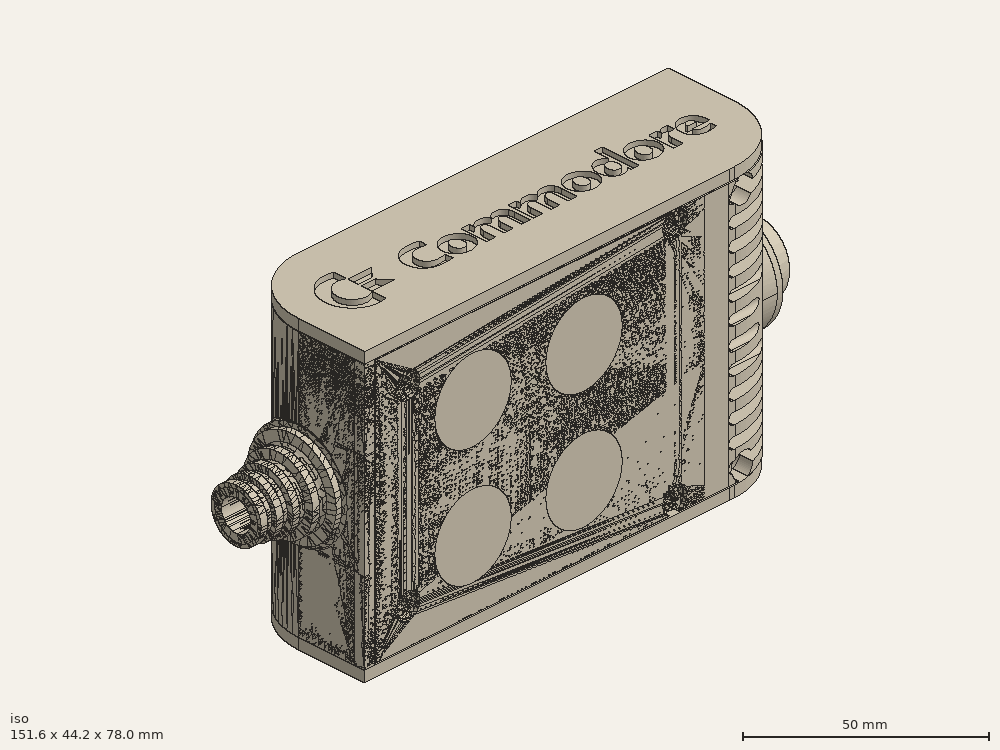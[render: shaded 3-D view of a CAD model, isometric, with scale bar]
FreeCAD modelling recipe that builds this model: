
FCSTD DOCUMENT  (FreeCAD 0.19R0.19.2)
Label: enclosure_217FCStd
License: All rights reserved
LicenseURL: http://en.wikipedia.org/wiki/All_rights_reserved
objects: Part::Revolution×152, Part::MultiFuse×146, Part::Feature×146, Sketcher::SketchObject×89, Part::Extrusion×74, Part::Cut×72, Part::Cylinder×70, Part::Fillet×58, Part::Box×36, App::MeasureDistance×4, Part::Chamfer×4, Part::FeaturePython×2, Image::ImagePlane×1, PartDesign::Body×1, Part::Mirroring×1
note: 851 computed .brp shape members not serialized (recipe doc carries the construction recipe); baked Part::Feature solids carry a one-line shape summary decoded from their .brp

FEATURE [Sketcher::SketchObject] Sketch  label="topSketch"
  FullyConstrained = true
  sketch-geometry (20):
    g0: LineSegment StartX=5.21097e-06 StartY=3 StartZ=0 EndX=5.21097e-06 EndY=19 EndZ=0
    g1: ArcOfCircle CenterX=19 CenterY=19 CenterZ=0 NormalX=0 NormalY=0 NormalZ=1 AngleXU=0 Radius=19 StartAngle=1.5708 EndAngle=3.14159
    g2: ArcOfCircle CenterX=19 CenterY=19 CenterZ=0 NormalX=0 NormalY=0 NormalZ=1 AngleXU=0 Radius=16 StartAngle=1.5708 EndAngle=3.14159
    g3: LineSegment StartX=114 StartY=35 StartZ=0 EndX=19 EndY=35 EndZ=0
    g4: LineSegment StartX=5.21097e-06 StartY=3 StartZ=0 EndX=5.21097e-06 EndY=0 EndZ=0
    g5: LineSegment StartX=3 StartY=0 StartZ=0 EndX=5.21097e-06 EndY=0 EndZ=0
    g6: LineSegment StartX=3 StartY=19 StartZ=0 EndX=3 EndY=0 EndZ=0
    g7: LineSegment StartX=19 StartY=38 StartZ=0 EndX=124 EndY=38 EndZ=0
    g8: Circle CenterX=119 CenterY=35 CenterZ=0 NormalX=0 NormalY=0 NormalZ=1 AngleXU=0 Radius=1
    g9: Circle CenterX=121 CenterY=35 CenterZ=0 NormalX=0 NormalY=0 NormalZ=1 AngleXU=0 Radius=1
    g10: Circle CenterX=121 CenterY=33 CenterZ=0 NormalX=0 NormalY=0 NormalZ=1 AngleXU=0 Radius=1
    g11: BSplineCurve PolesCount=3 KnotsCount=2 Degree=2 IsPeriodic=0
    g12: GeomPoint X=119 Y=35 Z=0
    g13: GeomPoint X=121 Y=33 Z=0
    g14: LineSegment StartX=119 StartY=35 StartZ=0 EndX=114 EndY=35 EndZ=0
    g15: ArcOfCircle CenterX=105 CenterY=19 CenterZ=0 NormalX=0 NormalY=0 NormalZ=1 AngleXU=0 Radius=19 StartAngle=5.7297 EndAngle=6.28319
    g16: ArcOfCircle CenterX=105 CenterY=19 CenterZ=0 NormalX=0 NormalY=0 NormalZ=1 AngleXU=0 Radius=16 StartAngle=5.60905 EndAngle=6.28319
    g17: LineSegment StartX=121 StartY=33 StartZ=0 EndX=121 EndY=19 EndZ=0
    g18: LineSegment StartX=124 StartY=38 StartZ=0 EndX=124 EndY=19 EndZ=0
    g19: LineSegment StartX=117.5 StartY=9.01251 StartZ=0 EndX=121.163 EndY=9.0125 EndZ=0
  constraints (46):
    c: Vertical(g0)
    c: Block(g0)
    c: Coincident(g1,g0)
    c: Block(g1)
    c: Coincident(g2,g1)
    c: Block(g2)
    c: Coincident(g3,g2)
    c: Horizontal(g3)
    c: Tangent(g3,g2)
    c: Coincident(g4,g0)
    c: Distance(g4) = 3
    c: Vertical(g4)
    c: Coincident(g5,g4)
    c: Horizontal(g5)
    c: Coincident(g6,g2)
    c: Coincident(g6,g5)
    c: Vertical(g6)
    c: Horizontal(g7)
    c: Distance(g7) = 105
    c: Coincident(g7,g1)
    c: Block(g3)
    c: Weight(g8) = 1
    c: Equal(g8,g9)
    c: Equal(g8,g10)
    c: InternalAlignment(g8,g11)
    c: InternalAlignment(g9,g11)
    c: InternalAlignment(g10,g11)
    c: InternalAlignment(g12,g11)
    c: InternalAlignment(g13,g11)
    c: Block(g11)
    c: Coincident(g14,g11)
    c: Coincident(g14,g3)
    c: Horizontal(g14)
    c: Block(g15)
    c: Coincident(g16,g15)
    c: Block(g16)
    c: Coincident(g17,g11)
    c: Coincident(g17,g16)
    c: Vertical(g17)
    c: Distance(g17) = 14
    c: Coincident(g18,g7)
    c: Coincident(g18,g15)
    c: Vertical(g18)
    c: Distance(g18) = 19
    c: Coincident(g19,g16)
    c: Coincident(g19,g15)
FEATURE [Sketcher::SketchObject] Sketch001  label="bottomSketch"
  FullyConstrained = true
  sketch-geometry (32):
    g0: LineSegment StartX=3.3 StartY=-6.03275e-07 StartZ=0 EndX=98 EndY=-6.03275e-07 EndZ=0
    g1: ArcOfCircle CenterX=98 CenterY=19 CenterZ=0 NormalX=0 NormalY=0 NormalZ=1 AngleXU=0 Radius=19 StartAngle=4.71239 EndAngle=5.71103
    g2: LineSegment StartX=6.3 StartY=8 StartZ=0 EndX=3.3 EndY=8 EndZ=0
    g3: LineSegment StartX=3.3 StartY=8 StartZ=0 EndX=3.3 EndY=-6.03275e-07 EndZ=0
    g4: ArcOfCircle CenterX=8.3 CenterY=5 CenterZ=0 NormalX=0 NormalY=0 NormalZ=1 AngleXU=0 Radius=2 StartAngle=3.14159 EndAngle=4.71239
    g5: LineSegment StartX=6.3 StartY=8 StartZ=0 EndX=6.3 EndY=5 EndZ=0
    g6: ArcOfCircle CenterX=98 CenterY=19 CenterZ=0 NormalX=0 NormalY=0 NormalZ=1 AngleXU=0 Radius=12.7 StartAngle=4.71239 EndAngle=6.28319
    g7: LineSegment StartX=94.7 StartY=3 StartZ=0 EndX=8.3 EndY=3 EndZ=0
    g8-g12: Circle x5 (B-spline internal-alignment scaffolding for g13; pole/knot coordinates omitted)
    g13: BSplineCurve PolesCount=5 KnotsCount=3 Degree=3 IsPeriodic=0
    g14: GeomPoint X=98 Y=6.3 Z=0
    g15: GeomPoint X=96.3938 Y=4.71946 Z=0
    g16: GeomPoint X=94.7 Y=3 Z=0
    g17-g23: Circle x7 (B-spline internal-alignment scaffolding for g24; pole/knot coordinates omitted)
    g24: BSplineCurve PolesCount=7 KnotsCount=5 Degree=3 IsPeriodic=0
    g25-g29: GeomPoint x5 (B-spline internal-alignment scaffolding for g24; pole/knot coordinates omitted)
    g30: ArcOfCircle CenterX=98 CenterY=19 CenterZ=0 NormalX=0 NormalY=0 NormalZ=1 AngleXU=0 Radius=15.7 StartAngle=5.81226 EndAngle=6.28319
    g31: LineSegment StartX=110.7 StartY=19 StartZ=0 EndX=113.7 EndY=19 EndZ=0
  constraints (41):
    c: Horizontal(g0)
    c: Coincident(g1,g0)
    c: Block(g1)
    c: Horizontal(g2)
    c: Distance(g2) = 3
    c: Coincident(g3,g2)
    c: Vertical(g3)
    c: Coincident(g3,g0)
    c: Block(g4)
    c: Block(g2)
    c: Coincident(g5,g2)
    c: Coincident(g5,g4)
    c: Vertical(g5)
    c: Coincident(g6,g1)
    c: Block(g6)
    c: Coincident(g7,g4)
    c: Horizontal(g7)
    c: Block(g0)
    c: Block(g7)
    c: Block(g3)
    c: Coincident(g13,g6)
    c: Weight(g8) = 1
    c: Equal(g8, g9-g12) x4
    c: Coincident(g13,g7)
    c: InternalAlignment(g8-g12 -> g13) x5
    c: InternalAlignment(g14,g13)
    c: InternalAlignment(g15,g13)
    c: InternalAlignment(g16,g13)
    c: Block(g13)
    c: Weight(g17) = 1
    c: Equal(g17, g18-g23) x6
    c: Coincident(g24,g1)
    c: InternalAlignment(g17-g23 -> g24) x7
    c: InternalAlignment(g25-g29 -> g24) x5
    c: Block(g24)
    c: Coincident(g30,g24)
    c: Coincident(g31,g6)
    c: Coincident(g31,g30)
    c: Horizontal(g31)
    c: Block(g31)
    c: Block(g30)
FEATURE [Part::Extrusion] Extrude  label="top"
  Base = -> Sketch
  Dir = (0,0,1)
  DirMode = 2
  FaceMakerClass = Part::FaceMakerBullseye
  LengthFwd = 72
  LengthRev = 0
  Solid = true
  Symmetric = false
FEATURE [Part::Extrusion] Extrude001  label="bottom"
  Base = -> Sketch001
  Dir = (0,0,1)
  DirMode = 2
  FaceMakerClass = Part::FaceMakerBullseye
  LengthFwd = 71.4
  LengthRev = 0
  Placement = pos=(0,0,0.3) rot=(0,0,1;0rad)
  Solid = true
  Symmetric = false
FEATURE [Sketcher::SketchObject] Sketch002  label="topSketch001"
  FullyConstrained = true
  sketch-geometry (8):
    g0: ArcOfCircle CenterX=19 CenterY=19.0975 CenterZ=0 NormalX=0 NormalY=0 NormalZ=1 AngleXU=0 Radius=18.9025 StartAngle=1.5708 EndAngle=3.14674
    g1: LineSegment StartX=0.0977805 StartY=19.0003 StartZ=0 EndX=0.0977805 EndY=0.000251602 EndZ=0
    g2: LineSegment StartX=19 StartY=38 StartZ=0 EndX=124 EndY=38 EndZ=0
    g3: LineSegment StartX=0.0977805 StartY=0.000251602 StartZ=0 EndX=105.098 EndY=0.000251602 EndZ=0
    g4: LineSegment StartX=124 StartY=38 StartZ=0 EndX=125.616 EndY=38 EndZ=0
    g5: LineSegment StartX=105.098 StartY=0.000251602 StartZ=0 EndX=106.713 EndY=0.000251602 EndZ=0
    g6: ArcOfCircle CenterX=106.616 CenterY=19 CenterZ=0 NormalX=0 NormalY=0 NormalZ=1 AngleXU=0 Radius=19 StartAngle=4.71754 EndAngle=6.28319
    g7: LineSegment StartX=125.616 StartY=38 StartZ=0 EndX=125.616 EndY=19 EndZ=0
  constraints (21):
    c: Block(g0)
    c: Coincident(g1,g0)
    c: Vertical(g1)
    c: Horizontal(g2)
    c: Distance(g2) = 105
    c: Coincident(g2,g0)
    c: Distance(g1) = 19
    c: Coincident(g3,g1)
    c: Horizontal(g3)
    c: Distance(g3) = 105
    c: Coincident(g4,g2)
    c: Horizontal(g4)
    c: Distance(g4) = 1.61553
    c: Horizontal(g5)
    c: Equal(g4,g5) = 1.61553
    c: Coincident(g5,g3)
    c: Block(g6)
    c: Coincident(g6,g5)
    c: Coincident(g7,g4)
    c: Coincident(g7,g6)
    c: Vertical(g7)
FEATURE [Part::Extrusion] Extrude002  label="sideA"
  Base = -> Sketch002
  Dir = (0,0,1)
  DirMode = 2
  FaceMakerClass = Part::FaceMakerBullseye
  LengthFwd = 3
  LengthRev = 0
  Placement = pos=(0,0,-3) rot=(0,0,1;0rad)
  Solid = true
  Symmetric = false
FEATURE [Sketcher::SketchObject] Sketch003  label="topSketch002"
  FullyConstrained = true
  sketch-geometry (6):
    g0: LineSegment StartX=19 StartY=38 StartZ=0 EndX=117 EndY=38 EndZ=0
    g1: ArcOfCircle CenterX=19 CenterY=19 CenterZ=0 NormalX=0 NormalY=0 NormalZ=1 AngleXU=0 Radius=19 StartAngle=1.5708 EndAngle=3.14159
    g2: LineSegment StartX=117 StartY=38 StartZ=0 EndX=117 EndY=19 EndZ=0
    g3: LineSegment StartX=98 StartY=1.0161e-12 StartZ=0 EndX=5.22862e-06 EndY=1.0161e-12 EndZ=0
    g4: LineSegment StartX=5.22862e-06 StartY=19 StartZ=0 EndX=5.22862e-06 EndY=1.0161e-12 EndZ=0
    g5: ArcOfCircle CenterX=98 CenterY=19 CenterZ=0 NormalX=0 NormalY=0 NormalZ=1 AngleXU=0 Radius=19 StartAngle=4.71239 EndAngle=6.28319
  constraints (16):
    c: Horizontal(g0)
    c: Distance(g0) = 98
    c: Coincident(g1,g0)
    c: Block(g1)
    c: Coincident(g2,g0)
    c: Vertical(g2)
    c: Distance(g2) = 19
    c: Horizontal(g3)
    c: Coincident(g4,g1)
    c: Vertical(g4)
    c: Coincident(g3,g4)
    c: Block(g3)
    c: Coincident(g5,g2)
    c: Coincident(g5,g3)
    c: Block(g0)
    c: Block(g5)
FEATURE [Sketcher::SketchObject] Sketch004
  FullyConstrained = true
  MapMode = 3
  Placement = pos=(0,0,0) rot=(1,0,0;1.5708rad)
  Support = -> [Extrude]
  sketch-geometry (8):
    g0: Circle CenterX=80.351 CenterY=-67.6202 CenterZ=0 NormalX=0 NormalY=0 NormalZ=1 AngleXU=0 Radius=2
    g1: Circle CenterX=80.351 CenterY=-67.6202 CenterZ=0 NormalX=0 NormalY=0 NormalZ=1 AngleXU=0 Radius=3
    g2: Circle CenterX=80.351 CenterY=-4.92017 CenterZ=0 NormalX=0 NormalY=0 NormalZ=1 AngleXU=0 Radius=2
    g3: Circle CenterX=80.351 CenterY=-4.92017 CenterZ=0 NormalX=0 NormalY=0 NormalZ=1 AngleXU=0 Radius=3
    g4: Circle CenterX=23.851 CenterY=-4.92017 CenterZ=0 NormalX=0 NormalY=0 NormalZ=1 AngleXU=0 Radius=2
    g5: Circle CenterX=23.851 CenterY=-4.92017 CenterZ=0 NormalX=0 NormalY=0 NormalZ=1 AngleXU=0 Radius=3
    g6: Circle CenterX=23.851 CenterY=-67.6202 CenterZ=0 NormalX=0 NormalY=0 NormalZ=1 AngleXU=0 Radius=2
    g7: Circle CenterX=23.851 CenterY=-67.6202 CenterZ=0 NormalX=0 NormalY=0 NormalZ=1 AngleXU=0 Radius=3
  constraints (8):
    c: Block(g3)
    c: Block(g2)
    c: Block(g1)
    c: Block(g0)
    c: Block(g6)
    c: Block(g7)
    c: Block(g4)
    c: Block(g5)
FEATURE [Part::Extrusion] Extrude004
  Base = -> Sketch004
  Dir = (0,-1,2e-16)
  DirMode = 2
  FaceMakerClass = Part::FaceMakerBullseye
  LengthFwd = 6
  LengthRev = 0
  Placement = pos=(0,9,0) rot=(0,0,1;0rad)
  Solid = true
  Symmetric = false
FEATURE [Sketcher::SketchObject] Sketch005
  FullyConstrained = true
  MapMode = 3
  Placement = pos=(0,0,0) rot=(1,0,0;1.5708rad)
  Support = -> [Extrude]
  sketch-geometry (8):
    g0: Circle CenterX=80.351 CenterY=-67.6202 CenterZ=0 NormalX=0 NormalY=0 NormalZ=1 AngleXU=0 Radius=3
    g1: Circle CenterX=80.351 CenterY=-4.92017 CenterZ=0 NormalX=0 NormalY=0 NormalZ=1 AngleXU=0 Radius=3
    g2: Circle CenterX=23.851 CenterY=-4.92017 CenterZ=0 NormalX=0 NormalY=0 NormalZ=1 AngleXU=0 Radius=3
    g3: Circle CenterX=23.851 CenterY=-67.6202 CenterZ=0 NormalX=0 NormalY=0 NormalZ=1 AngleXU=0 Radius=3
    g4: Circle CenterX=23.851 CenterY=-67.6202 CenterZ=0 NormalX=0 NormalY=0 NormalZ=1 AngleXU=0 Radius=5
    g5: Circle CenterX=80.351 CenterY=-67.6202 CenterZ=0 NormalX=0 NormalY=0 NormalZ=1 AngleXU=0 Radius=5
    g6: Circle CenterX=23.851 CenterY=-4.92017 CenterZ=0 NormalX=0 NormalY=0 NormalZ=1 AngleXU=0 Radius=5
    g7: Circle CenterX=80.351 CenterY=-4.92017 CenterZ=0 NormalX=0 NormalY=0 NormalZ=1 AngleXU=0 Radius=5
  constraints (8):
    c: Block(g1)
    c: Block(g0)
    c: Block(g3)
    c: Block(g2)
    c: Block(g5)
    c: Block(g4)
    c: Block(g6)
    c: Block(g7)
FEATURE [Part::Extrusion] Extrude005
  Base = -> Sketch005
  Dir = (0,-1,2e-16)
  DirMode = 2
  FaceMakerClass = Part::FaceMakerBullseye
  LengthFwd = 2
  LengthRev = 0
  Solid = true
  Symmetric = false
FEATURE [Sketcher::SketchObject] Sketch006
  FullyConstrained = true
  MapMode = 3
  Placement = pos=(0,0,0) rot=(1,0,0;1.5708rad)
  sketch-geometry (8):
    g0: Circle CenterX=80.351 CenterY=-67.6202 CenterZ=0 NormalX=0 NormalY=0 NormalZ=1 AngleXU=0 Radius=3
    g1: Circle CenterX=80.351 CenterY=-4.92017 CenterZ=0 NormalX=0 NormalY=0 NormalZ=1 AngleXU=0 Radius=3
    g2: Circle CenterX=23.851 CenterY=-4.92017 CenterZ=0 NormalX=0 NormalY=0 NormalZ=1 AngleXU=0 Radius=3
    g3: Circle CenterX=23.851 CenterY=-67.6202 CenterZ=0 NormalX=0 NormalY=0 NormalZ=1 AngleXU=0 Radius=3
    g4: Circle CenterX=23.851 CenterY=-67.6202 CenterZ=0 NormalX=0 NormalY=0 NormalZ=1 AngleXU=0 Radius=5
    g5: Circle CenterX=80.351 CenterY=-67.6202 CenterZ=0 NormalX=0 NormalY=0 NormalZ=1 AngleXU=0 Radius=5
    g6: Circle CenterX=23.851 CenterY=-4.92017 CenterZ=0 NormalX=0 NormalY=0 NormalZ=1 AngleXU=0 Radius=5
    g7: Circle CenterX=80.351 CenterY=-4.92017 CenterZ=0 NormalX=0 NormalY=0 NormalZ=1 AngleXU=0 Radius=5
  constraints (8):
    c: Block(g1)
    c: Block(g0)
    c: Block(g3)
    c: Block(g2)
    c: Block(g5)
    c: Block(g4)
    c: Block(g6)
    c: Block(g7)
FEATURE [Part::Extrusion] Extrude007
  Base = -> Sketch006
  Dir = (0,-1,2e-16)
  DirMode = 2
  FaceMakerClass = Part::FaceMakerBullseye
  LengthFwd = 2
  LengthRev = 0
  Solid = true
  Symmetric = false
FEATURE [Part::Fillet] Fillet
  Base = -> Extrude007
  Edges = 4 edges r=1.99: [Edge6,Edge12,Edge18,Edge24]
FEATURE [Part::Cut] Cut
  Base = -> Extrude005
  Placement = pos=(0,5,0) rot=(0,0,1;0rad)
  Tool = -> Fillet
FEATURE [Part::MultiFuse] Fusion  label="pCBScrews"
  Placement = pos=(-2.5,0,72.3) rot=(0,0,1;0rad)
  Shapes = -> [Extrude004,Cut]
FEATURE [App::MeasureDistance] Distance  label="Distance: 0.69 mm"
  Distance = 0.685967
  P1 = (24.0138,2.9647,0.3)
  P2 = (23.8901,3,-0.373787)
FEATURE [App::MeasureDistance] Distance001  label="Distance: 0.53 mm"
  Distance = 0.533607
  P1 = (80.2939,3,72.2334)
  P2 = (80.281,2.99661,71.7)
FEATURE [Part::Fillet] Fillet001
  Base = -> Extrude001
  Edges = 1 edges r=2.4: [Edge17]
FEATURE [Part::Fillet] Fillet002  label="bottom001"
  Base = -> Fillet001
  Edges = 1 edges r=2.4: [Edge36]
FEATURE [Part::Fillet] Fillet003  label="top001"
  Base = -> Extrude
  Edges = 1 edges r=2: [Edge1]
FEATURE [Sketcher::SketchObject] Sketch007
  FullyConstrained = true
  sketch-geometry (16):
    g0: LineSegment StartX=4 StartY=0 StartZ=0 EndX=4 EndY=2.4 EndZ=0
    g1: LineSegment StartX=4 StartY=2.4 StartZ=0 EndX=7 EndY=2.4 EndZ=0
    g2: LineSegment StartX=4 StartY=0 StartZ=0 EndX=5.7 EndY=0 EndZ=0
    g3: LineSegment StartX=5.7 StartY=0 StartZ=0 EndX=5.7 EndY=-5.6 EndZ=0
    g4-g8: Circle x5 (B-spline internal-alignment scaffolding for g9; pole/knot coordinates omitted)
    g9: BSplineCurve PolesCount=5 KnotsCount=3 Degree=3 IsPeriodic=0
    g10: GeomPoint X=7 Y=2.4 Z=0
    g11: GeomPoint X=10.4582 Y=-1.55472 Z=0
    g12: GeomPoint X=14 Y=-5.6 Z=0
    g13: LineSegment StartX=14 StartY=-5.6 StartZ=0 EndX=14 EndY=-14.1 EndZ=0
    g14: LineSegment StartX=14 StartY=-14.1 StartZ=0 EndX=6.5 EndY=-14.1 EndZ=0
    g15: LineSegment StartX=5.7 StartY=-5.6 StartZ=0 EndX=6.5 EndY=-14.1 EndZ=0
  constraints (28):
    c: Distance(g0) = 2.4
    c: Vertical(g0)
    c: Block(g0)
    c: Coincident(g1,g0)
    c: Horizontal(g1)
    c: Distance(g1) = 3
    c: Coincident(g2,g0)
    c: Horizontal(g2)
    c: Distance(g2) = 1.7
    c: Coincident(g3,g2)
    c: Vertical(g3)
    c: Distance(g3) = 5.6
    c: Coincident(g9,g1)
    c: Weight(g4) = 1
    c: Equal(g4, g5-g8) x4
    c: InternalAlignment(g4-g8 -> g9) x5
    c: InternalAlignment(g10,g9)
    c: InternalAlignment(g11,g9)
    c: InternalAlignment(g12,g9)
    c: Block(g9)
    c: Coincident(g13,g9)
    c: Vertical(g13)
    c: Distance(g13) = 8.5
    c: Coincident(g14,g13)
    c: Horizontal(g14)
    c: Distance(g14) = 7.5
    c: Coincident(g15,g3)
    c: Coincident(g15,g14)
FEATURE [Part::Feature] Face
  shape: bbox 10 x 16.5 x 2e-07 mm, 1 faces, 0 solids (baked)
FEATURE [Part::Revolution] Revolve  label="plugHousing"
  Angle = 360
  Axis = (0,1,0)
  Base = (0,0,0)
  FaceMakerClass = Part::FaceMakerBullseye
  Placement = pos=(0,0,36.15) rot=(0,0,1;0rad)
  Solid = false
  Source = -> Face
  Symmetric = false
FEATURE [Part::Feature] Face001
  shape: bbox 10 x 16.5 x 2e-07 mm, 1 faces, 0 solids (baked)
FEATURE [Part::Revolution] Revolve001  label="plugHousing001"
  Angle = 360
  Axis = (0,1,0)
  Base = (0,0,0)
  FaceMakerClass = Part::FaceMakerBullseye
  Placement = pos=(0,0,36.15) rot=(0,0,1;0rad)
  Solid = false
  Source = -> Face001
  Symmetric = false
FEATURE [Part::MultiFuse] Fusion001  label="plugHousing002"
  Placement = pos=(0,0,0) rot=(0,0,1;1.5708rad)
  Shapes = -> [Revolve001,Revolve]
FEATURE [Part::Feature] Face002
  shape: bbox 10 x 16.5 x 2e-07 mm, 1 faces, 0 solids (baked)
FEATURE [Part::Revolution] Revolve003  label="plugHousing005"
  Angle = 360
  Axis = (0,1,0)
  Base = (0,0,0)
  FaceMakerClass = Part::FaceMakerBullseye
  Placement = pos=(0,0,36.15) rot=(0,0,1;0rad)
  Solid = false
  Source = -> Face002
  Symmetric = false
FEATURE [Part::Feature] Face003
  shape: bbox 10 x 16.5 x 2e-07 mm, 1 faces, 0 solids (baked)
FEATURE [Part::Revolution] Revolve002  label="plugHousing003"
  Angle = 360
  Axis = (0,1,0)
  Base = (0,0,0)
  FaceMakerClass = Part::FaceMakerBullseye
  Placement = pos=(0,0,36.15) rot=(0,0,1;0rad)
  Solid = false
  Source = -> Face003
  Symmetric = false
FEATURE [Part::MultiFuse] Fusion002  label="plugHousing004"
  Placement = pos=(0,0,0) rot=(0,0,1;1.5708rad)
  Shapes = -> [Revolve002,Revolve003]
FEATURE [Part::MultiFuse] Fusion003  label="plugHousing006"
  Placement = pos=(0,19,0) rot=(0,0,1;3.14159rad)
  Shapes = -> [Fusion002,Fusion001]
FEATURE [Part::Feature] Face004
  shape: bbox 10 x 16.5 x 2e-07 mm, 1 faces, 0 solids (baked)
FEATURE [Part::Revolution] Revolve006  label="plugHousing010"
  Angle = 360
  Axis = (0,1,0)
  Base = (0,0,0)
  FaceMakerClass = Part::FaceMakerBullseye
  Placement = pos=(0,0,36.15) rot=(0,0,1;0rad)
  Solid = false
  Source = -> Face004
  Symmetric = false
FEATURE [Part::Feature] Face005
  shape: bbox 10 x 16.5 x 2e-07 mm, 1 faces, 0 solids (baked)
FEATURE [Part::Revolution] Revolve007  label="plugHousing011"
  Angle = 360
  Axis = (0,1,0)
  Base = (0,0,0)
  FaceMakerClass = Part::FaceMakerBullseye
  Placement = pos=(0,0,36.15) rot=(0,0,1;0rad)
  Solid = false
  Source = -> Face005
  Symmetric = false
FEATURE [Part::Feature] Face006
  shape: bbox 10 x 16.5 x 2e-07 mm, 1 faces, 0 solids (baked)
FEATURE [Part::Revolution] Revolve004  label="plugHousing007"
  Angle = 360
  Axis = (0,1,0)
  Base = (0,0,0)
  FaceMakerClass = Part::FaceMakerBullseye
  Placement = pos=(0,0,36.15) rot=(0,0,1;0rad)
  Solid = false
  Source = -> Face006
  Symmetric = false
FEATURE [Part::MultiFuse] Fusion004  label="plugHousing009"
  Placement = pos=(0,0,0) rot=(0,0,1;1.5708rad)
  Shapes = -> [Revolve004,Revolve007]
FEATURE [Part::Feature] Face007
  shape: bbox 10 x 16.5 x 2e-07 mm, 1 faces, 0 solids (baked)
FEATURE [Part::Revolution] Revolve005  label="plugHousing008"
  Angle = 360
  Axis = (0,1,0)
  Base = (0,0,0)
  FaceMakerClass = Part::FaceMakerBullseye
  Placement = pos=(0,0,36.15) rot=(0,0,1;0rad)
  Solid = false
  Source = -> Face007
  Symmetric = false
FEATURE [Part::MultiFuse] Fusion005  label="plugHousing012"
  Placement = pos=(0,0,0) rot=(0,0,1;1.5708rad)
  Shapes = -> [Revolve006,Revolve005]
FEATURE [Part::MultiFuse] Fusion006  label="plugHousing013"
  Placement = pos=(0,19,0) rot=(0,0,1;3.14159rad)
  Shapes = -> [Fusion005,Fusion004]
FEATURE [Part::MultiFuse] Fusion007  label="plugHousing014"
  Placement = pos=(122.621,0,-0.15) rot=(0,0,1;0rad)
  Shapes = -> [Fusion003,Fusion006]
FEATURE [Part::Cylinder] Cylinder002
  Angle = 360
  AttacherType = Attacher::AttachEngine3D
  Height = 20
  Placement = pos=(0,0,36.15) rot=(0,0,1;0rad)
  Radius = 4
FEATURE [Part::Cylinder] Cylinder003
  Angle = 360
  AttacherType = Attacher::AttachEngine3D
  Height = 10
  Placement = pos=(0,0,36.15) rot=(0,0,1;0rad)
  Radius = 4
FEATURE [Part::MultiFuse] Fusion009  label="removeToCreateHoleForPlugHousing"
  Placement = pos=(70,19,36.15) rot=(0,1,0;1.5708rad)
  Shapes = -> [Cylinder002,Cylinder003]
FEATURE [Part::Cylinder] Cylinder004
  Angle = 360
  AttacherType = Attacher::AttachEngine3D
  Height = 20
  Placement = pos=(0,0,36.15) rot=(0,0,1;0rad)
  Radius = 4
FEATURE [Part::Cylinder] Cylinder005
  Angle = 360
  AttacherType = Attacher::AttachEngine3D
  Height = 10
  Placement = pos=(0,0,36.15) rot=(0,0,1;0rad)
  Radius = 4
FEATURE [Part::MultiFuse] Fusion010  label="removeToCreateHoleForPlugHousing001"
  Placement = pos=(70,19,36.15) rot=(0,1,0;1.5708rad)
  Shapes = -> [Cylinder004,Cylinder005]
FEATURE [Part::Cut] Cut001
  Base = -> Fillet003
  Tool = -> Fusion010
FEATURE [Part::Cut] Cut002  label="Bottom"
  Base = -> Fillet002
  Tool = -> Fusion009
FEATURE [Part::Feature] Face008
  shape: bbox 10 x 16.5 x 2e-07 mm, 1 faces, 0 solids (baked)
FEATURE [Part::Revolution] Revolve011  label="plugHousing021"
  Angle = 360
  Axis = (0,1,0)
  Base = (0,0,0)
  FaceMakerClass = Part::FaceMakerBullseye
  Placement = pos=(0,0,36.15) rot=(0,0,1;0rad)
  Solid = false
  Source = -> Face008
  Symmetric = false
FEATURE [Part::Feature] Face009
  shape: bbox 10 x 16.5 x 2e-07 mm, 1 faces, 0 solids (baked)
FEATURE [Part::Revolution] Revolve012  label="plugHousing022"
  Angle = 360
  Axis = (0,1,0)
  Base = (0,0,0)
  FaceMakerClass = Part::FaceMakerBullseye
  Placement = pos=(0,0,36.15) rot=(0,0,1;0rad)
  Solid = false
  Source = -> Face009
  Symmetric = false
FEATURE [Part::Feature] Face010 .. Face013  x4 (patterned run collapsed; names and placements below)
  shape: bbox 10 x 16.5 x 2e-07 mm, 1 faces, 0 solids (baked)
FEATURE [Part::Revolution] Revolve015  label="plugHousing027"
  Angle = 360
  Axis = (0,1,0)
  Base = (0,0,0)
  FaceMakerClass = Part::FaceMakerBullseye
  Placement = pos=(0,0,36.15) rot=(0,0,1;0rad)
  Solid = false
  Source = -> Face013
  Symmetric = false
FEATURE [Part::Feature] Face014
  shape: bbox 10 x 16.5 x 2e-07 mm, 1 faces, 0 solids (baked)
FEATURE [Part::Feature] Face015
  shape: bbox 10 x 16.5 x 2e-07 mm, 1 faces, 0 solids (baked)
FEATURE [Part::Feature] Face016
  shape: bbox 10 x 16.5 x 2e-07 mm, 1 faces, 0 solids (baked)
FEATURE [Part::Revolution] Revolve019  label="plugHousing033"
  Angle = 360
  Axis = (0,1,0)
  Base = (0,0,0)
  FaceMakerClass = Part::FaceMakerBullseye
  Placement = pos=(0,0,36.15) rot=(0,0,1;0rad)
  Solid = false
  Source = -> Face016
  Symmetric = false
FEATURE [Part::Feature] Face017
  shape: bbox 10 x 16.5 x 2e-07 mm, 1 faces, 0 solids (baked)
FEATURE [Part::Revolution] Revolve020  label="plugHousing034"
  Angle = 360
  Axis = (0,1,0)
  Base = (0,0,0)
  FaceMakerClass = Part::FaceMakerBullseye
  Placement = pos=(0,0,36.15) rot=(0,0,1;0rad)
  Solid = false
  Source = -> Face017
  Symmetric = false
FEATURE [Part::Feature] Face018
  shape: bbox 10 x 16.5 x 2e-07 mm, 1 faces, 0 solids (baked)
FEATURE [Part::Revolution] Revolve016  label="plugHousing030"
  Angle = 360
  Axis = (0,1,0)
  Base = (0,0,0)
  FaceMakerClass = Part::FaceMakerBullseye
  Placement = pos=(0,0,36.15) rot=(0,0,1;0rad)
  Solid = false
  Source = -> Face018
  Symmetric = false
FEATURE [Part::MultiFuse] Fusion020  label="plugHousing038"
  Placement = pos=(0,0,0) rot=(0,0,1;1.5708rad)
  Shapes = -> [Revolve016,Revolve020]
FEATURE [Part::Feature] Face019
  shape: bbox 10 x 16.5 x 2e-07 mm, 1 faces, 0 solids (baked)
FEATURE [Part::Feature] Face020
  shape: bbox 10 x 16.5 x 2e-07 mm, 1 faces, 0 solids (baked)
FEATURE [Part::Revolution] Revolve017  label="plugHousing031"
  Angle = 360
  Axis = (0,1,0)
  Base = (0,0,0)
  FaceMakerClass = Part::FaceMakerBullseye
  Placement = pos=(0,0,36.15) rot=(0,0,1;0rad)
  Solid = false
  Source = -> Face020
  Symmetric = false
FEATURE [Part::MultiFuse] Fusion021  label="plugHousing039"
  Placement = pos=(0,0,0) rot=(0,0,1;1.5708rad)
  Shapes = -> [Revolve019,Revolve017]
FEATURE [Part::MultiFuse] Fusion023  label="plugHousing041"
  Placement = pos=(0,19,0) rot=(0,0,1;3.14159rad)
  Shapes = -> [Fusion021,Fusion020]
FEATURE [Part::Revolution] Revolve022  label="plugHousing043"
  Angle = 360
  Axis = (0,1,0)
  Base = (0,0,0)
  FaceMakerClass = Part::FaceMakerBullseye
  Placement = pos=(0,0,36.15) rot=(0,0,1;0rad)
  Solid = false
  Source = -> Face019
  Symmetric = false
FEATURE [Part::Feature] Face021
  shape: bbox 10 x 16.5 x 2e-07 mm, 1 faces, 0 solids (baked)
FEATURE [Part::Revolution] Revolve023  label="plugHousing044"
  Angle = 360
  Axis = (0,1,0)
  Base = (0,0,0)
  FaceMakerClass = Part::FaceMakerBullseye
  Placement = pos=(0,0,36.15) rot=(0,0,1;0rad)
  Solid = false
  Source = -> Face021
  Symmetric = false
FEATURE [Part::Feature] Face022
  shape: bbox 10 x 16.5 x 2e-07 mm, 1 faces, 0 solids (baked)
FEATURE [Part::Revolution] Revolve018  label="plugHousing032"
  Angle = 360
  Axis = (0,1,0)
  Base = (0,0,0)
  FaceMakerClass = Part::FaceMakerBullseye
  Placement = pos=(0,0,36.15) rot=(0,0,1;0rad)
  Solid = false
  Source = -> Face022
  Symmetric = false
FEATURE [Part::MultiFuse] Fusion022  label="plugHousing040"
  Placement = pos=(0,0,0) rot=(0,0,1;1.5708rad)
  Shapes = -> [Revolve018,Revolve023]
FEATURE [Part::Feature] Face023
  shape: bbox 10 x 16.5 x 2e-07 mm, 1 faces, 0 solids (baked)
FEATURE [Part::Revolution] Revolve021  label="plugHousing035"
  Angle = 360
  Axis = (0,1,0)
  Base = (0,0,0)
  FaceMakerClass = Part::FaceMakerBullseye
  Placement = pos=(0,0,36.15) rot=(0,0,1;0rad)
  Solid = false
  Source = -> Face023
  Symmetric = false
FEATURE [Part::MultiFuse] Fusion018  label="plugHousing036"
  Placement = pos=(0,0,0) rot=(0,0,1;1.5708rad)
  Shapes = -> [Revolve022,Revolve021]
FEATURE [Part::MultiFuse] Fusion019  label="plugHousing037"
  Placement = pos=(0,19,0) rot=(0,0,1;3.14159rad)
  Shapes = -> [Fusion018,Fusion022]
FEATURE [Part::MultiFuse] Fusion024  label="plugHousing042"
  Placement = pos=(122.621,0,-0.15) rot=(0,0,1;0rad)
  Shapes = -> [Fusion023,Fusion019]
FEATURE [Part::Cylinder] Cylinder006
  Angle = 360
  AttacherType = Attacher::AttachEngine3D
  Height = 20
  Placement = pos=(0,0,36.15) rot=(0,0,1;0rad)
  Radius = 14.3
FEATURE [Part::Cylinder] Cylinder007
  Angle = 360
  AttacherType = Attacher::AttachEngine3D
  Height = 10
  Placement = pos=(0,0,36.15) rot=(0,0,1;0rad)
  Radius = 4
FEATURE [Part::MultiFuse] Fusion026  label="removeToCreteHoleForPlugHousing"
  Placement = pos=(70,19,36) rot=(0,1,0;1.5708rad)
  Shapes = -> [Cylinder006,Cylinder007]
FEATURE [Part::Box] Box001  label="Cube001"
  AttacherType = Attacher::AttachEngine3D
  Height = 28
  Length = 3
  Placement = pos=(110.7,19,22) rot=(0,0,1;0rad)
  Width = 15.7
FEATURE [Part::Cut] Cut003  label="top002"
  Base = -> Cut001
  Tool = -> Fusion007
FEATURE [Part::Revolution] Revolve008  label="plugHousing015"
  Angle = 360
  Axis = (0,1,0)
  Base = (0,0,0)
  FaceMakerClass = Part::FaceMakerBullseye
  Placement = pos=(0,0,36.15) rot=(0,0,1;0rad)
  Solid = false
  Source = -> Face010
  Symmetric = false
FEATURE [Part::MultiFuse] Fusion013  label="plugHousing020"
  Placement = pos=(0,0,0) rot=(0,0,1;1.5708rad)
  Shapes = -> [Revolve008,Revolve012]
FEATURE [Part::Cut] Cut004  label="top003"
  Base = -> Cut003
  Placement = pos=(1,0,0) rot=(0,0,1;0rad)
  Tool = -> Fusion026
FEATURE [Part::Cylinder] Cylinder008
  Angle = 360
  AttacherType = Attacher::AttachEngine3D
  Height = 20
  Placement = pos=(0,0,36.15) rot=(0,0,1;0rad)
  Radius = 10.3
FEATURE [Part::Cylinder] Cylinder009
  Angle = 360
  AttacherType = Attacher::AttachEngine3D
  Height = 10
  Placement = pos=(0,0,36.15) rot=(0,0,1;0rad)
  Radius = 4
FEATURE [Part::MultiFuse] Fusion027  label="removeToCreteHoleForPlugHousing001"
  Placement = pos=(70,19,36) rot=(0,1,0;1.5708rad)
  Shapes = -> [Cylinder008,Cylinder009]
FEATURE [Part::Cut] Cut005  label="plugHousingTab"
  Base = -> Box001
  Tool = -> Fusion027
FEATURE [Part::MultiFuse] Fusion028  label="plugHousing045"
  Shapes = -> [Fusion024,Cut005]
FEATURE [Part::Box] Box002  label="Cube002"
  AttacherType = Attacher::AttachEngine3D
  Height = 28.8
  Length = 3
  Placement = pos=(107.3,28,21.6) rot=(0,0,1;0rad)
  Width = 7
FEATURE [Part::Box] Box003  label="Cube003"
  AttacherType = Attacher::AttachEngine3D
  Height = 3
  Length = 6.4
  Placement = pos=(107.3,28,18.6) rot=(0,0,1;0rad)
  Width = 7
FEATURE [Part::Box] Box004  label="Cube004"
  AttacherType = Attacher::AttachEngine3D
  Height = 3
  Length = 6.4
  Placement = pos=(107.3,28,50.4) rot=(0,0,1;0rad)
  Width = 7
FEATURE [Part::MultiFuse] Fusion029  label="plugHousingBracketHolder"
  Shapes = -> [Box004,Box002,Box003]
FEATURE [Part::Cylinder] Cylinder010
  Angle = 360
  AttacherType = Attacher::AttachEngine3D
  Height = 20
  Placement = pos=(0,0,36.15) rot=(0,0,1;0rad)
  Radius = 14.3
FEATURE [Part::Cylinder] Cylinder011
  Angle = 360
  AttacherType = Attacher::AttachEngine3D
  Height = 10
  Placement = pos=(0,0,36.15) rot=(0,0,1;0rad)
  Radius = 4
FEATURE [Part::MultiFuse] Fusion030  label="removeToCreteHoleForPlugHousing002"
  Placement = pos=(70,19,36) rot=(0,1,0;1.5708rad)
  Shapes = -> [Cylinder010,Cylinder011]
FEATURE [Part::Cut] Cut006  label="plugHousingBracketHolder001"
  Base = -> Fusion029
  Tool = -> Fusion030
FEATURE [Part::Cylinder] Cylinder012
  Angle = 360
  AttacherType = Attacher::AttachEngine3D
  Height = 20
  Placement = pos=(0,0,36.15) rot=(0,0,1;0rad)
  Radius = 7
FEATURE [Part::Cylinder] Cylinder013
  Angle = 360
  AttacherType = Attacher::AttachEngine3D
  Height = 10
  Placement = pos=(0,0,36.15) rot=(0,0,1;0rad)
  Radius = 4
FEATURE [Part::MultiFuse] Fusion032  label="removeToCreteHoleForPlugHousing003"
  Placement = pos=(70,19,36) rot=(0,1,0;1.5708rad)
  Shapes = -> [Cylinder012,Cylinder013]
FEATURE [Part::Cut] Cut007  label="bottom002"
  Base = -> Cut002
  Tool = -> Fusion032
FEATURE [Sketcher::SketchObject] Sketch008
  FullyConstrained = true
  sketch-geometry (54):
    g0: LineSegment StartX=-4.2 StartY=0 StartZ=0 EndX=-6.2 EndY=0 EndZ=0
    g1: LineSegment StartX=-14 StartY=-18 StartZ=0 EndX=-14 EndY=-26.5 EndZ=0
    g2: LineSegment StartX=-4.2 StartY=0 StartZ=0 EndX=-4.2 EndY=-13.4877 EndZ=0
    g3: Circle CenterX=-4.2 CenterY=-13.4877 CenterZ=0 NormalX=0 NormalY=0 NormalZ=1 AngleXU=0 Radius=1
    g4: Circle CenterX=-4.2 CenterY=-26.5 CenterZ=0 NormalX=0 NormalY=0 NormalZ=1 AngleXU=0 Radius=1
    g5: Circle CenterX=-8.2 CenterY=-26.5 CenterZ=0 NormalX=0 NormalY=0 NormalZ=1 AngleXU=0 Radius=1
    g6: BSplineCurve PolesCount=3 KnotsCount=2 Degree=2 IsPeriodic=0
    g7: GeomPoint X=-4.2 Y=-13.4877 Z=0
    g8: GeomPoint X=-8.2 Y=-26.5 Z=0
    g9: LineSegment StartX=-14 StartY=-26.5 StartZ=0 EndX=-8.2 EndY=-26.5 EndZ=0
    g10: LineSegment StartX=-10.15 StartY=-12 StartZ=0 EndX=-10.15 EndY=-14 EndZ=0
    g11: LineSegment StartX=-12.8401 StartY=-16 StartZ=0 EndX=-10.1571 EndY=-16 EndZ=0
    g12: LineSegment StartX=-10.15 StartY=-14 StartZ=0 EndX=-8.70761 EndY=-14 EndZ=0
    g13: LineSegment StartX=-12.8401 StartY=-16 StartZ=0 EndX=-12.8401 EndY=-17.6958 EndZ=0
    g14: LineSegment StartX=-10.15 StartY=-12 StartZ=0 EndX=-7.79258 EndY=-12 EndZ=0
    g15: Circle CenterX=-6.2215 CenterY=-2 CenterZ=0 NormalX=0 NormalY=0 NormalZ=1 AngleXU=0 Radius=1
    g16: Circle CenterX=-6.22762 CenterY=-2.58724 CenterZ=0 NormalX=0 NormalY=0 NormalZ=1 AngleXU=0 Radius=1
    g17: Circle CenterX=-6.32538 CenterY=-4 CenterZ=0 NormalX=0 NormalY=0 NormalZ=1 AngleXU=0 Radius=1
    g18: BSplineCurve PolesCount=3 KnotsCount=2 Degree=2 IsPeriodic=0
    g19: GeomPoint X=-6.2215 Y=-2 Z=0
    g20: GeomPoint X=-6.32538 Y=-4 Z=0
    g21: Circle CenterX=-6.48644 CenterY=-5.99526 CenterZ=0 NormalX=0 NormalY=0 NormalZ=1 AngleXU=0 Radius=1
    g22: Circle CenterX=-6.58486 CenterY=-6.99526 CenterZ=0 NormalX=0 NormalY=0 NormalZ=1 AngleXU=0 Radius=1
    g23: Circle CenterX=-6.77343 CenterY=-8 CenterZ=0 NormalX=0 NormalY=0 NormalZ=1 AngleXU=0 Radius=1
    g24: BSplineCurve PolesCount=3 KnotsCount=2 Degree=2 IsPeriodic=0
    g25: GeomPoint X=-6.48644 Y=-5.99526 Z=0
    g26: GeomPoint X=-6.77343 Y=-8 Z=0
    g27: Circle CenterX=-7.19003 CenterY=-10 CenterZ=0 NormalX=0 NormalY=0 NormalZ=1 AngleXU=0 Radius=1
    g28: Circle CenterX=-7.44407 CenterY=-11.0915 CenterZ=0 NormalX=0 NormalY=0 NormalZ=1 AngleXU=0 Radius=1
    g29: Circle CenterX=-7.79258 CenterY=-12 CenterZ=0 NormalX=0 NormalY=0 NormalZ=1 AngleXU=0 Radius=1
    g30: BSplineCurve PolesCount=3 KnotsCount=2 Degree=2 IsPeriodic=0
    g31: GeomPoint X=-7.19003 Y=-10 Z=0
    g32: GeomPoint X=-7.79258 Y=-12 Z=0
    g33: Circle CenterX=-8.70761 CenterY=-14 CenterZ=0 NormalX=0 NormalY=0 NormalZ=1 AngleXU=0 Radius=1
    g34: Circle CenterX=-9.33087 CenterY=-15.1837 CenterZ=0 NormalX=0 NormalY=0 NormalZ=1 AngleXU=0 Radius=1
    g35: Circle CenterX=-10.1571 CenterY=-16 CenterZ=0 NormalX=0 NormalY=0 NormalZ=1 AngleXU=0 Radius=1
    g36: BSplineCurve PolesCount=3 KnotsCount=2 Degree=2 IsPeriodic=0
    g37: GeomPoint X=-8.70761 Y=-14 Z=0
    g38: GeomPoint X=-10.1571 Y=-16 Z=0
    g39: Circle CenterX=-12.8401 CenterY=-17.6958 CenterZ=0 NormalX=0 NormalY=0 NormalZ=1 AngleXU=0 Radius=1
    g40: Circle CenterX=-13.3521 CenterY=-17.9027 CenterZ=0 NormalX=0 NormalY=0 NormalZ=1 AngleXU=0 Radius=1
    g41: Circle CenterX=-14 CenterY=-18 CenterZ=0 NormalX=0 NormalY=0 NormalZ=1 AngleXU=0 Radius=1
    g42: BSplineCurve PolesCount=3 KnotsCount=2 Degree=2 IsPeriodic=0
    g43: GeomPoint X=-12.8401 Y=-17.6958 Z=0
    g44: GeomPoint X=-14 Y=-18 Z=0
    g45: LineSegment StartX=-6.2 StartY=0 StartZ=0 EndX=-7.2 EndY=0 EndZ=0
    g46: LineSegment StartX=-7.2 StartY=0 StartZ=0 EndX=-7.2 EndY=-2 EndZ=0
    g47: LineSegment StartX=-7.2 StartY=-2 StartZ=0 EndX=-6.2215 EndY=-2 EndZ=0
    g48: LineSegment StartX=-6.32538 StartY=-4 StartZ=0 EndX=-7.65538 EndY=-4 EndZ=0
    g49: LineSegment StartX=-7.65538 StartY=-4 StartZ=0 EndX=-7.65538 EndY=-5.99526 EndZ=0
    g50: LineSegment StartX=-7.65538 StartY=-5.99526 StartZ=0 EndX=-6.48644 EndY=-5.99526 EndZ=0
    g51: LineSegment StartX=-6.77343 StartY=-8 StartZ=0 EndX=-8.43343 EndY=-8 EndZ=0
    g52: LineSegment StartX=-8.43343 StartY=-8 StartZ=0 EndX=-8.43343 EndY=-10 EndZ=0
    g53: LineSegment StartX=-8.43343 StartY=-10 StartZ=0 EndX=-7.19003 EndY=-10 EndZ=0
  constraints (112):
    c: Horizontal(g0)
    c: Distance(g0) = 2
    c: Block(g0)
    c: Vertical(g1)
    c: Coincident(g2,g0)
    c: Vertical(g2)
    c: Block(g2)
    c: Coincident(g6,g2)
    c: Weight(g3) = 1
    c: Equal(g3,g4)
    c: Equal(g3,g5)
    c: InternalAlignment(g3,g6)
    c: InternalAlignment(g4,g6)
    c: InternalAlignment(g5,g6)
    c: InternalAlignment(g7,g6)
    c: InternalAlignment(g8,g6)
    c: Block(g6)
    c: Coincident(g9,g1)
    c: Coincident(g9,g6)
    c: Horizontal(g9)
    c: Vertical(g10)
    c: Block(g10)
    c: Horizontal(g11)
    c: Block(g11)
    c: Coincident(g12,g10)
    c: Horizontal(g12)
    c: Block(g12)
    c: Coincident(g13,g11)
    c: Vertical(g13)
    c: Block(g13)
    c: Coincident(g14,g10)
    c: Horizontal(g14)
    c: Block(g14)
    c: Block(g9)
    c: Block(g1)
    c: Weight(g15) = 1
    c: Equal(g15,g16)
    c: Equal(g15,g17)
    c: InternalAlignment(g15,g18)
    c: InternalAlignment(g16,g18)
    c: InternalAlignment(g17,g18)
    c: InternalAlignment(g19,g18)
    c: InternalAlignment(g20,g18)
    c: Weight(g21) = 1
    c: Equal(g21,g22)
    c: Equal(g21,g23)
    c: InternalAlignment(g21,g24)
    c: InternalAlignment(g22,g24)
    c: InternalAlignment(g23,g24)
    c: InternalAlignment(g25,g24)
    c: InternalAlignment(g26,g24)
    c: Weight(g27) = 1
    c: Equal(g27,g28)
    c: Equal(g27,g29)
    c: Coincident(g30,g14)
    c: InternalAlignment(g27,g30)
    c: InternalAlignment(g28,g30)
    c: InternalAlignment(g29,g30)
    c: InternalAlignment(g31,g30)
    c: InternalAlignment(g32,g30)
    c: Coincident(g36,g12)
    c: Weight(g33) = 1
    c: Equal(g33,g34)
    c: Equal(g33,g35)
    c: Coincident(g36,g11)
    c: InternalAlignment(g33,g36)
    c: InternalAlignment(g34,g36)
    c: InternalAlignment(g35,g36)
    c: InternalAlignment(g37,g36)
    c: InternalAlignment(g38,g36)
    c: Coincident(g42,g13)
    c: Weight(g39) = 1
    c: Equal(g39,g40)
    c: Equal(g39,g41)
    c: Coincident(g42,g1)
    c: InternalAlignment(g39,g42)
    c: InternalAlignment(g40,g42)
    c: InternalAlignment(g41,g42)
    c: InternalAlignment(g43,g42)
    c: InternalAlignment(g44,g42)
    c: Block(g18)
    c: Block(g24)
    c: Block(g30)
    c: Block(g36)
    c: Block(g42)
    c: Horizontal(g45)
    c: Coincident(g45,g0)
    c: Vertical(g46)
    c: Coincident(g46,g45)
    c: Coincident(g47,g46)
    c: Coincident(g47,g18)
    c: Horizontal(g47)
    c: Block(g46)
    c: Coincident(g48,g18)
    c: Horizontal(g48)
    c: Distance(g48) = 1.33
    c: Vertical(g49)
    c: Coincident(g49,g48)
    c: Coincident(g50,g49)
    c: Coincident(g50,g24)
    c: Horizontal(g50)
    c: Tangent(g50,g22)
    c: Horizontal(g51)
    c: Coincident(g51,g24)
    c: Block(g51)
    c: Vertical(g52)
    c: Block(g52)
    c: Coincident(g52,g51)
    c: Coincident(g53,g52)
    c: Coincident(g53,g30)
    c: Horizontal(g53)
    c: Distance(g1) = 8.5
FEATURE [Part::Feature] Face024
  shape: bbox 9.8 x 26.5 x 2e-07 mm, 1 faces, 0 solids (baked)
FEATURE [Part::Revolution] Revolve024
  Angle = 360
  Axis = (0,1,0)
  Base = (0,0,0)
  FaceMakerClass = Part::FaceMakerBullseye
  Placement = pos=(0,0,0) rot=(0,0,1;1.5708rad)
  Solid = false
  Source = -> Face024
  Symmetric = false
FEATURE [Part::Feature] Face025
  shape: bbox 9.8 x 26.5 x 2e-07 mm, 1 faces, 0 solids (baked)
FEATURE [Part::Revolution] Revolve025
  Angle = 360
  Axis = (0,1,0)
  Base = (0,0,0)
  FaceMakerClass = Part::FaceMakerBullseye
  Placement = pos=(0,0,0) rot=(0,0,1;1.5708rad)
  Solid = false
  Source = -> Face025
  Symmetric = false
FEATURE [Part::MultiFuse] Fusion033
  Placement = pos=(-18,19,36) rot=(0,0,1;0rad)
  Shapes = -> [Revolve025,Revolve024]
FEATURE [Part::Cylinder] Cylinder014
  Angle = 360
  AttacherType = Attacher::AttachEngine3D
  Height = 20
  Placement = pos=(0,0,36.15) rot=(0,0,1;0rad)
  Radius = 14.3
FEATURE [Part::Cylinder] Cylinder015
  Angle = 360
  AttacherType = Attacher::AttachEngine3D
  Height = 10
  Placement = pos=(0,0,36.15) rot=(0,0,1;0rad)
  Radius = 4
FEATURE [Part::MultiFuse] Fusion034  label="removeToCreteHoleForPlugHousing004"
  Placement = pos=(-42,19,36) rot=(0,1,0;1.5708rad)
  Shapes = -> [Cylinder014,Cylinder015]
FEATURE [Part::Cut] Cut008  label="top004"
  Base = -> Cut004
  Placement = pos=(-1,0,0) rot=(0,0,1;0rad)
  Tool = -> Fusion034
FEATURE [Part::Box] Box005  label="Cube005"
  AttacherType = Attacher::AttachEngine3D
  Height = 28
  Length = 3
  Placement = pos=(110.7,19,22) rot=(0,0,1;0rad)
  Width = 15.7
FEATURE [Part::Cylinder] Cylinder016
  Angle = 360
  AttacherType = Attacher::AttachEngine3D
  Height = 10
  Placement = pos=(0,0,36.15) rot=(0,0,1;0rad)
  Radius = 4
FEATURE [Part::Cylinder] Cylinder017
  Angle = 360
  AttacherType = Attacher::AttachEngine3D
  Height = 20
  Placement = pos=(0,0,36.15) rot=(0,0,1;0rad)
  Radius = 10.3
FEATURE [Part::MultiFuse] Fusion035  label="removeToCreteHoleForPlugHousing005"
  Placement = pos=(70,19,36) rot=(0,1,0;1.5708rad)
  Shapes = -> [Cylinder017,Cylinder016]
FEATURE [Part::Cut] Cut009  label="plugHousingTab001"
  Base = -> Box005
  Placement = pos=(-107.4,-14,0) rot=(0,0,1;0rad)
  Tool = -> Fusion035
FEATURE [Part::Box] Box006  label="Cube006"
  AttacherType = Attacher::AttachEngine3D
  Height = 28
  Length = 3
  Placement = pos=(110.7,19,22) rot=(0,0,1;0rad)
  Width = 15.7
FEATURE [Part::Cylinder] Cylinder018
  Angle = 360
  AttacherType = Attacher::AttachEngine3D
  Height = 10
  Placement = pos=(0,0,36.15) rot=(0,0,1;0rad)
  Radius = 4
FEATURE [Part::Cylinder] Cylinder019
  Angle = 360
  AttacherType = Attacher::AttachEngine3D
  Height = 20
  Placement = pos=(0,0,36.15) rot=(0,0,1;0rad)
  Radius = 10.3
FEATURE [Part::MultiFuse] Fusion036  label="removeToCreteHoleForPlugHousing006"
  Placement = pos=(70,19,36) rot=(0,1,0;1.5708rad)
  Shapes = -> [Cylinder019,Cylinder018]
FEATURE [Part::Cut] Cut010  label="plugHousingTab002"
  Base = -> Box006
  Placement = pos=(-107.4,-14,0) rot=(0,0,1;0rad)
  Tool = -> Fusion036
FEATURE [Part::MultiFuse] Fusion037
  Placement = pos=(9.6,23,0) rot=(0,0,1;3.14159rad)
  Shapes = -> [Cut009,Cut010]
FEATURE [Part::Box] Box  label="Cube"
  AttacherType = Attacher::AttachEngine3D
  Height = 10
  Length = 3
  Placement = pos=(3.3,4,12) rot=(0,0,1;0rad)
  Width = 10
FEATURE [Part::Fillet] Fillet004
  Base = -> Fusion028
  Edges = 1 edges r=2: [Edge25]
FEATURE [Part::Fillet] Fillet005  label="plugHousing046"
  Base = -> Fillet004
  Edges = 1 edges r=2: [Edge8]
FEATURE [Part::Fillet] Fillet006
  Base = -> Box
  Edges = 1 edges r=2: [Edge11]
FEATURE [Part::Box] Box007  label="Cube007"
  AttacherType = Attacher::AttachEngine3D
  Height = 10
  Length = 3
  Placement = pos=(3.3,4,50) rot=(0,0,1;0rad)
  Width = 10
FEATURE [Part::Fillet] Fillet007
  Base = -> Box007
  Edges = 1 edges r=2: [Edge12]
FEATURE [Part::Box] Box008  label="Cube008"
  AttacherType = Attacher::AttachEngine3D
  Height = 28
  Length = 4
  Placement = pos=(5,0,22) rot=(0,0,1;0rad)
  Width = 10
FEATURE [Part::Fillet] Fillet008
  Base = -> Box008
  Edges = 1 edges r=1: [Edge7]
FEATURE [Part::Fillet] Fillet009
  Base = -> Fillet008
  Edges = 1 edges r=2: [Edge5]
FEATURE [Part::Fillet] Fillet010
  Base = -> Fillet009
  Edges = 1 edges r=2: [Edge2]
FEATURE [Sketcher::SketchObject] Sketch009  label="topSketch003"
  FullyConstrained = true
  sketch-geometry (4):
    g0: LineSegment StartX=16.8446 StartY=31.512 StartZ=0 EndX=16.3251 EndY=34.4666 EndZ=0
    g1: ArcOfCircle CenterX=19 CenterY=19.2524 CenterZ=0 NormalX=0 NormalY=0 NormalZ=1 AngleXU=0 Radius=15.4476 StartAngle=1.74483 EndAngle=2.72717
    g2: ArcOfCircle CenterX=19 CenterY=19.2524 CenterZ=0 NormalX=0 NormalY=0 NormalZ=1 AngleXU=0 Radius=12.4476 StartAngle=1.74483 EndAngle=2.73189
    g3: LineSegment StartX=4.86004 StartY=25.4725 StartZ=0 EndX=7.58253 EndY=24.2107 EndZ=0
  constraints (7):
    c: Block(g0)
    c: Coincident(g1,g0)
    c: Coincident(g2,g0)
    c: Coincident(g3,g1)
    c: Coincident(g3,g2)
    c: Block(g1)
    c: Block(g2)
FEATURE [Part::Extrusion] Extrude008
  Base = -> Sketch009
  Dir = (0,0,1)
  DirMode = 2
  FaceMakerClass = Part::FaceMakerBullseye
  LengthFwd = 10
  LengthRev = 0
  Placement = pos=(0,0,31) rot=(0,0,1;0rad)
  Solid = true
  Symmetric = false
FEATURE [Part::Cylinder] Cylinder020
  Angle = 360
  AttacherType = Attacher::AttachEngine3D
  Height = 20
  Placement = pos=(0,0,36.15) rot=(0,0,1;0rad)
  Radius = 8.2
FEATURE [Part::Cylinder] Cylinder021
  Angle = 360
  AttacherType = Attacher::AttachEngine3D
  Height = 10
  Placement = pos=(0,0,36.15) rot=(0,0,1;0rad)
  Radius = 4
FEATURE [Part::MultiFuse] Fusion038  label="removeToCreteHoleForPlugHousing007"
  Placement = pos=(-42,19,36) rot=(0,1,0;1.5708rad)
  Shapes = -> [Cylinder020,Cylinder021]
FEATURE [Part::Cut] Cut011
  Base = -> Extrude008
  Tool = -> Fusion038
FEATURE [Part::Fillet] Fillet011
  Base = -> Cut011
  Edges = 1 edges r=2: [Edge1]
FEATURE [Part::Fillet] Fillet012
  Base = -> Fillet011
  Edges = 1 edges r=2.5: [Edge1]
FEATURE [Part::Fillet] Fillet013
  Base = -> Fillet012
  Edges = 1 edges r=2.5: [Edge2]
FEATURE [Part::Box] Box010  label="Cube010"
  AttacherType = Attacher::AttachEngine3D
  Height = 16
  Length = 8
  Placement = pos=(12.7,31.52,28) rot=(0,0,1;0rad)
  Width = 4
FEATURE [Sketcher::SketchObject] Sketch010  label="topSketch004"
  FullyConstrained = true
  sketch-geometry (4):
    g0: LineSegment StartX=16.8446 StartY=31.512 StartZ=0 EndX=16.3251 EndY=34.4666 EndZ=0
    g1: ArcOfCircle CenterX=19 CenterY=19.2524 CenterZ=0 NormalX=0 NormalY=0 NormalZ=1 AngleXU=0 Radius=15.4476 StartAngle=1.74483 EndAngle=2.72717
    g2: ArcOfCircle CenterX=19 CenterY=19.2524 CenterZ=0 NormalX=0 NormalY=0 NormalZ=1 AngleXU=0 Radius=12.4476 StartAngle=1.74483 EndAngle=2.73189
    g3: LineSegment StartX=4.86004 StartY=25.4725 StartZ=0 EndX=7.58253 EndY=24.2107 EndZ=0
  constraints (7):
    c: Block(g0)
    c: Coincident(g1,g0)
    c: Coincident(g2,g0)
    c: Coincident(g3,g1)
    c: Coincident(g3,g2)
    c: Block(g1)
    c: Block(g2)
FEATURE [Part::Cylinder] Cylinder022
  Angle = 360
  AttacherType = Attacher::AttachEngine3D
  Height = 10
  Placement = pos=(0,0,36.15) rot=(0,0,1;0rad)
  Radius = 4
FEATURE [Sketcher::SketchObject] Sketch011  label="topSketch005"
  FullyConstrained = true
  sketch-geometry (4):
    g0: LineSegment StartX=16.8446 StartY=31.512 StartZ=0 EndX=16.3251 EndY=34.4666 EndZ=0
    g1: ArcOfCircle CenterX=19 CenterY=19.2524 CenterZ=0 NormalX=0 NormalY=0 NormalZ=1 AngleXU=0 Radius=15.4476 StartAngle=1.74483 EndAngle=2.72717
    g2: ArcOfCircle CenterX=19 CenterY=19.2524 CenterZ=0 NormalX=0 NormalY=0 NormalZ=1 AngleXU=0 Radius=12.4476 StartAngle=1.74483 EndAngle=2.73189
    g3: LineSegment StartX=4.86004 StartY=25.4725 StartZ=0 EndX=7.58253 EndY=24.2107 EndZ=0
  constraints (7):
    c: Block(g0)
    c: Coincident(g1,g0)
    c: Coincident(g2,g0)
    c: Coincident(g3,g1)
    c: Coincident(g3,g2)
    c: Block(g1)
    c: Block(g2)
FEATURE [Part::Extrusion] Extrude010
  Base = -> Sketch011
  Dir = (0,0,1)
  DirMode = 2
  FaceMakerClass = Part::FaceMakerBullseye
  LengthFwd = 10.6
  LengthRev = 0
  Placement = pos=(0,0,31) rot=(0,0,1;0rad)
  Solid = true
  Symmetric = false
FEATURE [Part::Cylinder] Cylinder023
  Angle = 360
  AttacherType = Attacher::AttachEngine3D
  Height = 20
  Placement = pos=(0,0,36.15) rot=(0,0,1;0rad)
  Radius = 8.2
FEATURE [Part::MultiFuse] Fusion039  label="removeToCreteHoleForPlugHousing008"
  Placement = pos=(-42,19,36) rot=(0,1,0;1.5708rad)
  Shapes = -> [Cylinder023,Cylinder022]
FEATURE [Part::Cut] Cut012
  Base = -> Extrude010
  Placement = pos=(0,0,-0.3) rot=(0,0,1;0rad)
  Tool = -> Fusion039
FEATURE [Part::Cut] Cut013
  Base = -> Box010
  Tool = -> Cut012
FEATURE [Part::Fillet] Fillet014
  Base = -> Cut013
  Edges = 1 edges r=0.7: [Edge13]
FEATURE [Part::Fillet] Fillet015
  Base = -> Fillet014
  Edges = 1 edges r=0.7: [Edge13]
FEATURE [Part::Fillet] Fillet016
  Base = -> Fillet015
  Edges = 1 edges r=0.7: [Edge16]
FEATURE [Part::Fillet] Fillet017
  Base = -> Fillet016
  Edges = 1 edges r=0.7: [Edge11]
FEATURE [Part::Fillet] Fillet018
  Base = -> Fillet017
  Edges = 1 edges r=0.7: [Edge10]
FEATURE [Part::Fillet] Fillet019
  Base = -> Fillet018
  Edges = 1 edges r=1.2: [Edge5]
FEATURE [Part::Fillet] Fillet020
  Base = -> Fillet019
  Edges = 1 edges r=1.2: [Edge12]
FEATURE [Part::Fillet] Fillet021
  Base = -> Fillet020
  Edges = 1 edges r=2: [Edge1]
  Placement = pos=(0.3,0,0) rot=(0,0,1;0rad)
FEATURE [Part::MultiFuse] Fusion040  label="top005"
  Shapes = -> [Cut008,Fillet021]
FEATURE [Part::MultiFuse] Fusion041  label="wireHolder"
  Shapes = -> [Fusion033,Fillet013]
FEATURE [Part::MultiFuse] Fusion042
  Shapes = -> [Fillet007,Fusion041]
FEATURE [Part::MultiFuse] Fusion043  label="wireHolder001"
  Shapes = -> [Fusion042,Fillet010]
FEATURE [Part::MultiFuse] Fusion044  label="wireHolder002"
  Shapes = -> [Fillet006,Fusion037,Fusion043]
FEATURE [Part::Feature] Face026
  shape: bbox 11 x 6 x 2e-07 mm, 1 faces, 0 solids (baked)
FEATURE [Part::Revolution] Revolve026
  Angle = 360
  Axis = (0,1,0)
  Base = (0,0,0)
  FaceMakerClass = Part::FaceMakerBullseye
  Placement = pos=(30.3,-1,19.7) rot=(0,0,1;0rad)
  Solid = false
  Source = -> Face026
  Symmetric = false
FEATURE [Sketcher::SketchObject] Sketch013  label="topSketch006"
  FullyConstrained = true
  sketch-geometry (13):
    g0: LineSegment StartX=117 StartY=19 StartZ=0 EndX=117 EndY=38 EndZ=0
    g1: ArcOfCircle CenterX=98 CenterY=19 CenterZ=0 NormalX=0 NormalY=0 NormalZ=1 AngleXU=0 Radius=19 StartAngle=5.7297 EndAngle=6.28319
    g2: LineSegment StartX=0 StartY=3 StartZ=0 EndX=0 EndY=19 EndZ=0
    g3: LineSegment StartX=19 StartY=38 StartZ=0 EndX=117 EndY=38 EndZ=0
    g4: ArcOfCircle CenterX=19 CenterY=19 CenterZ=0 NormalX=0 NormalY=0 NormalZ=1 AngleXU=0 Radius=19 StartAngle=1.5708 EndAngle=3.14159
    g5: ArcOfCircle CenterX=19 CenterY=19 CenterZ=0 NormalX=0 NormalY=0 NormalZ=1 AngleXU=0 Radius=16 StartAngle=1.5708 EndAngle=3.14159
    g6: ArcOfCircle CenterX=98 CenterY=19 CenterZ=0 NormalX=0 NormalY=0 NormalZ=1 AngleXU=0 Radius=16 StartAngle=5.60905 EndAngle=6.28319
    g7: LineSegment StartX=114 StartY=19 StartZ=0 EndX=114 EndY=35 EndZ=0
    g8: LineSegment StartX=110.5 StartY=9.01251 StartZ=0 EndX=114.163 EndY=9.01251 EndZ=0
    g9: LineSegment StartX=114 StartY=35 StartZ=0 EndX=19 EndY=35 EndZ=0
    g10: LineSegment StartX=0 StartY=3 StartZ=0 EndX=0 EndY=0 EndZ=0
    g11: LineSegment StartX=3 StartY=0 StartZ=0 EndX=0 EndY=0 EndZ=0
    g12: LineSegment StartX=3 StartY=19 StartZ=0 EndX=3 EndY=0 EndZ=0
  constraints (33):
    c: Vertical(g0)
    c: Distance(g0) = 19
    c: Block(g0)
    c: Coincident(g1,g0)
    c: Block(g1)
    c: Vertical(g2)
    c: Block(g2)
    c: Coincident(g3,g0)
    c: Horizontal(g3)
    c: Distance(g3) = 98
    c: Coincident(g4,g3)
    c: Coincident(g4,g2)
    c: Block(g4)
    c: Coincident(g5,g4)
    c: Coincident(g6,g1)
    c: Block(g6)
    c: Block(g5)
    c: Coincident(g7,g6)
    c: Vertical(g7)
    c: Coincident(g8,g6)
    c: Coincident(g8,g1)
    c: Coincident(g9,g7)
    c: Coincident(g9,g5)
    c: Horizontal(g9)
    c: Tangent(g9,g5)
    c: Coincident(g10,g2)
    c: Distance(g10) = 3
    c: Vertical(g10)
    c: Coincident(g11,g10)
    c: Horizontal(g11)
    c: Coincident(g12,g5)
    c: Coincident(g12,g11)
    c: Vertical(g12)
FEATURE [Part::Extrusion] Extrude011  label="top006"
  Base = -> Sketch013
  Dir = (0,0,1)
  DirMode = 2
  FaceMakerClass = Part::FaceMakerBullseye
  LengthFwd = 72
  LengthRev = 0
  Solid = true
  Symmetric = false
FEATURE [Sketcher::SketchObject] Sketch014
  FullyConstrained = true
  MapMode = 3
  Placement = pos=(0,0,0) rot=(1,0,0;1.5708rad)
  Support = -> [Extrude011]
  sketch-geometry (8):
    g0: Circle CenterX=80.351 CenterY=-67.6202 CenterZ=0 NormalX=0 NormalY=0 NormalZ=1 AngleXU=0 Radius=2
    g1: Circle CenterX=80.351 CenterY=-67.6202 CenterZ=0 NormalX=0 NormalY=0 NormalZ=1 AngleXU=0 Radius=3
    g2: Circle CenterX=80.351 CenterY=-4.92017 CenterZ=0 NormalX=0 NormalY=0 NormalZ=1 AngleXU=0 Radius=2
    g3: Circle CenterX=80.351 CenterY=-4.92017 CenterZ=0 NormalX=0 NormalY=0 NormalZ=1 AngleXU=0 Radius=3
    g4: Circle CenterX=23.851 CenterY=-4.92017 CenterZ=0 NormalX=0 NormalY=0 NormalZ=1 AngleXU=0 Radius=2
    g5: Circle CenterX=23.851 CenterY=-4.92017 CenterZ=0 NormalX=0 NormalY=0 NormalZ=1 AngleXU=0 Radius=3
    g6: Circle CenterX=23.851 CenterY=-67.6202 CenterZ=0 NormalX=0 NormalY=0 NormalZ=1 AngleXU=0 Radius=2
    g7: Circle CenterX=23.851 CenterY=-67.6202 CenterZ=0 NormalX=0 NormalY=0 NormalZ=1 AngleXU=0 Radius=3
  constraints (8):
    c: Block(g3)
    c: Block(g2)
    c: Block(g1)
    c: Block(g0)
    c: Block(g6)
    c: Block(g7)
    c: Block(g4)
    c: Block(g5)
FEATURE [Part::Feature] Face027
  shape: bbox 11 x 6 x 2e-07 mm, 1 faces, 0 solids (baked)
FEATURE [Part::Revolution] Revolve027
  Angle = 360
  Axis = (0,1,0)
  Base = (0,0,0)
  FaceMakerClass = Part::FaceMakerBullseye
  Placement = pos=(30.3,-1,51.7) rot=(0,0,1;0rad)
  Solid = false
  Source = -> Face027
  Symmetric = false
FEATURE [Part::Feature] Face028
  shape: bbox 11 x 6 x 2e-07 mm, 1 faces, 0 solids (baked)
FEATURE [Part::Revolution] Revolve028
  Angle = 360
  Axis = (0,1,0)
  Base = (0,0,0)
  FaceMakerClass = Part::FaceMakerBullseye
  Placement = pos=(62.3,-1,19.7) rot=(0,0,1;0rad)
  Solid = false
  Source = -> Face028
  Symmetric = false
FEATURE [Part::Feature] Face029
  shape: bbox 11 x 6 x 2e-07 mm, 1 faces, 0 solids (baked)
FEATURE [Part::Revolution] Revolve029
  Angle = 360
  Axis = (0,1,0)
  Base = (0,0,0)
  FaceMakerClass = Part::FaceMakerBullseye
  Placement = pos=(62.3,-1,51.7) rot=(0,0,1;0rad)
  Solid = false
  Source = -> Face029
  Symmetric = false
FEATURE [Part::Feature] Wire
  shape: bbox 11 x 5.2 x 2e-07 mm, 0 faces, 0 solids (baked)
FEATURE [Part::Revolution] Revolve030
  Angle = 360
  Axis = (0,1,0)
  Base = (0,0,0)
  FaceMakerClass = Part::FaceMakerBullseye
  Placement = pos=(30.3,38,19.7) rot=(0,0,1;0rad)
  Solid = true
  Source = -> Wire
  Symmetric = false
FEATURE [Part::Feature] Wire001
  shape: bbox 11 x 5.2 x 2e-07 mm, 0 faces, 0 solids (baked)
FEATURE [Part::Revolution] Revolve031
  Angle = 360
  Axis = (0,1,0)
  Base = (0,0,0)
  FaceMakerClass = Part::FaceMakerBullseye
  Placement = pos=(30.3,38,51.7) rot=(0,0,1;0rad)
  Solid = true
  Source = -> Wire001
  Symmetric = false
FEATURE [Part::Feature] Wire002
  shape: bbox 11 x 5.2 x 2e-07 mm, 0 faces, 0 solids (baked)
FEATURE [Part::Revolution] Revolve032
  Angle = 360
  Axis = (0,1,0)
  Base = (0,0,0)
  FaceMakerClass = Part::FaceMakerBullseye
  Placement = pos=(62.3,38,51.7) rot=(0,0,1;0rad)
  Solid = true
  Source = -> Wire002
  Symmetric = false
FEATURE [Part::Feature] Wire003
  shape: bbox 11 x 5.2 x 2e-07 mm, 0 faces, 0 solids (baked)
FEATURE [Part::Revolution] Revolve033
  Angle = 360
  Axis = (0,1,0)
  Base = (0,0,0)
  FaceMakerClass = Part::FaceMakerBullseye
  Placement = pos=(62.3,38,19.7) rot=(0,0,1;0rad)
  Solid = true
  Source = -> Wire003
  Symmetric = false
FEATURE [Part::MultiFuse] Fusion045  label="altRandScrewHousing"
  Shapes = -> [Revolve029,Revolve027,Revolve028,Revolve026]
FEATURE [Part::MultiFuse] Fusion046  label="fanScrewHousing"
  Shapes = -> [Revolve033,Revolve032,Revolve031,Revolve030]
FEATURE [Sketcher::SketchObject] Sketch015
  FullyConstrained = true
  sketch-geometry (17):
    g0: Circle CenterX=-3.5 CenterY=23.5 CenterZ=0 NormalX=0 NormalY=0 NormalZ=1 AngleXU=0 Radius=1
    g1: Circle CenterX=-1 CenterY=15.25 CenterZ=0 NormalX=0 NormalY=0 NormalZ=1 AngleXU=0 Radius=1
    g2: Circle CenterX=-3.5 CenterY=7 CenterZ=0 NormalX=0 NormalY=0 NormalZ=1 AngleXU=0 Radius=1
    g3: BSplineCurve PolesCount=3 KnotsCount=2 Degree=2 IsPeriodic=0
    g4: GeomPoint X=-3.5 Y=23.5 Z=0
    g5: GeomPoint X=-3.5 Y=7 Z=0
    g6: Circle CenterX=-4.8 CenterY=30.5 CenterZ=0 NormalX=0 NormalY=0 NormalZ=1 AngleXU=0 Radius=1
    g7: Circle CenterX=-3.5 CenterY=30.5 CenterZ=0 NormalX=0 NormalY=0 NormalZ=1 AngleXU=0 Radius=1
    g8: Circle CenterX=-3.5 CenterY=29.2 CenterZ=0 NormalX=0 NormalY=0 NormalZ=1 AngleXU=0 Radius=1
    g9: BSplineCurve PolesCount=3 KnotsCount=2 Degree=2 IsPeriodic=0
    g10: GeomPoint X=-4.8 Y=30.5 Z=0
    g11: GeomPoint X=-3.5 Y=29.2 Z=0
    g12: LineSegment StartX=-3.5 StartY=29.2 StartZ=0 EndX=-3.5 EndY=23.5 EndZ=0
    g13: LineSegment StartX=-4.8 StartY=30.5 StartZ=0 EndX=0 EndY=30.5 EndZ=0
    g14: LineSegment StartX=-3.5 StartY=0.3 StartZ=0 EndX=0 EndY=0.3 EndZ=0
    g15: LineSegment StartX=-3.5 StartY=0.3 StartZ=0 EndX=-3.5 EndY=7 EndZ=0
    g16: LineSegment StartX=0 StartY=0.3 StartZ=0 EndX=0 EndY=30.5 EndZ=0
  constraints (34):
    c: Weight(g0) = 1
    c: Equal(g0,g1)
    c: Equal(g0,g2)
    c: InternalAlignment(g0,g3)
    c: InternalAlignment(g1,g3)
    c: InternalAlignment(g2,g3)
    c: InternalAlignment(g4,g3)
    c: InternalAlignment(g5,g3)
    c: Block(g3)
    c: Weight(g6) = 1
    c: Equal(g6,g7)
    c: Equal(g6,g8)
    c: InternalAlignment(g6,g9)
    c: InternalAlignment(g7,g9)
    c: InternalAlignment(g8,g9)
    c: InternalAlignment(g10,g9)
    c: InternalAlignment(g11,g9)
    c: Block(g9)
    c: Coincident(g12,g9)
    c: Coincident(g12,g3)
    c: Vertical(g12)
    c: Coincident(g13,g9)
    c: Horizontal(g13)
    c: Distance(g13) = 4.8
    c: Horizontal(g14)
    c: Block(g14)
    c: Coincident(g15,g14)
    c: Coincident(g15,g3)
    c: Vertical(g15)
    c: Coincident(g16,g14)
    c: Coincident(g16,g13)
    c: Vertical(g16)
    c: Tangent(g16,g1)
    c: Distance(g14) = 3.5
FEATURE [Sketcher::SketchObject] Sketch016
  FullyConstrained = true
  sketch-geometry (16):
    g0: Circle CenterX=-3.5 CenterY=23.5 CenterZ=0 NormalX=0 NormalY=0 NormalZ=1 AngleXU=0 Radius=1
    g1: Circle CenterX=-1 CenterY=15.25 CenterZ=0 NormalX=0 NormalY=0 NormalZ=1 AngleXU=0 Radius=1
    g2: Circle CenterX=-3.5 CenterY=7 CenterZ=0 NormalX=0 NormalY=0 NormalZ=1 AngleXU=0 Radius=1
    g3: BSplineCurve PolesCount=3 KnotsCount=2 Degree=2 IsPeriodic=0
    g4: GeomPoint X=-3.5 Y=23.5 Z=0
    g5: GeomPoint X=-3.5 Y=7 Z=0
    g6: LineSegment StartX=-3.5 StartY=28.2 StartZ=0 EndX=-3.5 EndY=23.5 EndZ=0
    g7: LineSegment StartX=0 StartY=29.5 StartZ=0 EndX=0 EndY=30 EndZ=0
    g8: LineSegment StartX=-3.5 StartY=28.2 StartZ=0 EndX=-3.5 EndY=30 EndZ=0
    g9: LineSegment StartX=0 StartY=30 StartZ=0 EndX=0 EndY=30.5 EndZ=0
    g10: LineSegment StartX=0 StartY=30.5 StartZ=0 EndX=-3.5 EndY=30.5 EndZ=0
    g11: LineSegment StartX=-3.5 StartY=30.5 StartZ=0 EndX=-3.5 EndY=30 EndZ=0
    g12: LineSegment StartX=0 StartY=29.5 StartZ=0 EndX=0 EndY=5 EndZ=0
    g13: LineSegment StartX=-3.5 StartY=0.3 StartZ=0 EndX=-3.5 EndY=7 EndZ=0
    g14: LineSegment StartX=-3.5 StartY=0.3 StartZ=0 EndX=0 EndY=0.3 EndZ=0
    g15: LineSegment StartX=0 StartY=5 StartZ=0 EndX=0 EndY=0.3 EndZ=0
  constraints (39):
    c: Weight(g0) = 1
    c: Equal(g0,g1)
    c: Equal(g0,g2)
    c: InternalAlignment(g0,g3)
    c: InternalAlignment(g1,g3)
    c: InternalAlignment(g2,g3)
    c: InternalAlignment(g4,g3)
    c: InternalAlignment(g5,g3)
    c: Block(g3)
    c: Coincident(g6,g3)
    c: Vertical(g6)
    c: Vertical(g7)
    c: Distance(g7) = 0.5
    c: Coincident(g8,g6)
    c: Vertical(g8)
    c: Block(g6)
    c: Block(g7)
    c: Vertical(g9)
    c: Equal(g7,g9) = 0.5
    c: Block(g9)
    c: Coincident(g9,g7)
    c: Horizontal(g10)
    c: Coincident(g10,g9)
    c: Coincident(g11,g10)
    c: Coincident(g11,g8)
    c: Vertical(g11)
    c: Block(g11)
    c: Coincident(g12,g7)
    c: Vertical(g12)
    c: Coincident(g13,g3)
    c: Vertical(g13)
    c: Distance(g13) = 6.7
    c: Coincident(g14,g13)
    c: Horizontal(g14)
    c: Block(g14)
    c: Coincident(g15,g12)
    c: Coincident(g15,g14)
    c: Vertical(g15)
    c: Block(g15)
FEATURE [Sketcher::SketchObject] Sketch017
  FullyConstrained = true
  sketch-geometry (11):
    g0: LineSegment StartX=-3.5 StartY=1e-16 StartZ=0 EndX=-1.6 EndY=1e-16 EndZ=0
    g1: LineSegment StartX=-1.6 StartY=1e-16 StartZ=0 EndX=-1.6 EndY=1.5 EndZ=0
    g2: LineSegment StartX=-3.5 StartY=1.5 StartZ=0 EndX=-1.6 EndY=1.5 EndZ=0
    g3: LineSegment StartX=-3.5 StartY=1e-16 StartZ=0 EndX=-4.8 EndY=1e-16 EndZ=0
    g4: Circle CenterX=-3.5 CenterY=1.3 CenterZ=0 NormalX=0 NormalY=0 NormalZ=1 AngleXU=0 Radius=1
    g5: Circle CenterX=-3.5 CenterY=1e-16 CenterZ=0 NormalX=0 NormalY=0 NormalZ=1 AngleXU=0 Radius=1
    g6: Circle CenterX=-4.8 CenterY=1e-16 CenterZ=0 NormalX=0 NormalY=0 NormalZ=1 AngleXU=0 Radius=1
    g7: BSplineCurve PolesCount=3 KnotsCount=2 Degree=2 IsPeriodic=0
    g8: GeomPoint X=-3.5 Y=1.3 Z=0
    g9: GeomPoint X=-4.8 Y=1e-16 Z=0
    g10: LineSegment StartX=-3.5 StartY=1.3 StartZ=0 EndX=-3.5 EndY=1.5 EndZ=0
  constraints (24):
    c: Horizontal(g0)
    c: Distance(g0) = 1.9
    c: Block(g0)
    c: Coincident(g1,g0)
    c: Vertical(g1)
    c: Coincident(g2,g1)
    c: Horizontal(g2)
    c: Coincident(g3,g0)
    c: Horizontal(g3)
    c: Distance(g3) = 1.3
    c: Weight(g4) = 1
    c: Equal(g4,g5)
    c: Coincident(g5,g0)
    c: Equal(g4,g6)
    c: Coincident(g7,g3)
    c: InternalAlignment(g4,g7)
    c: InternalAlignment(g5,g7)
    c: InternalAlignment(g6,g7)
    c: InternalAlignment(g8,g7)
    c: InternalAlignment(g9,g7)
    c: Coincident(g10,g7)
    c: Coincident(g10,g2)
    c: Vertical(g10)
    c: Block(g10)
FEATURE [Part::Feature] Face035
  shape: bbox 3.2 x 1.5 x 2e-07 mm, 1 faces, 0 solids (baked)
FEATURE [Part::Revolution] Revolve039  label="backCaseScrewRetainer"
  Angle = 360
  Axis = (0,1,0)
  Base = (0,0,0)
  FaceMakerClass = Part::FaceMakerBullseye
  Placement = pos=(12.5,3,62) rot=(0,0,1;0rad)
  Solid = false
  Source = -> Face035
  Symmetric = false
FEATURE [Part::Feature] Face036
  shape: bbox 3.2 x 1.5 x 2e-07 mm, 1 faces, 0 solids (baked)
FEATURE [Part::Feature] Face039
  shape: bbox 4.8 x 30.2 x 2e-07 mm, 1 faces, 0 solids (baked)
FEATURE [Part::Revolution] Revolve043  label="frontCaseScrewPost002"
  Angle = 360
  Axis = (0,1,0)
  Base = (0,0,0)
  FaceMakerClass = Part::FaceMakerBullseye
  Placement = pos=(89.5,4.5,3.5) rot=(0,0,1;0rad)
  Solid = false
  Source = -> Face039
  Symmetric = false
FEATURE [Part::Feature] Face042
  shape: bbox 4.8 x 30.2 x 2e-07 mm, 1 faces, 0 solids (baked)
FEATURE [Part::Revolution] Revolve046  label="frontCaseScrewPost003"
  Angle = 360
  Axis = (0,1,0)
  Base = (0,0,0)
  FaceMakerClass = Part::FaceMakerBullseye
  Placement = pos=(89.5,4.5,68.5) rot=(0,0,1;0rad)
  Solid = false
  Source = -> Face042
  Symmetric = false
FEATURE [Part::Feature] Face043
  shape: bbox 3.2 x 1.5 x 2e-07 mm, 1 faces, 0 solids (baked)
FEATURE [Part::Revolution] Revolve047  label="frontCaseScrewRetainer002"
  Angle = 360
  Axis = (0,1,0)
  Base = (0,0,0)
  FaceMakerClass = Part::FaceMakerBullseye
  Placement = pos=(89.5,3,68.5) rot=(0,0,1;0rad)
  Solid = false
  Source = -> Face043
  Symmetric = false
FEATURE [Part::Feature] Face044
  shape: bbox 3.2 x 1.5 x 2e-07 mm, 1 faces, 0 solids (baked)
FEATURE [Part::Revolution] Revolve048  label="frontCaseScrewRetainer003"
  Angle = 360
  Axis = (0,1,0)
  Base = (0,0,0)
  FaceMakerClass = Part::FaceMakerBullseye
  Placement = pos=(89.5,3,3.5) rot=(0,0,1;0rad)
  Solid = false
  Source = -> Face044
  Symmetric = false
FEATURE [App::MeasureDistance] Distance002  label="Distance: 1.67 mm"
  Distance = 1.66921
  P1 = (99.2361,4.7524,71.7)
  P2 = (99.2347,6.42161,71.7)
FEATURE [Sketcher::SketchObject] Sketch018
  FullyConstrained = true
  sketch-geometry (7):
    g0: LineSegment StartX=0 StartY=0 StartZ=0 EndX=0 EndY=6 EndZ=0
    g1: Circle CenterX=0 CenterY=0 CenterZ=0 NormalX=0 NormalY=0 NormalZ=1 AngleXU=0 Radius=1
    g2: Circle CenterX=8 CenterY=6 CenterZ=0 NormalX=0 NormalY=0 NormalZ=1 AngleXU=0 Radius=1
    g3: BSplineCurve PolesCount=3 KnotsCount=2 Degree=2 IsPeriodic=0
    g4: GeomPoint X=0 Y=0 Z=0
    g5: GeomPoint X=8 Y=6 Z=0
    g6: LineSegment StartX=0 StartY=6 StartZ=0 EndX=8 EndY=6 EndZ=0
  constraints (14):
    c: Coincident(g0,g-1)
    c: Distance(g0) = 6
    c: Vertical(g0)
    c: Coincident(g3,g0)
    c: Weight(g1) = 1
    c: Equal(g1,g2)
    c: InternalAlignment(g1,g3)
    c: InternalAlignment(g2,g3)
    c: InternalAlignment(g4,g3)
    c: InternalAlignment(g5,g3)
    c: Block(g3)
    c: Coincident(g6,g0)
    c: Coincident(g6,g3)
    c: Horizontal(g6)
FEATURE [Part::Extrusion] Extrude012  label="caseScrewPillarBracket"
  Base = -> Sketch018
  Dir = (0,0,1)
  DirMode = 2
  FaceMakerClass = Part::FaceMakerBullseye
  LengthFwd = 2.4
  LengthRev = 0
  Placement = pos=(15.76,29,8.8) rot=(0,1,0;0rad)
  Solid = true
  Symmetric = false
FEATURE [Sketcher::SketchObject] Sketch019
  FullyConstrained = true
  sketch-geometry (7):
    g0: LineSegment StartX=0 StartY=0 StartZ=0 EndX=0 EndY=6 EndZ=0
    g1: Circle CenterX=0 CenterY=0 CenterZ=0 NormalX=0 NormalY=0 NormalZ=1 AngleXU=0 Radius=1
    g2: Circle CenterX=8 CenterY=6 CenterZ=0 NormalX=0 NormalY=0 NormalZ=1 AngleXU=0 Radius=1
    g3: BSplineCurve PolesCount=3 KnotsCount=2 Degree=2 IsPeriodic=0
    g4: GeomPoint X=0 Y=0 Z=0
    g5: GeomPoint X=8 Y=6 Z=0
    g6: LineSegment StartX=0 StartY=6 StartZ=0 EndX=8 EndY=6 EndZ=0
  constraints (14):
    c: Coincident(g0,g-1)
    c: Distance(g0) = 6
    c: Vertical(g0)
    c: Coincident(g3,g0)
    c: Weight(g1) = 1
    c: Equal(g1,g2)
    c: InternalAlignment(g1,g3)
    c: InternalAlignment(g2,g3)
    c: InternalAlignment(g4,g3)
    c: InternalAlignment(g5,g3)
    c: Block(g3)
    c: Coincident(g6,g0)
    c: Coincident(g6,g3)
    c: Horizontal(g6)
FEATURE [Part::Extrusion] Extrude013  label="caseScrewPillarBracket001"
  Base = -> Sketch019
  Dir = (0,0,1)
  DirMode = 2
  FaceMakerClass = Part::FaceMakerBullseye
  LengthFwd = 2.4
  LengthRev = 0
  Placement = pos=(15.76,29,60.8) rot=(0,0,1;0rad)
  Solid = true
  Symmetric = false
FEATURE [Sketcher::SketchObject] Sketch020
  FullyConstrained = true
  sketch-geometry (7):
    g0: LineSegment StartX=0 StartY=0 StartZ=0 EndX=0 EndY=6 EndZ=0
    g1: Circle CenterX=0 CenterY=0 CenterZ=0 NormalX=0 NormalY=0 NormalZ=1 AngleXU=0 Radius=1
    g2: Circle CenterX=8 CenterY=6 CenterZ=0 NormalX=0 NormalY=0 NormalZ=1 AngleXU=0 Radius=1
    g3: BSplineCurve PolesCount=3 KnotsCount=2 Degree=2 IsPeriodic=0
    g4: GeomPoint X=0 Y=0 Z=0
    g5: GeomPoint X=8 Y=6 Z=0
    g6: LineSegment StartX=0 StartY=6 StartZ=0 EndX=8 EndY=6 EndZ=0
  constraints (14):
    c: Coincident(g0,g-1)
    c: Distance(g0) = 6
    c: Vertical(g0)
    c: Coincident(g3,g0)
    c: Weight(g1) = 1
    c: Equal(g1,g2)
    c: InternalAlignment(g1,g3)
    c: InternalAlignment(g2,g3)
    c: InternalAlignment(g4,g3)
    c: InternalAlignment(g5,g3)
    c: Block(g3)
    c: Coincident(g6,g0)
    c: Coincident(g6,g3)
    c: Horizontal(g6)
FEATURE [Part::Extrusion] Extrude014  label="caseScrewPillarBracket002"
  Base = -> Sketch020
  Dir = (0,0,1)
  DirMode = 2
  FaceMakerClass = Part::FaceMakerBullseye
  LengthFwd = 2.4
  LengthRev = 0
  Placement = pos=(13.7,29,13.26) rot=(0,-1,0;1.5708rad)
  Solid = true
  Symmetric = false
FEATURE [Sketcher::SketchObject] Sketch021
  FullyConstrained = true
  sketch-geometry (7):
    g0: LineSegment StartX=0 StartY=0 StartZ=0 EndX=0 EndY=6 EndZ=0
    g1: Circle CenterX=0 CenterY=0 CenterZ=0 NormalX=0 NormalY=0 NormalZ=1 AngleXU=0 Radius=1
    g2: Circle CenterX=8 CenterY=6 CenterZ=0 NormalX=0 NormalY=0 NormalZ=1 AngleXU=0 Radius=1
    g3: BSplineCurve PolesCount=3 KnotsCount=2 Degree=2 IsPeriodic=0
    g4: GeomPoint X=0 Y=0 Z=0
    g5: GeomPoint X=8 Y=6 Z=0
    g6: LineSegment StartX=0 StartY=6 StartZ=0 EndX=8 EndY=6 EndZ=0
  constraints (14):
    c: Coincident(g0,g-1)
    c: Distance(g0) = 6
    c: Vertical(g0)
    c: Coincident(g3,g0)
    c: Weight(g1) = 1
    c: Equal(g1,g2)
    c: InternalAlignment(g1,g3)
    c: InternalAlignment(g2,g3)
    c: InternalAlignment(g4,g3)
    c: InternalAlignment(g5,g3)
    c: Block(g3)
    c: Coincident(g6,g0)
    c: Coincident(g6,g3)
    c: Horizontal(g6)
FEATURE [Part::Extrusion] Extrude015  label="caseScrewPillarBracket003"
  Base = -> Sketch021
  Dir = (0,0,1)
  DirMode = 2
  FaceMakerClass = Part::FaceMakerBullseye
  LengthFwd = 2.4
  LengthRev = 0
  Placement = pos=(11.3,29,58.74) rot=(0,1,0;1.5708rad)
  Solid = true
  Symmetric = false
FEATURE [Sketcher::SketchObject] Sketch022
  FullyConstrained = true
  sketch-geometry (7):
    g0: LineSegment StartX=0 StartY=0 StartZ=0 EndX=0 EndY=6 EndZ=0
    g1: Circle CenterX=0 CenterY=0 CenterZ=0 NormalX=0 NormalY=0 NormalZ=1 AngleXU=0 Radius=1
    g2: Circle CenterX=8 CenterY=6 CenterZ=0 NormalX=0 NormalY=0 NormalZ=1 AngleXU=0 Radius=1
    g3: BSplineCurve PolesCount=3 KnotsCount=2 Degree=2 IsPeriodic=0
    g4: GeomPoint X=0 Y=0 Z=0
    g5: GeomPoint X=8 Y=6 Z=0
    g6: LineSegment StartX=0 StartY=6 StartZ=0 EndX=8 EndY=6 EndZ=0
  constraints (14):
    c: Coincident(g0,g-1)
    c: Distance(g0) = 6
    c: Vertical(g0)
    c: Coincident(g3,g0)
    c: Weight(g1) = 1
    c: Equal(g1,g2)
    c: InternalAlignment(g1,g3)
    c: InternalAlignment(g2,g3)
    c: InternalAlignment(g4,g3)
    c: InternalAlignment(g5,g3)
    c: Block(g3)
    c: Coincident(g6,g0)
    c: Coincident(g6,g3)
    c: Horizontal(g6)
FEATURE [Part::Extrusion] Extrude016  label="caseScrewPillarBracket004"
  Base = -> Sketch022
  Dir = (0,0,1)
  DirMode = 2
  FaceMakerClass = Part::FaceMakerBullseye
  LengthFwd = 2.4
  LengthRev = 0
  Placement = pos=(88.3,29,65.23) rot=(0,1,0;1.5708rad)
  Solid = true
  Symmetric = false
FEATURE [Sketcher::SketchObject] Sketch023
  FullyConstrained = true
  sketch-geometry (7):
    g0: LineSegment StartX=0 StartY=0 StartZ=0 EndX=0 EndY=6 EndZ=0
    g1: Circle CenterX=0 CenterY=0 CenterZ=0 NormalX=0 NormalY=0 NormalZ=1 AngleXU=0 Radius=1
    g2: Circle CenterX=8 CenterY=6 CenterZ=0 NormalX=0 NormalY=0 NormalZ=1 AngleXU=0 Radius=1
    g3: BSplineCurve PolesCount=3 KnotsCount=2 Degree=2 IsPeriodic=0
    g4: GeomPoint X=0 Y=0 Z=0
    g5: GeomPoint X=8 Y=6 Z=0
    g6: LineSegment StartX=0 StartY=6 StartZ=0 EndX=8 EndY=6 EndZ=0
  constraints (14):
    c: Coincident(g0,g-1)
    c: Distance(g0) = 6
    c: Vertical(g0)
    c: Coincident(g3,g0)
    c: Weight(g1) = 1
    c: Equal(g1,g2)
    c: InternalAlignment(g1,g3)
    c: InternalAlignment(g2,g3)
    c: InternalAlignment(g4,g3)
    c: InternalAlignment(g5,g3)
    c: Block(g3)
    c: Coincident(g6,g0)
    c: Coincident(g6,g3)
    c: Horizontal(g6)
FEATURE [Part::Extrusion] Extrude017  label="caseScrewPillarBracket005"
  Base = -> Sketch023
  Dir = (0,0,1)
  DirMode = 2
  FaceMakerClass = Part::FaceMakerBullseye
  LengthFwd = 2.4
  LengthRev = 0
  Placement = pos=(90.7,29,6.77) rot=(0,-1,0;1.5708rad)
  Solid = true
  Symmetric = false
FEATURE [Sketcher::SketchObject] Sketch024
  FullyConstrained = true
  sketch-geometry (7):
    g0: LineSegment StartX=0 StartY=0 StartZ=0 EndX=0 EndY=6 EndZ=0
    g1: Circle CenterX=0 CenterY=0 CenterZ=0 NormalX=0 NormalY=0 NormalZ=1 AngleXU=0 Radius=1
    g2: Circle CenterX=8 CenterY=6 CenterZ=0 NormalX=0 NormalY=0 NormalZ=1 AngleXU=0 Radius=1
    g3: BSplineCurve PolesCount=3 KnotsCount=2 Degree=2 IsPeriodic=0
    g4: GeomPoint X=0 Y=0 Z=0
    g5: GeomPoint X=8 Y=6 Z=0
    g6: LineSegment StartX=0 StartY=6 StartZ=0 EndX=8 EndY=6 EndZ=0
  constraints (14):
    c: Coincident(g0,g-1)
    c: Distance(g0) = 6
    c: Vertical(g0)
    c: Coincident(g3,g0)
    c: Weight(g1) = 1
    c: Equal(g1,g2)
    c: InternalAlignment(g1,g3)
    c: InternalAlignment(g2,g3)
    c: InternalAlignment(g4,g3)
    c: InternalAlignment(g5,g3)
    c: Block(g3)
    c: Coincident(g6,g0)
    c: Coincident(g6,g3)
    c: Horizontal(g6)
FEATURE [Part::Extrusion] Extrude018  label="caseScrewPillarBracket006"
  Base = -> Sketch024
  Dir = (0,0,1)
  DirMode = 2
  FaceMakerClass = Part::FaceMakerBullseye
  LengthFwd = 2.4
  LengthRev = 0
  Placement = pos=(103.7,29,6.77) rot=(0,-1,0;1.5708rad)
  Solid = true
  Symmetric = false
FEATURE [Sketcher::SketchObject] Sketch025
  FullyConstrained = true
  sketch-geometry (7):
    g0: LineSegment StartX=0 StartY=0 StartZ=0 EndX=0 EndY=6 EndZ=0
    g1: Circle CenterX=0 CenterY=0 CenterZ=0 NormalX=0 NormalY=0 NormalZ=1 AngleXU=0 Radius=1
    g2: Circle CenterX=8 CenterY=6 CenterZ=0 NormalX=0 NormalY=0 NormalZ=1 AngleXU=0 Radius=1
    g3: BSplineCurve PolesCount=3 KnotsCount=2 Degree=2 IsPeriodic=0
    g4: GeomPoint X=0 Y=0 Z=0
    g5: GeomPoint X=8 Y=6 Z=0
    g6: LineSegment StartX=0 StartY=6 StartZ=0 EndX=8 EndY=6 EndZ=0
  constraints (14):
    c: Coincident(g0,g-1)
    c: Distance(g0) = 6
    c: Vertical(g0)
    c: Coincident(g3,g0)
    c: Weight(g1) = 1
    c: Equal(g1,g2)
    c: InternalAlignment(g1,g3)
    c: InternalAlignment(g2,g3)
    c: InternalAlignment(g4,g3)
    c: InternalAlignment(g5,g3)
    c: Block(g3)
    c: Coincident(g6,g0)
    c: Coincident(g6,g3)
    c: Horizontal(g6)
FEATURE [Part::Extrusion] Extrude019  label="caseScrewPillarBracket007"
  Base = -> Sketch025
  Dir = (0,0,1)
  DirMode = 2
  FaceMakerClass = Part::FaceMakerBullseye
  LengthFwd = 2.4
  LengthRev = 0
  Placement = pos=(101.3,29,65.23) rot=(0,1,0;1.5708rad)
  Solid = true
  Symmetric = false
FEATURE [Part::Box] Box011  label="frontCaseScrewPillarBracket"
  AttacherType = Attacher::AttachEngine3D
  Height = 2.4
  Length = 16
  Placement = pos=(87,28,2.3) rot=(0,0,1;0rad)
  Width = 7
FEATURE [Part::Box] Box012  label="frontCaseScrewPillarBracket001"
  AttacherType = Attacher::AttachEngine3D
  Height = 2.4
  Length = 16
  Placement = pos=(87,28,67.3) rot=(0,0,1;0rad)
  Width = 7
FEATURE [Sketcher::SketchObject] Sketch026
  FullyConstrained = true
  sketch-geometry (17):
    g0: Circle CenterX=-3.5 CenterY=23.5 CenterZ=0 NormalX=0 NormalY=0 NormalZ=1 AngleXU=0 Radius=1
    g1: Circle CenterX=-1 CenterY=15.25 CenterZ=0 NormalX=0 NormalY=0 NormalZ=1 AngleXU=0 Radius=1
    g2: Circle CenterX=-3.5 CenterY=7 CenterZ=0 NormalX=0 NormalY=0 NormalZ=1 AngleXU=0 Radius=1
    g3: BSplineCurve PolesCount=3 KnotsCount=2 Degree=2 IsPeriodic=0
    g4: GeomPoint X=-3.5 Y=23.5 Z=0
    g5: GeomPoint X=-3.5 Y=7 Z=0
    g6: Circle CenterX=-4.8 CenterY=30.5 CenterZ=0 NormalX=0 NormalY=0 NormalZ=1 AngleXU=0 Radius=1
    g7: Circle CenterX=-3.5 CenterY=30.5 CenterZ=0 NormalX=0 NormalY=0 NormalZ=1 AngleXU=0 Radius=1
    g8: Circle CenterX=-3.5 CenterY=29.2 CenterZ=0 NormalX=0 NormalY=0 NormalZ=1 AngleXU=0 Radius=1
    g9: BSplineCurve PolesCount=3 KnotsCount=2 Degree=2 IsPeriodic=0
    g10: GeomPoint X=-4.8 Y=30.5 Z=0
    g11: GeomPoint X=-3.5 Y=29.2 Z=0
    g12: LineSegment StartX=-3.5 StartY=29.2 StartZ=0 EndX=-3.5 EndY=23.5 EndZ=0
    g13: LineSegment StartX=-4.8 StartY=30.5 StartZ=0 EndX=0 EndY=30.5 EndZ=0
    g14: LineSegment StartX=-3.5 StartY=5 StartZ=0 EndX=-3.5 EndY=7 EndZ=0
    g15: LineSegment StartX=0 StartY=5 StartZ=0 EndX=0 EndY=30.5 EndZ=0
    g16: LineSegment StartX=-3.5 StartY=5 StartZ=0 EndX=0 EndY=5 EndZ=0
  constraints (33):
    c: Weight(g0) = 1
    c: Equal(g0,g1)
    c: Equal(g0,g2)
    c: InternalAlignment(g0,g3)
    c: InternalAlignment(g1,g3)
    c: InternalAlignment(g2,g3)
    c: InternalAlignment(g4,g3)
    c: InternalAlignment(g5,g3)
    c: Block(g3)
    c: Weight(g6) = 1
    c: Equal(g6,g7)
    c: Equal(g6,g8)
    c: InternalAlignment(g6,g9)
    c: InternalAlignment(g7,g9)
    c: InternalAlignment(g8,g9)
    c: InternalAlignment(g10,g9)
    c: InternalAlignment(g11,g9)
    c: Block(g9)
    c: Coincident(g12,g9)
    c: Coincident(g12,g3)
    c: Vertical(g12)
    c: Coincident(g13,g9)
    c: Horizontal(g13)
    c: Distance(g13) = 4.8
    c: Coincident(g14,g3)
    c: Vertical(g14)
    c: Coincident(g15,g13)
    c: Vertical(g15)
    c: Tangent(g15,g1)
    c: Distance(g14) = 2
    c: Coincident(g16,g14)
    c: Horizontal(g16)
    c: Coincident(g15,g16)
FEATURE [Part::Feature] Face050
  shape: bbox 4.8 x 25.5 x 2e-07 mm, 1 faces, 0 solids (baked)
FEATURE [Part::Revolution] Revolve054  label="moreFrontCaseScrewPost001"
  Angle = 360
  Axis = (0,1,0)
  Base = (0,0,0)
  FaceMakerClass = Part::FaceMakerBullseye
  Placement = pos=(102.5,4.5,3.5) rot=(0,0,1;0rad)
  Solid = false
  Source = -> Face050
  Symmetric = false
FEATURE [Part::Feature] Face051
  shape: bbox 4.8 x 25.5 x 2e-07 mm, 1 faces, 0 solids (baked)
FEATURE [Part::Revolution] Revolve055  label="moreFrontCaseScrewPost002"
  Angle = 360
  Axis = (0,1,0)
  Base = (0,0,0)
  FaceMakerClass = Part::FaceMakerBullseye
  Placement = pos=(102.5,4.5,68.5) rot=(0,0,1;0rad)
  Solid = false
  Source = -> Face051
  Symmetric = false
FEATURE [Sketcher::SketchObject] Sketch027
  FullyConstrained = true
  sketch-geometry (10):
    g0: LineSegment StartX=-1.6 StartY=4.7 StartZ=0 EndX=-1.6 EndY=1.7 EndZ=0
    g1: LineSegment StartX=-3.5 StartY=4.7 StartZ=0 EndX=-1.6 EndY=4.7 EndZ=0
    g2: LineSegment StartX=-1.6 StartY=1.7 StartZ=0 EndX=-1.6 EndY=1.5 EndZ=0
    g3: LineSegment StartX=-1.6 StartY=1.5 StartZ=0 EndX=-5.2 EndY=1.5 EndZ=0
    g4: Circle CenterX=-3.5 CenterY=4.7 CenterZ=0 NormalX=0 NormalY=0 NormalZ=1 AngleXU=0 Radius=1
    g5: Circle CenterX=-3.59627 CenterY=2.99743 CenterZ=0 NormalX=0 NormalY=0 NormalZ=1 AngleXU=0 Radius=1
    g6: Circle CenterX=-5.2 CenterY=1.5 CenterZ=0 NormalX=0 NormalY=0 NormalZ=1 AngleXU=0 Radius=1
    g7: BSplineCurve PolesCount=3 KnotsCount=2 Degree=2 IsPeriodic=0
    g8: GeomPoint X=-3.5 Y=4.7 Z=0
    g9: GeomPoint X=-5.2 Y=1.5 Z=0
  constraints (23):
    c: Vertical(g0)
    c: Distance(g0) = 3
    c: Coincident(g1,g0)
    c: Horizontal(g1)
    c: Block(g0)
    c: Block(g1)
    c: Coincident(g2,g0)
    c: Vertical(g2)
    c: Distance(g2) = 0.2
    c: Coincident(g3,g2)
    c: Horizontal(g3)
    c: Block(g3)
    c: Coincident(g7,g1)
    c: Weight(g4) = 1
    c: Equal(g4,g5)
    c: Equal(g4,g6)
    c: Coincident(g7,g3)
    c: InternalAlignment(g4,g7)
    c: InternalAlignment(g5,g7)
    c: InternalAlignment(g6,g7)
    c: InternalAlignment(g8,g7)
    c: InternalAlignment(g9,g7)
    c: Block(g7)
FEATURE [Sketcher::SketchObject] Sketch028
  FullyConstrained = true
  sketch-geometry (18):
    g0: LineSegment StartX=0 StartY=3e-16 StartZ=0 EndX=0 EndY=1.7 EndZ=0
    g1: LineSegment StartX=-3.5 StartY=0 StartZ=0 EndX=-3.5 EndY=0.9 EndZ=0
    g2: Circle CenterX=-2.7 CenterY=1.7 CenterZ=0 NormalX=0 NormalY=0 NormalZ=1 AngleXU=0 Radius=1
    g3: Circle CenterX=-3.5 CenterY=1.7 CenterZ=0 NormalX=0 NormalY=0 NormalZ=1 AngleXU=0 Radius=1
    g4: Circle CenterX=-3.5 CenterY=0.9 CenterZ=0 NormalX=0 NormalY=0 NormalZ=1 AngleXU=0 Radius=1
    g5: BSplineCurve PolesCount=3 KnotsCount=2 Degree=2 IsPeriodic=0
    g6: GeomPoint X=-2.7 Y=1.7 Z=0
    g7: GeomPoint X=-3.5 Y=0.9 Z=0
    g8: LineSegment StartX=-3.5 StartY=0 StartZ=0 EndX=-3.5 EndY=-7 EndZ=0
    g9: LineSegment StartX=0 StartY=3e-16 StartZ=0 EndX=0 EndY=-7 EndZ=0
    g10: LineSegment StartX=-3.5 StartY=-7 StartZ=0 EndX=0 EndY=-7 EndZ=0
    g11: LineSegment StartX=-2.7 StartY=1.7 StartZ=0 EndX=-1.6 EndY=1.7 EndZ=0
    g12: LineSegment StartX=0 StartY=1.7 StartZ=0 EndX=0 EndY=4.5 EndZ=0
    g13: LineSegment StartX=0 StartY=4.5 StartZ=0 EndX=0 EndY=10.8 EndZ=0
    g14: LineSegment StartX=0 StartY=10.8 StartZ=0 EndX=-2 EndY=10.8 EndZ=0
    g15: LineSegment StartX=-1.6 StartY=4.7 StartZ=0 EndX=-1.6 EndY=1.7 EndZ=0
    g16: LineSegment StartX=-1.6 StartY=4.7 StartZ=0 EndX=-2 EndY=4.7 EndZ=0
    g17: LineSegment StartX=-2 StartY=4.7 StartZ=0 EndX=-2 EndY=10.8 EndZ=0
  constraints (44):
    c: Vertical(g0)
    c: Vertical(g1)
    c: Distance(g1) = 0.9
    c: Block(g0)
    c: Distance(g0) = 1.7
    c: Weight(g2) = 1
    c: Equal(g2,g3)
    c: Equal(g2,g4)
    c: Coincident(g5,g1)
    c: InternalAlignment(g2,g5)
    c: InternalAlignment(g3,g5)
    c: InternalAlignment(g4,g5)
    c: InternalAlignment(g6,g5)
    c: InternalAlignment(g7,g5)
    c: Block(g5)
    c: Coincident(g8,g1)
    c: Vertical(g8)
    c: Distance(g8) = 7
    c: Vertical(g9)
    c: Equal(g8,g9) = 7
    c: Coincident(g9,g0)
    c: Coincident(g10,g8)
    c: Coincident(g10,g9)
    c: Horizontal(g10)
    c: Coincident(g11,g5)
    c: Horizontal(g11)
    c: Coincident(g12,g0)
    c: Vertical(g12)
    c: Distance(g12) = 2.8
    c: Coincident(g13,g12)
    c: Vertical(g13)
    c: Distance(g13) = 6.3
    c: Coincident(g14,g13)
    c: Horizontal(g14)
    c: Distance(g14) = 2
    c: Vertical(g15)
    c: Distance(g15) = 3
    c: Block(g11)
    c: Coincident(g15,g11)
    c: Coincident(g16,g15)
    c: Horizontal(g16)
    c: Coincident(g17,g16)
    c: Coincident(g17,g14)
    c: Vertical(g17)
FEATURE [Part::Revolution] Revolve040  label="backCaseScrewRetainer001"
  Angle = 360
  Axis = (0,1,0)
  Base = (0,0,0)
  FaceMakerClass = Part::FaceMakerBullseye
  Placement = pos=(12.5,3,10) rot=(0,0,1;0rad)
  Solid = false
  Source = -> Face036
  Symmetric = false
FEATURE [Part::Feature] Face055
  shape: bbox 3.5 x 30.2 x 2e-07 mm, 1 faces, 0 solids (baked)
FEATURE [Part::Revolution] Revolve059  label="backCaseScrewPost"
  Angle = 360
  Axis = (0,1,0)
  Base = (0,0,0)
  FaceMakerClass = Part::FaceMakerBullseye
  Placement = pos=(12.5,4.5,10) rot=(0,0,1;0rad)
  Solid = false
  Source = -> Face055
  Symmetric = false
FEATURE [Part::Feature] Face056
  shape: bbox 3.5 x 30.2 x 2e-07 mm, 1 faces, 0 solids (baked)
FEATURE [Part::Revolution] Revolve060  label="backCaseScrewPost001"
  Angle = 360
  Axis = (0,1,0)
  Base = (0,0,0)
  FaceMakerClass = Part::FaceMakerBullseye
  Placement = pos=(12.5,4.5,62) rot=(0,0,1;0rad)
  Solid = false
  Source = -> Face056
  Symmetric = false
FEATURE [Part::Feature] Face057
  shape: bbox 3.5 x 17.8 x 2e-07 mm, 1 faces, 0 solids (baked)
FEATURE [Part::Revolution] Revolve061  label="removeToCreateScrewAndThreadedInsertHole"
  Angle = 360
  Axis = (0,1,0)
  Base = (0,0,0)
  FaceMakerClass = Part::FaceMakerBullseye
  Placement = pos=(12.5,0,10) rot=(0,0,1;0rad)
  Solid = false
  Source = -> Face057
  Symmetric = false
FEATURE [Part::Feature] Face058
  shape: bbox 3.5 x 17.8 x 2e-07 mm, 1 faces, 0 solids (baked)
FEATURE [Part::Revolution] Revolve062  label="removeToCreateScrewAndThreadedInsertHole001"
  Angle = 360
  Axis = (0,1,0)
  Base = (0,0,0)
  FaceMakerClass = Part::FaceMakerBullseye
  Placement = pos=(12.5,0,62) rot=(0,0,1;0rad)
  Solid = false
  Source = -> Face058
  Symmetric = false
FEATURE [Part::Feature] Face059
  shape: bbox 3.5 x 17.8 x 2e-07 mm, 1 faces, 0 solids (baked)
FEATURE [Part::Revolution] Revolve063  label="removeToCreateScrewAndThreadedInsertHole002"
  Angle = 360
  Axis = (0,1,0)
  Base = (0,0,0)
  FaceMakerClass = Part::FaceMakerBullseye
  Placement = pos=(89.5,0,68.5) rot=(0,0,1;0rad)
  Solid = false
  Source = -> Face059
  Symmetric = false
FEATURE [Part::Feature] Face060
  shape: bbox 3.5 x 17.8 x 2e-07 mm, 1 faces, 0 solids (baked)
FEATURE [Part::Revolution] Revolve064  label="removeToCreateScrewAndThreadedInsertHole003"
  Angle = 360
  Axis = (0,1,0)
  Base = (0,0,0)
  FaceMakerClass = Part::FaceMakerBullseye
  Placement = pos=(89.5,0,3.5) rot=(0,0,1;0rad)
  Solid = false
  Source = -> Face060
  Symmetric = false
FEATURE [Part::Feature] Face061
  shape: bbox 3.5 x 17.8 x 2e-07 mm, 1 faces, 0 solids (baked)
FEATURE [Part::Revolution] Revolve065  label="removeToCreateScrewAndThreadedInsertHole004"
  Angle = 360
  Axis = (0,1,0)
  Base = (0,0,0)
  FaceMakerClass = Part::FaceMakerBullseye
  Placement = pos=(102.5,4.7,3.5) rot=(0,0,1;0rad)
  Solid = false
  Source = -> Face061
  Symmetric = false
FEATURE [Part::Feature] Face062
  shape: bbox 3.5 x 17.8 x 2e-07 mm, 1 faces, 0 solids (baked)
FEATURE [Part::Revolution] Revolve066  label="removeToCreateScrewAndThreadedInsertHole005"
  Angle = 360
  Axis = (0,1,0)
  Base = (0,0,0)
  FaceMakerClass = Part::FaceMakerBullseye
  Placement = pos=(102.5,4.7,68.5) rot=(0,0,1;0rad)
  Solid = false
  Source = -> Face062
  Symmetric = false
FEATURE [Part::MultiFuse] Fusion047  label="makeHoles"
  Shapes = -> [Revolve066,Revolve065,Revolve064,Revolve063,Revolve062,Revolve061]
FEATURE [Part::Feature] Face063
  shape: bbox 3.6 x 3.2 x 2e-07 mm, 1 faces, 0 solids (baked)
FEATURE [Part::Revolution] Revolve067  label="moreFrontCaseScrewRetainer002"
  Angle = 360
  Axis = (0,1,0)
  Base = (0,0,0)
  FaceMakerClass = Part::FaceMakerBullseye
  Placement = pos=(102.5,4.5,68.5) rot=(0,0,1;0rad)
  Solid = false
  Source = -> Face063
  Symmetric = false
FEATURE [Part::Feature] Face064
  shape: bbox 3.6 x 3.2 x 2e-07 mm, 1 faces, 0 solids (baked)
FEATURE [Part::Revolution] Revolve068  label="moreFrontCaseScrewRetainer003"
  Angle = 360
  Axis = (0,1,0)
  Base = (0,0,0)
  FaceMakerClass = Part::FaceMakerBullseye
  Placement = pos=(102.5,4.5,3.5) rot=(0,0,1;0rad)
  Solid = false
  Source = -> Face064
  Symmetric = false
FEATURE [Part::Feature] Face065
  shape: bbox 3.5 x 17.8 x 2e-07 mm, 1 faces, 0 solids (baked)
FEATURE [Part::Revolution] Revolve069  label="removeToCreateScrewAndThreadedInsertHole006"
  Angle = 360
  Axis = (0,1,0)
  Base = (0,0,0)
  FaceMakerClass = Part::FaceMakerBullseye
  Placement = pos=(12.5,0,10) rot=(0,0,1;0rad)
  Solid = false
  Source = -> Face065
  Symmetric = false
FEATURE [Part::Feature] Face066
  shape: bbox 3.5 x 17.8 x 2e-07 mm, 1 faces, 0 solids (baked)
FEATURE [Part::Revolution] Revolve070  label="removeToCreateScrewAndThreadedInsertHole007"
  Angle = 360
  Axis = (0,1,0)
  Base = (0,0,0)
  FaceMakerClass = Part::FaceMakerBullseye
  Placement = pos=(12.5,0,62) rot=(0,0,1;0rad)
  Solid = false
  Source = -> Face066
  Symmetric = false
FEATURE [Part::Feature] Face067
  shape: bbox 3.5 x 17.8 x 2e-07 mm, 1 faces, 0 solids (baked)
FEATURE [Part::Revolution] Revolve071  label="removeToCreateScrewAndThreadedInsertHole008"
  Angle = 360
  Axis = (0,1,0)
  Base = (0,0,0)
  FaceMakerClass = Part::FaceMakerBullseye
  Placement = pos=(89.5,0,68.5) rot=(0,0,1;0rad)
  Solid = false
  Source = -> Face067
  Symmetric = false
FEATURE [Part::Feature] Face068
  shape: bbox 3.5 x 17.8 x 2e-07 mm, 1 faces, 0 solids (baked)
FEATURE [Part::Revolution] Revolve072  label="removeToCreateScrewAndThreadedInsertHole009"
  Angle = 360
  Axis = (0,1,0)
  Base = (0,0,0)
  FaceMakerClass = Part::FaceMakerBullseye
  Placement = pos=(89.5,0,3.5) rot=(0,0,1;0rad)
  Solid = false
  Source = -> Face068
  Symmetric = false
FEATURE [Part::Feature] Face069
  shape: bbox 3.5 x 17.8 x 2e-07 mm, 1 faces, 0 solids (baked)
FEATURE [Part::Feature] Face070
  shape: bbox 3.5 x 17.8 x 2e-07 mm, 1 faces, 0 solids (baked)
FEATURE [Part::Revolution] Revolve073  label="removeToCreateScrewAndThreadedInsertHole010"
  Angle = 360
  Axis = (0,1,0)
  Base = (0,0,0)
  FaceMakerClass = Part::FaceMakerBullseye
  Placement = pos=(102.5,4.7,3.5) rot=(0,0,1;0rad)
  Solid = false
  Source = -> Face069
  Symmetric = false
FEATURE [Part::Revolution] Revolve074  label="removeToCreateScrewAndThreadedInsertHole011"
  Angle = 360
  Axis = (0,1,0)
  Base = (0,0,0)
  FaceMakerClass = Part::FaceMakerBullseye
  Placement = pos=(102.5,4.7,68.5) rot=(0,0,1;0rad)
  Solid = false
  Source = -> Face070
  Symmetric = false
FEATURE [Part::MultiFuse] Fusion048  label="makeHoles001"
  Shapes = -> [Revolve074,Revolve073,Revolve072,Revolve071,Revolve070,Revolve069]
FEATURE [Part::MultiFuse] Fusion049  label="caseScrewRetainers"
  Shapes = -> [Revolve067,Revolve068,Revolve048,Revolve047,Revolve039,Revolve040]
FEATURE [Part::Cut] Cut015  label="caseScrewRetainers001"
  Base = -> Fusion049
  Tool = -> Fusion048
FEATURE [Part::MultiFuse] Fusion050  label="casePillars"
  Shapes = -> [Revolve055,Revolve054,Revolve043,Revolve046,Revolve059,Revolve060]
FEATURE [Part::Feature] Face071 .. Face076  x6 (patterned run collapsed; names and placements below)
  shape: bbox 3.5 x 17.8 x 2e-07 mm, 1 faces, 0 solids (baked)
FEATURE [Part::Revolution] Revolve075  label="removeToCreateScrewAndThreadedInsertHole012"
  Angle = 360
  Axis = (0,1,0)
  Base = (0,0,0)
  FaceMakerClass = Part::FaceMakerBullseye
  Placement = pos=(12.5,0,10) rot=(0,0,1;0rad)
  Solid = false
  Source = -> Face071
  Symmetric = false
FEATURE [Part::Revolution] Revolve076  label="removeToCreateScrewAndThreadedInsertHole013"
  Angle = 360
  Axis = (0,1,0)
  Base = (0,0,0)
  FaceMakerClass = Part::FaceMakerBullseye
  Placement = pos=(12.5,0,62) rot=(0,0,1;0rad)
  Solid = false
  Source = -> Face072
  Symmetric = false
FEATURE [Part::Revolution] Revolve077  label="removeToCreateScrewAndThreadedInsertHole014"
  Angle = 360
  Axis = (0,1,0)
  Base = (0,0,0)
  FaceMakerClass = Part::FaceMakerBullseye
  Placement = pos=(89.5,0,68.5) rot=(0,0,1;0rad)
  Solid = false
  Source = -> Face073
  Symmetric = false
FEATURE [Part::Revolution] Revolve078  label="removeToCreateScrewAndThreadedInsertHole015"
  Angle = 360
  Axis = (0,1,0)
  Base = (0,0,0)
  FaceMakerClass = Part::FaceMakerBullseye
  Placement = pos=(89.5,0,3.5) rot=(0,0,1;0rad)
  Solid = false
  Source = -> Face074
  Symmetric = false
FEATURE [Part::Revolution] Revolve079  label="removeToCreateScrewAndThreadedInsertHole016"
  Angle = 360
  Axis = (0,1,0)
  Base = (0,0,0)
  FaceMakerClass = Part::FaceMakerBullseye
  Placement = pos=(102.5,4.7,3.5) rot=(0,0,1;0rad)
  Solid = false
  Source = -> Face075
  Symmetric = false
FEATURE [Part::Revolution] Revolve080  label="removeToCreateScrewAndThreadedInsertHole017"
  Angle = 360
  Axis = (0,1,0)
  Base = (0,0,0)
  FaceMakerClass = Part::FaceMakerBullseye
  Placement = pos=(102.5,4.7,68.5) rot=(0,0,1;0rad)
  Solid = false
  Source = -> Face076
  Symmetric = false
FEATURE [Part::MultiFuse] Fusion051  label="makeHoles002"
  Shapes = -> [Revolve080,Revolve079,Revolve078,Revolve077,Revolve076,Revolve075]
FEATURE [Part::Cut] Cut016  label="caesPillars"
  Base = -> Fusion050
  Tool = -> Fusion051
FEATURE [Part::Revolution] Revolve009  label="plugHousing016"
  Angle = 360
  Axis = (0,1,0)
  Base = (0,0,0)
  FaceMakerClass = Part::FaceMakerBullseye
  Placement = pos=(0,0,36.15) rot=(0,0,1;0rad)
  Solid = false
  Source = -> Face012
  Symmetric = false
FEATURE [Part::MultiFuse] Fusion014  label="plugHousing023"
  Placement = pos=(0,0,0) rot=(0,0,1;1.5708rad)
  Shapes = -> [Revolve011,Revolve009]
FEATURE [Part::Revolution] Revolve010  label="plugHousing017"
  Angle = 360
  Axis = (0,1,0)
  Base = (0,0,0)
  FaceMakerClass = Part::FaceMakerBullseye
  Placement = pos=(0,0,36.15) rot=(0,0,1;0rad)
  Solid = false
  Source = -> Face014
  Symmetric = false
FEATURE [Part::MultiFuse] Fusion015  label="plugHousing024"
  Placement = pos=(0,0,0) rot=(0,0,1;1.5708rad)
  Shapes = -> [Revolve010,Revolve015]
FEATURE [Part::Revolution] Revolve014  label="plugHousing026"
  Angle = 360
  Axis = (0,1,0)
  Base = (0,0,0)
  FaceMakerClass = Part::FaceMakerBullseye
  Placement = pos=(0,0,36.15) rot=(0,0,1;0rad)
  Solid = false
  Source = -> Face011
  Symmetric = false
FEATURE [Part::Revolution] Revolve013  label="plugHousing025"
  Angle = 360
  Axis = (0,1,0)
  Base = (0,0,0)
  FaceMakerClass = Part::FaceMakerBullseye
  Placement = pos=(0,0,36.15) rot=(0,0,1;0rad)
  Solid = false
  Source = -> Face015
  Symmetric = false
FEATURE [Part::MultiFuse] Fusion016  label="plugHousing028"
  Placement = pos=(0,19,0) rot=(0,0,1;3.14159rad)
  Shapes = -> [Fusion014,Fusion013]
FEATURE [Part::MultiFuse] Fusion011  label="plugHousing018"
  Placement = pos=(0,0,0) rot=(0,0,1;1.5708rad)
  Shapes = -> [Revolve014,Revolve013]
FEATURE [Part::MultiFuse] Fusion012  label="plugHousing019"
  Placement = pos=(0,19,0) rot=(0,0,1;3.14159rad)
  Shapes = -> [Fusion011,Fusion015]
FEATURE [Part::MultiFuse] Fusion017  label="plugHousing029"
  Placement = pos=(122.621,0,-0.15) rot=(0,0,1;0rad)
  Shapes = -> [Fusion016,Fusion012]
FEATURE [Part::MultiFuse] Fusion052  label="casePillarRetainers"
  Shapes = -> [Extrude012,Extrude013,Extrude014,Extrude015,Extrude016,Extrude017,Extrude018,Extrude019,Box011,Box012]
FEATURE [Part::Feature] Face077
  shape: bbox 3.5 x 17.8 x 2e-07 mm, 1 faces, 0 solids (baked)
FEATURE [Part::Revolution] Revolve081  label="removeToCreateScrewAndThreadedInsertHole018"
  Angle = 360
  Axis = (0,1,0)
  Base = (0,0,0)
  FaceMakerClass = Part::FaceMakerBullseye
  Placement = pos=(62.3,30.3,19.7) rot=(0,0,1;0rad)
  Solid = false
  Source = -> Face077
  Symmetric = false
FEATURE [Part::Feature] Face078
  shape: bbox 3.5 x 17.8 x 2e-07 mm, 1 faces, 0 solids (baked)
FEATURE [Part::Revolution] Revolve082  label="removeToCreateScrewAndThreadedInsertHole019"
  Angle = 360
  Axis = (0,1,0)
  Base = (0,0,0)
  FaceMakerClass = Part::FaceMakerBullseye
  Placement = pos=(62.3,30.3,51.7) rot=(0,0,1;0rad)
  Solid = false
  Source = -> Face078
  Symmetric = false
FEATURE [Part::Feature] Face079
  shape: bbox 3.5 x 17.8 x 2e-07 mm, 1 faces, 0 solids (baked)
FEATURE [Part::Revolution] Revolve083  label="removeToCreateScrewAndThreadedInsertHole020"
  Angle = 360
  Axis = (0,1,0)
  Base = (0,0,0)
  FaceMakerClass = Part::FaceMakerBullseye
  Placement = pos=(30.3,30.3,19.7) rot=(0,0,1;0rad)
  Solid = false
  Source = -> Face079
  Symmetric = false
FEATURE [Part::Feature] Face080
  shape: bbox 3.5 x 17.8 x 2e-07 mm, 1 faces, 0 solids (baked)
FEATURE [Part::Revolution] Revolve084  label="removeToCreateScrewAndThreadedInsertHole021"
  Angle = 360
  Axis = (0,1,0)
  Base = (0,0,0)
  FaceMakerClass = Part::FaceMakerBullseye
  Placement = pos=(30.3,30.3,51.7) rot=(0,0,1;0rad)
  Solid = false
  Source = -> Face080
  Symmetric = false
FEATURE [Part::MultiFuse] Fusion053  label="createThreadedInsertHolesForFan"
  Shapes = -> [Revolve081,Revolve082,Revolve083,Revolve084]
FEATURE [Part::Cut] Cut017  label="fanScrewHousing001"
  Base = -> Fusion046
  Tool = -> Fusion053
FEATURE [Part::Feature] Face081
  shape: bbox 3.5 x 17.8 x 2e-07 mm, 1 faces, 0 solids (baked)
FEATURE [Part::Revolution] Revolve085  label="removeToCreateScrewAndThreadedInsertHole022"
  Angle = 360
  Axis = (0,1,0)
  Base = (0,0,0)
  FaceMakerClass = Part::FaceMakerBullseye
  Placement = pos=(62.3,30.3,19.7) rot=(0,0,1;0rad)
  Solid = false
  Source = -> Face081
  Symmetric = false
FEATURE [Part::Feature] Face082
  shape: bbox 3.5 x 17.8 x 2e-07 mm, 1 faces, 0 solids (baked)
FEATURE [Part::Revolution] Revolve086  label="removeToCreateScrewAndThreadedInsertHole023"
  Angle = 360
  Axis = (0,1,0)
  Base = (0,0,0)
  FaceMakerClass = Part::FaceMakerBullseye
  Placement = pos=(62.3,30.3,51.7) rot=(0,0,1;0rad)
  Solid = false
  Source = -> Face082
  Symmetric = false
FEATURE [Part::Feature] Face083
  shape: bbox 3.5 x 17.8 x 2e-07 mm, 1 faces, 0 solids (baked)
FEATURE [Part::Revolution] Revolve087  label="removeToCreateScrewAndThreadedInsertHole024"
  Angle = 360
  Axis = (0,1,0)
  Base = (0,0,0)
  FaceMakerClass = Part::FaceMakerBullseye
  Placement = pos=(30.3,30.3,19.7) rot=(0,0,1;0rad)
  Solid = false
  Source = -> Face083
  Symmetric = false
FEATURE [Part::Feature] Face084
  shape: bbox 3.5 x 17.8 x 2e-07 mm, 1 faces, 0 solids (baked)
FEATURE [Part::Revolution] Revolve088  label="removeToCreateScrewAndThreadedInsertHole025"
  Angle = 360
  Axis = (0,1,0)
  Base = (0,0,0)
  FaceMakerClass = Part::FaceMakerBullseye
  Placement = pos=(30.3,30.3,51.7) rot=(0,0,1;0rad)
  Solid = false
  Source = -> Face084
  Symmetric = false
FEATURE [Part::MultiFuse] Fusion054  label="createThreadedInsertHolesForFan001"
  Shapes = -> [Revolve085,Revolve086,Revolve087,Revolve088]
FEATURE [Part::Cut] Cut018  label="top007"
  Base = -> Fusion040
  Tool = -> Fusion054
FEATURE [Sketcher::SketchObject] Sketch029
  FullyConstrained = false
  Placement = pos=(0,0,0) rot=(1,0,0;1.5708rad)
  sketch-geometry (24):
    g0: ArcOfCircle CenterX=-4 CenterY=-10.5 CenterZ=0 NormalX=0 NormalY=0 NormalZ=1 AngleXU=0 Radius=1.5 StartAngle=6e-16 EndAngle=3.14159
    g1: ArcOfCircle CenterX=-34.2 CenterY=-10.5 CenterZ=0 NormalX=0 NormalY=0 NormalZ=1 AngleXU=0 Radius=1.5 StartAngle=0 EndAngle=3.14159
    g2: ArcOfCircle CenterX=-34.2 CenterY=-27.7 CenterZ=0 NormalX=0 NormalY=0 NormalZ=1 AngleXU=0 Radius=1.5 StartAngle=3.14159 EndAngle=6.28319
    g3: ArcOfCircle CenterX=-4 CenterY=-27.7 CenterZ=0 NormalX=0 NormalY=0 NormalZ=1 AngleXU=0 Radius=1.5 StartAngle=3.1416 EndAngle=6.28319
    g4: ArcOfCircle CenterX=-10 CenterY=-4.3 CenterZ=0 NormalX=0 NormalY=0 NormalZ=1 AngleXU=0 Radius=1.5 StartAngle=2e-16 EndAngle=3.14159
    g5: ArcOfCircle CenterX=-16.1 CenterY=-1.8 CenterZ=0 NormalX=0 NormalY=0 NormalZ=1 AngleXU=0 Radius=1.5 StartAngle=5e-16 EndAngle=3.14159
    g6: ArcOfCircle CenterX=-22.1 CenterY=-1.8 CenterZ=0 NormalX=0 NormalY=0 NormalZ=1 AngleXU=0 Radius=1.5 StartAngle=5e-16 EndAngle=3.14159
    g7: ArcOfCircle CenterX=-28.2 CenterY=-4.3 CenterZ=0 NormalX=0 NormalY=0 NormalZ=1 AngleXU=0 Radius=1.5 StartAngle=2e-16 EndAngle=3.14159
    g8: ArcOfCircle CenterX=-10 CenterY=-33.9 CenterZ=0 NormalX=0 NormalY=0 NormalZ=1 AngleXU=0 Radius=1.5 StartAngle=3.14159 EndAngle=6.28319
    g9: ArcOfCircle CenterX=-16.1 CenterY=-36.4 CenterZ=0 NormalX=0 NormalY=0 NormalZ=1 AngleXU=0 Radius=1.5 StartAngle=3.14159 EndAngle=6.28319
    g10: ArcOfCircle CenterX=-22.1 CenterY=-36.4 CenterZ=0 NormalX=0 NormalY=0 NormalZ=1 AngleXU=0 Radius=1.5 StartAngle=3.14159 EndAngle=6.28319
    g11: ArcOfCircle CenterX=-28.2 CenterY=-33.9 CenterZ=0 NormalX=0 NormalY=0 NormalZ=1 AngleXU=0 Radius=1.5 StartAngle=3.14159 EndAngle=6.28319
    g12: LineSegment StartX=-35.7 StartY=-10.5 StartZ=0 EndX=-35.7 EndY=-27.7 EndZ=0
    g13: LineSegment StartX=-32.7 StartY=-10.5 StartZ=0 EndX=-32.7 EndY=-27.7 EndZ=0
    g14: LineSegment StartX=-29.7 StartY=-33.9 StartZ=0 EndX=-29.7 EndY=-4.3 EndZ=0
    g15: LineSegment StartX=-26.7 StartY=-33.9 StartZ=0 EndX=-26.7 EndY=-4.3 EndZ=0
    g16: LineSegment StartX=-2.5 StartY=-10.5 StartZ=0 EndX=-2.5 EndY=-27.7 EndZ=0
    g17: LineSegment StartX=-8.5 StartY=-4.3 StartZ=0 EndX=-8.5 EndY=-33.9 EndZ=0
    g18: LineSegment StartX=-5.5 StartY=-10.5 StartZ=0 EndX=-5.5 EndY=-27.7 EndZ=0
    g19: LineSegment StartX=-11.5 StartY=-4.3 StartZ=0 EndX=-11.5 EndY=-33.9 EndZ=0
    g20: LineSegment StartX=-14.6 StartY=-1.8 StartZ=0 EndX=-14.6 EndY=-36.4 EndZ=0
    g21: LineSegment StartX=-17.6 StartY=-1.8 StartZ=0 EndX=-17.6 EndY=-36.4 EndZ=0
    g22: LineSegment StartX=-20.6 StartY=-36.4 StartZ=0 EndX=-20.6 EndY=-1.8 EndZ=0
    g23: LineSegment StartX=-23.6 StartY=-1.8 StartZ=0 EndX=-23.6 EndY=-36.4 EndZ=0
  constraints (48):
    c: Block(g0)
    c: Block(g1)
    c: Block(g2)
    c: Block(g3)
    c: Block(g4)
    c: Block(g5)
    c: Block(g6)
    c: Block(g7)
    c: Block(g8)
    c: Block(g9)
    c: Block(g10)
    c: Block(g11)
    c: Coincident(g12,g1)
    c: Coincident(g12,g2)
    c: Vertical(g12)
    c: Coincident(g13,g1)
    c: Coincident(g13,g2)
    c: Vertical(g13)
    c: Coincident(g14,g11)
    c: Coincident(g14,g7)
    c: Vertical(g14)
    c: Coincident(g15,g11)
    c: Coincident(g15,g7)
    c: Vertical(g15)
    c: Coincident(g16,g0)
    c: Coincident(g16,g3)
    c: Vertical(g16)
    c: Coincident(g17,g4)
    c: Coincident(g17,g8)
    c: Vertical(g17)
    c: Coincident(g18,g0)
    c: Coincident(g18,g3)
    c: Vertical(g18)
    c: Coincident(g19,g4)
    c: Coincident(g19,g8)
    c: Vertical(g19)
    c: Coincident(g20,g5)
    c: Coincident(g20,g9)
    c: Vertical(g20)
    c: Coincident(g21,g5)
    c: Coincident(g21,g9)
    c: Vertical(g21)
    c: Coincident(g22,g10)
    c: Coincident(g22,g6)
    c: Vertical(g22)
    c: Coincident(g23,g6)
    c: Coincident(g23,g10)
    c: Vertical(g23)
FEATURE [Part::Extrusion] Extrude020  label="removeToCreateFanGrillHoles"
  Base = -> Sketch029
  Dir = (0,-1,6e-16)
  DirMode = 2
  FaceMakerClass = Part::FaceMakerBullseye
  LengthFwd = 10
  LengthRev = 0
  Placement = pos=(65.4,44,54.82) rot=(0,0,1;0rad)
  Solid = true
  Symmetric = false
FEATURE [Part::MultiFuse] Fusion055  label="top008"
  Shapes = -> [Cut017,Cut018]
FEATURE [Part::Cut] Cut019  label="top009"
  Base = -> Fusion055
  Tool = -> Extrude020
FEATURE [App::MeasureDistance] Distance003  label="Distance: 71.95 mm"
  Distance = 71.9513
  P1 = (117,38,72)
  P2 = (117,38,0.0487319)
FEATURE [Sketcher::SketchObject] Sketch030
  FullyConstrained = true
  Placement = pos=(117,19,0) rot=(0.57735,0.57735,0.57735;2.0944rad)
  sketch-geometry (48):
    g0: LineSegment StartX=-49.19 StartY=69.25 StartZ=0 EndX=-49.19 EndY=66.25 EndZ=0
    g1: LineSegment StartX=-49.19 StartY=63.5 StartZ=0 EndX=-49.19 EndY=60.5 EndZ=0
    g2: LineSegment StartX=-49.19 StartY=57.75 StartZ=0 EndX=-49.19 EndY=54.75 EndZ=0
    g3: LineSegment StartX=-49.19 StartY=52 StartZ=0 EndX=-49.19 EndY=49 EndZ=0
    g4: LineSegment StartX=-49.19 StartY=46.25 StartZ=0 EndX=-49.19 EndY=43.25 EndZ=0
    g5: LineSegment StartX=-49.19 StartY=40.5 StartZ=0 EndX=-49.19 EndY=37.5 EndZ=0
    g6: LineSegment StartX=-49.19 StartY=34.5 StartZ=0 EndX=-49.19 EndY=31.5 EndZ=0
    g7: LineSegment StartX=-49.19 StartY=28.75 StartZ=0 EndX=-49.19 EndY=25.75 EndZ=0
    g8: LineSegment StartX=-49.19 StartY=23 StartZ=0 EndX=-49.19 EndY=20 EndZ=0
    g9: LineSegment StartX=-49.19 StartY=17.25 StartZ=0 EndX=-49.19 EndY=14.25 EndZ=0
    g10: LineSegment StartX=-49.19 StartY=11.5 StartZ=0 EndX=-49.19 EndY=8.5 EndZ=0
    g11: LineSegment StartX=-49.19 StartY=5.75 StartZ=0 EndX=-49.19 EndY=2.75 EndZ=0
    g12: ArcOfCircle CenterX=-1.5 CenterY=67.75 CenterZ=0 NormalX=0 NormalY=0 NormalZ=1 AngleXU=0 Radius=1.5 StartAngle=4.71239 EndAngle=7.85398
    g13: ArcOfCircle CenterX=-1.5 CenterY=62 CenterZ=0 NormalX=0 NormalY=0 NormalZ=1 AngleXU=0 Radius=1.5 StartAngle=4.71239 EndAngle=7.85398
    g14: ArcOfCircle CenterX=-1.5 CenterY=56.25 CenterZ=0 NormalX=0 NormalY=0 NormalZ=1 AngleXU=0 Radius=1.5 StartAngle=4.71239 EndAngle=7.85398
    g15: ArcOfCircle CenterX=-11.49 CenterY=50.5 CenterZ=0 NormalX=0 NormalY=0 NormalZ=1 AngleXU=0 Radius=1.5 StartAngle=4.71239 EndAngle=7.85398
    g16: ArcOfCircle CenterX=-16.28 CenterY=44.75 CenterZ=0 NormalX=0 NormalY=0 NormalZ=1 AngleXU=0 Radius=1.5 StartAngle=4.71239 EndAngle=7.85398
    g17: ArcOfCircle CenterX=-18.2337 CenterY=39 CenterZ=0 NormalX=0 NormalY=0 NormalZ=1 AngleXU=0 Radius=1.5 StartAngle=4.71485 EndAngle=7.85398
    g18: ArcOfCircle CenterX=-16.2837 CenterY=27.25 CenterZ=0 NormalX=0 NormalY=0 NormalZ=1 AngleXU=0 Radius=1.5 StartAngle=4.71485 EndAngle=7.85398
    g19: ArcOfCircle CenterX=-18.2337 CenterY=33 CenterZ=0 NormalX=0 NormalY=0 NormalZ=1 AngleXU=0 Radius=1.5 StartAngle=4.71485 EndAngle=7.85398
    g20: ArcOfCircle CenterX=-11.49 CenterY=21.5 CenterZ=0 NormalX=0 NormalY=0 NormalZ=1 AngleXU=0 Radius=1.5 StartAngle=4.71239 EndAngle=7.85398
    g21: ArcOfCircle CenterX=-1.5 CenterY=4.25 CenterZ=0 NormalX=0 NormalY=0 NormalZ=1 AngleXU=0 Radius=1.5 StartAngle=4.71239 EndAngle=7.85398
    g22: ArcOfCircle CenterX=-1.5 CenterY=10 CenterZ=0 NormalX=0 NormalY=0 NormalZ=1 AngleXU=0 Radius=1.5 StartAngle=4.71239 EndAngle=7.85398
    g23: ArcOfCircle CenterX=-1.5 CenterY=15.75 CenterZ=0 NormalX=0 NormalY=0 NormalZ=1 AngleXU=0 Radius=1.5 StartAngle=4.71239 EndAngle=7.85398
    g24: LineSegment StartX=-49.19 StartY=69.25 StartZ=0 EndX=-1.5 EndY=69.25 EndZ=0
    g25: LineSegment StartX=-49.19 StartY=66.25 StartZ=0 EndX=-1.5 EndY=66.25 EndZ=0
    g26: LineSegment StartX=-49.19 StartY=63.5 StartZ=0 EndX=-1.5 EndY=63.5 EndZ=0
    g27: LineSegment StartX=-49.19 StartY=60.5 StartZ=0 EndX=-1.5 EndY=60.5 EndZ=0
    g28: LineSegment StartX=-49.19 StartY=57.75 StartZ=0 EndX=-1.5 EndY=57.75 EndZ=0
    g29: LineSegment StartX=-49.19 StartY=54.75 StartZ=0 EndX=-1.5 EndY=54.75 EndZ=0
    g30: LineSegment StartX=-49.19 StartY=52 StartZ=0 EndX=-11.49 EndY=52 EndZ=0
    g31: LineSegment StartX=-49.19 StartY=49 StartZ=0 EndX=-11.49 EndY=49 EndZ=0
    g32: LineSegment StartX=-49.19 StartY=46.25 StartZ=0 EndX=-16.28 EndY=46.25 EndZ=0
    g33: LineSegment StartX=-49.19 StartY=43.25 StartZ=0 EndX=-16.28 EndY=43.25 EndZ=0
    g34: LineSegment StartX=-49.19 StartY=40.5 StartZ=0 EndX=-18.2337 EndY=40.5 EndZ=0
    g35: LineSegment StartX=-49.19 StartY=37.5 StartZ=0 EndX=-18.23 EndY=37.5 EndZ=0
    g36: LineSegment StartX=-49.19 StartY=34.5 StartZ=0 EndX=-18.2337 EndY=34.5 EndZ=0
    g37: LineSegment StartX=-49.19 StartY=31.5 StartZ=0 EndX=-18.23 EndY=31.5 EndZ=0
    g38: LineSegment StartX=-49.19 StartY=28.75 StartZ=0 EndX=-16.2837 EndY=28.75 EndZ=0
    g39: LineSegment StartX=-49.19 StartY=25.75 StartZ=0 EndX=-16.28 EndY=25.75 EndZ=0
    g40: LineSegment StartX=-49.19 StartY=23 StartZ=0 EndX=-11.49 EndY=23 EndZ=0
    g41: LineSegment StartX=-49.19 StartY=20 StartZ=0 EndX=-11.49 EndY=20 EndZ=0
    g42: LineSegment StartX=-49.19 StartY=17.25 StartZ=0 EndX=-1.5 EndY=17.25 EndZ=0
    g43: LineSegment StartX=-49.19 StartY=14.25 StartZ=0 EndX=-1.5 EndY=14.25 EndZ=0
    g44: LineSegment StartX=-49.19 StartY=11.5 StartZ=0 EndX=-1.5 EndY=11.5 EndZ=0
    g45: LineSegment StartX=-49.19 StartY=8.5 StartZ=0 EndX=-1.5 EndY=8.5 EndZ=0
    g46: LineSegment StartX=-49.19 StartY=5.75 StartZ=0 EndX=-1.5 EndY=5.75 EndZ=0
    g47: LineSegment StartX=-49.19 StartY=2.75 StartZ=0 EndX=-1.5 EndY=2.75 EndZ=0
  constraints (120):
    c: Vertical(g0)
    c: Distance(g0) = 3
    c: Block(g0)
    c: Vertical(g1)
    c: Distance(g1) = 3
    c: Vertical(g2)
    c: Equal(g0,g2) = 3
    c: Block(g2)
    c: Vertical(g3)
    c: Equal(g1,g3) = 3
    c: Vertical(g4)
    c: Equal(g0,g4) = 3
    c: Block(g4)
    c: Vertical(g5)
    c: Equal(g1,g5) = 3
    c: Vertical(g6)
    c: Equal(g0,g6) = 3
    c: Block(g6)
    c: Vertical(g7)
    c: Equal(g1,g7) = 3
    c: Vertical(g8)
    c: Equal(g0,g8) = 3
    c: Block(g8)
    c: Vertical(g9)
    c: Equal(g1,g9) = 3
    c: Vertical(g10)
    c: Equal(g0,g10) = 3
    c: Block(g10)
    c: Vertical(g11)
    c: Equal(g1,g11) = 3
    c: Block(g12)
    c: Block(g13)
    c: Block(g14)
    c: Block(g15)
    c: Block(g16)
    c: Block(g17)
    c: Block(g18)
    c: Block(g19)
    c: Block(g20)
    c: Block(g21)
    c: Block(g22)
    c: Block(g23)
    c: Block(g11)
    c: Block(g9)
    c: Block(g7)
    c: Block(g5)
    c: Block(g3)
    c: Block(g1)
    c: Coincident(g24,g0)
    c: Coincident(g24,g12)
    c: Horizontal(g24)
    c: Coincident(g25,g0)
    c: Coincident(g25,g12)
    c: Horizontal(g25)
    c: Coincident(g26,g1)
    c: Coincident(g26,g13)
    c: Horizontal(g26)
    c: Coincident(g27,g1)
    c: Coincident(g27,g13)
    c: Horizontal(g27)
    c: Coincident(g28,g2)
    c: Coincident(g28,g14)
    c: Horizontal(g28)
    c: Coincident(g29,g2)
    c: Coincident(g29,g14)
    c: Horizontal(g29)
    c: Coincident(g30,g3)
    c: Coincident(g30,g15)
    c: Horizontal(g30)
    c: Coincident(g31,g3)
    c: Coincident(g31,g15)
    c: Horizontal(g31)
    c: Coincident(g32,g4)
    c: Coincident(g32,g16)
    c: Horizontal(g32)
    c: Coincident(g33,g4)
    c: Coincident(g33,g16)
    c: Horizontal(g33)
    c: Coincident(g34,g5)
    c: Coincident(g34,g17)
    c: Horizontal(g34)
    c: Coincident(g35,g5)
    c: Coincident(g35,g17)
    c: Horizontal(g35)
    c: Coincident(g36,g6)
    c: Coincident(g36,g19)
    c: Horizontal(g36)
    c: Coincident(g37,g6)
    c: Coincident(g37,g19)
    c: Horizontal(g37)
    c: Coincident(g38,g7)
    c: Coincident(g38,g18)
    c: Horizontal(g38)
    c: Coincident(g39,g7)
    c: Coincident(g39,g18)
    c: Horizontal(g39)
    c: Coincident(g40,g8)
    c: Coincident(g40,g20)
    c: Horizontal(g40)
    c: Coincident(g41,g8)
    c: Coincident(g41,g20)
    c: Horizontal(g41)
    c: Coincident(g42,g9)
    c: Coincident(g42,g23)
    c: Horizontal(g42)
    c: Coincident(g43,g9)
    c: Coincident(g43,g23)
    c: Horizontal(g43)
    c: Coincident(g44,g10)
    c: Coincident(g44,g22)
    c: Horizontal(g44)
    c: Coincident(g45,g10)
    c: Coincident(g45,g22)
    c: Horizontal(g45)
    c: Coincident(g46,g11)
    c: Coincident(g46,g21)
    c: Horizontal(g46)
    c: Coincident(g47,g11)
    c: Coincident(g47,g21)
    c: Horizontal(g47)
FEATURE [Sketcher::SketchObject] Sketch031
  FullyConstrained = true
  Placement = pos=(117,19,0) rot=(0.57735,0.57735,0.57735;2.0944rad)
  sketch-geometry (24):
    g0: ArcOfCircle CenterX=-49.19 CenterY=67.75 CenterZ=0 NormalX=0 NormalY=0 NormalZ=1 AngleXU=0 Radius=1.5 StartAngle=1.5708 EndAngle=4.71239
    g1: ArcOfCircle CenterX=-49.19 CenterY=62 CenterZ=0 NormalX=0 NormalY=0 NormalZ=1 AngleXU=0 Radius=1.5 StartAngle=1.5708 EndAngle=4.71239
    g2: ArcOfCircle CenterX=-49.19 CenterY=56.25 CenterZ=0 NormalX=0 NormalY=0 NormalZ=1 AngleXU=0 Radius=1.5 StartAngle=1.5708 EndAngle=4.71239
    g3: ArcOfCircle CenterX=-49.19 CenterY=50.5 CenterZ=0 NormalX=0 NormalY=0 NormalZ=1 AngleXU=0 Radius=1.5 StartAngle=1.5708 EndAngle=4.71239
    g4: ArcOfCircle CenterX=-49.19 CenterY=44.75 CenterZ=0 NormalX=0 NormalY=0 NormalZ=1 AngleXU=0 Radius=1.5 StartAngle=1.5708 EndAngle=4.71239
    g5: ArcOfCircle CenterX=-49.19 CenterY=39 CenterZ=0 NormalX=0 NormalY=0 NormalZ=1 AngleXU=0 Radius=1.5 StartAngle=1.5708 EndAngle=4.71239
    g6: ArcOfCircle CenterX=-49.19 CenterY=33 CenterZ=0 NormalX=0 NormalY=0 NormalZ=1 AngleXU=0 Radius=1.5 StartAngle=1.5708 EndAngle=4.71239
    g7: ArcOfCircle CenterX=-49.19 CenterY=27.25 CenterZ=0 NormalX=0 NormalY=0 NormalZ=1 AngleXU=0 Radius=1.5 StartAngle=1.5708 EndAngle=4.71239
    g8: ArcOfCircle CenterX=-49.19 CenterY=21.5 CenterZ=0 NormalX=0 NormalY=0 NormalZ=1 AngleXU=0 Radius=1.5 StartAngle=1.5708 EndAngle=4.71239
    g9: ArcOfCircle CenterX=-49.19 CenterY=15.75 CenterZ=0 NormalX=0 NormalY=0 NormalZ=1 AngleXU=0 Radius=1.5 StartAngle=1.5708 EndAngle=4.71239
    g10: ArcOfCircle CenterX=-49.19 CenterY=10 CenterZ=0 NormalX=0 NormalY=0 NormalZ=1 AngleXU=0 Radius=1.5 StartAngle=1.5708 EndAngle=4.71239
    g11: ArcOfCircle CenterX=-49.19 CenterY=4.25 CenterZ=0 NormalX=0 NormalY=0 NormalZ=1 AngleXU=0 Radius=1.5 StartAngle=1.5708 EndAngle=4.71239
    g12: LineSegment StartX=-49.19 StartY=69.25 StartZ=0 EndX=-49.19 EndY=66.25 EndZ=0
    g13: LineSegment StartX=-49.19 StartY=63.5 StartZ=0 EndX=-49.19 EndY=60.5 EndZ=0
    g14: LineSegment StartX=-49.19 StartY=57.75 StartZ=0 EndX=-49.19 EndY=54.75 EndZ=0
    g15: LineSegment StartX=-49.19 StartY=52 StartZ=0 EndX=-49.19 EndY=49 EndZ=0
    g16: LineSegment StartX=-49.19 StartY=46.25 StartZ=0 EndX=-49.19 EndY=43.25 EndZ=0
    g17: LineSegment StartX=-49.19 StartY=40.5 StartZ=0 EndX=-49.19 EndY=37.5 EndZ=0
    g18: LineSegment StartX=-49.19 StartY=34.5 StartZ=0 EndX=-49.19 EndY=31.5 EndZ=0
    g19: LineSegment StartX=-49.19 StartY=28.75 StartZ=0 EndX=-49.19 EndY=25.75 EndZ=0
    g20: LineSegment StartX=-49.19 StartY=23 StartZ=0 EndX=-49.19 EndY=20 EndZ=0
    g21: LineSegment StartX=-49.19 StartY=17.25 StartZ=0 EndX=-49.19 EndY=14.25 EndZ=0
    g22: LineSegment StartX=-49.19 StartY=11.5 StartZ=0 EndX=-49.19 EndY=8.5 EndZ=0
    g23: LineSegment StartX=-49.19 StartY=5.75 StartZ=0 EndX=-49.19 EndY=2.75 EndZ=0
  constraints (48):
    c: Block(g0)
    c: Block(g1)
    c: Block(g2)
    c: Block(g3)
    c: Block(g4)
    c: Block(g5)
    c: Block(g6)
    c: Block(g7)
    c: Block(g8)
    c: Block(g9)
    c: Block(g10)
    c: Block(g11)
    c: Coincident(g12,g0)
    c: Coincident(g12,g0)
    c: Vertical(g12)
    c: Vertical(g13)
    c: Coincident(g13,g1)
    c: Vertical(g14)
    c: Coincident(g14,g2)
    c: Vertical(g15)
    c: Coincident(g15,g3)
    c: Vertical(g16)
    c: Coincident(g16,g4)
    c: Vertical(g17)
    c: Coincident(g17,g5)
    c: Vertical(g18)
    c: Coincident(g18,g6)
    c: Vertical(g19)
    c: Coincident(g19,g7)
    c: Vertical(g20)
    c: Coincident(g20,g8)
    c: Vertical(g21)
    c: Coincident(g21,g9)
    c: Vertical(g22)
    c: Coincident(g22,g10)
    c: Vertical(g23)
    c: Coincident(g23,g11)
    c: Block(g23)
    c: Block(g22)
    c: Block(g21)
    c: Block(g20)
    c: Block(g13)
    c: Block(g14)
    c: Block(g15)
    c: Block(g16)
    c: Block(g17)
    c: Block(g18)
    c: Block(g19)
FEATURE [Part::Extrusion] Extrude022
  Base = -> Sketch030
  Dir = (1,-2e-16,2e-16)
  DirMode = 2
  FaceMakerClass = Part::FaceMakerBullseye
  LengthFwd = 19
  LengthRev = 0
  Placement = pos=(-19,0,0) rot=(0,0,1;0rad)
  Solid = true
  Symmetric = false
FEATURE [Part::Fillet] Fillet022
  Base = -> Extrude022
  Edges = 24 edges r=1.49: [Edge6,Edge11,Edge18,Edge23,Edge30,Edge35,Edge42,Edge47,Edge54,Edge59,Edge66,Edge71,Edge78,Edge83,Edge90,Edge95,Edge102,Edge107,Edge114,Edge119,Edge126,Edge131,Edge138,Edge143]
FEATURE [Part::Cut] Cut020  label="top010"
  Base = -> Cut019
  Tool = -> Fillet022
FEATURE [Sketcher::SketchObject] Sketch032
  FullyConstrained = true
  Placement = pos=(117,19,0) rot=(0.57735,0.57735,0.57735;2.0944rad)
  sketch-geometry (48):
    g0: LineSegment StartX=-49.19 StartY=69.25 StartZ=0 EndX=-49.19 EndY=66.25 EndZ=0
    g1: LineSegment StartX=-49.19 StartY=63.5 StartZ=0 EndX=-49.19 EndY=60.5 EndZ=0
    g2: LineSegment StartX=-49.19 StartY=57.75 StartZ=0 EndX=-49.19 EndY=54.75 EndZ=0
    g3: LineSegment StartX=-49.19 StartY=52 StartZ=0 EndX=-49.19 EndY=49 EndZ=0
    g4: LineSegment StartX=-49.19 StartY=46.25 StartZ=0 EndX=-49.19 EndY=43.25 EndZ=0
    g5: LineSegment StartX=-49.19 StartY=40.5 StartZ=0 EndX=-49.19 EndY=37.5 EndZ=0
    g6: LineSegment StartX=-49.19 StartY=34.5 StartZ=0 EndX=-49.19 EndY=31.5 EndZ=0
    g7: LineSegment StartX=-49.19 StartY=28.75 StartZ=0 EndX=-49.19 EndY=25.75 EndZ=0
    g8: LineSegment StartX=-49.19 StartY=23 StartZ=0 EndX=-49.19 EndY=20 EndZ=0
    g9: LineSegment StartX=-49.19 StartY=17.25 StartZ=0 EndX=-49.19 EndY=14.25 EndZ=0
    g10: LineSegment StartX=-49.19 StartY=11.5 StartZ=0 EndX=-49.19 EndY=8.5 EndZ=0
    g11: LineSegment StartX=-49.19 StartY=5.75 StartZ=0 EndX=-49.19 EndY=2.75 EndZ=0
    g12: ArcOfCircle CenterX=-1.5 CenterY=67.75 CenterZ=0 NormalX=0 NormalY=0 NormalZ=1 AngleXU=0 Radius=1.5 StartAngle=4.71239 EndAngle=7.85398
    g13: ArcOfCircle CenterX=-1.5 CenterY=62 CenterZ=0 NormalX=0 NormalY=0 NormalZ=1 AngleXU=0 Radius=1.5 StartAngle=4.71239 EndAngle=7.85398
    g14: ArcOfCircle CenterX=-1.5 CenterY=56.25 CenterZ=0 NormalX=0 NormalY=0 NormalZ=1 AngleXU=0 Radius=1.5 StartAngle=4.71239 EndAngle=7.85398
    g15: ArcOfCircle CenterX=-11.49 CenterY=50.5 CenterZ=0 NormalX=0 NormalY=0 NormalZ=1 AngleXU=0 Radius=1.5 StartAngle=4.71239 EndAngle=7.85398
    g16: ArcOfCircle CenterX=-16.28 CenterY=44.75 CenterZ=0 NormalX=0 NormalY=0 NormalZ=1 AngleXU=0 Radius=1.5 StartAngle=4.71239 EndAngle=7.85398
    g17: ArcOfCircle CenterX=-18.2337 CenterY=39 CenterZ=0 NormalX=0 NormalY=0 NormalZ=1 AngleXU=0 Radius=1.5 StartAngle=4.71485 EndAngle=7.85398
    g18: ArcOfCircle CenterX=-16.2837 CenterY=27.25 CenterZ=0 NormalX=0 NormalY=0 NormalZ=1 AngleXU=0 Radius=1.5 StartAngle=4.71485 EndAngle=7.85398
    g19: ArcOfCircle CenterX=-18.2337 CenterY=33 CenterZ=0 NormalX=0 NormalY=0 NormalZ=1 AngleXU=0 Radius=1.5 StartAngle=4.71485 EndAngle=7.85398
    g20: ArcOfCircle CenterX=-11.49 CenterY=21.5 CenterZ=0 NormalX=0 NormalY=0 NormalZ=1 AngleXU=0 Radius=1.5 StartAngle=4.71239 EndAngle=7.85398
    g21: ArcOfCircle CenterX=-1.5 CenterY=4.25 CenterZ=0 NormalX=0 NormalY=0 NormalZ=1 AngleXU=0 Radius=1.5 StartAngle=4.71239 EndAngle=7.85398
    g22: ArcOfCircle CenterX=-1.5 CenterY=10 CenterZ=0 NormalX=0 NormalY=0 NormalZ=1 AngleXU=0 Radius=1.5 StartAngle=4.71239 EndAngle=7.85398
    g23: ArcOfCircle CenterX=-1.5 CenterY=15.75 CenterZ=0 NormalX=0 NormalY=0 NormalZ=1 AngleXU=0 Radius=1.5 StartAngle=4.71239 EndAngle=7.85398
    g24: LineSegment StartX=-49.19 StartY=69.25 StartZ=0 EndX=-1.5 EndY=69.25 EndZ=0
    g25: LineSegment StartX=-49.19 StartY=66.25 StartZ=0 EndX=-1.5 EndY=66.25 EndZ=0
    g26: LineSegment StartX=-49.19 StartY=63.5 StartZ=0 EndX=-1.5 EndY=63.5 EndZ=0
    g27: LineSegment StartX=-49.19 StartY=60.5 StartZ=0 EndX=-1.5 EndY=60.5 EndZ=0
    g28: LineSegment StartX=-49.19 StartY=57.75 StartZ=0 EndX=-1.5 EndY=57.75 EndZ=0
    g29: LineSegment StartX=-49.19 StartY=54.75 StartZ=0 EndX=-1.5 EndY=54.75 EndZ=0
    g30: LineSegment StartX=-49.19 StartY=52 StartZ=0 EndX=-11.49 EndY=52 EndZ=0
    g31: LineSegment StartX=-49.19 StartY=49 StartZ=0 EndX=-11.49 EndY=49 EndZ=0
    g32: LineSegment StartX=-49.19 StartY=46.25 StartZ=0 EndX=-16.28 EndY=46.25 EndZ=0
    g33: LineSegment StartX=-49.19 StartY=43.25 StartZ=0 EndX=-16.28 EndY=43.25 EndZ=0
    g34: LineSegment StartX=-49.19 StartY=40.5 StartZ=0 EndX=-18.2337 EndY=40.5 EndZ=0
    g35: LineSegment StartX=-49.19 StartY=37.5 StartZ=0 EndX=-18.23 EndY=37.5 EndZ=0
    g36: LineSegment StartX=-49.19 StartY=34.5 StartZ=0 EndX=-18.2337 EndY=34.5 EndZ=0
    g37: LineSegment StartX=-49.19 StartY=31.5 StartZ=0 EndX=-18.23 EndY=31.5 EndZ=0
    g38: LineSegment StartX=-49.19 StartY=28.75 StartZ=0 EndX=-16.2837 EndY=28.75 EndZ=0
    g39: LineSegment StartX=-49.19 StartY=25.75 StartZ=0 EndX=-16.28 EndY=25.75 EndZ=0
    g40: LineSegment StartX=-49.19 StartY=23 StartZ=0 EndX=-11.49 EndY=23 EndZ=0
    g41: LineSegment StartX=-49.19 StartY=20 StartZ=0 EndX=-11.49 EndY=20 EndZ=0
    g42: LineSegment StartX=-49.19 StartY=17.25 StartZ=0 EndX=-1.5 EndY=17.25 EndZ=0
    g43: LineSegment StartX=-49.19 StartY=14.25 StartZ=0 EndX=-1.5 EndY=14.25 EndZ=0
    g44: LineSegment StartX=-49.19 StartY=11.5 StartZ=0 EndX=-1.5 EndY=11.5 EndZ=0
    g45: LineSegment StartX=-49.19 StartY=8.5 StartZ=0 EndX=-1.5 EndY=8.5 EndZ=0
    g46: LineSegment StartX=-49.19 StartY=5.75 StartZ=0 EndX=-1.5 EndY=5.75 EndZ=0
    g47: LineSegment StartX=-49.19 StartY=2.75 StartZ=0 EndX=-1.5 EndY=2.75 EndZ=0
  constraints (120):
    c: Vertical(g0)
    c: Distance(g0) = 3
    c: Block(g0)
    c: Vertical(g1)
    c: Distance(g1) = 3
    c: Vertical(g2)
    c: Equal(g0,g2) = 3
    c: Block(g2)
    c: Vertical(g3)
    c: Equal(g1,g3) = 3
    c: Vertical(g4)
    c: Equal(g0,g4) = 3
    c: Block(g4)
    c: Vertical(g5)
    c: Equal(g1,g5) = 3
    c: Vertical(g6)
    c: Equal(g0,g6) = 3
    c: Block(g6)
    c: Vertical(g7)
    c: Equal(g1,g7) = 3
    c: Vertical(g8)
    c: Equal(g0,g8) = 3
    c: Block(g8)
    c: Vertical(g9)
    c: Equal(g1,g9) = 3
    c: Vertical(g10)
    c: Equal(g0,g10) = 3
    c: Block(g10)
    c: Vertical(g11)
    c: Equal(g1,g11) = 3
    c: Block(g12)
    c: Block(g13)
    c: Block(g14)
    c: Block(g15)
    c: Block(g16)
    c: Block(g17)
    c: Block(g18)
    c: Block(g19)
    c: Block(g20)
    c: Block(g21)
    c: Block(g22)
    c: Block(g23)
    c: Block(g11)
    c: Block(g9)
    c: Block(g7)
    c: Block(g5)
    c: Block(g3)
    c: Block(g1)
    c: Coincident(g24,g0)
    c: Coincident(g24,g12)
    c: Horizontal(g24)
    c: Coincident(g25,g0)
    c: Coincident(g25,g12)
    c: Horizontal(g25)
    c: Coincident(g26,g1)
    c: Coincident(g26,g13)
    c: Horizontal(g26)
    c: Coincident(g27,g1)
    c: Coincident(g27,g13)
    c: Horizontal(g27)
    c: Coincident(g28,g2)
    c: Coincident(g28,g14)
    c: Horizontal(g28)
    c: Coincident(g29,g2)
    c: Coincident(g29,g14)
    c: Horizontal(g29)
    c: Coincident(g30,g3)
    c: Coincident(g30,g15)
    c: Horizontal(g30)
    c: Coincident(g31,g3)
    c: Coincident(g31,g15)
    c: Horizontal(g31)
    c: Coincident(g32,g4)
    c: Coincident(g32,g16)
    c: Horizontal(g32)
    c: Coincident(g33,g4)
    c: Coincident(g33,g16)
    c: Horizontal(g33)
    c: Coincident(g34,g5)
    c: Coincident(g34,g17)
    c: Horizontal(g34)
    c: Coincident(g35,g5)
    c: Coincident(g35,g17)
    c: Horizontal(g35)
    c: Coincident(g36,g6)
    c: Coincident(g36,g19)
    c: Horizontal(g36)
    c: Coincident(g37,g6)
    c: Coincident(g37,g19)
    c: Horizontal(g37)
    c: Coincident(g38,g7)
    c: Coincident(g38,g18)
    c: Horizontal(g38)
    c: Coincident(g39,g7)
    c: Coincident(g39,g18)
    c: Horizontal(g39)
    c: Coincident(g40,g8)
    c: Coincident(g40,g20)
    c: Horizontal(g40)
    c: Coincident(g41,g8)
    c: Coincident(g41,g20)
    c: Horizontal(g41)
    c: Coincident(g42,g9)
    c: Coincident(g42,g23)
    c: Horizontal(g42)
    c: Coincident(g43,g9)
    c: Coincident(g43,g23)
    c: Horizontal(g43)
    c: Coincident(g44,g10)
    c: Coincident(g44,g22)
    c: Horizontal(g44)
    c: Coincident(g45,g10)
    c: Coincident(g45,g22)
    c: Horizontal(g45)
    c: Coincident(g46,g11)
    c: Coincident(g46,g21)
    c: Horizontal(g46)
    c: Coincident(g47,g11)
    c: Coincident(g47,g21)
    c: Horizontal(g47)
FEATURE [Part::Extrusion] Extrude023
  Base = -> Sketch032
  Dir = (1,-2e-16,2e-16)
  DirMode = 2
  FaceMakerClass = Part::FaceMakerBullseye
  LengthFwd = 19
  LengthRev = 0
  Placement = pos=(-19,0,0) rot=(0,0,1;0rad)
  Solid = true
  Symmetric = false
FEATURE [Part::Fillet] Fillet023
  Base = -> Extrude023
  Edges = <same value as first occurrence — deduplicated (x6 in doc)>
  Placement = pos=(0,0.05,0) rot=(0,0,1;0rad)
FEATURE [Part::Cut] Cut014  label="bottom003"
  Base = -> Cut007
  Tool = -> Fusion047
FEATURE [Part::Cut] Cut021  label="bottom004"
  Base = -> Cut014
  Tool = -> Fillet023
FEATURE [Sketcher::SketchObject] Sketch033
  FullyConstrained = true
  Placement = pos=(117,19,0) rot=(0.57735,0.57735,0.57735;2.0944rad)
  sketch-geometry (8):
    g0: LineSegment StartX=-49.19 StartY=69.25 StartZ=0 EndX=-49.19 EndY=66.25 EndZ=0
    g1: LineSegment StartX=-49.19 StartY=5.75 StartZ=0 EndX=-49.19 EndY=2.75 EndZ=0
    g2: ArcOfCircle CenterX=-1.5 CenterY=67.75 CenterZ=0 NormalX=0 NormalY=0 NormalZ=1 AngleXU=0 Radius=1.5 StartAngle=4.71239 EndAngle=7.85398
    g3: ArcOfCircle CenterX=-1.5 CenterY=4.25 CenterZ=0 NormalX=0 NormalY=0 NormalZ=1 AngleXU=0 Radius=1.5 StartAngle=4.71239 EndAngle=7.85398
    g4: LineSegment StartX=-49.19 StartY=69.25 StartZ=0 EndX=-1.5 EndY=69.25 EndZ=0
    g5: LineSegment StartX=-49.19 StartY=66.25 StartZ=0 EndX=-1.5 EndY=66.25 EndZ=0
    g6: LineSegment StartX=-49.19 StartY=5.75 StartZ=0 EndX=-1.5 EndY=5.75 EndZ=0
    g7: LineSegment StartX=-49.19 StartY=2.75 StartZ=0 EndX=-1.5 EndY=2.75 EndZ=0
  constraints (19):
    c: Vertical(g0)
    c: Distance(g0) = 3
    c: Block(g0)
    c: Vertical(g1)
    c: Block(g2)
    c: Block(g3)
    c: Block(g1)
    c: Coincident(g4,g0)
    c: Coincident(g4,g2)
    c: Horizontal(g4)
    c: Coincident(g5,g0)
    c: Coincident(g5,g2)
    c: Horizontal(g5)
    c: Coincident(g6,g1)
    c: Coincident(g6,g3)
    c: Horizontal(g6)
    c: Coincident(g7,g1)
    c: Coincident(g7,g3)
    c: Horizontal(g7)
FEATURE [Sketcher::SketchObject] Sketch034
  FullyConstrained = true
  Placement = pos=(117,19,0) rot=(0.57735,0.57735,0.57735;2.0944rad)
  sketch-geometry (8):
    g0: LineSegment StartX=-49.19 StartY=63.5 StartZ=0 EndX=-49.19 EndY=60.5 EndZ=0
    g1: LineSegment StartX=-49.19 StartY=11.5 StartZ=0 EndX=-49.19 EndY=8.5 EndZ=0
    g2: ArcOfCircle CenterX=-1.5 CenterY=62 CenterZ=0 NormalX=0 NormalY=0 NormalZ=1 AngleXU=0 Radius=1.5 StartAngle=4.71239 EndAngle=7.85398
    g3: ArcOfCircle CenterX=-1.5 CenterY=10 CenterZ=0 NormalX=0 NormalY=0 NormalZ=1 AngleXU=0 Radius=1.5 StartAngle=4.71239 EndAngle=7.85398
    g4: LineSegment StartX=-49.19 StartY=63.5 StartZ=0 EndX=-1.5 EndY=63.5 EndZ=0
    g5: LineSegment StartX=-49.19 StartY=60.5 StartZ=0 EndX=-1.5 EndY=60.5 EndZ=0
    g6: LineSegment StartX=-49.19 StartY=11.5 StartZ=0 EndX=-1.5 EndY=11.5 EndZ=0
    g7: LineSegment StartX=-49.19 StartY=8.5 StartZ=0 EndX=-1.5 EndY=8.5 EndZ=0
  constraints (19):
    c: Vertical(g0)
    c: Distance(g0) = 3
    c: Vertical(g1)
    c: Block(g1)
    c: Block(g2)
    c: Block(g3)
    c: Block(g0)
    c: Coincident(g4,g0)
    c: Coincident(g4,g2)
    c: Horizontal(g4)
    c: Coincident(g5,g0)
    c: Coincident(g5,g2)
    c: Horizontal(g5)
    c: Coincident(g6,g1)
    c: Coincident(g6,g3)
    c: Horizontal(g6)
    c: Coincident(g7,g1)
    c: Coincident(g7,g3)
    c: Horizontal(g7)
FEATURE [Part::Extrusion] Extrude024
  Base = -> Sketch033
  Dir = (1,0,0)
  DirMode = 2
  FaceMakerClass = Part::FaceMakerBullseye
  LengthFwd = 10
  LengthRev = 0
  Solid = true
  Symmetric = false
FEATURE [Part::Extrusion] Extrude025
  Base = -> Sketch034
  Dir = (1,0,0)
  DirMode = 2
  FaceMakerClass = Part::FaceMakerBullseye
  LengthFwd = 10
  LengthRev = 0
  Solid = true
  Symmetric = false
FEATURE [Part::Fillet] Fillet024  label="removeFromtMoreFrontCaseScrewRetainers"
  Base = -> Extrude024
  Edges = 4 edges r=1.49: [Edge6,Edge11,Edge18,Edge23]
  Placement = pos=(-11,0,0) rot=(0,0,1;0rad)
FEATURE [Part::Fillet] Fillet025  label="removeFromtMoreFrontCaseScrewRetainers001"
  Base = -> Extrude025
  Edges = 4 edges r=1.49: [Edge6,Edge11,Edge18,Edge23]
  Placement = pos=(-19,0,0) rot=(0,0,1;0rad)
FEATURE [Part::Cut] Cut022
  Base = -> Cut015
  Tool = -> Fillet025
FEATURE [Part::Cut] Cut023  label="screwRetainers"
  Base = -> Cut022
  Tool = -> Fillet024
FEATURE [Part::MultiFuse] Fusion056  label="bottom005"
  Shapes = -> [Fusion044,Cut021]
FEATURE [Part::MultiFuse] Fusion057  label="casePillars001"
  Shapes = -> [Cut016,Fusion052]
FEATURE [Part::MultiFuse] Fusion058  label="bottom006"
  Shapes = -> [Fusion056,Cut023]
FEATURE [Part::MultiFuse] Fusion059  label="bottom007"
  Shapes = -> [Fusion058,Fillet005]
FEATURE [Part::MultiFuse] Fusion060  label="bottom008"
  Shapes = -> [Fusion059,Fusion]
FEATURE [Part::MultiFuse] Fusion061  label="top011"
  Shapes = -> [Cut006,Cut020]
FEATURE [Part::MultiFuse] Fusion062  label="top012"
  Shapes = -> [Fusion057,Fusion061]
FEATURE [Sketcher::SketchObject] Sketch035  label="topSketch007"
  FullyConstrained = true
  sketch-geometry (6):
    g0: LineSegment StartX=19 StartY=38 StartZ=0 EndX=117 EndY=38 EndZ=0
    g1: ArcOfCircle CenterX=19 CenterY=19 CenterZ=0 NormalX=0 NormalY=0 NormalZ=1 AngleXU=0 Radius=19 StartAngle=1.5708 EndAngle=3.14159
    g2: LineSegment StartX=117 StartY=38 StartZ=0 EndX=117 EndY=19 EndZ=0
    g3: LineSegment StartX=98 StartY=1.0161e-12 StartZ=0 EndX=5.22862e-06 EndY=1.0161e-12 EndZ=0
    g4: LineSegment StartX=5.22862e-06 StartY=19 StartZ=0 EndX=5.22862e-06 EndY=1.0161e-12 EndZ=0
    g5: ArcOfCircle CenterX=98 CenterY=19 CenterZ=0 NormalX=0 NormalY=0 NormalZ=1 AngleXU=0 Radius=19 StartAngle=4.71239 EndAngle=6.28319
  constraints (16):
    c: Horizontal(g0)
    c: Distance(g0) = 98
    c: Coincident(g1,g0)
    c: Block(g1)
    c: Coincident(g2,g0)
    c: Vertical(g2)
    c: Distance(g2) = 19
    c: Horizontal(g3)
    c: Coincident(g4,g1)
    c: Vertical(g4)
    c: Coincident(g3,g4)
    c: Block(g3)
    c: Coincident(g5,g2)
    c: Coincident(g5,g3)
    c: Block(g0)
    c: Block(g5)
FEATURE [Part::Extrusion] Extrude026  label="sideA001"
  Base = -> Sketch035
  Dir = (0,0,1)
  DirMode = 2
  FaceMakerClass = Part::FaceMakerBullseye
  LengthFwd = 3
  LengthRev = 0
  Placement = pos=(0,0,-2.7) rot=(0,0,1;0rad)
  Solid = true
  Symmetric = false
FEATURE [Sketcher::SketchObject] Sketch036  label="topSketch008"
  FullyConstrained = true
  sketch-geometry (6):
    g0: LineSegment StartX=19 StartY=38 StartZ=0 EndX=117 EndY=38 EndZ=0
    g1: ArcOfCircle CenterX=19 CenterY=19 CenterZ=0 NormalX=0 NormalY=0 NormalZ=1 AngleXU=0 Radius=19 StartAngle=1.5708 EndAngle=3.14159
    g2: LineSegment StartX=117 StartY=38 StartZ=0 EndX=117 EndY=19 EndZ=0
    g3: LineSegment StartX=98 StartY=1.0161e-12 StartZ=0 EndX=5.22862e-06 EndY=1.0161e-12 EndZ=0
    g4: LineSegment StartX=5.22862e-06 StartY=19 StartZ=0 EndX=5.22862e-06 EndY=1.0161e-12 EndZ=0
    g5: ArcOfCircle CenterX=98 CenterY=19 CenterZ=0 NormalX=0 NormalY=0 NormalZ=1 AngleXU=0 Radius=19 StartAngle=4.71239 EndAngle=6.28319
  constraints (16):
    c: Horizontal(g0)
    c: Distance(g0) = 98
    c: Coincident(g1,g0)
    c: Block(g1)
    c: Coincident(g2,g0)
    c: Vertical(g2)
    c: Distance(g2) = 19
    c: Horizontal(g3)
    c: Coincident(g4,g1)
    c: Vertical(g4)
    c: Coincident(g3,g4)
    c: Block(g3)
    c: Coincident(g5,g2)
    c: Coincident(g5,g3)
    c: Block(g0)
    c: Block(g5)
FEATURE [Part::Extrusion] Extrude027  label="sideB001"
  Base = -> Sketch036
  Dir = (0,0,1)
  DirMode = 2
  FaceMakerClass = Part::FaceMakerBullseye
  LengthFwd = 3
  LengthRev = 0
  Placement = pos=(0,0,71.7) rot=(0,0,1;0rad)
  Solid = true
  Symmetric = false
FEATURE [Part::MultiFuse] Fusion064  label="removeFromBottom"
  Shapes = -> [Extrude026,Extrude027]
FEATURE [Part::Cut] Cut024  label="bottom009"
  Base = -> Fusion060
  Tool = -> Fusion064
FEATURE [Sketcher::SketchObject] Sketch037  label="topSketch009"
  FullyConstrained = true
  sketch-geometry (8):
    g0: ArcOfCircle CenterX=19 CenterY=19.1201 CenterZ=0 NormalX=0 NormalY=0 NormalZ=1 AngleXU=0 Radius=18.8799 StartAngle=1.5708 EndAngle=3.14793
    g1: LineSegment StartX=0.120501 StartY=19.0004 StartZ=0 EndX=0.120501 EndY=0.000382114 EndZ=0
    g2: LineSegment StartX=19 StartY=38 StartZ=0 EndX=124 EndY=38 EndZ=0
    g3: LineSegment StartX=0.120501 StartY=0.000382114 StartZ=0 EndX=105.121 EndY=0.000382114 EndZ=0
    g4: LineSegment StartX=124 StartY=38 StartZ=0 EndX=125.616 EndY=38 EndZ=0
    g5: LineSegment StartX=105.121 StartY=0.000382114 StartZ=0 EndX=106.736 EndY=0.000382114 EndZ=0
    g6: ArcOfCircle CenterX=106.616 CenterY=19 CenterZ=0 NormalX=0 NormalY=0 NormalZ=1 AngleXU=0 Radius=19 StartAngle=4.71873 EndAngle=6.28319
    g7: LineSegment StartX=125.616 StartY=38 StartZ=0 EndX=125.616 EndY=19 EndZ=0
  constraints (21):
    c: Block(g0)
    c: Coincident(g1,g0)
    c: Vertical(g1)
    c: Horizontal(g2)
    c: Distance(g2) = 105
    c: Coincident(g2,g0)
    c: Distance(g1) = 19
    c: Coincident(g3,g1)
    c: Horizontal(g3)
    c: Distance(g3) = 105
    c: Coincident(g4,g2)
    c: Horizontal(g4)
    c: Distance(g4) = 1.61553
    c: Horizontal(g5)
    c: Equal(g4,g5) = 1.61553
    c: Coincident(g5,g3)
    c: Block(g6)
    c: Coincident(g6,g5)
    c: Coincident(g7,g4)
    c: Coincident(g7,g6)
    c: Vertical(g7)
FEATURE [Part::Extrusion] Extrude028  label="sideB"
  Base = -> Sketch037
  Dir = (0,0,1)
  DirMode = 2
  FaceMakerClass = Part::FaceMakerBullseye
  LengthFwd = 3
  LengthRev = 0
  Placement = pos=(0,0,72) rot=(0,0,1;0rad)
  Solid = true
  Symmetric = false
FEATURE [Sketcher::SketchObject] Sketch038  label="topSketch010"
  FullyConstrained = true
  sketch-geometry (22):
    g0: LineSegment StartX=5.21097e-06 StartY=3 StartZ=0 EndX=5.21097e-06 EndY=19 EndZ=0
    g1: ArcOfCircle CenterX=19 CenterY=19 CenterZ=0 NormalX=0 NormalY=0 NormalZ=1 AngleXU=0 Radius=19 StartAngle=1.5708 EndAngle=3.14159
    g2: ArcOfCircle CenterX=19 CenterY=19 CenterZ=0 NormalX=0 NormalY=0 NormalZ=1 AngleXU=0 Radius=16 StartAngle=1.5708 EndAngle=3.14159
    g3: LineSegment StartX=114 StartY=35 StartZ=0 EndX=19 EndY=35 EndZ=0
    g4: LineSegment StartX=5.21097e-06 StartY=3 StartZ=0 EndX=5.21097e-06 EndY=0 EndZ=0
    g5: LineSegment StartX=3 StartY=0 StartZ=0 EndX=5.21097e-06 EndY=0 EndZ=0
    g6: LineSegment StartX=3 StartY=19 StartZ=0 EndX=3 EndY=0 EndZ=0
    g7: LineSegment StartX=19 StartY=38 StartZ=0 EndX=124 EndY=38 EndZ=0
    g8: Circle CenterX=119 CenterY=35 CenterZ=0 NormalX=0 NormalY=0 NormalZ=1 AngleXU=0 Radius=1
    g9: Circle CenterX=121 CenterY=35 CenterZ=0 NormalX=0 NormalY=0 NormalZ=1 AngleXU=0 Radius=1
    g10: Circle CenterX=121 CenterY=33 CenterZ=0 NormalX=0 NormalY=0 NormalZ=1 AngleXU=0 Radius=1
    g11: BSplineCurve PolesCount=3 KnotsCount=2 Degree=2 IsPeriodic=0
    g12: GeomPoint X=119 Y=35 Z=0
    g13: GeomPoint X=121 Y=33 Z=0
    g14: LineSegment StartX=119 StartY=35 StartZ=0 EndX=114 EndY=35 EndZ=0
    g15: ArcOfCircle CenterX=105 CenterY=19 CenterZ=0 NormalX=0 NormalY=0 NormalZ=1 AngleXU=0 Radius=16 StartAngle=5.60905 EndAngle=6.28319
    g16: LineSegment StartX=121 StartY=33 StartZ=0 EndX=121 EndY=19 EndZ=0
    g17: LineSegment StartX=117.5 StartY=9.01251 StartZ=0 EndX=121.163 EndY=9.0125 EndZ=0
    g18: ArcOfCircle CenterX=105 CenterY=19 CenterZ=0 NormalX=0 NormalY=0 NormalZ=1 AngleXU=0 Radius=20.6155 StartAngle=5.7297 EndAngle=6.28319
    g19: LineSegment StartX=121.163 StartY=9.0125 StartZ=0 EndX=122.538 EndY=8.16329 EndZ=0
    g20: LineSegment StartX=124 StartY=38 StartZ=0 EndX=125.616 EndY=38 EndZ=0
    g21: LineSegment StartX=125.616 StartY=19 StartZ=0 EndX=125.616 EndY=38 EndZ=0
  constraints (49):
    c: Vertical(g0)
    c: Block(g0)
    c: Coincident(g1,g0)
    c: Block(g1)
    c: Coincident(g2,g1)
    c: Block(g2)
    c: Coincident(g3,g2)
    c: Horizontal(g3)
    c: Tangent(g3,g2)
    c: Coincident(g4,g0)
    c: Distance(g4) = 3
    c: Vertical(g4)
    c: Coincident(g5,g4)
    c: Horizontal(g5)
    c: Coincident(g6,g2)
    c: Coincident(g6,g5)
    c: Vertical(g6)
    c: Horizontal(g7)
    c: Distance(g7) = 105
    c: Coincident(g7,g1)
    c: Block(g3)
    c: Weight(g8) = 1
    c: Equal(g8,g9)
    c: Equal(g8,g10)
    c: InternalAlignment(g8,g11)
    c: InternalAlignment(g9,g11)
    c: InternalAlignment(g10,g11)
    c: InternalAlignment(g12,g11)
    c: InternalAlignment(g13,g11)
    c: Block(g11)
    c: Coincident(g14,g11)
    c: Coincident(g14,g3)
    c: Horizontal(g14)
    c: Block(g15)
    c: Coincident(g16,g11)
    c: Coincident(g16,g15)
    c: Vertical(g16)
    c: Distance(g16) = 14
    c: Coincident(g17,g15)
    c: Block(g18)
    c: Coincident(g19,g18)
    c: Coincident(g20,g7)
    c: Horizontal(g20)
    c: Vertical(g21)
    c: Coincident(g20,g21)
    c: Block(g20)
    c: Block(g21)
    c: Block(g19)
    c: Block(g17)
FEATURE [Part::Extrusion] Extrude029
  Base = -> Sketch038
  Dir = (0,0,1)
  DirMode = 2
  FaceMakerClass = Part::FaceMakerBullseye
  LengthFwd = 72
  LengthRev = 0
  Solid = true
  Symmetric = false
FEATURE [Part::Feature] Face085
  shape: bbox 4.8 x 25.5 x 2e-07 mm, 1 faces, 0 solids (baked)
FEATURE [Part::Revolution] Revolve089  label="moreFrontCaseScrewPost003"
  Angle = 360
  Axis = (0,1,0)
  Base = (0,0,0)
  FaceMakerClass = Part::FaceMakerBullseye
  Placement = pos=(109.5,4.5,3.5) rot=(0,0,1;0rad)
  Solid = false
  Source = -> Face085
  Symmetric = false
FEATURE [Part::Feature] Face086
  shape: bbox 4.8 x 25.5 x 2e-07 mm, 1 faces, 0 solids (baked)
FEATURE [Part::Revolution] Revolve090  label="moreFrontCaseScrewPost004"
  Angle = 360
  Axis = (0,1,0)
  Base = (0,0,0)
  FaceMakerClass = Part::FaceMakerBullseye
  Placement = pos=(109.5,4.5,68.5) rot=(0,0,1;0rad)
  Solid = false
  Source = -> Face086
  Symmetric = false
FEATURE [Part::Fillet] Fillet026  label="top013"
  Base = -> Extrude029
  Edges = 1 edges r=2: [Edge35]
FEATURE [Sketcher::SketchObject] Sketch039
  FullyConstrained = true
  sketch-geometry (7):
    g0: LineSegment StartX=0 StartY=0 StartZ=0 EndX=0 EndY=6 EndZ=0
    g1: Circle CenterX=0 CenterY=0 CenterZ=0 NormalX=0 NormalY=0 NormalZ=1 AngleXU=0 Radius=1
    g2: Circle CenterX=8 CenterY=6 CenterZ=0 NormalX=0 NormalY=0 NormalZ=1 AngleXU=0 Radius=1
    g3: BSplineCurve PolesCount=3 KnotsCount=2 Degree=2 IsPeriodic=0
    g4: GeomPoint X=0 Y=0 Z=0
    g5: GeomPoint X=8 Y=6 Z=0
    g6: LineSegment StartX=0 StartY=6 StartZ=0 EndX=8 EndY=6 EndZ=0
  constraints (14):
    c: Coincident(g0,g-1)
    c: Distance(g0) = 6
    c: Vertical(g0)
    c: Coincident(g3,g0)
    c: Weight(g1) = 1
    c: Equal(g1,g2)
    c: InternalAlignment(g1,g3)
    c: InternalAlignment(g2,g3)
    c: InternalAlignment(g4,g3)
    c: InternalAlignment(g5,g3)
    c: Block(g3)
    c: Coincident(g6,g0)
    c: Coincident(g6,g3)
    c: Horizontal(g6)
FEATURE [Sketcher::SketchObject] Sketch040
  FullyConstrained = true
  sketch-geometry (7):
    g0: LineSegment StartX=0 StartY=0 StartZ=0 EndX=0 EndY=6 EndZ=0
    g1: Circle CenterX=0 CenterY=0 CenterZ=0 NormalX=0 NormalY=0 NormalZ=1 AngleXU=0 Radius=1
    g2: Circle CenterX=8 CenterY=6 CenterZ=0 NormalX=0 NormalY=0 NormalZ=1 AngleXU=0 Radius=1
    g3: BSplineCurve PolesCount=3 KnotsCount=2 Degree=2 IsPeriodic=0
    g4: GeomPoint X=0 Y=0 Z=0
    g5: GeomPoint X=8 Y=6 Z=0
    g6: LineSegment StartX=0 StartY=6 StartZ=0 EndX=8 EndY=6 EndZ=0
  constraints (14):
    c: Coincident(g0,g-1)
    c: Distance(g0) = 6
    c: Vertical(g0)
    c: Coincident(g3,g0)
    c: Weight(g1) = 1
    c: Equal(g1,g2)
    c: InternalAlignment(g1,g3)
    c: InternalAlignment(g2,g3)
    c: InternalAlignment(g4,g3)
    c: InternalAlignment(g5,g3)
    c: Block(g3)
    c: Coincident(g6,g0)
    c: Coincident(g6,g3)
    c: Horizontal(g6)
FEATURE [Sketcher::SketchObject] Sketch041
  FullyConstrained = true
  sketch-geometry (7):
    g0: LineSegment StartX=0 StartY=0 StartZ=0 EndX=0 EndY=6 EndZ=0
    g1: Circle CenterX=0 CenterY=0 CenterZ=0 NormalX=0 NormalY=0 NormalZ=1 AngleXU=0 Radius=1
    g2: Circle CenterX=8 CenterY=6 CenterZ=0 NormalX=0 NormalY=0 NormalZ=1 AngleXU=0 Radius=1
    g3: BSplineCurve PolesCount=3 KnotsCount=2 Degree=2 IsPeriodic=0
    g4: GeomPoint X=0 Y=0 Z=0
    g5: GeomPoint X=8 Y=6 Z=0
    g6: LineSegment StartX=0 StartY=6 StartZ=0 EndX=8 EndY=6 EndZ=0
  constraints (14):
    c: Coincident(g0,g-1)
    c: Distance(g0) = 6
    c: Vertical(g0)
    c: Coincident(g3,g0)
    c: Weight(g1) = 1
    c: Equal(g1,g2)
    c: InternalAlignment(g1,g3)
    c: InternalAlignment(g2,g3)
    c: InternalAlignment(g4,g3)
    c: InternalAlignment(g5,g3)
    c: Block(g3)
    c: Coincident(g6,g0)
    c: Coincident(g6,g3)
    c: Horizontal(g6)
FEATURE [Sketcher::SketchObject] Sketch042
  FullyConstrained = true
  sketch-geometry (7):
    g0: LineSegment StartX=0 StartY=0 StartZ=0 EndX=0 EndY=6 EndZ=0
    g1: Circle CenterX=0 CenterY=0 CenterZ=0 NormalX=0 NormalY=0 NormalZ=1 AngleXU=0 Radius=1
    g2: Circle CenterX=8 CenterY=6 CenterZ=0 NormalX=0 NormalY=0 NormalZ=1 AngleXU=0 Radius=1
    g3: BSplineCurve PolesCount=3 KnotsCount=2 Degree=2 IsPeriodic=0
    g4: GeomPoint X=0 Y=0 Z=0
    g5: GeomPoint X=8 Y=6 Z=0
    g6: LineSegment StartX=0 StartY=6 StartZ=0 EndX=8 EndY=6 EndZ=0
  constraints (14):
    c: Coincident(g0,g-1)
    c: Distance(g0) = 6
    c: Vertical(g0)
    c: Coincident(g3,g0)
    c: Weight(g1) = 1
    c: Equal(g1,g2)
    c: InternalAlignment(g1,g3)
    c: InternalAlignment(g2,g3)
    c: InternalAlignment(g4,g3)
    c: InternalAlignment(g5,g3)
    c: Block(g3)
    c: Coincident(g6,g0)
    c: Coincident(g6,g3)
    c: Horizontal(g6)
FEATURE [Part::Extrusion] Extrude030  label="caseScrewPillarBracket008"
  Base = -> Sketch039
  Dir = (0,0,1)
  DirMode = 2
  FaceMakerClass = Part::FaceMakerBullseye
  LengthFwd = 2.4
  LengthRev = 0
  Placement = pos=(15.76,29,8.8) rot=(0,1,0;0rad)
  Solid = true
  Symmetric = false
FEATURE [Part::Extrusion] Extrude031  label="caseScrewPillarBracket009"
  Base = -> Sketch040
  Dir = (0,0,1)
  DirMode = 2
  FaceMakerClass = Part::FaceMakerBullseye
  LengthFwd = 2.4
  LengthRev = 0
  Placement = pos=(15.76,29,60.8) rot=(0,0,1;0rad)
  Solid = true
  Symmetric = false
FEATURE [Part::Extrusion] Extrude032  label="caseScrewPillarBracket010"
  Base = -> Sketch041
  Dir = (0,0,1)
  DirMode = 2
  FaceMakerClass = Part::FaceMakerBullseye
  LengthFwd = 2.4
  LengthRev = 0
  Placement = pos=(13.7,29,13.26) rot=(0,-1,0;1.5708rad)
  Solid = true
  Symmetric = false
FEATURE [Part::Extrusion] Extrude033  label="caseScrewPillarBracket011"
  Base = -> Sketch042
  Dir = (0,0,1)
  DirMode = 2
  FaceMakerClass = Part::FaceMakerBullseye
  LengthFwd = 2.4
  LengthRev = 0
  Placement = pos=(11.3,29,58.74) rot=(0,1,0;1.5708rad)
  Solid = true
  Symmetric = false
FEATURE [Sketcher::SketchObject] Sketch043
  FullyConstrained = true
  sketch-geometry (7):
    g0: LineSegment StartX=0 StartY=0 StartZ=0 EndX=0 EndY=6 EndZ=0
    g1: Circle CenterX=0 CenterY=0 CenterZ=0 NormalX=0 NormalY=0 NormalZ=1 AngleXU=0 Radius=1
    g2: Circle CenterX=8 CenterY=6 CenterZ=0 NormalX=0 NormalY=0 NormalZ=1 AngleXU=0 Radius=1
    g3: BSplineCurve PolesCount=3 KnotsCount=2 Degree=2 IsPeriodic=0
    g4: GeomPoint X=0 Y=0 Z=0
    g5: GeomPoint X=8 Y=6 Z=0
    g6: LineSegment StartX=0 StartY=6 StartZ=0 EndX=8 EndY=6 EndZ=0
  constraints (14):
    c: Coincident(g0,g-1)
    c: Distance(g0) = 6
    c: Vertical(g0)
    c: Coincident(g3,g0)
    c: Weight(g1) = 1
    c: Equal(g1,g2)
    c: InternalAlignment(g1,g3)
    c: InternalAlignment(g2,g3)
    c: InternalAlignment(g4,g3)
    c: InternalAlignment(g5,g3)
    c: Block(g3)
    c: Coincident(g6,g0)
    c: Coincident(g6,g3)
    c: Horizontal(g6)
FEATURE [Part::Extrusion] Extrude034  label="caseScrewPillarBracket012"
  Base = -> Sketch043
  Dir = (0,0,1)
  DirMode = 2
  FaceMakerClass = Part::FaceMakerBullseye
  LengthFwd = 2.4
  LengthRev = 0
  Placement = pos=(88.3,29,65.23) rot=(0,1,0;1.5708rad)
  Solid = true
  Symmetric = false
FEATURE [Sketcher::SketchObject] Sketch044
  FullyConstrained = true
  sketch-geometry (7):
    g0: LineSegment StartX=0 StartY=0 StartZ=0 EndX=0 EndY=6 EndZ=0
    g1: Circle CenterX=0 CenterY=0 CenterZ=0 NormalX=0 NormalY=0 NormalZ=1 AngleXU=0 Radius=1
    g2: Circle CenterX=8 CenterY=6 CenterZ=0 NormalX=0 NormalY=0 NormalZ=1 AngleXU=0 Radius=1
    g3: BSplineCurve PolesCount=3 KnotsCount=2 Degree=2 IsPeriodic=0
    g4: GeomPoint X=0 Y=0 Z=0
    g5: GeomPoint X=8 Y=6 Z=0
    g6: LineSegment StartX=0 StartY=6 StartZ=0 EndX=8 EndY=6 EndZ=0
  constraints (14):
    c: Coincident(g0,g-1)
    c: Distance(g0) = 6
    c: Vertical(g0)
    c: Coincident(g3,g0)
    c: Weight(g1) = 1
    c: Equal(g1,g2)
    c: InternalAlignment(g1,g3)
    c: InternalAlignment(g2,g3)
    c: InternalAlignment(g4,g3)
    c: InternalAlignment(g5,g3)
    c: Block(g3)
    c: Coincident(g6,g0)
    c: Coincident(g6,g3)
    c: Horizontal(g6)
FEATURE [Part::Extrusion] Extrude035  label="caseScrewPillarBracket013"
  Base = -> Sketch044
  Dir = (0,0,1)
  DirMode = 2
  FaceMakerClass = Part::FaceMakerBullseye
  LengthFwd = 2.4
  LengthRev = 0
  Placement = pos=(90.7,29,6.77) rot=(0,-1,0;1.5708rad)
  Solid = true
  Symmetric = false
FEATURE [Sketcher::SketchObject] Sketch045
  FullyConstrained = true
  sketch-geometry (7):
    g0: LineSegment StartX=0 StartY=0 StartZ=0 EndX=0 EndY=6 EndZ=0
    g1: Circle CenterX=0 CenterY=0 CenterZ=0 NormalX=0 NormalY=0 NormalZ=1 AngleXU=0 Radius=1
    g2: Circle CenterX=8 CenterY=6 CenterZ=0 NormalX=0 NormalY=0 NormalZ=1 AngleXU=0 Radius=1
    g3: BSplineCurve PolesCount=3 KnotsCount=2 Degree=2 IsPeriodic=0
    g4: GeomPoint X=0 Y=0 Z=0
    g5: GeomPoint X=8 Y=6 Z=0
    g6: LineSegment StartX=0 StartY=6 StartZ=0 EndX=8 EndY=6 EndZ=0
  constraints (14):
    c: Coincident(g0,g-1)
    c: Distance(g0) = 6
    c: Vertical(g0)
    c: Coincident(g3,g0)
    c: Weight(g1) = 1
    c: Equal(g1,g2)
    c: InternalAlignment(g1,g3)
    c: InternalAlignment(g2,g3)
    c: InternalAlignment(g4,g3)
    c: InternalAlignment(g5,g3)
    c: Block(g3)
    c: Coincident(g6,g0)
    c: Coincident(g6,g3)
    c: Horizontal(g6)
FEATURE [Sketcher::SketchObject] Sketch046
  FullyConstrained = true
  sketch-geometry (7):
    g0: LineSegment StartX=0 StartY=0 StartZ=0 EndX=0 EndY=6 EndZ=0
    g1: Circle CenterX=0 CenterY=0 CenterZ=0 NormalX=0 NormalY=0 NormalZ=1 AngleXU=0 Radius=1
    g2: Circle CenterX=8 CenterY=6 CenterZ=0 NormalX=0 NormalY=0 NormalZ=1 AngleXU=0 Radius=1
    g3: BSplineCurve PolesCount=3 KnotsCount=2 Degree=2 IsPeriodic=0
    g4: GeomPoint X=0 Y=0 Z=0
    g5: GeomPoint X=8 Y=6 Z=0
    g6: LineSegment StartX=0 StartY=6 StartZ=0 EndX=8 EndY=6 EndZ=0
  constraints (14):
    c: Coincident(g0,g-1)
    c: Distance(g0) = 6
    c: Vertical(g0)
    c: Coincident(g3,g0)
    c: Weight(g1) = 1
    c: Equal(g1,g2)
    c: InternalAlignment(g1,g3)
    c: InternalAlignment(g2,g3)
    c: InternalAlignment(g4,g3)
    c: InternalAlignment(g5,g3)
    c: Block(g3)
    c: Coincident(g6,g0)
    c: Coincident(g6,g3)
    c: Horizontal(g6)
FEATURE [Part::Extrusion] Extrude036  label="caseScrewPillarBracket014"
  Base = -> Sketch045
  Dir = (0,0,1)
  DirMode = 2
  FaceMakerClass = Part::FaceMakerBullseye
  LengthFwd = 2.4
  LengthRev = 0
  Placement = pos=(110.7,29,6.77) rot=(0,-1,0;1.5708rad)
  Solid = true
  Symmetric = false
FEATURE [Part::Extrusion] Extrude037  label="caseScrewPillarBracket015"
  Base = -> Sketch046
  Dir = (0,0,1)
  DirMode = 2
  FaceMakerClass = Part::FaceMakerBullseye
  LengthFwd = 2.4
  LengthRev = 0
  Placement = pos=(108.3,29,65.23) rot=(0,1,0;1.5708rad)
  Solid = true
  Symmetric = false
FEATURE [Part::Box] Box013  label="frontCaseScrewPillarBracket002"
  AttacherType = Attacher::AttachEngine3D
  Height = 2.4
  Length = 22
  Placement = pos=(87,28,2.3) rot=(0,0,1;0rad)
  Width = 7
FEATURE [Part::Box] Box014  label="frontCaseScrewPillarBracket003"
  AttacherType = Attacher::AttachEngine3D
  Height = 2.4
  Length = 22
  Placement = pos=(87,28,67.3) rot=(0,0,1;0rad)
  Width = 7
FEATURE [Part::Feature] Face087
  shape: bbox 4.8 x 30.2 x 2e-07 mm, 1 faces, 0 solids (baked)
FEATURE [Part::Revolution] Revolve091  label="frontCaseScrewPost004"
  Angle = 360
  Axis = (0,1,0)
  Base = (0,0,0)
  FaceMakerClass = Part::FaceMakerBullseye
  Placement = pos=(89.5,4.5,3.5) rot=(0,0,1;0rad)
  Solid = false
  Source = -> Face087
  Symmetric = false
FEATURE [Part::Feature] Face088
  shape: bbox 4.8 x 30.2 x 2e-07 mm, 1 faces, 0 solids (baked)
FEATURE [Part::Revolution] Revolve092  label="frontCaseScrewPost005"
  Angle = 360
  Axis = (0,1,0)
  Base = (0,0,0)
  FaceMakerClass = Part::FaceMakerBullseye
  Placement = pos=(89.5,4.5,68.5) rot=(0,0,1;0rad)
  Solid = false
  Source = -> Face088
  Symmetric = false
FEATURE [Part::Feature] Face089
  shape: bbox 3.5 x 30.2 x 2e-07 mm, 1 faces, 0 solids (baked)
FEATURE [Part::Revolution] Revolve093  label="backCaseScrewPost002"
  Angle = 360
  Axis = (0,1,0)
  Base = (0,0,0)
  FaceMakerClass = Part::FaceMakerBullseye
  Placement = pos=(12.5,4.5,10) rot=(0,0,1;0rad)
  Solid = false
  Source = -> Face089
  Symmetric = false
FEATURE [Part::Feature] Face090
  shape: bbox 3.5 x 30.2 x 2e-07 mm, 1 faces, 0 solids (baked)
FEATURE [Part::Revolution] Revolve094  label="backCaseScrewPost003"
  Angle = 360
  Axis = (0,1,0)
  Base = (0,0,0)
  FaceMakerClass = Part::FaceMakerBullseye
  Placement = pos=(12.5,4.5,62) rot=(0,0,1;0rad)
  Solid = false
  Source = -> Face090
  Symmetric = false
FEATURE [Part::Box] Box015  label="Cube011"
  AttacherType = Attacher::AttachEngine3D
  Height = 28.8
  Length = 3
  Placement = pos=(107.3,28,21.6) rot=(0,0,1;0rad)
  Width = 7
FEATURE [Part::Box] Box016  label="Cube012"
  AttacherType = Attacher::AttachEngine3D
  Height = 3
  Length = 7.4
  Placement = pos=(107.3,28,18.6) rot=(0,0,1;0rad)
  Width = 7
FEATURE [Part::Box] Box017  label="Cube013"
  AttacherType = Attacher::AttachEngine3D
  Height = 3
  Length = 7.4
  Placement = pos=(107.3,28,50.4) rot=(0,0,1;0rad)
  Width = 7
FEATURE [Part::Cylinder] Cylinder024
  Angle = 360
  AttacherType = Attacher::AttachEngine3D
  Height = 20
  Placement = pos=(0,0,36.15) rot=(0,0,1;0rad)
  Radius = 14.3
FEATURE [Part::Cylinder] Cylinder025
  Angle = 360
  AttacherType = Attacher::AttachEngine3D
  Height = 10
  Placement = pos=(0,0,36.15) rot=(0,0,1;0rad)
  Radius = 4
FEATURE [Part::MultiFuse] Fusion066  label="removeToCreteHoleForPlugHousing009"
  Placement = pos=(70,19,36) rot=(0,1,0;1.5708rad)
  Shapes = -> [Cylinder024,Cylinder025]
FEATURE [Part::MultiFuse] Fusion065  label="plugHousingBracketHolder002"
  Shapes = -> [Box017,Box015,Box016]
FEATURE [Part::Cut] Cut025  label="plugHousingBracketHolder003"
  Base = -> Fusion065
  Placement = pos=(7,0,0) rot=(0,0,1;0rad)
  Tool = -> Fusion066
FEATURE [Sketcher::SketchObject] Sketch047
  FullyConstrained = false
  Placement = pos=(0,0,0) rot=(1,0,0;1.5708rad)
  sketch-geometry (24):
    g0: ArcOfCircle CenterX=-4 CenterY=-10.5 CenterZ=0 NormalX=0 NormalY=0 NormalZ=1 AngleXU=0 Radius=1.5 StartAngle=6e-16 EndAngle=3.14159
    g1: ArcOfCircle CenterX=-34.2 CenterY=-10.5 CenterZ=0 NormalX=0 NormalY=0 NormalZ=1 AngleXU=0 Radius=1.5 StartAngle=0 EndAngle=3.14159
    g2: ArcOfCircle CenterX=-34.2 CenterY=-27.7 CenterZ=0 NormalX=0 NormalY=0 NormalZ=1 AngleXU=0 Radius=1.5 StartAngle=3.14159 EndAngle=6.28319
    g3: ArcOfCircle CenterX=-4 CenterY=-27.7 CenterZ=0 NormalX=0 NormalY=0 NormalZ=1 AngleXU=0 Radius=1.5 StartAngle=3.1416 EndAngle=6.28319
    g4: ArcOfCircle CenterX=-10 CenterY=-4.3 CenterZ=0 NormalX=0 NormalY=0 NormalZ=1 AngleXU=0 Radius=1.5 StartAngle=2e-16 EndAngle=3.14159
    g5: ArcOfCircle CenterX=-16.1 CenterY=-1.8 CenterZ=0 NormalX=0 NormalY=0 NormalZ=1 AngleXU=0 Radius=1.5 StartAngle=5e-16 EndAngle=3.14159
    g6: ArcOfCircle CenterX=-22.1 CenterY=-1.8 CenterZ=0 NormalX=0 NormalY=0 NormalZ=1 AngleXU=0 Radius=1.5 StartAngle=5e-16 EndAngle=3.14159
    g7: ArcOfCircle CenterX=-28.2 CenterY=-4.3 CenterZ=0 NormalX=0 NormalY=0 NormalZ=1 AngleXU=0 Radius=1.5 StartAngle=2e-16 EndAngle=3.14159
    g8: ArcOfCircle CenterX=-10 CenterY=-33.9 CenterZ=0 NormalX=0 NormalY=0 NormalZ=1 AngleXU=0 Radius=1.5 StartAngle=3.14159 EndAngle=6.28319
    g9: ArcOfCircle CenterX=-16.1 CenterY=-36.4 CenterZ=0 NormalX=0 NormalY=0 NormalZ=1 AngleXU=0 Radius=1.5 StartAngle=3.14159 EndAngle=6.28319
    g10: ArcOfCircle CenterX=-22.1 CenterY=-36.4 CenterZ=0 NormalX=0 NormalY=0 NormalZ=1 AngleXU=0 Radius=1.5 StartAngle=3.14159 EndAngle=6.28319
    g11: ArcOfCircle CenterX=-28.2 CenterY=-33.9 CenterZ=0 NormalX=0 NormalY=0 NormalZ=1 AngleXU=0 Radius=1.5 StartAngle=3.14159 EndAngle=6.28319
    g12: LineSegment StartX=-35.7 StartY=-10.5 StartZ=0 EndX=-35.7 EndY=-27.7 EndZ=0
    g13: LineSegment StartX=-32.7 StartY=-10.5 StartZ=0 EndX=-32.7 EndY=-27.7 EndZ=0
    g14: LineSegment StartX=-29.7 StartY=-33.9 StartZ=0 EndX=-29.7 EndY=-4.3 EndZ=0
    g15: LineSegment StartX=-26.7 StartY=-33.9 StartZ=0 EndX=-26.7 EndY=-4.3 EndZ=0
    g16: LineSegment StartX=-2.5 StartY=-10.5 StartZ=0 EndX=-2.5 EndY=-27.7 EndZ=0
    g17: LineSegment StartX=-8.5 StartY=-4.3 StartZ=0 EndX=-8.5 EndY=-33.9 EndZ=0
    g18: LineSegment StartX=-5.5 StartY=-10.5 StartZ=0 EndX=-5.5 EndY=-27.7 EndZ=0
    g19: LineSegment StartX=-11.5 StartY=-4.3 StartZ=0 EndX=-11.5 EndY=-33.9 EndZ=0
    g20: LineSegment StartX=-14.6 StartY=-1.8 StartZ=0 EndX=-14.6 EndY=-36.4 EndZ=0
    g21: LineSegment StartX=-17.6 StartY=-1.8 StartZ=0 EndX=-17.6 EndY=-36.4 EndZ=0
    g22: LineSegment StartX=-20.6 StartY=-36.4 StartZ=0 EndX=-20.6 EndY=-1.8 EndZ=0
    g23: LineSegment StartX=-23.6 StartY=-1.8 StartZ=0 EndX=-23.6 EndY=-36.4 EndZ=0
  constraints (48):
    c: Block(g0)
    c: Block(g1)
    c: Block(g2)
    c: Block(g3)
    c: Block(g4)
    c: Block(g5)
    c: Block(g6)
    c: Block(g7)
    c: Block(g8)
    c: Block(g9)
    c: Block(g10)
    c: Block(g11)
    c: Coincident(g12,g1)
    c: Coincident(g12,g2)
    c: Vertical(g12)
    c: Coincident(g13,g1)
    c: Coincident(g13,g2)
    c: Vertical(g13)
    c: Coincident(g14,g11)
    c: Coincident(g14,g7)
    c: Vertical(g14)
    c: Coincident(g15,g11)
    c: Coincident(g15,g7)
    c: Vertical(g15)
    c: Coincident(g16,g0)
    c: Coincident(g16,g3)
    c: Vertical(g16)
    c: Coincident(g17,g4)
    c: Coincident(g17,g8)
    c: Vertical(g17)
    c: Coincident(g18,g0)
    c: Coincident(g18,g3)
    c: Vertical(g18)
    c: Coincident(g19,g4)
    c: Coincident(g19,g8)
    c: Vertical(g19)
    c: Coincident(g20,g5)
    c: Coincident(g20,g9)
    c: Vertical(g20)
    c: Coincident(g21,g5)
    c: Coincident(g21,g9)
    c: Vertical(g21)
    c: Coincident(g22,g10)
    c: Coincident(g22,g6)
    c: Vertical(g22)
    c: Coincident(g23,g6)
    c: Coincident(g23,g10)
    c: Vertical(g23)
FEATURE [Part::Extrusion] Extrude038  label="removeToCreateFanGrillHoles001"
  Base = -> Sketch047
  Dir = (0,-1,6e-16)
  DirMode = 2
  FaceMakerClass = Part::FaceMakerBullseye
  LengthFwd = 10
  LengthRev = 0
  Placement = pos=(65.4,44,54.82) rot=(0,0,1;0rad)
  Solid = true
  Symmetric = false
FEATURE [Part::Feature] Wire004
  shape: bbox 11 x 5.2 x 2e-07 mm, 0 faces, 0 solids (baked)
FEATURE [Part::Revolution] Revolve095
  Angle = 360
  Axis = (0,1,0)
  Base = (0,0,0)
  FaceMakerClass = Part::FaceMakerBullseye
  Placement = pos=(30.3,38,19.7) rot=(0,0,1;0rad)
  Solid = true
  Source = -> Wire004
  Symmetric = false
FEATURE [Part::Feature] Wire005
  shape: bbox 11 x 5.2 x 2e-07 mm, 0 faces, 0 solids (baked)
FEATURE [Part::Revolution] Revolve096
  Angle = 360
  Axis = (0,1,0)
  Base = (0,0,0)
  FaceMakerClass = Part::FaceMakerBullseye
  Placement = pos=(30.3,38,51.7) rot=(0,0,1;0rad)
  Solid = true
  Source = -> Wire005
  Symmetric = false
FEATURE [Part::Feature] Wire006
  shape: bbox 11 x 5.2 x 2e-07 mm, 0 faces, 0 solids (baked)
FEATURE [Part::Revolution] Revolve097
  Angle = 360
  Axis = (0,1,0)
  Base = (0,0,0)
  FaceMakerClass = Part::FaceMakerBullseye
  Placement = pos=(62.3,38,51.7) rot=(0,0,1;0rad)
  Solid = true
  Source = -> Wire006
  Symmetric = false
FEATURE [Part::Feature] Wire007
  shape: bbox 11 x 5.2 x 2e-07 mm, 0 faces, 0 solids (baked)
FEATURE [Part::Revolution] Revolve098
  Angle = 360
  Axis = (0,1,0)
  Base = (0,0,0)
  FaceMakerClass = Part::FaceMakerBullseye
  Placement = pos=(62.3,38,19.7) rot=(0,0,1;0rad)
  Solid = true
  Source = -> Wire007
  Symmetric = false
FEATURE [Part::MultiFuse] Fusion067  label="fanScrewHousing002"
  Shapes = -> [Revolve098,Revolve097,Revolve096,Revolve095]
FEATURE [Part::Feature] Face091 .. Face094  x4 (patterned run collapsed; names and placements below)
  shape: bbox 3.5 x 17.8 x 2e-07 mm, 1 faces, 0 solids (baked)
FEATURE [Part::Revolution] Revolve099  label="removeToCreateScrewAndThreadedInsertHole026"
  Angle = 360
  Axis = (0,1,0)
  Base = (0,0,0)
  FaceMakerClass = Part::FaceMakerBullseye
  Placement = pos=(62.3,30.3,19.7) rot=(0,0,1;0rad)
  Solid = false
  Source = -> Face091
  Symmetric = false
FEATURE [Part::Revolution] Revolve100  label="removeToCreateScrewAndThreadedInsertHole027"
  Angle = 360
  Axis = (0,1,0)
  Base = (0,0,0)
  FaceMakerClass = Part::FaceMakerBullseye
  Placement = pos=(62.3,30.3,51.7) rot=(0,0,1;0rad)
  Solid = false
  Source = -> Face092
  Symmetric = false
FEATURE [Part::Revolution] Revolve101  label="removeToCreateScrewAndThreadedInsertHole028"
  Angle = 360
  Axis = (0,1,0)
  Base = (0,0,0)
  FaceMakerClass = Part::FaceMakerBullseye
  Placement = pos=(30.3,30.3,19.7) rot=(0,0,1;0rad)
  Solid = false
  Source = -> Face093
  Symmetric = false
FEATURE [Part::Revolution] Revolve102  label="removeToCreateScrewAndThreadedInsertHole029"
  Angle = 360
  Axis = (0,1,0)
  Base = (0,0,0)
  FaceMakerClass = Part::FaceMakerBullseye
  Placement = pos=(30.3,30.3,51.7) rot=(0,0,1;0rad)
  Solid = false
  Source = -> Face094
  Symmetric = false
FEATURE [Part::MultiFuse] Fusion068  label="createThreadedInsertHolesForFan002"
  Shapes = -> [Revolve099,Revolve100,Revolve101,Revolve102]
FEATURE [Part::Cut] Cut026  label="fanScrewHousing003"
  Base = -> Fusion067
  Tool = -> Fusion068
FEATURE [Sketcher::SketchObject] Sketch048
  FullyConstrained = false
  Placement = pos=(0,0,0) rot=(1,0,0;1.5708rad)
  sketch-geometry (24):
    g0: ArcOfCircle CenterX=-4 CenterY=-10.5 CenterZ=0 NormalX=0 NormalY=0 NormalZ=1 AngleXU=0 Radius=1.5 StartAngle=6e-16 EndAngle=3.14159
    g1: ArcOfCircle CenterX=-34.2 CenterY=-10.5 CenterZ=0 NormalX=0 NormalY=0 NormalZ=1 AngleXU=0 Radius=1.5 StartAngle=0 EndAngle=3.14159
    g2: ArcOfCircle CenterX=-34.2 CenterY=-27.7 CenterZ=0 NormalX=0 NormalY=0 NormalZ=1 AngleXU=0 Radius=1.5 StartAngle=3.14159 EndAngle=6.28319
    g3: ArcOfCircle CenterX=-4 CenterY=-27.7 CenterZ=0 NormalX=0 NormalY=0 NormalZ=1 AngleXU=0 Radius=1.5 StartAngle=3.1416 EndAngle=6.28319
    g4: ArcOfCircle CenterX=-10 CenterY=-4.3 CenterZ=0 NormalX=0 NormalY=0 NormalZ=1 AngleXU=0 Radius=1.5 StartAngle=2e-16 EndAngle=3.14159
    g5: ArcOfCircle CenterX=-16.1 CenterY=-1.8 CenterZ=0 NormalX=0 NormalY=0 NormalZ=1 AngleXU=0 Radius=1.5 StartAngle=5e-16 EndAngle=3.14159
    g6: ArcOfCircle CenterX=-22.1 CenterY=-1.8 CenterZ=0 NormalX=0 NormalY=0 NormalZ=1 AngleXU=0 Radius=1.5 StartAngle=5e-16 EndAngle=3.14159
    g7: ArcOfCircle CenterX=-28.2 CenterY=-4.3 CenterZ=0 NormalX=0 NormalY=0 NormalZ=1 AngleXU=0 Radius=1.5 StartAngle=2e-16 EndAngle=3.14159
    g8: ArcOfCircle CenterX=-10 CenterY=-33.9 CenterZ=0 NormalX=0 NormalY=0 NormalZ=1 AngleXU=0 Radius=1.5 StartAngle=3.14159 EndAngle=6.28319
    g9: ArcOfCircle CenterX=-16.1 CenterY=-36.4 CenterZ=0 NormalX=0 NormalY=0 NormalZ=1 AngleXU=0 Radius=1.5 StartAngle=3.14159 EndAngle=6.28319
    g10: ArcOfCircle CenterX=-22.1 CenterY=-36.4 CenterZ=0 NormalX=0 NormalY=0 NormalZ=1 AngleXU=0 Radius=1.5 StartAngle=3.14159 EndAngle=6.28319
    g11: ArcOfCircle CenterX=-28.2 CenterY=-33.9 CenterZ=0 NormalX=0 NormalY=0 NormalZ=1 AngleXU=0 Radius=1.5 StartAngle=3.14159 EndAngle=6.28319
    g12: LineSegment StartX=-35.7 StartY=-10.5 StartZ=0 EndX=-35.7 EndY=-27.7 EndZ=0
    g13: LineSegment StartX=-32.7 StartY=-10.5 StartZ=0 EndX=-32.7 EndY=-27.7 EndZ=0
    g14: LineSegment StartX=-29.7 StartY=-33.9 StartZ=0 EndX=-29.7 EndY=-4.3 EndZ=0
    g15: LineSegment StartX=-26.7 StartY=-33.9 StartZ=0 EndX=-26.7 EndY=-4.3 EndZ=0
    g16: LineSegment StartX=-2.5 StartY=-10.5 StartZ=0 EndX=-2.5 EndY=-27.7 EndZ=0
    g17: LineSegment StartX=-8.5 StartY=-4.3 StartZ=0 EndX=-8.5 EndY=-33.9 EndZ=0
    g18: LineSegment StartX=-5.5 StartY=-10.5 StartZ=0 EndX=-5.5 EndY=-27.7 EndZ=0
    g19: LineSegment StartX=-11.5 StartY=-4.3 StartZ=0 EndX=-11.5 EndY=-33.9 EndZ=0
    g20: LineSegment StartX=-14.6 StartY=-1.8 StartZ=0 EndX=-14.6 EndY=-36.4 EndZ=0
    g21: LineSegment StartX=-17.6 StartY=-1.8 StartZ=0 EndX=-17.6 EndY=-36.4 EndZ=0
    g22: LineSegment StartX=-20.6 StartY=-36.4 StartZ=0 EndX=-20.6 EndY=-1.8 EndZ=0
    g23: LineSegment StartX=-23.6 StartY=-1.8 StartZ=0 EndX=-23.6 EndY=-36.4 EndZ=0
  constraints (48):
    c: Block(g0)
    c: Block(g1)
    c: Block(g2)
    c: Block(g3)
    c: Block(g4)
    c: Block(g5)
    c: Block(g6)
    c: Block(g7)
    c: Block(g8)
    c: Block(g9)
    c: Block(g10)
    c: Block(g11)
    c: Coincident(g12,g1)
    c: Coincident(g12,g2)
    c: Vertical(g12)
    c: Coincident(g13,g1)
    c: Coincident(g13,g2)
    c: Vertical(g13)
    c: Coincident(g14,g11)
    c: Coincident(g14,g7)
    c: Vertical(g14)
    c: Coincident(g15,g11)
    c: Coincident(g15,g7)
    c: Vertical(g15)
    c: Coincident(g16,g0)
    c: Coincident(g16,g3)
    c: Vertical(g16)
    c: Coincident(g17,g4)
    c: Coincident(g17,g8)
    c: Vertical(g17)
    c: Coincident(g18,g0)
    c: Coincident(g18,g3)
    c: Vertical(g18)
    c: Coincident(g19,g4)
    c: Coincident(g19,g8)
    c: Vertical(g19)
    c: Coincident(g20,g5)
    c: Coincident(g20,g9)
    c: Vertical(g20)
    c: Coincident(g21,g5)
    c: Coincident(g21,g9)
    c: Vertical(g21)
    c: Coincident(g22,g10)
    c: Coincident(g22,g6)
    c: Vertical(g22)
    c: Coincident(g23,g6)
    c: Coincident(g23,g10)
    c: Vertical(g23)
FEATURE [Part::Extrusion] Extrude039  label="removeToCreateFanGrillHoles002"
  Base = -> Sketch048
  Dir = (0,-1,6e-16)
  DirMode = 2
  FaceMakerClass = Part::FaceMakerBullseye
  LengthFwd = 10
  LengthRev = 0
  Placement = pos=(65.4,44,54.82) rot=(0,0,1;0rad)
  Solid = true
  Symmetric = false
FEATURE [Part::Cut] Cut027  label="fanScrewHousing004"
  Base = -> Cut026
  Tool = -> Extrude038
FEATURE [Part::Cut] Cut028  label="top014"
  Base = -> Fillet026
  Tool = -> Extrude039
FEATURE [Part::Feature] Face095 .. Face098  x4 (patterned run collapsed; names and placements below)
  shape: bbox 3.5 x 17.8 x 2e-07 mm, 1 faces, 0 solids (baked)
FEATURE [Part::Revolution] Revolve103  label="removeToCreateScrewAndThreadedInsertHole030"
  Angle = 360
  Axis = (0,1,0)
  Base = (0,0,0)
  FaceMakerClass = Part::FaceMakerBullseye
  Placement = pos=(62.3,30.3,19.7) rot=(0,0,1;0rad)
  Solid = false
  Source = -> Face095
  Symmetric = false
FEATURE [Part::Revolution] Revolve104  label="removeToCreateScrewAndThreadedInsertHole031"
  Angle = 360
  Axis = (0,1,0)
  Base = (0,0,0)
  FaceMakerClass = Part::FaceMakerBullseye
  Placement = pos=(62.3,30.3,51.7) rot=(0,0,1;0rad)
  Solid = false
  Source = -> Face096
  Symmetric = false
FEATURE [Part::Revolution] Revolve105  label="removeToCreateScrewAndThreadedInsertHole032"
  Angle = 360
  Axis = (0,1,0)
  Base = (0,0,0)
  FaceMakerClass = Part::FaceMakerBullseye
  Placement = pos=(30.3,30.3,19.7) rot=(0,0,1;0rad)
  Solid = false
  Source = -> Face097
  Symmetric = false
FEATURE [Part::Revolution] Revolve106  label="removeToCreateScrewAndThreadedInsertHole033"
  Angle = 360
  Axis = (0,1,0)
  Base = (0,0,0)
  FaceMakerClass = Part::FaceMakerBullseye
  Placement = pos=(30.3,30.3,51.7) rot=(0,0,1;0rad)
  Solid = false
  Source = -> Face098
  Symmetric = false
FEATURE [Part::MultiFuse] Fusion069  label="createThreadedInsertHolesForFan003"
  Shapes = -> [Revolve103,Revolve104,Revolve105,Revolve106]
FEATURE [Part::Cut] Cut029  label="top015"
  Base = -> Cut028
  Tool = -> Fusion054
FEATURE [Part::Cut] Cut030  label="fanScrewHousing005"
  Base = -> Cut027
  Tool = -> Fusion069
FEATURE [Part::Cylinder] Cylinder026  label="removeToCreteHoleForPlugHousing010"
  Angle = 360
  AttacherType = Attacher::AttachEngine3D
  Height = 20
  Placement = pos=(-2,19,36) rot=(0,1,0;1.5708rad)
  Radius = 14.3
FEATURE [Part::Box] Box018  label="removeToCreteHoleForPlugHousing011"
  AttacherType = Attacher::AttachEngine3D
  Height = 28.6
  Length = 10
  Placement = pos=(-2,0,21.7) rot=(0,0,1;0rad)
  Width = 19
FEATURE [Part::Box] Box019  label="wireHolderBottomCaseBit"
  AttacherType = Attacher::AttachEngine3D
  Height = 28
  Length = 3
  Placement = pos=(0,0,22) rot=(0,0,1;0rad)
  Width = 21
FEATURE [Part::Cylinder] Cylinder027  label="removeToCreteHoleForPlugHousing012"
  Angle = 360
  AttacherType = Attacher::AttachEngine3D
  Height = 20
  Placement = pos=(-2,19,36) rot=(0,1,0;1.5708rad)
  Radius = 14.3
FEATURE [Part::Cut] Cut031  label="wireHolderBottomCaseBit001"
  Base = -> Box019
  Tool = -> Cylinder027
FEATURE [Part::MultiFuse] Fusion070  label="removeToCreteHoleForPlugHousing013"
  Shapes = -> [Box018,Cylinder026]
FEATURE [Part::Cut] Cut032  label="top016"
  Base = -> Cut029
  Tool = -> Fusion070
FEATURE [Part::Cylinder] Cylinder028
  Angle = 360
  AttacherType = Attacher::AttachEngine3D
  Height = 20
  Placement = pos=(0,0,36.15) rot=(0,0,1;0rad)
  Radius = 14.3
FEATURE [Part::Cylinder] Cylinder029
  Angle = 360
  AttacherType = Attacher::AttachEngine3D
  Height = 10
  Placement = pos=(0,0,36.15) rot=(0,0,1;0rad)
  Radius = 4
FEATURE [Part::MultiFuse] Fusion071  label="removeToCreteHoleForPlugHousing014"
  Placement = pos=(70,19,36) rot=(0,1,0;1.5708rad)
  Shapes = -> [Cylinder028,Cylinder029]
FEATURE [Sketcher::SketchObject] Sketch049  label="topSketch011"
  FullyConstrained = true
  sketch-geometry (4):
    g0: ArcOfCircle CenterX=105 CenterY=19 CenterZ=0 NormalX=0 NormalY=0 NormalZ=1 AngleXU=0 Radius=20.6155 StartAngle=5.54125 EndAngle=6.28319
    g1: ArcOfCircle CenterX=105 CenterY=19 CenterZ=0 NormalX=0 NormalY=0 NormalZ=1 AngleXU=0 Radius=13 StartAngle=5.54125 EndAngle=6.28319
    g2: LineSegment StartX=118 StartY=19 StartZ=0 EndX=125.616 EndY=19 EndZ=0
    g3: LineSegment StartX=114.583 StartY=10.2157 StartZ=0 EndX=120.197 EndY=5.06982 EndZ=0
  constraints (7):
    c: Block(g0)
    c: Block(g1)
    c: Coincident(g2,g1)
    c: Coincident(g2,g0)
    c: Horizontal(g2)
    c: Coincident(g3,g1)
    c: Coincident(g3,g0)
FEATURE [Part::Box] Box020  label="removeToCreteHoleForPlugHousing015"
  AttacherType = Attacher::AttachEngine3D
  Height = 28.6
  Length = 20
  Placement = pos=(106.15,0,21.7) rot=(0,0,1;0rad)
  Width = 19
FEATURE [Part::MultiFuse] Fusion072  label="removeToCreteHoleForPlugHousing016"
  Shapes = -> [Box020,Fusion071]
FEATURE [Part::Cut] Cut033  label="removeToCreteHoleForPlugHousing017"
  Base = -> Cut032
  Tool = -> Fusion072
FEATURE [Part::Cylinder] Cylinder030
  Angle = 360
  AttacherType = Attacher::AttachEngine3D
  Height = 20
  Placement = pos=(0,0,36.15) rot=(0,0,1;0rad)
  Radius = 14.3
FEATURE [Part::Cylinder] Cylinder031
  Angle = 360
  AttacherType = Attacher::AttachEngine3D
  Height = 10
  Placement = pos=(0,0,36.15) rot=(0,0,1;0rad)
  Radius = 4
FEATURE [Part::Box] Box021  label="removeToCreteHoleForPlugHousing019"
  AttacherType = Attacher::AttachEngine3D
  Height = 28.6
  Length = 20
  Placement = pos=(106.15,0,21.7) rot=(0,0,1;0rad)
  Width = 19
FEATURE [Part::MultiFuse] Fusion074  label="removeToCreteHoleForPlugHousing020"
  Placement = pos=(70,19,36) rot=(0,1,0;1.5708rad)
  Shapes = -> [Cylinder030,Cylinder031]
FEATURE [Part::MultiFuse] Fusion073  label="removeToCreteHoleForPlugHousing018"
  Placement = pos=(0,0,28.3) rot=(0,0,1;0rad)
  Shapes = -> [Box021,Fusion074]
FEATURE [Part::Cylinder] Cylinder032
  Angle = 360
  AttacherType = Attacher::AttachEngine3D
  Height = 20
  Placement = pos=(0,0,36.15) rot=(0,0,1;0rad)
  Radius = 14.3
FEATURE [Part::Cylinder] Cylinder033
  Angle = 360
  AttacherType = Attacher::AttachEngine3D
  Height = 10
  Placement = pos=(0,0,36.15) rot=(0,0,1;0rad)
  Radius = 4
FEATURE [Part::Box] Box022  label="removeToCreteHoleForPlugHousing021"
  AttacherType = Attacher::AttachEngine3D
  Height = 28.6
  Length = 20
  Placement = pos=(106.15,0,21.7) rot=(0,0,1;0rad)
  Width = 19
FEATURE [Part::MultiFuse] Fusion076  label="removeToCreteHoleForPlugHousing023"
  Placement = pos=(70,19,36) rot=(0,1,0;1.5708rad)
  Shapes = -> [Cylinder032,Cylinder033]
FEATURE [Part::MultiFuse] Fusion075  label="removeToCreteHoleForPlugHousing022"
  Placement = pos=(0,0,-28.3) rot=(0,0,1;0rad)
  Shapes = -> [Box022,Fusion076]
FEATURE [Part::MultiFuse] Fusion077  label="removeToCreatePlugHousingBottomBit"
  Shapes = -> [Fusion075,Fusion073]
FEATURE [Part::Cylinder] Cylinder034
  Angle = 360
  AttacherType = Attacher::AttachEngine3D
  Height = 20
  Placement = pos=(0,0,36.15) rot=(0,0,1;0rad)
  Radius = 14
FEATURE [Part::Cylinder] Cylinder035
  Angle = 360
  AttacherType = Attacher::AttachEngine3D
  Height = 10
  Placement = pos=(0,0,36.15) rot=(0,0,1;0rad)
  Radius = 4
FEATURE [Part::MultiFuse] Fusion078  label="removeToCreteHoleForPlugHousing024"
  Placement = pos=(70,19,36) rot=(0,1,0;1.5708rad)
  Shapes = -> [Cylinder034,Cylinder035]
FEATURE [Part::MultiFuse] Fusion079  label="removeToCreatePlugHousingBottomBit001"
  Shapes = -> [Fusion078,Fusion077]
FEATURE [Part::Extrusion] Extrude040  label="bottomPlugHousingBit"
  Base = -> Sketch049
  Dir = (0,0,1)
  DirMode = 2
  FaceMakerClass = Part::FaceMakerBullseye
  LengthFwd = 72
  LengthRev = 0
  Solid = true
  Symmetric = false
FEATURE [Part::Cut] Cut034  label="bottomPlugHousingBit001"
  Base = -> Extrude040
  Placement = pos=(-0.09,0,0) rot=(0,0,1;0rad)
  Tool = -> Fusion079
FEATURE [Part::Box] Box023  label="Cube014"
  AttacherType = Attacher::AttachEngine3D
  Height = 16
  Length = 8
  Placement = pos=(12.7,31.52,28) rot=(0,0,1;0rad)
  Width = 4
FEATURE [Part::Cylinder] Cylinder036
  Angle = 360
  AttacherType = Attacher::AttachEngine3D
  Height = 10
  Placement = pos=(0,0,36.15) rot=(0,0,1;0rad)
  Radius = 4
FEATURE [Part::Cylinder] Cylinder037
  Angle = 360
  AttacherType = Attacher::AttachEngine3D
  Height = 20
  Placement = pos=(0,0,36.15) rot=(0,0,1;0rad)
  Radius = 8.2
FEATURE [Part::MultiFuse] Fusion080  label="removeToCreteHoleForPlugHousing025"
  Placement = pos=(-42,19,36) rot=(0,1,0;1.5708rad)
  Shapes = -> [Cylinder037,Cylinder036]
FEATURE [Sketcher::SketchObject] Sketch050  label="topSketch012"
  FullyConstrained = true
  sketch-geometry (4):
    g0: LineSegment StartX=16.8446 StartY=31.512 StartZ=0 EndX=16.3251 EndY=34.4666 EndZ=0
    g1: ArcOfCircle CenterX=19 CenterY=19.2524 CenterZ=0 NormalX=0 NormalY=0 NormalZ=1 AngleXU=0 Radius=15.4476 StartAngle=1.74483 EndAngle=2.72717
    g2: ArcOfCircle CenterX=19 CenterY=19.2524 CenterZ=0 NormalX=0 NormalY=0 NormalZ=1 AngleXU=0 Radius=12.4476 StartAngle=1.74483 EndAngle=2.73189
    g3: LineSegment StartX=4.86004 StartY=25.4725 StartZ=0 EndX=7.58253 EndY=24.2107 EndZ=0
  constraints (7):
    c: Block(g0)
    c: Coincident(g1,g0)
    c: Coincident(g2,g0)
    c: Coincident(g3,g1)
    c: Coincident(g3,g2)
    c: Block(g1)
    c: Block(g2)
FEATURE [Part::Extrusion] Extrude041
  Base = -> Sketch050
  Dir = (0,0,1)
  DirMode = 2
  FaceMakerClass = Part::FaceMakerBullseye
  LengthFwd = 10.6
  LengthRev = 0
  Placement = pos=(0,0,31) rot=(0,0,1;0rad)
  Solid = true
  Symmetric = false
FEATURE [Part::Cut] Cut035
  Base = -> Extrude041
  Placement = pos=(0,0,-0.3) rot=(0,0,1;0rad)
  Tool = -> Fusion080
FEATURE [Part::Cut] Cut036
  Base = -> Box023
  Tool = -> Cut035
FEATURE [Part::Fillet] Fillet027
  Base = -> Cut036
  Edges = 1 edges r=0.7: [Edge13]
FEATURE [Part::Fillet] Fillet028
  Base = -> Fillet027
  Edges = 1 edges r=0.7: [Edge13]
FEATURE [Part::Fillet] Fillet029
  Base = -> Fillet028
  Edges = 1 edges r=0.7: [Edge16]
FEATURE [Part::Fillet] Fillet030
  Base = -> Fillet029
  Edges = 1 edges r=0.7: [Edge11]
FEATURE [Part::Fillet] Fillet031
  Base = -> Fillet030
  Edges = 1 edges r=0.7: [Edge10]
FEATURE [Part::Fillet] Fillet032
  Base = -> Fillet031
  Edges = 1 edges r=1.2: [Edge5]
FEATURE [Part::Fillet] Fillet033
  Base = -> Fillet032
  Edges = 1 edges r=1.2: [Edge12]
FEATURE [Part::Fillet] Fillet034  label="wireHousingRetainer"
  Base = -> Fillet033
  Edges = 1 edges r=2: [Edge1]
  Placement = pos=(0.3,0,0) rot=(0,0,1;0rad)
FEATURE [Part::Feature] Face099
  shape: bbox 3.5 x 17.8 x 2e-07 mm, 1 faces, 0 solids (baked)
FEATURE [Part::Revolution] Revolve107  label="removeToCreateScrewAndThreadedInsertHole034"
  Angle = 360
  Axis = (0,1,0)
  Base = (0,0,0)
  FaceMakerClass = Part::FaceMakerBullseye
  Placement = pos=(12.5,0,10) rot=(0,0,1;0rad)
  Solid = false
  Source = -> Face099
  Symmetric = false
FEATURE [Part::Feature] Face100
  shape: bbox 3.5 x 17.8 x 2e-07 mm, 1 faces, 0 solids (baked)
FEATURE [Part::Revolution] Revolve108  label="removeToCreateScrewAndThreadedInsertHole035"
  Angle = 360
  Axis = (0,1,0)
  Base = (0,0,0)
  FaceMakerClass = Part::FaceMakerBullseye
  Placement = pos=(12.5,0,62) rot=(0,0,1;0rad)
  Solid = false
  Source = -> Face100
  Symmetric = false
FEATURE [Part::Feature] Face101
  shape: bbox 3.5 x 17.8 x 2e-07 mm, 1 faces, 0 solids (baked)
FEATURE [Part::Revolution] Revolve109  label="removeToCreateScrewAndThreadedInsertHole036"
  Angle = 360
  Axis = (0,1,0)
  Base = (0,0,0)
  FaceMakerClass = Part::FaceMakerBullseye
  Placement = pos=(89.5,0,68.5) rot=(0,0,1;0rad)
  Solid = false
  Source = -> Face101
  Symmetric = false
FEATURE [Part::Feature] Face102
  shape: bbox 3.5 x 17.8 x 2e-07 mm, 1 faces, 0 solids (baked)
FEATURE [Part::Revolution] Revolve110  label="removeToCreateScrewAndThreadedInsertHole037"
  Angle = 360
  Axis = (0,1,0)
  Base = (0,0,0)
  FaceMakerClass = Part::FaceMakerBullseye
  Placement = pos=(89.5,0,3.5) rot=(0,0,1;0rad)
  Solid = false
  Source = -> Face102
  Symmetric = false
FEATURE [Part::Feature] Face103
  shape: bbox 3.5 x 17.8 x 2e-07 mm, 1 faces, 0 solids (baked)
FEATURE [Part::Revolution] Revolve111  label="removeToCreateScrewAndThreadedInsertHole038"
  Angle = 360
  Axis = (0,1,0)
  Base = (0,0,0)
  FaceMakerClass = Part::FaceMakerBullseye
  Placement = pos=(109.5,4.7,3.5) rot=(0,0,1;0rad)
  Solid = false
  Source = -> Face103
  Symmetric = false
FEATURE [Part::Feature] Face104
  shape: bbox 3.5 x 17.8 x 2e-07 mm, 1 faces, 0 solids (baked)
FEATURE [Part::Revolution] Revolve112  label="removeToCreateScrewAndThreadedInsertHole039"
  Angle = 360
  Axis = (0,1,0)
  Base = (0,0,0)
  FaceMakerClass = Part::FaceMakerBullseye
  Placement = pos=(109.5,4.7,68.5) rot=(0,0,1;0rad)
  Solid = false
  Source = -> Face104
  Symmetric = false
FEATURE [Part::MultiFuse] Fusion081  label="removeToCreateScrewAndThreadedInsertHole040"
  Shapes = -> [Revolve107,Revolve108,Revolve109,Revolve110,Revolve111,Revolve112]
FEATURE [Part::MultiFuse] Fusion082  label="casePillars002"
  Shapes = -> [Revolve094,Revolve092,Revolve090,Revolve089,Revolve091,Revolve093]
FEATURE [Part::Cut] Cut037  label="casePillars003"
  Base = -> Fusion082
  Tool = -> Fusion081
FEATURE [Sketcher::SketchObject] Sketch051
  FullyConstrained = true
  Placement = pos=(117,19,0) rot=(0.57735,0.57735,0.57735;2.0944rad)
  sketch-geometry (48):
    g0: LineSegment StartX=-49.19 StartY=69.25 StartZ=0 EndX=-49.19 EndY=66.25 EndZ=0
    g1: LineSegment StartX=-49.19 StartY=63.5 StartZ=0 EndX=-49.19 EndY=60.5 EndZ=0
    g2: LineSegment StartX=-49.19 StartY=57.75 StartZ=0 EndX=-49.19 EndY=54.75 EndZ=0
    g3: LineSegment StartX=-49.19 StartY=52 StartZ=0 EndX=-49.19 EndY=49 EndZ=0
    g4: LineSegment StartX=-49.19 StartY=46.25 StartZ=0 EndX=-49.19 EndY=43.25 EndZ=0
    g5: LineSegment StartX=-49.19 StartY=40.5 StartZ=0 EndX=-49.19 EndY=37.5 EndZ=0
    g6: LineSegment StartX=-49.19 StartY=34.5 StartZ=0 EndX=-49.19 EndY=31.5 EndZ=0
    g7: LineSegment StartX=-49.19 StartY=28.75 StartZ=0 EndX=-49.19 EndY=25.75 EndZ=0
    g8: LineSegment StartX=-49.19 StartY=23 StartZ=0 EndX=-49.19 EndY=20 EndZ=0
    g9: LineSegment StartX=-49.19 StartY=17.25 StartZ=0 EndX=-49.19 EndY=14.25 EndZ=0
    g10: LineSegment StartX=-49.19 StartY=11.5 StartZ=0 EndX=-49.19 EndY=8.5 EndZ=0
    g11: LineSegment StartX=-49.19 StartY=5.75 StartZ=0 EndX=-49.19 EndY=2.75 EndZ=0
    g12: ArcOfCircle CenterX=-1.5 CenterY=67.75 CenterZ=0 NormalX=0 NormalY=0 NormalZ=1 AngleXU=0 Radius=1.5 StartAngle=4.71239 EndAngle=7.85398
    g13: ArcOfCircle CenterX=-1.5 CenterY=62 CenterZ=0 NormalX=0 NormalY=0 NormalZ=1 AngleXU=0 Radius=1.5 StartAngle=4.71239 EndAngle=7.85398
    g14: ArcOfCircle CenterX=-1.5 CenterY=56.25 CenterZ=0 NormalX=0 NormalY=0 NormalZ=1 AngleXU=0 Radius=1.5 StartAngle=4.71239 EndAngle=7.85398
    g15: ArcOfCircle CenterX=-11.49 CenterY=50.5 CenterZ=0 NormalX=0 NormalY=0 NormalZ=1 AngleXU=0 Radius=1.5 StartAngle=4.71239 EndAngle=7.85398
    g16: ArcOfCircle CenterX=-16.28 CenterY=44.75 CenterZ=0 NormalX=0 NormalY=0 NormalZ=1 AngleXU=0 Radius=1.5 StartAngle=4.71239 EndAngle=7.85398
    g17: ArcOfCircle CenterX=-18.2337 CenterY=39 CenterZ=0 NormalX=0 NormalY=0 NormalZ=1 AngleXU=0 Radius=1.5 StartAngle=4.71485 EndAngle=7.85398
    g18: ArcOfCircle CenterX=-16.2837 CenterY=27.25 CenterZ=0 NormalX=0 NormalY=0 NormalZ=1 AngleXU=0 Radius=1.5 StartAngle=4.71485 EndAngle=7.85398
    g19: ArcOfCircle CenterX=-18.2337 CenterY=33 CenterZ=0 NormalX=0 NormalY=0 NormalZ=1 AngleXU=0 Radius=1.5 StartAngle=4.71485 EndAngle=7.85398
    g20: ArcOfCircle CenterX=-11.49 CenterY=21.5 CenterZ=0 NormalX=0 NormalY=0 NormalZ=1 AngleXU=0 Radius=1.5 StartAngle=4.71239 EndAngle=7.85398
    g21: ArcOfCircle CenterX=-1.5 CenterY=4.25 CenterZ=0 NormalX=0 NormalY=0 NormalZ=1 AngleXU=0 Radius=1.5 StartAngle=4.71239 EndAngle=7.85398
    g22: ArcOfCircle CenterX=-1.5 CenterY=10 CenterZ=0 NormalX=0 NormalY=0 NormalZ=1 AngleXU=0 Radius=1.5 StartAngle=4.71239 EndAngle=7.85398
    g23: ArcOfCircle CenterX=-1.5 CenterY=15.75 CenterZ=0 NormalX=0 NormalY=0 NormalZ=1 AngleXU=0 Radius=1.5 StartAngle=4.71239 EndAngle=7.85398
    g24: LineSegment StartX=-49.19 StartY=69.25 StartZ=0 EndX=-1.5 EndY=69.25 EndZ=0
    g25: LineSegment StartX=-49.19 StartY=66.25 StartZ=0 EndX=-1.5 EndY=66.25 EndZ=0
    g26: LineSegment StartX=-49.19 StartY=63.5 StartZ=0 EndX=-1.5 EndY=63.5 EndZ=0
    g27: LineSegment StartX=-49.19 StartY=60.5 StartZ=0 EndX=-1.5 EndY=60.5 EndZ=0
    g28: LineSegment StartX=-49.19 StartY=57.75 StartZ=0 EndX=-1.5 EndY=57.75 EndZ=0
    g29: LineSegment StartX=-49.19 StartY=54.75 StartZ=0 EndX=-1.5 EndY=54.75 EndZ=0
    g30: LineSegment StartX=-49.19 StartY=52 StartZ=0 EndX=-11.49 EndY=52 EndZ=0
    g31: LineSegment StartX=-49.19 StartY=49 StartZ=0 EndX=-11.49 EndY=49 EndZ=0
    g32: LineSegment StartX=-49.19 StartY=46.25 StartZ=0 EndX=-16.28 EndY=46.25 EndZ=0
    g33: LineSegment StartX=-49.19 StartY=43.25 StartZ=0 EndX=-16.28 EndY=43.25 EndZ=0
    g34: LineSegment StartX=-49.19 StartY=40.5 StartZ=0 EndX=-18.2337 EndY=40.5 EndZ=0
    g35: LineSegment StartX=-49.19 StartY=37.5 StartZ=0 EndX=-18.23 EndY=37.5 EndZ=0
    g36: LineSegment StartX=-49.19 StartY=34.5 StartZ=0 EndX=-18.2337 EndY=34.5 EndZ=0
    g37: LineSegment StartX=-49.19 StartY=31.5 StartZ=0 EndX=-18.23 EndY=31.5 EndZ=0
    g38: LineSegment StartX=-49.19 StartY=28.75 StartZ=0 EndX=-16.2837 EndY=28.75 EndZ=0
    g39: LineSegment StartX=-49.19 StartY=25.75 StartZ=0 EndX=-16.28 EndY=25.75 EndZ=0
    g40: LineSegment StartX=-49.19 StartY=23 StartZ=0 EndX=-11.49 EndY=23 EndZ=0
    g41: LineSegment StartX=-49.19 StartY=20 StartZ=0 EndX=-11.49 EndY=20 EndZ=0
    g42: LineSegment StartX=-49.19 StartY=17.25 StartZ=0 EndX=-1.5 EndY=17.25 EndZ=0
    g43: LineSegment StartX=-49.19 StartY=14.25 StartZ=0 EndX=-1.5 EndY=14.25 EndZ=0
    g44: LineSegment StartX=-49.19 StartY=11.5 StartZ=0 EndX=-1.5 EndY=11.5 EndZ=0
    g45: LineSegment StartX=-49.19 StartY=8.5 StartZ=0 EndX=-1.5 EndY=8.5 EndZ=0
    g46: LineSegment StartX=-49.19 StartY=5.75 StartZ=0 EndX=-1.5 EndY=5.75 EndZ=0
    g47: LineSegment StartX=-49.19 StartY=2.75 StartZ=0 EndX=-1.5 EndY=2.75 EndZ=0
  constraints (120):
    c: Vertical(g0)
    c: Distance(g0) = 3
    c: Block(g0)
    c: Vertical(g1)
    c: Distance(g1) = 3
    c: Vertical(g2)
    c: Equal(g0,g2) = 3
    c: Block(g2)
    c: Vertical(g3)
    c: Equal(g1,g3) = 3
    c: Vertical(g4)
    c: Equal(g0,g4) = 3
    c: Block(g4)
    c: Vertical(g5)
    c: Equal(g1,g5) = 3
    c: Vertical(g6)
    c: Equal(g0,g6) = 3
    c: Block(g6)
    c: Vertical(g7)
    c: Equal(g1,g7) = 3
    c: Vertical(g8)
    c: Equal(g0,g8) = 3
    c: Block(g8)
    c: Vertical(g9)
    c: Equal(g1,g9) = 3
    c: Vertical(g10)
    c: Equal(g0,g10) = 3
    c: Block(g10)
    c: Vertical(g11)
    c: Equal(g1,g11) = 3
    c: Block(g12)
    c: Block(g13)
    c: Block(g14)
    c: Block(g15)
    c: Block(g16)
    c: Block(g17)
    c: Block(g18)
    c: Block(g19)
    c: Block(g20)
    c: Block(g21)
    c: Block(g22)
    c: Block(g23)
    c: Block(g11)
    c: Block(g9)
    c: Block(g7)
    c: Block(g5)
    c: Block(g3)
    c: Block(g1)
    c: Coincident(g24,g0)
    c: Coincident(g24,g12)
    c: Horizontal(g24)
    c: Coincident(g25,g0)
    c: Coincident(g25,g12)
    c: Horizontal(g25)
    c: Coincident(g26,g1)
    c: Coincident(g26,g13)
    c: Horizontal(g26)
    c: Coincident(g27,g1)
    c: Coincident(g27,g13)
    c: Horizontal(g27)
    c: Coincident(g28,g2)
    c: Coincident(g28,g14)
    c: Horizontal(g28)
    c: Coincident(g29,g2)
    c: Coincident(g29,g14)
    c: Horizontal(g29)
    c: Coincident(g30,g3)
    c: Coincident(g30,g15)
    c: Horizontal(g30)
    c: Coincident(g31,g3)
    c: Coincident(g31,g15)
    c: Horizontal(g31)
    c: Coincident(g32,g4)
    c: Coincident(g32,g16)
    c: Horizontal(g32)
    c: Coincident(g33,g4)
    c: Coincident(g33,g16)
    c: Horizontal(g33)
    c: Coincident(g34,g5)
    c: Coincident(g34,g17)
    c: Horizontal(g34)
    c: Coincident(g35,g5)
    c: Coincident(g35,g17)
    c: Horizontal(g35)
    c: Coincident(g36,g6)
    c: Coincident(g36,g19)
    c: Horizontal(g36)
    c: Coincident(g37,g6)
    c: Coincident(g37,g19)
    c: Horizontal(g37)
    c: Coincident(g38,g7)
    c: Coincident(g38,g18)
    c: Horizontal(g38)
    c: Coincident(g39,g7)
    c: Coincident(g39,g18)
    c: Horizontal(g39)
    c: Coincident(g40,g8)
    c: Coincident(g40,g20)
    c: Horizontal(g40)
    c: Coincident(g41,g8)
    c: Coincident(g41,g20)
    c: Horizontal(g41)
    c: Coincident(g42,g9)
    c: Coincident(g42,g23)
    c: Horizontal(g42)
    c: Coincident(g43,g9)
    c: Coincident(g43,g23)
    c: Horizontal(g43)
    c: Coincident(g44,g10)
    c: Coincident(g44,g22)
    c: Horizontal(g44)
    c: Coincident(g45,g10)
    c: Coincident(g45,g22)
    c: Horizontal(g45)
    c: Coincident(g46,g11)
    c: Coincident(g46,g21)
    c: Horizontal(g46)
    c: Coincident(g47,g11)
    c: Coincident(g47,g21)
    c: Horizontal(g47)
FEATURE [Part::Extrusion] Extrude042
  Base = -> Sketch051
  Dir = (1,-2e-16,2e-16)
  DirMode = 2
  FaceMakerClass = Part::FaceMakerBullseye
  LengthFwd = 19
  LengthRev = 0
  Placement = pos=(-19,0,0) rot=(0,0,1;0rad)
  Solid = true
  Symmetric = false
FEATURE [Part::Fillet] Fillet035  label="removeToCreateVentalationHoles"
  Base = -> Extrude042
  Edges = <same value as first occurrence — deduplicated (x6 in doc)>
  Placement = pos=(7,0,0) rot=(0,0,1;0rad)
FEATURE [Part::Cut] Cut038  label="top017"
  Base = -> Cut033
  Tool = -> Fillet035
FEATURE [Sketcher::SketchObject] Sketch052  label="bottomSketch001"
  FullyConstrained = true
  sketch-geometry (45):
    g0: LineSegment StartX=6.29999 StartY=8 StartZ=0 EndX=3.29999 EndY=8 EndZ=0
    g1: LineSegment StartX=3.29999 StartY=8 StartZ=0 EndX=3.29999 EndY=-6.03275e-07 EndZ=0
    g2: ArcOfCircle CenterX=8.29999 CenterY=5 CenterZ=0 NormalX=0 NormalY=0 NormalZ=1 AngleXU=0 Radius=2 StartAngle=3.14159 EndAngle=4.71239
    g3: LineSegment StartX=6.29999 StartY=8 StartZ=0 EndX=6.29999 EndY=5 EndZ=0
    g4: ArcOfCircle CenterX=105 CenterY=19 CenterZ=0 NormalX=0 NormalY=0 NormalZ=1 AngleXU=0 Radius=12.7 StartAngle=4.71239 EndAngle=5.94289
    g5-g11: Circle x7 (B-spline internal-alignment scaffolding for g12; pole/knot coordinates omitted)
    g12: BSplineCurve PolesCount=7 KnotsCount=5 Degree=3 IsPeriodic=0
    g13-g17: GeomPoint x5 (B-spline internal-alignment scaffolding for g12; pole/knot coordinates omitted)
    g18: ArcOfCircle CenterX=105 CenterY=19 CenterZ=0 NormalX=0 NormalY=0 NormalZ=1 AngleXU=0 Radius=15.7 StartAngle=5.81226 EndAngle=6.28319
    g19: BSplineCurve PolesCount=5 KnotsCount=3 Degree=3 IsPeriodic=0
    g20: LineSegment StartX=8.29999 StartY=3 StartZ=0 EndX=101.7 EndY=3 EndZ=0
    g21: LineSegment StartX=3.29999 StartY=-6.03275e-07 StartZ=0 EndX=105 EndY=-6.03275e-07 EndZ=0
    g22: LineSegment StartX=120.974 StartY=8.71251 StartZ=0 EndX=122.332 EndY=7.83778 EndZ=0
    g23: LineSegment StartX=105 StartY=-6.03274e-07 StartZ=0 EndX=113 EndY=-6.03274e-07 EndZ=0
    g24: ArcOfCircle CenterX=105 CenterY=19 CenterZ=0 NormalX=0 NormalY=0 NormalZ=1 AngleXU=0 Radius=20.6155 StartAngle=5.11091 EndAngle=5.71103
    g25: ArcOfCircle CenterX=117.7 CenterY=19 CenterZ=0 NormalX=0 NormalY=0 NormalZ=1 AngleXU=0 Radius=3 StartAngle=1.2e-15 EndAngle=2.10468
    g26: Circle CenterX=116.345 CenterY=16.3232 CenterZ=0 NormalX=0 NormalY=0 NormalZ=1 AngleXU=0 Radius=1
    g27: Circle CenterX=117.24 CenterY=15.7584 CenterZ=0 NormalX=0 NormalY=0 NormalZ=1 AngleXU=0 Radius=1
    g28: Circle CenterX=116.972 CenterY=14.7612 CenterZ=0 NormalX=0 NormalY=0 NormalZ=1 AngleXU=0 Radius=1
    g29: BSplineCurve PolesCount=3 KnotsCount=2 Degree=2 IsPeriodic=0
    g30: GeomPoint X=116.345 Y=16.3232 Z=0
    g31: GeomPoint X=116.972 Y=14.7612 Z=0
    g32: Circle CenterX=115.828 CenterY=17.157 CenterZ=0 NormalX=0 NormalY=0 NormalZ=1 AngleXU=0 Radius=1
    g33: Circle CenterX=115.841 CenterY=16.639 CenterZ=0 NormalX=0 NormalY=0 NormalZ=1 AngleXU=0 Radius=1
    g34: Circle CenterX=116.345 CenterY=16.3232 CenterZ=0 NormalX=0 NormalY=0 NormalZ=1 AngleXU=0 Radius=1
    g35: BSplineCurve PolesCount=3 KnotsCount=2 Degree=2 IsPeriodic=0
    g36: GeomPoint X=115.828 Y=17.157 Z=0
    g37: GeomPoint X=116.345 Y=16.3232 Z=0
    g38: LineSegment StartX=115.828 StartY=17.157 StartZ=0 EndX=115.828 EndY=20.8307 EndZ=0
    g39: Circle CenterX=115.828 CenterY=20.8307 CenterZ=0 NormalX=0 NormalY=0 NormalZ=1 AngleXU=0 Radius=1
    g40: Circle CenterX=115.831 CenterY=21.3396 CenterZ=0 NormalX=0 NormalY=0 NormalZ=1 AngleXU=0 Radius=1
    g41: Circle CenterX=116.173 CenterY=21.5825 CenterZ=0 NormalX=0 NormalY=0 NormalZ=1 AngleXU=0 Radius=1
    g42: BSplineCurve PolesCount=3 KnotsCount=2 Degree=2 IsPeriodic=0
    g43: GeomPoint X=115.828 Y=20.8307 Z=0
    g44: GeomPoint X=116.173 Y=21.5825 Z=0
  constraints (70):
    c: Horizontal(g0)
    c: Distance(g0) = 3
    c: Coincident(g1,g0)
    c: Vertical(g1)
    c: Block(g2)
    c: Block(g0)
    c: Coincident(g3,g0)
    c: Coincident(g3,g2)
    c: Vertical(g3)
    c: Block(g1)
    c: Block(g4)
    c: Coincident(g19,g4)
    c: Block(g19)
    c: Equal(g5, g6-g11) x6
    c: InternalAlignment(g5-g11 -> g12) x7
    c: InternalAlignment(g13-g17 -> g12) x5
    c: Block(g12)
    c: Coincident(g18,g12)
    c: Block(g18)
    c: Coincident(g20,g2)
    c: Coincident(g20,g19)
    c: Horizontal(g20)
    c: Distance(g20) = 93.4
    c: Coincident(g21,g1)
    c: Horizontal(g21)
    c: Distance(g21) = 101.7
    c: Horizontal(g23)
    c: Distance(g23) = 8
    c: Coincident(g24,g23)
    c: Block(g23)
    c: Coincident(g22,g24)
    c: Block(g24)
    c: Block(g22)
    c: Distance(g22) = 1.61553
    c: Coincident(g25,g18)
    c: Block(g25)
    c: Weight(g26) = 1
    c: Equal(g26,g27)
    c: Equal(g26,g28)
    c: Coincident(g29,g4)
    c: InternalAlignment(g26,g29)
    c: InternalAlignment(g27,g29)
    c: InternalAlignment(g28,g29)
    c: InternalAlignment(g30,g29)
    c: InternalAlignment(g31,g29)
    c: Block(g29)
    c: Weight(g32) = 1
    c: Equal(g32,g33)
    c: Equal(g32,g34)
    c: Coincident(g35,g29)
    c: InternalAlignment(g32,g35)
    c: InternalAlignment(g33,g35)
    c: InternalAlignment(g34,g35)
    c: InternalAlignment(g36,g35)
    c: InternalAlignment(g37,g35)
    c: Block(g35)
    c: Coincident(g38,g35)
    c: Vertical(g38)
    c: Block(g38)
    c: Coincident(g42,g38)
    c: Weight(g39) = 1
    c: Equal(g39,g40)
    c: Equal(g39,g41)
    c: Coincident(g42,g25)
    c: InternalAlignment(g39,g42)
    c: InternalAlignment(g40,g42)
    c: InternalAlignment(g41,g42)
    c: InternalAlignment(g43,g42)
    c: InternalAlignment(g44,g42)
    c: Block(g42)
FEATURE [Part::Extrusion] Extrude043  label="bottom010"
  Base = -> Sketch052
  Dir = (0,0,1)
  DirMode = 2
  FaceMakerClass = Part::FaceMakerBullseye
  LengthFwd = 71.4
  LengthRev = 0
  Placement = pos=(0,0,0.3) rot=(0,0,1;0rad)
  Solid = true
  Symmetric = false
FEATURE [Sketcher::SketchObject] Sketch053  label="topSketch013"
  FullyConstrained = true
  sketch-geometry (22):
    g0: LineSegment StartX=5.21097e-06 StartY=3 StartZ=0 EndX=5.21097e-06 EndY=19 EndZ=0
    g1: ArcOfCircle CenterX=19 CenterY=19 CenterZ=0 NormalX=0 NormalY=0 NormalZ=1 AngleXU=0 Radius=19 StartAngle=1.5708 EndAngle=3.14159
    g2: ArcOfCircle CenterX=19 CenterY=19 CenterZ=0 NormalX=0 NormalY=0 NormalZ=1 AngleXU=0 Radius=16 StartAngle=1.5708 EndAngle=3.14159
    g3: LineSegment StartX=114 StartY=35 StartZ=0 EndX=19 EndY=35 EndZ=0
    g4: LineSegment StartX=5.21097e-06 StartY=3 StartZ=0 EndX=5.21097e-06 EndY=0 EndZ=0
    g5: LineSegment StartX=3 StartY=0 StartZ=0 EndX=5.21097e-06 EndY=0 EndZ=0
    g6: LineSegment StartX=3 StartY=19 StartZ=0 EndX=3 EndY=0 EndZ=0
    g7: LineSegment StartX=19 StartY=38 StartZ=0 EndX=124 EndY=38 EndZ=0
    g8: Circle CenterX=119 CenterY=35 CenterZ=0 NormalX=0 NormalY=0 NormalZ=1 AngleXU=0 Radius=1
    g9: Circle CenterX=121 CenterY=35 CenterZ=0 NormalX=0 NormalY=0 NormalZ=1 AngleXU=0 Radius=1
    g10: Circle CenterX=121 CenterY=33 CenterZ=0 NormalX=0 NormalY=0 NormalZ=1 AngleXU=0 Radius=1
    g11: BSplineCurve PolesCount=3 KnotsCount=2 Degree=2 IsPeriodic=0
    g12: GeomPoint X=119 Y=35 Z=0
    g13: GeomPoint X=121 Y=33 Z=0
    g14: LineSegment StartX=119 StartY=35 StartZ=0 EndX=114 EndY=35 EndZ=0
    g15: ArcOfCircle CenterX=105 CenterY=19 CenterZ=0 NormalX=0 NormalY=0 NormalZ=1 AngleXU=0 Radius=16 StartAngle=5.60905 EndAngle=6.28319
    g16: LineSegment StartX=121 StartY=33 StartZ=0 EndX=121 EndY=19 EndZ=0
    g17: LineSegment StartX=117.5 StartY=9.01251 StartZ=0 EndX=121.163 EndY=9.0125 EndZ=0
    g18: ArcOfCircle CenterX=105 CenterY=19 CenterZ=0 NormalX=0 NormalY=0 NormalZ=1 AngleXU=0 Radius=20.6155 StartAngle=5.7297 EndAngle=6.28319
    g19: LineSegment StartX=121.163 StartY=9.0125 StartZ=0 EndX=122.538 EndY=8.16329 EndZ=0
    g20: LineSegment StartX=124 StartY=38 StartZ=0 EndX=125.616 EndY=38 EndZ=0
    g21: LineSegment StartX=125.616 StartY=19 StartZ=0 EndX=125.616 EndY=38 EndZ=0
  constraints (50):
    c: Vertical(g0)
    c: Block(g0)
    c: Coincident(g1,g0)
    c: Block(g1)
    c: Coincident(g2,g1)
    c: Block(g2)
    c: Coincident(g3,g2)
    c: Horizontal(g3)
    c: Tangent(g3,g2)
    c: Coincident(g4,g0)
    c: Distance(g4) = 3
    c: Vertical(g4)
    c: Coincident(g5,g4)
    c: Horizontal(g5)
    c: Coincident(g6,g2)
    c: Coincident(g6,g5)
    c: Vertical(g6)
    c: Horizontal(g7)
    c: Distance(g7) = 105
    c: Coincident(g7,g1)
    c: Block(g3)
    c: Weight(g8) = 1
    c: Equal(g8,g9)
    c: Equal(g8,g10)
    c: InternalAlignment(g8,g11)
    c: InternalAlignment(g9,g11)
    c: InternalAlignment(g10,g11)
    c: InternalAlignment(g12,g11)
    c: InternalAlignment(g13,g11)
    c: Block(g11)
    c: Coincident(g14,g11)
    c: Coincident(g14,g3)
    c: Horizontal(g14)
    c: Block(g15)
    c: Coincident(g16,g11)
    c: Coincident(g16,g15)
    c: Vertical(g16)
    c: Distance(g16) = 14
    c: Coincident(g17,g15)
    c: Block(g18)
    c: Coincident(g19,g18)
    c: Coincident(g20,g7)
    c: Horizontal(g20)
    c: Vertical(g21)
    c: Coincident(g20,g21)
    c: Block(g20)
    c: Block(g21)
    c: Block(g19)
    c: Block(g17)
    c: Distance(g20) = 1.61553
FEATURE [Part::Extrusion] Extrude044
  Base = -> Sketch053
  Dir = (0,0,1)
  DirMode = 2
  FaceMakerClass = Part::FaceMakerBullseye
  LengthFwd = 72
  LengthRev = 0
  Solid = true
  Symmetric = false
FEATURE [Part::Fillet] Fillet036  label="top018"
  Base = -> Extrude044
  Edges = 1 edges r=2: [Edge41]
FEATURE [Sketcher::SketchObject] Sketch054
  FullyConstrained = false
  Placement = pos=(0,0,0) rot=(1,0,0;1.5708rad)
  sketch-geometry (24):
    g0: ArcOfCircle CenterX=-4 CenterY=-10.5 CenterZ=0 NormalX=0 NormalY=0 NormalZ=1 AngleXU=0 Radius=1.5 StartAngle=6e-16 EndAngle=3.14159
    g1: ArcOfCircle CenterX=-34.2 CenterY=-10.5 CenterZ=0 NormalX=0 NormalY=0 NormalZ=1 AngleXU=0 Radius=1.5 StartAngle=0 EndAngle=3.14159
    g2: ArcOfCircle CenterX=-34.2 CenterY=-27.7 CenterZ=0 NormalX=0 NormalY=0 NormalZ=1 AngleXU=0 Radius=1.5 StartAngle=3.14159 EndAngle=6.28319
    g3: ArcOfCircle CenterX=-4 CenterY=-27.7 CenterZ=0 NormalX=0 NormalY=0 NormalZ=1 AngleXU=0 Radius=1.5 StartAngle=3.1416 EndAngle=6.28319
    g4: ArcOfCircle CenterX=-10 CenterY=-4.3 CenterZ=0 NormalX=0 NormalY=0 NormalZ=1 AngleXU=0 Radius=1.5 StartAngle=2e-16 EndAngle=3.14159
    g5: ArcOfCircle CenterX=-16.1 CenterY=-1.8 CenterZ=0 NormalX=0 NormalY=0 NormalZ=1 AngleXU=0 Radius=1.5 StartAngle=5e-16 EndAngle=3.14159
    g6: ArcOfCircle CenterX=-22.1 CenterY=-1.8 CenterZ=0 NormalX=0 NormalY=0 NormalZ=1 AngleXU=0 Radius=1.5 StartAngle=5e-16 EndAngle=3.14159
    g7: ArcOfCircle CenterX=-28.2 CenterY=-4.3 CenterZ=0 NormalX=0 NormalY=0 NormalZ=1 AngleXU=0 Radius=1.5 StartAngle=2e-16 EndAngle=3.14159
    g8: ArcOfCircle CenterX=-10 CenterY=-33.9 CenterZ=0 NormalX=0 NormalY=0 NormalZ=1 AngleXU=0 Radius=1.5 StartAngle=3.14159 EndAngle=6.28319
    g9: ArcOfCircle CenterX=-16.1 CenterY=-36.4 CenterZ=0 NormalX=0 NormalY=0 NormalZ=1 AngleXU=0 Radius=1.5 StartAngle=3.14159 EndAngle=6.28319
    g10: ArcOfCircle CenterX=-22.1 CenterY=-36.4 CenterZ=0 NormalX=0 NormalY=0 NormalZ=1 AngleXU=0 Radius=1.5 StartAngle=3.14159 EndAngle=6.28319
    g11: ArcOfCircle CenterX=-28.2 CenterY=-33.9 CenterZ=0 NormalX=0 NormalY=0 NormalZ=1 AngleXU=0 Radius=1.5 StartAngle=3.14159 EndAngle=6.28319
    g12: LineSegment StartX=-35.7 StartY=-10.5 StartZ=0 EndX=-35.7 EndY=-27.7 EndZ=0
    g13: LineSegment StartX=-32.7 StartY=-10.5 StartZ=0 EndX=-32.7 EndY=-27.7 EndZ=0
    g14: LineSegment StartX=-29.7 StartY=-33.9 StartZ=0 EndX=-29.7 EndY=-4.3 EndZ=0
    g15: LineSegment StartX=-26.7 StartY=-33.9 StartZ=0 EndX=-26.7 EndY=-4.3 EndZ=0
    g16: LineSegment StartX=-2.5 StartY=-10.5 StartZ=0 EndX=-2.5 EndY=-27.7 EndZ=0
    g17: LineSegment StartX=-8.5 StartY=-4.3 StartZ=0 EndX=-8.5 EndY=-33.9 EndZ=0
    g18: LineSegment StartX=-5.5 StartY=-10.5 StartZ=0 EndX=-5.5 EndY=-27.7 EndZ=0
    g19: LineSegment StartX=-11.5 StartY=-4.3 StartZ=0 EndX=-11.5 EndY=-33.9 EndZ=0
    g20: LineSegment StartX=-14.6 StartY=-1.8 StartZ=0 EndX=-14.6 EndY=-36.4 EndZ=0
    g21: LineSegment StartX=-17.6 StartY=-1.8 StartZ=0 EndX=-17.6 EndY=-36.4 EndZ=0
    g22: LineSegment StartX=-20.6 StartY=-36.4 StartZ=0 EndX=-20.6 EndY=-1.8 EndZ=0
    g23: LineSegment StartX=-23.6 StartY=-1.8 StartZ=0 EndX=-23.6 EndY=-36.4 EndZ=0
  constraints (48):
    c: Block(g0)
    c: Block(g1)
    c: Block(g2)
    c: Block(g3)
    c: Block(g4)
    c: Block(g5)
    c: Block(g6)
    c: Block(g7)
    c: Block(g8)
    c: Block(g9)
    c: Block(g10)
    c: Block(g11)
    c: Coincident(g12,g1)
    c: Coincident(g12,g2)
    c: Vertical(g12)
    c: Coincident(g13,g1)
    c: Coincident(g13,g2)
    c: Vertical(g13)
    c: Coincident(g14,g11)
    c: Coincident(g14,g7)
    c: Vertical(g14)
    c: Coincident(g15,g11)
    c: Coincident(g15,g7)
    c: Vertical(g15)
    c: Coincident(g16,g0)
    c: Coincident(g16,g3)
    c: Vertical(g16)
    c: Coincident(g17,g4)
    c: Coincident(g17,g8)
    c: Vertical(g17)
    c: Coincident(g18,g0)
    c: Coincident(g18,g3)
    c: Vertical(g18)
    c: Coincident(g19,g4)
    c: Coincident(g19,g8)
    c: Vertical(g19)
    c: Coincident(g20,g5)
    c: Coincident(g20,g9)
    c: Vertical(g20)
    c: Coincident(g21,g5)
    c: Coincident(g21,g9)
    c: Vertical(g21)
    c: Coincident(g22,g10)
    c: Coincident(g22,g6)
    c: Vertical(g22)
    c: Coincident(g23,g6)
    c: Coincident(g23,g10)
    c: Vertical(g23)
FEATURE [Part::Extrusion] Extrude045  label="removeToCreateFanGrillHoles003"
  Base = -> Sketch054
  Dir = (0,-1,6e-16)
  DirMode = 2
  FaceMakerClass = Part::FaceMakerBullseye
  LengthFwd = 10
  LengthRev = 0
  Placement = pos=(65.4,44,54.82) rot=(0,0,1;0rad)
  Solid = true
  Symmetric = false
FEATURE [Part::Feature] Face105 .. Face108  x4 (patterned run collapsed; names and placements below)
  shape: bbox 3.5 x 17.8 x 2e-07 mm, 1 faces, 0 solids (baked)
FEATURE [Part::Revolution] Revolve113  label="removeToCreateScrewAndThreadedInsertHole041"
  Angle = 360
  Axis = (0,1,0)
  Base = (0,0,0)
  FaceMakerClass = Part::FaceMakerBullseye
  Placement = pos=(62.3,30.3,19.7) rot=(0,0,1;0rad)
  Solid = false
  Source = -> Face105
  Symmetric = false
FEATURE [Part::Revolution] Revolve114  label="removeToCreateScrewAndThreadedInsertHole042"
  Angle = 360
  Axis = (0,1,0)
  Base = (0,0,0)
  FaceMakerClass = Part::FaceMakerBullseye
  Placement = pos=(62.3,30.3,51.7) rot=(0,0,1;0rad)
  Solid = false
  Source = -> Face106
  Symmetric = false
FEATURE [Part::Revolution] Revolve115  label="removeToCreateScrewAndThreadedInsertHole043"
  Angle = 360
  Axis = (0,1,0)
  Base = (0,0,0)
  FaceMakerClass = Part::FaceMakerBullseye
  Placement = pos=(30.3,30.3,19.7) rot=(0,0,1;0rad)
  Solid = false
  Source = -> Face107
  Symmetric = false
FEATURE [Part::Revolution] Revolve116  label="removeToCreateScrewAndThreadedInsertHole044"
  Angle = 360
  Axis = (0,1,0)
  Base = (0,0,0)
  FaceMakerClass = Part::FaceMakerBullseye
  Placement = pos=(30.3,30.3,51.7) rot=(0,0,1;0rad)
  Solid = false
  Source = -> Face108
  Symmetric = false
FEATURE [Part::MultiFuse] Fusion083  label="createThreadedInsertHolesForFan004"
  Shapes = -> [Revolve113,Revolve114,Revolve115,Revolve116]
FEATURE [Part::Box] Box024  label="removeToCreteHoleForPlugHousing026"
  AttacherType = Attacher::AttachEngine3D
  Height = 28.6
  Length = 10
  Placement = pos=(-2,0,21.7) rot=(0,0,1;0rad)
  Width = 19
FEATURE [Part::Cylinder] Cylinder038  label="removeToCreteHoleForPlugHousing027"
  Angle = 360
  AttacherType = Attacher::AttachEngine3D
  Height = 20
  Placement = pos=(-2,19,36) rot=(0,1,0;1.5708rad)
  Radius = 14.3
FEATURE [Part::MultiFuse] Fusion084  label="removeToCreteHoleForPlugHousing028"
  Shapes = -> [Box024,Cylinder038]
FEATURE [Part::Cylinder] Cylinder039
  Angle = 360
  AttacherType = Attacher::AttachEngine3D
  Height = 20
  Placement = pos=(0,0,36.15) rot=(0,0,1;0rad)
  Radius = 14.3
FEATURE [Part::Cylinder] Cylinder040
  Angle = 360
  AttacherType = Attacher::AttachEngine3D
  Height = 10
  Placement = pos=(0,0,36.15) rot=(0,0,1;0rad)
  Radius = 4
FEATURE [Part::Box] Box025  label="removeToCreteHoleForPlugHousing030"
  AttacherType = Attacher::AttachEngine3D
  Height = 28.6
  Length = 20
  Placement = pos=(106.15,0,21.7) rot=(0,0,1;0rad)
  Width = 19
FEATURE [Part::MultiFuse] Fusion086  label="removeToCreteHoleForPlugHousing031"
  Placement = pos=(70,19,36) rot=(0,1,0;1.5708rad)
  Shapes = -> [Cylinder039,Cylinder040]
FEATURE [Part::MultiFuse] Fusion085  label="removeToCreteHoleForPlugHousing029"
  Shapes = -> [Box025,Fusion086]
FEATURE [Sketcher::SketchObject] Sketch055
  FullyConstrained = true
  Placement = pos=(117,19,0) rot=(0.57735,0.57735,0.57735;2.0944rad)
  sketch-geometry (48):
    g0: LineSegment StartX=-49.19 StartY=69.25 StartZ=0 EndX=-49.19 EndY=66.25 EndZ=0
    g1: LineSegment StartX=-49.19 StartY=63.5 StartZ=0 EndX=-49.19 EndY=60.5 EndZ=0
    g2: LineSegment StartX=-49.19 StartY=57.75 StartZ=0 EndX=-49.19 EndY=54.75 EndZ=0
    g3: LineSegment StartX=-49.19 StartY=52 StartZ=0 EndX=-49.19 EndY=49 EndZ=0
    g4: LineSegment StartX=-49.19 StartY=46.25 StartZ=0 EndX=-49.19 EndY=43.25 EndZ=0
    g5: LineSegment StartX=-49.19 StartY=40.5 StartZ=0 EndX=-49.19 EndY=37.5 EndZ=0
    g6: LineSegment StartX=-49.19 StartY=34.5 StartZ=0 EndX=-49.19 EndY=31.5 EndZ=0
    g7: LineSegment StartX=-49.19 StartY=28.75 StartZ=0 EndX=-49.19 EndY=25.75 EndZ=0
    g8: LineSegment StartX=-49.19 StartY=23 StartZ=0 EndX=-49.19 EndY=20 EndZ=0
    g9: LineSegment StartX=-49.19 StartY=17.25 StartZ=0 EndX=-49.19 EndY=14.25 EndZ=0
    g10: LineSegment StartX=-49.19 StartY=11.5 StartZ=0 EndX=-49.19 EndY=8.5 EndZ=0
    g11: LineSegment StartX=-49.19 StartY=5.75 StartZ=0 EndX=-49.19 EndY=2.75 EndZ=0
    g12: ArcOfCircle CenterX=-1.5 CenterY=67.75 CenterZ=0 NormalX=0 NormalY=0 NormalZ=1 AngleXU=0 Radius=1.5 StartAngle=4.71239 EndAngle=7.85398
    g13: ArcOfCircle CenterX=-1.5 CenterY=62 CenterZ=0 NormalX=0 NormalY=0 NormalZ=1 AngleXU=0 Radius=1.5 StartAngle=4.71239 EndAngle=7.85398
    g14: ArcOfCircle CenterX=-1.5 CenterY=56.25 CenterZ=0 NormalX=0 NormalY=0 NormalZ=1 AngleXU=0 Radius=1.5 StartAngle=4.71239 EndAngle=7.85398
    g15: ArcOfCircle CenterX=-11.49 CenterY=50.5 CenterZ=0 NormalX=0 NormalY=0 NormalZ=1 AngleXU=0 Radius=1.5 StartAngle=4.71239 EndAngle=7.85398
    g16: ArcOfCircle CenterX=-16.28 CenterY=44.75 CenterZ=0 NormalX=0 NormalY=0 NormalZ=1 AngleXU=0 Radius=1.5 StartAngle=4.71239 EndAngle=7.85398
    g17: ArcOfCircle CenterX=-18.2337 CenterY=39 CenterZ=0 NormalX=0 NormalY=0 NormalZ=1 AngleXU=0 Radius=1.5 StartAngle=4.71485 EndAngle=7.85398
    g18: ArcOfCircle CenterX=-16.2837 CenterY=27.25 CenterZ=0 NormalX=0 NormalY=0 NormalZ=1 AngleXU=0 Radius=1.5 StartAngle=4.71485 EndAngle=7.85398
    g19: ArcOfCircle CenterX=-18.2337 CenterY=33 CenterZ=0 NormalX=0 NormalY=0 NormalZ=1 AngleXU=0 Radius=1.5 StartAngle=4.71485 EndAngle=7.85398
    g20: ArcOfCircle CenterX=-11.49 CenterY=21.5 CenterZ=0 NormalX=0 NormalY=0 NormalZ=1 AngleXU=0 Radius=1.5 StartAngle=4.71239 EndAngle=7.85398
    g21: ArcOfCircle CenterX=-1.5 CenterY=4.25 CenterZ=0 NormalX=0 NormalY=0 NormalZ=1 AngleXU=0 Radius=1.5 StartAngle=4.71239 EndAngle=7.85398
    g22: ArcOfCircle CenterX=-1.5 CenterY=10 CenterZ=0 NormalX=0 NormalY=0 NormalZ=1 AngleXU=0 Radius=1.5 StartAngle=4.71239 EndAngle=7.85398
    g23: ArcOfCircle CenterX=-1.5 CenterY=15.75 CenterZ=0 NormalX=0 NormalY=0 NormalZ=1 AngleXU=0 Radius=1.5 StartAngle=4.71239 EndAngle=7.85398
    g24: LineSegment StartX=-49.19 StartY=69.25 StartZ=0 EndX=-1.5 EndY=69.25 EndZ=0
    g25: LineSegment StartX=-49.19 StartY=66.25 StartZ=0 EndX=-1.5 EndY=66.25 EndZ=0
    g26: LineSegment StartX=-49.19 StartY=63.5 StartZ=0 EndX=-1.5 EndY=63.5 EndZ=0
    g27: LineSegment StartX=-49.19 StartY=60.5 StartZ=0 EndX=-1.5 EndY=60.5 EndZ=0
    g28: LineSegment StartX=-49.19 StartY=57.75 StartZ=0 EndX=-1.5 EndY=57.75 EndZ=0
    g29: LineSegment StartX=-49.19 StartY=54.75 StartZ=0 EndX=-1.5 EndY=54.75 EndZ=0
    g30: LineSegment StartX=-49.19 StartY=52 StartZ=0 EndX=-11.49 EndY=52 EndZ=0
    g31: LineSegment StartX=-49.19 StartY=49 StartZ=0 EndX=-11.49 EndY=49 EndZ=0
    g32: LineSegment StartX=-49.19 StartY=46.25 StartZ=0 EndX=-16.28 EndY=46.25 EndZ=0
    g33: LineSegment StartX=-49.19 StartY=43.25 StartZ=0 EndX=-16.28 EndY=43.25 EndZ=0
    g34: LineSegment StartX=-49.19 StartY=40.5 StartZ=0 EndX=-18.2337 EndY=40.5 EndZ=0
    g35: LineSegment StartX=-49.19 StartY=37.5 StartZ=0 EndX=-18.23 EndY=37.5 EndZ=0
    g36: LineSegment StartX=-49.19 StartY=34.5 StartZ=0 EndX=-18.2337 EndY=34.5 EndZ=0
    g37: LineSegment StartX=-49.19 StartY=31.5 StartZ=0 EndX=-18.23 EndY=31.5 EndZ=0
    g38: LineSegment StartX=-49.19 StartY=28.75 StartZ=0 EndX=-16.2837 EndY=28.75 EndZ=0
    g39: LineSegment StartX=-49.19 StartY=25.75 StartZ=0 EndX=-16.28 EndY=25.75 EndZ=0
    g40: LineSegment StartX=-49.19 StartY=23 StartZ=0 EndX=-11.49 EndY=23 EndZ=0
    g41: LineSegment StartX=-49.19 StartY=20 StartZ=0 EndX=-11.49 EndY=20 EndZ=0
    g42: LineSegment StartX=-49.19 StartY=17.25 StartZ=0 EndX=-1.5 EndY=17.25 EndZ=0
    g43: LineSegment StartX=-49.19 StartY=14.25 StartZ=0 EndX=-1.5 EndY=14.25 EndZ=0
    g44: LineSegment StartX=-49.19 StartY=11.5 StartZ=0 EndX=-1.5 EndY=11.5 EndZ=0
    g45: LineSegment StartX=-49.19 StartY=8.5 StartZ=0 EndX=-1.5 EndY=8.5 EndZ=0
    g46: LineSegment StartX=-49.19 StartY=5.75 StartZ=0 EndX=-1.5 EndY=5.75 EndZ=0
    g47: LineSegment StartX=-49.19 StartY=2.75 StartZ=0 EndX=-1.5 EndY=2.75 EndZ=0
  constraints (120):
    c: Vertical(g0)
    c: Distance(g0) = 3
    c: Block(g0)
    c: Vertical(g1)
    c: Distance(g1) = 3
    c: Vertical(g2)
    c: Equal(g0,g2) = 3
    c: Block(g2)
    c: Vertical(g3)
    c: Equal(g1,g3) = 3
    c: Vertical(g4)
    c: Equal(g0,g4) = 3
    c: Block(g4)
    c: Vertical(g5)
    c: Equal(g1,g5) = 3
    c: Vertical(g6)
    c: Equal(g0,g6) = 3
    c: Block(g6)
    c: Vertical(g7)
    c: Equal(g1,g7) = 3
    c: Vertical(g8)
    c: Equal(g0,g8) = 3
    c: Block(g8)
    c: Vertical(g9)
    c: Equal(g1,g9) = 3
    c: Vertical(g10)
    c: Equal(g0,g10) = 3
    c: Block(g10)
    c: Vertical(g11)
    c: Equal(g1,g11) = 3
    c: Block(g12)
    c: Block(g13)
    c: Block(g14)
    c: Block(g15)
    c: Block(g16)
    c: Block(g17)
    c: Block(g18)
    c: Block(g19)
    c: Block(g20)
    c: Block(g21)
    c: Block(g22)
    c: Block(g23)
    c: Block(g11)
    c: Block(g9)
    c: Block(g7)
    c: Block(g5)
    c: Block(g3)
    c: Block(g1)
    c: Coincident(g24,g0)
    c: Coincident(g24,g12)
    c: Horizontal(g24)
    c: Coincident(g25,g0)
    c: Coincident(g25,g12)
    c: Horizontal(g25)
    c: Coincident(g26,g1)
    c: Coincident(g26,g13)
    c: Horizontal(g26)
    c: Coincident(g27,g1)
    c: Coincident(g27,g13)
    c: Horizontal(g27)
    c: Coincident(g28,g2)
    c: Coincident(g28,g14)
    c: Horizontal(g28)
    c: Coincident(g29,g2)
    c: Coincident(g29,g14)
    c: Horizontal(g29)
    c: Coincident(g30,g3)
    c: Coincident(g30,g15)
    c: Horizontal(g30)
    c: Coincident(g31,g3)
    c: Coincident(g31,g15)
    c: Horizontal(g31)
    c: Coincident(g32,g4)
    c: Coincident(g32,g16)
    c: Horizontal(g32)
    c: Coincident(g33,g4)
    c: Coincident(g33,g16)
    c: Horizontal(g33)
    c: Coincident(g34,g5)
    c: Coincident(g34,g17)
    c: Horizontal(g34)
    c: Coincident(g35,g5)
    c: Coincident(g35,g17)
    c: Horizontal(g35)
    c: Coincident(g36,g6)
    c: Coincident(g36,g19)
    c: Horizontal(g36)
    c: Coincident(g37,g6)
    c: Coincident(g37,g19)
    c: Horizontal(g37)
    c: Coincident(g38,g7)
    c: Coincident(g38,g18)
    c: Horizontal(g38)
    c: Coincident(g39,g7)
    c: Coincident(g39,g18)
    c: Horizontal(g39)
    c: Coincident(g40,g8)
    c: Coincident(g40,g20)
    c: Horizontal(g40)
    c: Coincident(g41,g8)
    c: Coincident(g41,g20)
    c: Horizontal(g41)
    c: Coincident(g42,g9)
    c: Coincident(g42,g23)
    c: Horizontal(g42)
    c: Coincident(g43,g9)
    c: Coincident(g43,g23)
    c: Horizontal(g43)
    c: Coincident(g44,g10)
    c: Coincident(g44,g22)
    c: Horizontal(g44)
    c: Coincident(g45,g10)
    c: Coincident(g45,g22)
    c: Horizontal(g45)
    c: Coincident(g46,g11)
    c: Coincident(g46,g21)
    c: Horizontal(g46)
    c: Coincident(g47,g11)
    c: Coincident(g47,g21)
    c: Horizontal(g47)
FEATURE [Part::Extrusion] Extrude046
  Base = -> Sketch055
  Dir = (1,0,0)
  DirMode = 2
  FaceMakerClass = Part::FaceMakerBullseye
  LengthFwd = 23
  LengthRev = 0
  Placement = pos=(-19,0,0) rot=(0,0,1;0rad)
  Solid = true
  Symmetric = false
FEATURE [Part::Fillet] Fillet038  label="removeToCreateVentalationHoles001"
  Base = -> Extrude046
  Edges = <same value as first occurrence — deduplicated (x6 in doc)>
  Placement = pos=(7,0,0) rot=(0,0,1;0rad)
FEATURE [Sketcher::SketchObject] Sketch056  label="topSketch014"
  FullyConstrained = true
  sketch-geometry (22):
    g0: LineSegment StartX=5.21097e-06 StartY=3 StartZ=0 EndX=5.21097e-06 EndY=19 EndZ=0
    g1: ArcOfCircle CenterX=19 CenterY=19 CenterZ=0 NormalX=0 NormalY=0 NormalZ=1 AngleXU=0 Radius=19 StartAngle=1.5708 EndAngle=3.14159
    g2: ArcOfCircle CenterX=19 CenterY=19 CenterZ=0 NormalX=0 NormalY=0 NormalZ=1 AngleXU=0 Radius=16 StartAngle=1.5708 EndAngle=3.14159
    g3: LineSegment StartX=114 StartY=35 StartZ=0 EndX=19 EndY=35 EndZ=0
    g4: LineSegment StartX=5.21097e-06 StartY=3 StartZ=0 EndX=5.21097e-06 EndY=0 EndZ=0
    g5: LineSegment StartX=3 StartY=0 StartZ=0 EndX=5.21097e-06 EndY=0 EndZ=0
    g6: LineSegment StartX=3 StartY=19 StartZ=0 EndX=3 EndY=0 EndZ=0
    g7: LineSegment StartX=19 StartY=38 StartZ=0 EndX=124 EndY=38 EndZ=0
    g8: Circle CenterX=119 CenterY=35 CenterZ=0 NormalX=0 NormalY=0 NormalZ=1 AngleXU=0 Radius=1
    g9: Circle CenterX=121 CenterY=35 CenterZ=0 NormalX=0 NormalY=0 NormalZ=1 AngleXU=0 Radius=1
    g10: Circle CenterX=121 CenterY=33 CenterZ=0 NormalX=0 NormalY=0 NormalZ=1 AngleXU=0 Radius=1
    g11: BSplineCurve PolesCount=3 KnotsCount=2 Degree=2 IsPeriodic=0
    g12: GeomPoint X=119 Y=35 Z=0
    g13: GeomPoint X=121 Y=33 Z=0
    g14: LineSegment StartX=119 StartY=35 StartZ=0 EndX=114 EndY=35 EndZ=0
    g15: ArcOfCircle CenterX=105 CenterY=19 CenterZ=0 NormalX=0 NormalY=0 NormalZ=1 AngleXU=0 Radius=16 StartAngle=5.60905 EndAngle=6.28319
    g16: LineSegment StartX=121 StartY=33 StartZ=0 EndX=121 EndY=19 EndZ=0
    g17: LineSegment StartX=117.5 StartY=9.01251 StartZ=0 EndX=121.163 EndY=9.0125 EndZ=0
    g18: ArcOfCircle CenterX=105 CenterY=19 CenterZ=0 NormalX=0 NormalY=0 NormalZ=1 AngleXU=0 Radius=20.6155 StartAngle=5.7297 EndAngle=6.28319
    g19: LineSegment StartX=121.163 StartY=9.0125 StartZ=0 EndX=122.538 EndY=8.16329 EndZ=0
    g20: LineSegment StartX=124 StartY=38 StartZ=0 EndX=125.616 EndY=38 EndZ=0
    g21: LineSegment StartX=125.616 StartY=19 StartZ=0 EndX=125.616 EndY=38 EndZ=0
  constraints (49):
    c: Vertical(g0)
    c: Block(g0)
    c: Coincident(g1,g0)
    c: Block(g1)
    c: Coincident(g2,g1)
    c: Block(g2)
    c: Coincident(g3,g2)
    c: Horizontal(g3)
    c: Tangent(g3,g2)
    c: Coincident(g4,g0)
    c: Distance(g4) = 3
    c: Vertical(g4)
    c: Coincident(g5,g4)
    c: Horizontal(g5)
    c: Coincident(g6,g2)
    c: Coincident(g6,g5)
    c: Vertical(g6)
    c: Horizontal(g7)
    c: Distance(g7) = 105
    c: Coincident(g7,g1)
    c: Block(g3)
    c: Weight(g8) = 1
    c: Equal(g8,g9)
    c: Equal(g8,g10)
    c: InternalAlignment(g8,g11)
    c: InternalAlignment(g9,g11)
    c: InternalAlignment(g10,g11)
    c: InternalAlignment(g12,g11)
    c: InternalAlignment(g13,g11)
    c: Block(g11)
    c: Coincident(g14,g11)
    c: Coincident(g14,g3)
    c: Horizontal(g14)
    c: Block(g15)
    c: Coincident(g16,g11)
    c: Coincident(g16,g15)
    c: Vertical(g16)
    c: Distance(g16) = 14
    c: Coincident(g17,g15)
    c: Block(g18)
    c: Coincident(g19,g18)
    c: Coincident(g20,g7)
    c: Horizontal(g20)
    c: Vertical(g21)
    c: Coincident(g20,g21)
    c: Block(g20)
    c: Block(g21)
    c: Block(g19)
    c: Block(g17)
FEATURE [Part::Box] Box026  label="removeToCreteHoleForPlugHousing032"
  AttacherType = Attacher::AttachEngine3D
  Height = 28.6
  Length = 10
  Placement = pos=(-2,0,21.7) rot=(0,0,1;0rad)
  Width = 19
FEATURE [Part::Feature] Face109 .. Face112  x4 (patterned run collapsed; names and placements below)
  shape: bbox 3.5 x 17.8 x 2e-07 mm, 1 faces, 0 solids (baked)
FEATURE [Part::Revolution] Revolve117  label="removeToCreateScrewAndThreadedInsertHole045"
  Angle = 360
  Axis = (0,1,0)
  Base = (0,0,0)
  FaceMakerClass = Part::FaceMakerBullseye
  Placement = pos=(62.3,30.3,19.7) rot=(0,0,1;0rad)
  Solid = false
  Source = -> Face109
  Symmetric = false
FEATURE [Part::Revolution] Revolve118  label="removeToCreateScrewAndThreadedInsertHole046"
  Angle = 360
  Axis = (0,1,0)
  Base = (0,0,0)
  FaceMakerClass = Part::FaceMakerBullseye
  Placement = pos=(62.3,30.3,51.7) rot=(0,0,1;0rad)
  Solid = false
  Source = -> Face110
  Symmetric = false
FEATURE [Part::Revolution] Revolve119  label="removeToCreateScrewAndThreadedInsertHole047"
  Angle = 360
  Axis = (0,1,0)
  Base = (0,0,0)
  FaceMakerClass = Part::FaceMakerBullseye
  Placement = pos=(30.3,30.3,19.7) rot=(0,0,1;0rad)
  Solid = false
  Source = -> Face111
  Symmetric = false
FEATURE [Part::Revolution] Revolve120  label="removeToCreateScrewAndThreadedInsertHole048"
  Angle = 360
  Axis = (0,1,0)
  Base = (0,0,0)
  FaceMakerClass = Part::FaceMakerBullseye
  Placement = pos=(30.3,30.3,51.7) rot=(0,0,1;0rad)
  Solid = false
  Source = -> Face112
  Symmetric = false
FEATURE [Part::MultiFuse] Fusion087  label="createThreadedInsertHolesForFan005"
  Shapes = -> [Revolve117,Revolve118,Revolve119,Revolve120]
FEATURE [Part::Extrusion] Extrude047
  Base = -> Sketch056
  Dir = (0,0,1)
  DirMode = 2
  FaceMakerClass = Part::FaceMakerBullseye
  LengthFwd = 72
  LengthRev = 0
  Solid = true
  Symmetric = false
FEATURE [Part::Fillet] Fillet039  label="top019"
  Base = -> Extrude047
  Edges = 1 edges r=2: [Edge35]
FEATURE [Sketcher::SketchObject] Sketch057
  FullyConstrained = false
  Placement = pos=(0,0,0) rot=(1,0,0;1.5708rad)
  sketch-geometry (24):
    g0: ArcOfCircle CenterX=-4 CenterY=-10.5 CenterZ=0 NormalX=0 NormalY=0 NormalZ=1 AngleXU=0 Radius=1.5 StartAngle=6e-16 EndAngle=3.14159
    g1: ArcOfCircle CenterX=-34.2 CenterY=-10.5 CenterZ=0 NormalX=0 NormalY=0 NormalZ=1 AngleXU=0 Radius=1.5 StartAngle=0 EndAngle=3.14159
    g2: ArcOfCircle CenterX=-34.2 CenterY=-27.7 CenterZ=0 NormalX=0 NormalY=0 NormalZ=1 AngleXU=0 Radius=1.5 StartAngle=3.14159 EndAngle=6.28319
    g3: ArcOfCircle CenterX=-4 CenterY=-27.7 CenterZ=0 NormalX=0 NormalY=0 NormalZ=1 AngleXU=0 Radius=1.5 StartAngle=3.1416 EndAngle=6.28319
    g4: ArcOfCircle CenterX=-10 CenterY=-4.3 CenterZ=0 NormalX=0 NormalY=0 NormalZ=1 AngleXU=0 Radius=1.5 StartAngle=2e-16 EndAngle=3.14159
    g5: ArcOfCircle CenterX=-16.1 CenterY=-1.8 CenterZ=0 NormalX=0 NormalY=0 NormalZ=1 AngleXU=0 Radius=1.5 StartAngle=5e-16 EndAngle=3.14159
    g6: ArcOfCircle CenterX=-22.1 CenterY=-1.8 CenterZ=0 NormalX=0 NormalY=0 NormalZ=1 AngleXU=0 Radius=1.5 StartAngle=5e-16 EndAngle=3.14159
    g7: ArcOfCircle CenterX=-28.2 CenterY=-4.3 CenterZ=0 NormalX=0 NormalY=0 NormalZ=1 AngleXU=0 Radius=1.5 StartAngle=2e-16 EndAngle=3.14159
    g8: ArcOfCircle CenterX=-10 CenterY=-33.9 CenterZ=0 NormalX=0 NormalY=0 NormalZ=1 AngleXU=0 Radius=1.5 StartAngle=3.14159 EndAngle=6.28319
    g9: ArcOfCircle CenterX=-16.1 CenterY=-36.4 CenterZ=0 NormalX=0 NormalY=0 NormalZ=1 AngleXU=0 Radius=1.5 StartAngle=3.14159 EndAngle=6.28319
    g10: ArcOfCircle CenterX=-22.1 CenterY=-36.4 CenterZ=0 NormalX=0 NormalY=0 NormalZ=1 AngleXU=0 Radius=1.5 StartAngle=3.14159 EndAngle=6.28319
    g11: ArcOfCircle CenterX=-28.2 CenterY=-33.9 CenterZ=0 NormalX=0 NormalY=0 NormalZ=1 AngleXU=0 Radius=1.5 StartAngle=3.14159 EndAngle=6.28319
    g12: LineSegment StartX=-35.7 StartY=-10.5 StartZ=0 EndX=-35.7 EndY=-27.7 EndZ=0
    g13: LineSegment StartX=-32.7 StartY=-10.5 StartZ=0 EndX=-32.7 EndY=-27.7 EndZ=0
    g14: LineSegment StartX=-29.7 StartY=-33.9 StartZ=0 EndX=-29.7 EndY=-4.3 EndZ=0
    g15: LineSegment StartX=-26.7 StartY=-33.9 StartZ=0 EndX=-26.7 EndY=-4.3 EndZ=0
    g16: LineSegment StartX=-2.5 StartY=-10.5 StartZ=0 EndX=-2.5 EndY=-27.7 EndZ=0
    g17: LineSegment StartX=-8.5 StartY=-4.3 StartZ=0 EndX=-8.5 EndY=-33.9 EndZ=0
    g18: LineSegment StartX=-5.5 StartY=-10.5 StartZ=0 EndX=-5.5 EndY=-27.7 EndZ=0
    g19: LineSegment StartX=-11.5 StartY=-4.3 StartZ=0 EndX=-11.5 EndY=-33.9 EndZ=0
    g20: LineSegment StartX=-14.6 StartY=-1.8 StartZ=0 EndX=-14.6 EndY=-36.4 EndZ=0
    g21: LineSegment StartX=-17.6 StartY=-1.8 StartZ=0 EndX=-17.6 EndY=-36.4 EndZ=0
    g22: LineSegment StartX=-20.6 StartY=-36.4 StartZ=0 EndX=-20.6 EndY=-1.8 EndZ=0
    g23: LineSegment StartX=-23.6 StartY=-1.8 StartZ=0 EndX=-23.6 EndY=-36.4 EndZ=0
  constraints (48):
    c: Block(g0)
    c: Block(g1)
    c: Block(g2)
    c: Block(g3)
    c: Block(g4)
    c: Block(g5)
    c: Block(g6)
    c: Block(g7)
    c: Block(g8)
    c: Block(g9)
    c: Block(g10)
    c: Block(g11)
    c: Coincident(g12,g1)
    c: Coincident(g12,g2)
    c: Vertical(g12)
    c: Coincident(g13,g1)
    c: Coincident(g13,g2)
    c: Vertical(g13)
    c: Coincident(g14,g11)
    c: Coincident(g14,g7)
    c: Vertical(g14)
    c: Coincident(g15,g11)
    c: Coincident(g15,g7)
    c: Vertical(g15)
    c: Coincident(g16,g0)
    c: Coincident(g16,g3)
    c: Vertical(g16)
    c: Coincident(g17,g4)
    c: Coincident(g17,g8)
    c: Vertical(g17)
    c: Coincident(g18,g0)
    c: Coincident(g18,g3)
    c: Vertical(g18)
    c: Coincident(g19,g4)
    c: Coincident(g19,g8)
    c: Vertical(g19)
    c: Coincident(g20,g5)
    c: Coincident(g20,g9)
    c: Vertical(g20)
    c: Coincident(g21,g5)
    c: Coincident(g21,g9)
    c: Vertical(g21)
    c: Coincident(g22,g10)
    c: Coincident(g22,g6)
    c: Vertical(g22)
    c: Coincident(g23,g6)
    c: Coincident(g23,g10)
    c: Vertical(g23)
FEATURE [Part::Extrusion] Extrude048  label="removeToCreateFanGrillHoles004"
  Base = -> Sketch057
  Dir = (0,-1,6e-16)
  DirMode = 2
  FaceMakerClass = Part::FaceMakerBullseye
  LengthFwd = 10
  LengthRev = 0
  Placement = pos=(65.4,44,54.82) rot=(0,0,1;0rad)
  Solid = true
  Symmetric = false
FEATURE [Part::Cut] Cut040  label="top021"
  Base = -> Fillet039
  Tool = -> Extrude048
FEATURE [Part::Cylinder] Cylinder041  label="removeToCreteHoleForPlugHousing034"
  Angle = 360
  AttacherType = Attacher::AttachEngine3D
  Height = 20
  Placement = pos=(-2,19,36) rot=(0,1,0;1.5708rad)
  Radius = 14.3
FEATURE [Part::MultiFuse] Fusion089  label="removeToCreteHoleForPlugHousing035"
  Shapes = -> [Box026,Cylinder041]
FEATURE [Part::Cylinder] Cylinder042
  Angle = 360
  AttacherType = Attacher::AttachEngine3D
  Height = 20
  Placement = pos=(0,0,36.15) rot=(0,0,1;0rad)
  Radius = 14.3
FEATURE [Part::Cylinder] Cylinder043
  Angle = 360
  AttacherType = Attacher::AttachEngine3D
  Height = 10
  Placement = pos=(0,0,36.15) rot=(0,0,1;0rad)
  Radius = 4
FEATURE [Part::Box] Box027  label="removeToCreteHoleForPlugHousing036"
  AttacherType = Attacher::AttachEngine3D
  Height = 28.6
  Length = 20
  Placement = pos=(106.15,0,21.7) rot=(0,0,1;0rad)
  Width = 19
FEATURE [Part::Cut] Cut041  label="top022"
  Base = -> Cut040
  Tool = -> Fusion087
FEATURE [Part::Cut] Cut039  label="top020"
  Base = -> Cut041
  Tool = -> Fusion089
FEATURE [Part::MultiFuse] Fusion090  label="removeToCreteHoleForPlugHousing037"
  Placement = pos=(70,19,36) rot=(0,1,0;1.5708rad)
  Shapes = -> [Cylinder042,Cylinder043]
FEATURE [Part::MultiFuse] Fusion088  label="removeToCreteHoleForPlugHousing033"
  Shapes = -> [Box027,Fusion090]
FEATURE [Part::Cut] Cut042  label="removeToCreteHoleForPlugHousing038"
  Base = -> Cut039
  Tool = -> Fusion088
FEATURE [Part::MultiFuse] Fusion091  label="removeFromTop"
  Shapes = -> [Fillet038,Fusion085,Fusion084,Fusion083,Extrude045]
FEATURE [Part::Cut] Cut043  label="REAL TOP ====="
  Base = -> Fillet036
  Tool = -> Fusion091
FEATURE [Part::MultiFuse] Fusion092  label="caseScrewPillarBracket016"
  Shapes = -> [Extrude030,Extrude031,Extrude032,Extrude033,Extrude034,Extrude035,Extrude036,Extrude037,Box013,Box014]
FEATURE [Sketcher::SketchObject] Sketch058  label="topSketch015"
  FullyConstrained = true
  sketch-geometry (20):
    g0: LineSegment StartX=5.21097e-06 StartY=3 StartZ=0 EndX=5.21097e-06 EndY=19 EndZ=0
    g1: ArcOfCircle CenterX=19 CenterY=19 CenterZ=0 NormalX=0 NormalY=0 NormalZ=1 AngleXU=0 Radius=19 StartAngle=1.5708 EndAngle=3.14159
    g2: ArcOfCircle CenterX=19 CenterY=19 CenterZ=0 NormalX=0 NormalY=0 NormalZ=1 AngleXU=0 Radius=16 StartAngle=1.5708 EndAngle=3.14159
    g3: LineSegment StartX=114 StartY=35 StartZ=0 EndX=19 EndY=35 EndZ=0
    g4: LineSegment StartX=5.21097e-06 StartY=3 StartZ=0 EndX=5.21097e-06 EndY=0 EndZ=0
    g5: LineSegment StartX=3 StartY=0 StartZ=0 EndX=5.21097e-06 EndY=0 EndZ=0
    g6: LineSegment StartX=3 StartY=19 StartZ=0 EndX=3 EndY=0 EndZ=0
    g7: LineSegment StartX=19 StartY=38 StartZ=0 EndX=124 EndY=38 EndZ=0
    g8: Circle CenterX=119 CenterY=35 CenterZ=0 NormalX=0 NormalY=0 NormalZ=1 AngleXU=0 Radius=1
    g9: Circle CenterX=121 CenterY=35 CenterZ=0 NormalX=0 NormalY=0 NormalZ=1 AngleXU=0 Radius=1
    g10: Circle CenterX=121 CenterY=33 CenterZ=0 NormalX=0 NormalY=0 NormalZ=1 AngleXU=0 Radius=1
    g11: BSplineCurve PolesCount=3 KnotsCount=2 Degree=2 IsPeriodic=0
    g12: GeomPoint X=119 Y=35 Z=0
    g13: GeomPoint X=121 Y=33 Z=0
    g14: LineSegment StartX=119 StartY=35 StartZ=0 EndX=114 EndY=35 EndZ=0
    g15: ArcOfCircle CenterX=105 CenterY=19 CenterZ=0 NormalX=0 NormalY=0 NormalZ=1 AngleXU=0 Radius=19 StartAngle=5.7297 EndAngle=6.28319
    g16: ArcOfCircle CenterX=105 CenterY=19 CenterZ=0 NormalX=0 NormalY=0 NormalZ=1 AngleXU=0 Radius=16 StartAngle=5.60905 EndAngle=6.28319
    g17: LineSegment StartX=121 StartY=33 StartZ=0 EndX=121 EndY=19 EndZ=0
    g18: LineSegment StartX=124 StartY=38 StartZ=0 EndX=124 EndY=19 EndZ=0
    g19: LineSegment StartX=117.5 StartY=9.01251 StartZ=0 EndX=121.163 EndY=9.0125 EndZ=0
  constraints (46):
    c: Vertical(g0)
    c: Block(g0)
    c: Coincident(g1,g0)
    c: Block(g1)
    c: Coincident(g2,g1)
    c: Block(g2)
    c: Coincident(g3,g2)
    c: Horizontal(g3)
    c: Tangent(g3,g2)
    c: Coincident(g4,g0)
    c: Distance(g4) = 3
    c: Vertical(g4)
    c: Coincident(g5,g4)
    c: Horizontal(g5)
    c: Coincident(g6,g2)
    c: Coincident(g6,g5)
    c: Vertical(g6)
    c: Horizontal(g7)
    c: Distance(g7) = 105
    c: Coincident(g7,g1)
    c: Block(g3)
    c: Weight(g8) = 1
    c: Equal(g8,g9)
    c: Equal(g8,g10)
    c: InternalAlignment(g8,g11)
    c: InternalAlignment(g9,g11)
    c: InternalAlignment(g10,g11)
    c: InternalAlignment(g12,g11)
    c: InternalAlignment(g13,g11)
    c: Block(g11)
    c: Coincident(g14,g11)
    c: Coincident(g14,g3)
    c: Horizontal(g14)
    c: Block(g15)
    c: Coincident(g16,g15)
    c: Block(g16)
    c: Coincident(g17,g11)
    c: Coincident(g17,g16)
    c: Vertical(g17)
    c: Distance(g17) = 14
    c: Coincident(g18,g7)
    c: Coincident(g18,g15)
    c: Vertical(g18)
    c: Distance(g18) = 19
    c: Coincident(g19,g16)
    c: Coincident(g19,g15)
FEATURE [Part::Extrusion] Extrude049  label="top023"
  Base = -> Sketch058
  Dir = (0,0,1)
  DirMode = 2
  FaceMakerClass = Part::FaceMakerBullseye
  LengthFwd = 72
  LengthRev = 0
  Solid = true
  Symmetric = false
FEATURE [Sketcher::SketchObject] Sketch059
  FullyConstrained = true
  MapMode = 3
  Placement = pos=(0,0,0) rot=(1,0,0;1.5708rad)
  Support = -> [Extrude049]
  sketch-geometry (8):
    g0: Circle CenterX=80.351 CenterY=-67.6202 CenterZ=0 NormalX=0 NormalY=0 NormalZ=1 AngleXU=0 Radius=2
    g1: Circle CenterX=80.351 CenterY=-67.6202 CenterZ=0 NormalX=0 NormalY=0 NormalZ=1 AngleXU=0 Radius=3
    g2: Circle CenterX=80.351 CenterY=-4.92017 CenterZ=0 NormalX=0 NormalY=0 NormalZ=1 AngleXU=0 Radius=2
    g3: Circle CenterX=80.351 CenterY=-4.92017 CenterZ=0 NormalX=0 NormalY=0 NormalZ=1 AngleXU=0 Radius=3
    g4: Circle CenterX=23.851 CenterY=-4.92017 CenterZ=0 NormalX=0 NormalY=0 NormalZ=1 AngleXU=0 Radius=2
    g5: Circle CenterX=23.851 CenterY=-4.92017 CenterZ=0 NormalX=0 NormalY=0 NormalZ=1 AngleXU=0 Radius=3
    g6: Circle CenterX=23.851 CenterY=-67.6202 CenterZ=0 NormalX=0 NormalY=0 NormalZ=1 AngleXU=0 Radius=2
    g7: Circle CenterX=23.851 CenterY=-67.6202 CenterZ=0 NormalX=0 NormalY=0 NormalZ=1 AngleXU=0 Radius=3
  constraints (8):
    c: Block(g3)
    c: Block(g2)
    c: Block(g1)
    c: Block(g0)
    c: Block(g6)
    c: Block(g7)
    c: Block(g4)
    c: Block(g5)
FEATURE [Sketcher::SketchObject] Sketch060
  FullyConstrained = true
  MapMode = 3
  Placement = pos=(0,0,0) rot=(1,0,0;1.5708rad)
  Support = -> [Extrude049]
  sketch-geometry (8):
    g0: Circle CenterX=80.351 CenterY=-67.6202 CenterZ=0 NormalX=0 NormalY=0 NormalZ=1 AngleXU=0 Radius=3
    g1: Circle CenterX=80.351 CenterY=-4.92017 CenterZ=0 NormalX=0 NormalY=0 NormalZ=1 AngleXU=0 Radius=3
    g2: Circle CenterX=23.851 CenterY=-4.92017 CenterZ=0 NormalX=0 NormalY=0 NormalZ=1 AngleXU=0 Radius=3
    g3: Circle CenterX=23.851 CenterY=-67.6202 CenterZ=0 NormalX=0 NormalY=0 NormalZ=1 AngleXU=0 Radius=3
    g4: Circle CenterX=23.851 CenterY=-67.6202 CenterZ=0 NormalX=0 NormalY=0 NormalZ=1 AngleXU=0 Radius=5
    g5: Circle CenterX=80.351 CenterY=-67.6202 CenterZ=0 NormalX=0 NormalY=0 NormalZ=1 AngleXU=0 Radius=5
    g6: Circle CenterX=23.851 CenterY=-4.92017 CenterZ=0 NormalX=0 NormalY=0 NormalZ=1 AngleXU=0 Radius=5
    g7: Circle CenterX=80.351 CenterY=-4.92017 CenterZ=0 NormalX=0 NormalY=0 NormalZ=1 AngleXU=0 Radius=5
  constraints (8):
    c: Block(g1)
    c: Block(g0)
    c: Block(g3)
    c: Block(g2)
    c: Block(g5)
    c: Block(g4)
    c: Block(g6)
    c: Block(g7)
FEATURE [Sketcher::SketchObject] Sketch061
  FullyConstrained = true
  MapMode = 3
  Placement = pos=(0,0,0) rot=(1,0,0;1.5708rad)
  sketch-geometry (8):
    g0: Circle CenterX=80.351 CenterY=-67.6202 CenterZ=0 NormalX=0 NormalY=0 NormalZ=1 AngleXU=0 Radius=3
    g1: Circle CenterX=80.351 CenterY=-4.92017 CenterZ=0 NormalX=0 NormalY=0 NormalZ=1 AngleXU=0 Radius=3
    g2: Circle CenterX=23.851 CenterY=-4.92017 CenterZ=0 NormalX=0 NormalY=0 NormalZ=1 AngleXU=0 Radius=3
    g3: Circle CenterX=23.851 CenterY=-67.6202 CenterZ=0 NormalX=0 NormalY=0 NormalZ=1 AngleXU=0 Radius=3
    g4: Circle CenterX=23.851 CenterY=-67.6202 CenterZ=0 NormalX=0 NormalY=0 NormalZ=1 AngleXU=0 Radius=5
    g5: Circle CenterX=80.351 CenterY=-67.6202 CenterZ=0 NormalX=0 NormalY=0 NormalZ=1 AngleXU=0 Radius=5
    g6: Circle CenterX=23.851 CenterY=-4.92017 CenterZ=0 NormalX=0 NormalY=0 NormalZ=1 AngleXU=0 Radius=5
    g7: Circle CenterX=80.351 CenterY=-4.92017 CenterZ=0 NormalX=0 NormalY=0 NormalZ=1 AngleXU=0 Radius=5
  constraints (8):
    c: Block(g1)
    c: Block(g0)
    c: Block(g3)
    c: Block(g2)
    c: Block(g5)
    c: Block(g4)
    c: Block(g6)
    c: Block(g7)
FEATURE [Sketcher::SketchObject] Sketch062  label="topSketch016"
  FullyConstrained = true
  sketch-geometry (20):
    g0: LineSegment StartX=5.21097e-06 StartY=3 StartZ=0 EndX=5.21097e-06 EndY=19 EndZ=0
    g1: ArcOfCircle CenterX=19 CenterY=19 CenterZ=0 NormalX=0 NormalY=0 NormalZ=1 AngleXU=0 Radius=19 StartAngle=1.5708 EndAngle=3.14159
    g2: ArcOfCircle CenterX=19 CenterY=19 CenterZ=0 NormalX=0 NormalY=0 NormalZ=1 AngleXU=0 Radius=16 StartAngle=1.5708 EndAngle=3.14159
    g3: LineSegment StartX=114 StartY=35 StartZ=0 EndX=19 EndY=35 EndZ=0
    g4: LineSegment StartX=5.21097e-06 StartY=3 StartZ=0 EndX=5.21097e-06 EndY=0 EndZ=0
    g5: LineSegment StartX=3 StartY=0 StartZ=0 EndX=5.21097e-06 EndY=0 EndZ=0
    g6: LineSegment StartX=3 StartY=19 StartZ=0 EndX=3 EndY=0 EndZ=0
    g7: LineSegment StartX=19 StartY=38 StartZ=0 EndX=124 EndY=38 EndZ=0
    g8: Circle CenterX=119 CenterY=35 CenterZ=0 NormalX=0 NormalY=0 NormalZ=1 AngleXU=0 Radius=1
    g9: Circle CenterX=121 CenterY=35 CenterZ=0 NormalX=0 NormalY=0 NormalZ=1 AngleXU=0 Radius=1
    g10: Circle CenterX=121 CenterY=33 CenterZ=0 NormalX=0 NormalY=0 NormalZ=1 AngleXU=0 Radius=1
    g11: BSplineCurve PolesCount=3 KnotsCount=2 Degree=2 IsPeriodic=0
    g12: GeomPoint X=119 Y=35 Z=0
    g13: GeomPoint X=121 Y=33 Z=0
    g14: LineSegment StartX=119 StartY=35 StartZ=0 EndX=114 EndY=35 EndZ=0
    g15: ArcOfCircle CenterX=105 CenterY=19 CenterZ=0 NormalX=0 NormalY=0 NormalZ=1 AngleXU=0 Radius=19 StartAngle=5.7297 EndAngle=6.28319
    g16: ArcOfCircle CenterX=105 CenterY=19 CenterZ=0 NormalX=0 NormalY=0 NormalZ=1 AngleXU=0 Radius=16 StartAngle=5.60905 EndAngle=6.28319
    g17: LineSegment StartX=121 StartY=33 StartZ=0 EndX=121 EndY=19 EndZ=0
    g18: LineSegment StartX=124 StartY=38 StartZ=0 EndX=124 EndY=19 EndZ=0
    g19: LineSegment StartX=117.5 StartY=9.01251 StartZ=0 EndX=121.163 EndY=9.0125 EndZ=0
  constraints (46):
    c: Vertical(g0)
    c: Block(g0)
    c: Coincident(g1,g0)
    c: Block(g1)
    c: Coincident(g2,g1)
    c: Block(g2)
    c: Coincident(g3,g2)
    c: Horizontal(g3)
    c: Tangent(g3,g2)
    c: Coincident(g4,g0)
    c: Distance(g4) = 3
    c: Vertical(g4)
    c: Coincident(g5,g4)
    c: Horizontal(g5)
    c: Coincident(g6,g2)
    c: Coincident(g6,g5)
    c: Vertical(g6)
    c: Horizontal(g7)
    c: Distance(g7) = 105
    c: Coincident(g7,g1)
    c: Block(g3)
    c: Weight(g8) = 1
    c: Equal(g8,g9)
    c: Equal(g8,g10)
    c: InternalAlignment(g8,g11)
    c: InternalAlignment(g9,g11)
    c: InternalAlignment(g10,g11)
    c: InternalAlignment(g12,g11)
    c: InternalAlignment(g13,g11)
    c: Block(g11)
    c: Coincident(g14,g11)
    c: Coincident(g14,g3)
    c: Horizontal(g14)
    c: Block(g15)
    c: Coincident(g16,g15)
    c: Block(g16)
    c: Coincident(g17,g11)
    c: Coincident(g17,g16)
    c: Vertical(g17)
    c: Distance(g17) = 14
    c: Coincident(g18,g7)
    c: Coincident(g18,g15)
    c: Vertical(g18)
    c: Distance(g18) = 19
    c: Coincident(g19,g16)
    c: Coincident(g19,g15)
FEATURE [Part::Extrusion] Extrude053  label="top024"
  Base = -> Sketch062
  Dir = (0,0,1)
  DirMode = 2
  FaceMakerClass = Part::FaceMakerBullseye
  LengthFwd = 72
  LengthRev = 0
  Solid = true
  Symmetric = false
FEATURE [Sketcher::SketchObject] Sketch063
  FullyConstrained = true
  MapMode = 3
  Placement = pos=(0,0,0) rot=(1,0,0;1.5708rad)
  Support = -> [Extrude053]
  sketch-geometry (8):
    g0: Circle CenterX=80.351 CenterY=-67.6202 CenterZ=0 NormalX=0 NormalY=0 NormalZ=1 AngleXU=0 Radius=2
    g1: Circle CenterX=80.351 CenterY=-67.6202 CenterZ=0 NormalX=0 NormalY=0 NormalZ=1 AngleXU=0 Radius=3
    g2: Circle CenterX=80.351 CenterY=-4.92017 CenterZ=0 NormalX=0 NormalY=0 NormalZ=1 AngleXU=0 Radius=2
    g3: Circle CenterX=80.351 CenterY=-4.92017 CenterZ=0 NormalX=0 NormalY=0 NormalZ=1 AngleXU=0 Radius=3
    g4: Circle CenterX=23.851 CenterY=-4.92017 CenterZ=0 NormalX=0 NormalY=0 NormalZ=1 AngleXU=0 Radius=2
    g5: Circle CenterX=23.851 CenterY=-4.92017 CenterZ=0 NormalX=0 NormalY=0 NormalZ=1 AngleXU=0 Radius=3
    g6: Circle CenterX=23.851 CenterY=-67.6202 CenterZ=0 NormalX=0 NormalY=0 NormalZ=1 AngleXU=0 Radius=2
    g7: Circle CenterX=23.851 CenterY=-67.6202 CenterZ=0 NormalX=0 NormalY=0 NormalZ=1 AngleXU=0 Radius=3
  constraints (8):
    c: Block(g3)
    c: Block(g2)
    c: Block(g1)
    c: Block(g0)
    c: Block(g6)
    c: Block(g7)
    c: Block(g4)
    c: Block(g5)
FEATURE [Part::Extrusion] Extrude054
  Base = -> Sketch063
  Dir = (0,-1,2e-16)
  DirMode = 2
  FaceMakerClass = Part::FaceMakerBullseye
  LengthFwd = 6
  LengthRev = 0
  Placement = pos=(0,9,0) rot=(0,0,1;0rad)
  Solid = true
  Symmetric = false
FEATURE [Sketcher::SketchObject] Sketch064  label="topSketch017"
  FullyConstrained = true
  sketch-geometry (20):
    g0: LineSegment StartX=5.21097e-06 StartY=3 StartZ=0 EndX=5.21097e-06 EndY=19 EndZ=0
    g1: ArcOfCircle CenterX=19 CenterY=19 CenterZ=0 NormalX=0 NormalY=0 NormalZ=1 AngleXU=0 Radius=19 StartAngle=1.5708 EndAngle=3.14159
    g2: ArcOfCircle CenterX=19 CenterY=19 CenterZ=0 NormalX=0 NormalY=0 NormalZ=1 AngleXU=0 Radius=16 StartAngle=1.5708 EndAngle=3.14159
    g3: LineSegment StartX=114 StartY=35 StartZ=0 EndX=19 EndY=35 EndZ=0
    g4: LineSegment StartX=5.21097e-06 StartY=3 StartZ=0 EndX=5.21097e-06 EndY=0 EndZ=0
    g5: LineSegment StartX=3 StartY=0 StartZ=0 EndX=5.21097e-06 EndY=0 EndZ=0
    g6: LineSegment StartX=3 StartY=19 StartZ=0 EndX=3 EndY=0 EndZ=0
    g7: LineSegment StartX=19 StartY=38 StartZ=0 EndX=124 EndY=38 EndZ=0
    g8: Circle CenterX=119 CenterY=35 CenterZ=0 NormalX=0 NormalY=0 NormalZ=1 AngleXU=0 Radius=1
    g9: Circle CenterX=121 CenterY=35 CenterZ=0 NormalX=0 NormalY=0 NormalZ=1 AngleXU=0 Radius=1
    g10: Circle CenterX=121 CenterY=33 CenterZ=0 NormalX=0 NormalY=0 NormalZ=1 AngleXU=0 Radius=1
    g11: BSplineCurve PolesCount=3 KnotsCount=2 Degree=2 IsPeriodic=0
    g12: GeomPoint X=119 Y=35 Z=0
    g13: GeomPoint X=121 Y=33 Z=0
    g14: LineSegment StartX=119 StartY=35 StartZ=0 EndX=114 EndY=35 EndZ=0
    g15: ArcOfCircle CenterX=105 CenterY=19 CenterZ=0 NormalX=0 NormalY=0 NormalZ=1 AngleXU=0 Radius=19 StartAngle=5.7297 EndAngle=6.28319
    g16: ArcOfCircle CenterX=105 CenterY=19 CenterZ=0 NormalX=0 NormalY=0 NormalZ=1 AngleXU=0 Radius=16 StartAngle=5.60905 EndAngle=6.28319
    g17: LineSegment StartX=121 StartY=33 StartZ=0 EndX=121 EndY=19 EndZ=0
    g18: LineSegment StartX=124 StartY=38 StartZ=0 EndX=124 EndY=19 EndZ=0
    g19: LineSegment StartX=117.5 StartY=9.01251 StartZ=0 EndX=121.163 EndY=9.0125 EndZ=0
  constraints (46):
    c: Vertical(g0)
    c: Block(g0)
    c: Coincident(g1,g0)
    c: Block(g1)
    c: Coincident(g2,g1)
    c: Block(g2)
    c: Coincident(g3,g2)
    c: Horizontal(g3)
    c: Tangent(g3,g2)
    c: Coincident(g4,g0)
    c: Distance(g4) = 3
    c: Vertical(g4)
    c: Coincident(g5,g4)
    c: Horizontal(g5)
    c: Coincident(g6,g2)
    c: Coincident(g6,g5)
    c: Vertical(g6)
    c: Horizontal(g7)
    c: Distance(g7) = 105
    c: Coincident(g7,g1)
    c: Block(g3)
    c: Weight(g8) = 1
    c: Equal(g8,g9)
    c: Equal(g8,g10)
    c: InternalAlignment(g8,g11)
    c: InternalAlignment(g9,g11)
    c: InternalAlignment(g10,g11)
    c: InternalAlignment(g12,g11)
    c: InternalAlignment(g13,g11)
    c: Block(g11)
    c: Coincident(g14,g11)
    c: Coincident(g14,g3)
    c: Horizontal(g14)
    c: Block(g15)
    c: Coincident(g16,g15)
    c: Block(g16)
    c: Coincident(g17,g11)
    c: Coincident(g17,g16)
    c: Vertical(g17)
    c: Distance(g17) = 14
    c: Coincident(g18,g7)
    c: Coincident(g18,g15)
    c: Vertical(g18)
    c: Distance(g18) = 19
    c: Coincident(g19,g16)
    c: Coincident(g19,g15)
FEATURE [Sketcher::SketchObject] Sketch065
  FullyConstrained = true
  MapMode = 3
  Placement = pos=(0,0,0) rot=(1,0,0;1.5708rad)
  sketch-geometry (8):
    g0: Circle CenterX=80.351 CenterY=-67.6202 CenterZ=0 NormalX=0 NormalY=0 NormalZ=1 AngleXU=0 Radius=3
    g1: Circle CenterX=80.351 CenterY=-4.92017 CenterZ=0 NormalX=0 NormalY=0 NormalZ=1 AngleXU=0 Radius=3
    g2: Circle CenterX=23.851 CenterY=-4.92017 CenterZ=0 NormalX=0 NormalY=0 NormalZ=1 AngleXU=0 Radius=3
    g3: Circle CenterX=23.851 CenterY=-67.6202 CenterZ=0 NormalX=0 NormalY=0 NormalZ=1 AngleXU=0 Radius=3
    g4: Circle CenterX=23.851 CenterY=-67.6202 CenterZ=0 NormalX=0 NormalY=0 NormalZ=1 AngleXU=0 Radius=5
    g5: Circle CenterX=80.351 CenterY=-67.6202 CenterZ=0 NormalX=0 NormalY=0 NormalZ=1 AngleXU=0 Radius=5
    g6: Circle CenterX=23.851 CenterY=-4.92017 CenterZ=0 NormalX=0 NormalY=0 NormalZ=1 AngleXU=0 Radius=5
    g7: Circle CenterX=80.351 CenterY=-4.92017 CenterZ=0 NormalX=0 NormalY=0 NormalZ=1 AngleXU=0 Radius=5
  constraints (8):
    c: Block(g1)
    c: Block(g0)
    c: Block(g3)
    c: Block(g2)
    c: Block(g5)
    c: Block(g4)
    c: Block(g6)
    c: Block(g7)
FEATURE [Part::Extrusion] Extrude056
  Base = -> Sketch065
  Dir = (0,-1,2e-16)
  DirMode = 2
  FaceMakerClass = Part::FaceMakerBullseye
  LengthFwd = 2
  LengthRev = 0
  Solid = true
  Symmetric = false
FEATURE [Part::Extrusion] Extrude057  label="top025"
  Base = -> Sketch064
  Dir = (0,0,1)
  DirMode = 2
  FaceMakerClass = Part::FaceMakerBullseye
  LengthFwd = 72
  LengthRev = 0
  Solid = true
  Symmetric = false
FEATURE [Sketcher::SketchObject] Sketch066
  FullyConstrained = true
  MapMode = 3
  Placement = pos=(0,0,0) rot=(1,0,0;1.5708rad)
  Support = -> [Extrude057]
  sketch-geometry (8):
    g0: Circle CenterX=80.351 CenterY=-67.6202 CenterZ=0 NormalX=0 NormalY=0 NormalZ=1 AngleXU=0 Radius=3
    g1: Circle CenterX=80.351 CenterY=-4.92017 CenterZ=0 NormalX=0 NormalY=0 NormalZ=1 AngleXU=0 Radius=3
    g2: Circle CenterX=23.851 CenterY=-4.92017 CenterZ=0 NormalX=0 NormalY=0 NormalZ=1 AngleXU=0 Radius=3
    g3: Circle CenterX=23.851 CenterY=-67.6202 CenterZ=0 NormalX=0 NormalY=0 NormalZ=1 AngleXU=0 Radius=3
    g4: Circle CenterX=23.851 CenterY=-67.6202 CenterZ=0 NormalX=0 NormalY=0 NormalZ=1 AngleXU=0 Radius=5
    g5: Circle CenterX=80.351 CenterY=-67.6202 CenterZ=0 NormalX=0 NormalY=0 NormalZ=1 AngleXU=0 Radius=5
    g6: Circle CenterX=23.851 CenterY=-4.92017 CenterZ=0 NormalX=0 NormalY=0 NormalZ=1 AngleXU=0 Radius=5
    g7: Circle CenterX=80.351 CenterY=-4.92017 CenterZ=0 NormalX=0 NormalY=0 NormalZ=1 AngleXU=0 Radius=5
  constraints (8):
    c: Block(g1)
    c: Block(g0)
    c: Block(g3)
    c: Block(g2)
    c: Block(g5)
    c: Block(g4)
    c: Block(g6)
    c: Block(g7)
FEATURE [Part::Extrusion] Extrude055
  Base = -> Sketch066
  Dir = (0,-1,2e-16)
  DirMode = 2
  FaceMakerClass = Part::FaceMakerBullseye
  LengthFwd = 2
  LengthRev = 0
  Solid = true
  Symmetric = false
FEATURE [Part::Fillet] Fillet041
  Base = -> Extrude056
  Edges = 4 edges r=1.99: [Edge6,Edge12,Edge18,Edge24]
FEATURE [Part::Cut] Cut045
  Base = -> Extrude055
  Placement = pos=(0,6,0) rot=(0,0,1;0rad)
  Tool = -> Fillet041
FEATURE [Part::MultiFuse] Fusion095  label="pcbScrewPillars"
  Placement = pos=(-3.2,-1,72.3) rot=(0,0,1;0rad)
  Shapes = -> [Cut045,Extrude054]
FEATURE [Part::Feature] Face113
  shape: bbox 3.2 x 1.5 x 2e-07 mm, 1 faces, 0 solids (baked)
FEATURE [Part::Revolution] Revolve121  label="backCaseScrewRetainer002"
  Angle = 360
  Axis = (0,1,0)
  Base = (0,0,0)
  FaceMakerClass = Part::FaceMakerBullseye
  Placement = pos=(12.5,3,62) rot=(0,0,1;0rad)
  Solid = false
  Source = -> Face113
  Symmetric = false
FEATURE [Part::Feature] Face114
  shape: bbox 3.2 x 1.5 x 2e-07 mm, 1 faces, 0 solids (baked)
FEATURE [Part::Feature] Face115
  shape: bbox 3.2 x 1.5 x 2e-07 mm, 1 faces, 0 solids (baked)
FEATURE [Part::Feature] Face116
  shape: bbox 3.2 x 1.5 x 2e-07 mm, 1 faces, 0 solids (baked)
FEATURE [Part::Revolution] Revolve122  label="frontCaseScrewRetainer004"
  Angle = 360
  Axis = (0,1,0)
  Base = (0,0,0)
  FaceMakerClass = Part::FaceMakerBullseye
  Placement = pos=(89.5,3,68.5) rot=(0,0,1;0rad)
  Solid = false
  Source = -> Face115
  Symmetric = false
FEATURE [Part::Revolution] Revolve123  label="frontCaseScrewRetainer005"
  Angle = 360
  Axis = (0,1,0)
  Base = (0,0,0)
  FaceMakerClass = Part::FaceMakerBullseye
  Placement = pos=(89.5,3,3.5) rot=(0,0,1;0rad)
  Solid = false
  Source = -> Face116
  Symmetric = false
FEATURE [Part::Revolution] Revolve124  label="backCaseScrewRetainer003"
  Angle = 360
  Axis = (0,1,0)
  Base = (0,0,0)
  FaceMakerClass = Part::FaceMakerBullseye
  Placement = pos=(12.5,3,10) rot=(0,0,1;0rad)
  Solid = false
  Source = -> Face114
  Symmetric = false
FEATURE [Part::Feature] Face117
  shape: bbox 3.6 x 3.2 x 2e-07 mm, 1 faces, 0 solids (baked)
FEATURE [Part::Revolution] Revolve125  label="moreFrontCaseScrewRetainer004"
  Angle = 360
  Axis = (0,1,0)
  Base = (0,0,0)
  FaceMakerClass = Part::FaceMakerBullseye
  Placement = pos=(109.5,4.5,68.5) rot=(0,0,1;0rad)
  Solid = false
  Source = -> Face117
  Symmetric = false
FEATURE [Part::Feature] Face118
  shape: bbox 3.6 x 3.2 x 2e-07 mm, 1 faces, 0 solids (baked)
FEATURE [Part::Revolution] Revolve126  label="moreFrontCaseScrewRetainer005"
  Angle = 360
  Axis = (0,1,0)
  Base = (0,0,0)
  FaceMakerClass = Part::FaceMakerBullseye
  Placement = pos=(109.5,4.5,3.5) rot=(0,0,1;0rad)
  Solid = false
  Source = -> Face118
  Symmetric = false
FEATURE [Part::MultiFuse] Fusion096  label="screwRetainers001"
  Shapes = -> [Revolve126,Revolve125,Revolve124,Revolve123,Revolve122,Revolve121]
FEATURE [Part::Feature] Face119
  shape: bbox 10 x 16.5 x 2e-07 mm, 1 faces, 0 solids (baked)
FEATURE [Part::Revolution] Revolve130  label="plugHousing050"
  Angle = 360
  Axis = (0,1,0)
  Base = (0,0,0)
  FaceMakerClass = Part::FaceMakerBullseye
  Placement = pos=(0,0,36.15) rot=(0,0,1;0rad)
  Solid = false
  Source = -> Face119
  Symmetric = false
FEATURE [Part::Feature] Face120
  shape: bbox 10 x 16.5 x 2e-07 mm, 1 faces, 0 solids (baked)
FEATURE [Part::Feature] Face121
  shape: bbox 10 x 16.5 x 2e-07 mm, 1 faces, 0 solids (baked)
FEATURE [Part::Revolution] Revolve127  label="plugHousing047"
  Angle = 360
  Axis = (0,1,0)
  Base = (0,0,0)
  FaceMakerClass = Part::FaceMakerBullseye
  Placement = pos=(0,0,36.15) rot=(0,0,1;0rad)
  Solid = false
  Source = -> Face121
  Symmetric = false
FEATURE [Part::Feature] Face122
  shape: bbox 10 x 16.5 x 2e-07 mm, 1 faces, 0 solids (baked)
FEATURE [Part::Feature] Face123
  shape: bbox 10 x 16.5 x 2e-07 mm, 1 faces, 0 solids (baked)
FEATURE [Part::Revolution] Revolve128  label="plugHousing048"
  Angle = 360
  Axis = (0,1,0)
  Base = (0,0,0)
  FaceMakerClass = Part::FaceMakerBullseye
  Placement = pos=(0,0,36.15) rot=(0,0,1;0rad)
  Solid = false
  Source = -> Face123
  Symmetric = false
FEATURE [Part::MultiFuse] Fusion100  label="plugHousing054"
  Placement = pos=(0,0,0) rot=(0,0,1;1.5708rad)
  Shapes = -> [Revolve130,Revolve128]
FEATURE [Part::Feature] Face124
  shape: bbox 10 x 16.5 x 2e-07 mm, 1 faces, 0 solids (baked)
FEATURE [Part::Feature] Face125
  shape: bbox 10 x 16.5 x 2e-07 mm, 1 faces, 0 solids (baked)
FEATURE [Part::Revolution] Revolve129  label="plugHousing049"
  Angle = 360
  Axis = (0,1,0)
  Base = (0,0,0)
  FaceMakerClass = Part::FaceMakerBullseye
  Placement = pos=(0,0,36.15) rot=(0,0,1;0rad)
  Solid = false
  Source = -> Face125
  Symmetric = false
FEATURE [Part::Feature] Face126
  shape: bbox 10 x 16.5 x 2e-07 mm, 1 faces, 0 solids (baked)
FEATURE [Part::Revolution] Revolve131  label="plugHousing058"
  Angle = 360
  Axis = (0,1,0)
  Base = (0,0,0)
  FaceMakerClass = Part::FaceMakerBullseye
  Placement = pos=(0,0,36.15) rot=(0,0,1;0rad)
  Solid = false
  Source = -> Face120
  Symmetric = false
FEATURE [Part::MultiFuse] Fusion099  label="plugHousing053"
  Placement = pos=(0,0,0) rot=(0,0,1;1.5708rad)
  Shapes = -> [Revolve127,Revolve131]
FEATURE [Part::MultiFuse] Fusion102  label="plugHousing056"
  Placement = pos=(0,19,0) rot=(0,0,1;3.14159rad)
  Shapes = -> [Fusion100,Fusion099]
FEATURE [Part::Revolution] Revolve132  label="plugHousing059"
  Angle = 360
  Axis = (0,1,0)
  Base = (0,0,0)
  FaceMakerClass = Part::FaceMakerBullseye
  Placement = pos=(0,0,36.15) rot=(0,0,1;0rad)
  Solid = false
  Source = -> Face126
  Symmetric = false
FEATURE [Part::Revolution] Revolve133  label="plugHousing060"
  Angle = 360
  Axis = (0,1,0)
  Base = (0,0,0)
  FaceMakerClass = Part::FaceMakerBullseye
  Placement = pos=(0,0,36.15) rot=(0,0,1;0rad)
  Solid = false
  Source = -> Face122
  Symmetric = false
FEATURE [Part::MultiFuse] Fusion097  label="plugHousing051"
  Placement = pos=(0,0,0) rot=(0,0,1;1.5708rad)
  Shapes = -> [Revolve133,Revolve132]
FEATURE [Part::Revolution] Revolve134  label="plugHousing061"
  Angle = 360
  Axis = (0,1,0)
  Base = (0,0,0)
  FaceMakerClass = Part::FaceMakerBullseye
  Placement = pos=(0,0,36.15) rot=(0,0,1;0rad)
  Solid = false
  Source = -> Face124
  Symmetric = false
FEATURE [Part::MultiFuse] Fusion101  label="plugHousing055"
  Placement = pos=(0,0,0) rot=(0,0,1;1.5708rad)
  Shapes = -> [Revolve129,Revolve134]
FEATURE [Part::MultiFuse] Fusion098  label="plugHousing052"
  Placement = pos=(0,19,0) rot=(0,0,1;3.14159rad)
  Shapes = -> [Fusion097,Fusion101]
FEATURE [Part::MultiFuse] Fusion103  label="plugHousing057"
  Placement = pos=(122.621,0,-0.15) rot=(0,0,1;0rad)
  Shapes = -> [Fusion102,Fusion098]
FEATURE [Part::Box] Box028  label="Cube015"
  AttacherType = Attacher::AttachEngine3D
  Height = 28
  Length = 3
  Placement = pos=(110.7,19,22) rot=(0,0,1;0rad)
  Width = 15.7
FEATURE [Part::Cylinder] Cylinder044
  Angle = 360
  AttacherType = Attacher::AttachEngine3D
  Height = 20
  Placement = pos=(0,0,36.15) rot=(0,0,1;0rad)
  Radius = 10.3
FEATURE [Part::Cylinder] Cylinder045
  Angle = 360
  AttacherType = Attacher::AttachEngine3D
  Height = 10
  Placement = pos=(0,0,36.15) rot=(0,0,1;0rad)
  Radius = 4
FEATURE [Part::MultiFuse] Fusion104  label="removeToCreteHoleForPlugHousing040"
  Placement = pos=(70,19,36) rot=(0,1,0;1.5708rad)
  Shapes = -> [Cylinder044,Cylinder045]
FEATURE [Part::Cut] Cut046  label="plugHousingTab003"
  Base = -> Box028
  Tool = -> Fusion104
FEATURE [Part::MultiFuse] Fusion105  label="plugHousing062"
  Shapes = -> [Fusion103,Cut046]
FEATURE [Part::Fillet] Fillet042
  Base = -> Fusion105
  Edges = 1 edges r=2: [Edge25]
FEATURE [Part::Fillet] Fillet043  label="plugHousing063"
  Base = -> Fillet042
  Edges = 1 edges r=2: [Edge8]
  Placement = pos=(7,0,0) rot=(0,0,1;0rad)
FEATURE [Part::Feature] Face127
  shape: bbox 10 x 16.5 x 2e-07 mm, 1 faces, 0 solids (baked)
FEATURE [Part::Feature] Face128
  shape: bbox 10 x 16.5 x 2e-07 mm, 1 faces, 0 solids (baked)
FEATURE [Part::Revolution] Revolve137  label="plugHousing070"
  Angle = 360
  Axis = (0,1,0)
  Base = (0,0,0)
  FaceMakerClass = Part::FaceMakerBullseye
  Placement = pos=(0,0,36.15) rot=(0,0,1;0rad)
  Solid = false
  Source = -> Face127
  Symmetric = false
FEATURE [Part::Revolution] Revolve140  label="plugHousing073"
  Angle = 360
  Axis = (0,1,0)
  Base = (0,0,0)
  FaceMakerClass = Part::FaceMakerBullseye
  Placement = pos=(0,0,36.15) rot=(0,0,1;0rad)
  Solid = false
  Source = -> Face128
  Symmetric = false
FEATURE [Part::Feature] Face129
  shape: bbox 10 x 16.5 x 2e-07 mm, 1 faces, 0 solids (baked)
FEATURE [Part::Revolution] Revolve138  label="plugHousing071"
  Angle = 360
  Axis = (0,1,0)
  Base = (0,0,0)
  FaceMakerClass = Part::FaceMakerBullseye
  Placement = pos=(0,0,36.15) rot=(0,0,1;0rad)
  Solid = false
  Source = -> Face129
  Symmetric = false
FEATURE [Part::Feature] Face130
  shape: bbox 10 x 16.5 x 2e-07 mm, 1 faces, 0 solids (baked)
FEATURE [Part::Revolution] Revolve139  label="plugHousing072"
  Angle = 360
  Axis = (0,1,0)
  Base = (0,0,0)
  FaceMakerClass = Part::FaceMakerBullseye
  Placement = pos=(0,0,36.15) rot=(0,0,1;0rad)
  Solid = false
  Source = -> Face130
  Symmetric = false
FEATURE [Part::Feature] Face131
  shape: bbox 10 x 16.5 x 2e-07 mm, 1 faces, 0 solids (baked)
FEATURE [Part::Revolution] Revolve135  label="plugHousing068"
  Angle = 360
  Axis = (0,1,0)
  Base = (0,0,0)
  FaceMakerClass = Part::FaceMakerBullseye
  Placement = pos=(0,0,36.15) rot=(0,0,1;0rad)
  Solid = false
  Source = -> Face131
  Symmetric = false
FEATURE [Part::MultiFuse] Fusion112  label="plugHousing078"
  Placement = pos=(0,0,0) rot=(0,0,1;1.5708rad)
  Shapes = -> [Revolve135,Revolve139]
FEATURE [Part::Feature] Face132
  shape: bbox 10 x 16.5 x 2e-07 mm, 1 faces, 0 solids (baked)
FEATURE [Part::Revolution] Revolve141  label="plugHousing074"
  Angle = 360
  Axis = (0,1,0)
  Base = (0,0,0)
  FaceMakerClass = Part::FaceMakerBullseye
  Placement = pos=(0,0,36.15) rot=(0,0,1;0rad)
  Solid = false
  Source = -> Face132
  Symmetric = false
FEATURE [Part::MultiFuse] Fusion110  label="plugHousing076"
  Placement = pos=(0,0,0) rot=(0,0,1;1.5708rad)
  Shapes = -> [Revolve141,Revolve140]
FEATURE [Part::Feature] Face133
  shape: bbox 10 x 16.5 x 2e-07 mm, 1 faces, 0 solids (baked)
FEATURE [Part::Revolution] Revolve136  label="plugHousing069"
  Angle = 360
  Axis = (0,1,0)
  Base = (0,0,0)
  FaceMakerClass = Part::FaceMakerBullseye
  Placement = pos=(0,0,36.15) rot=(0,0,1;0rad)
  Solid = false
  Source = -> Face133
  Symmetric = false
FEATURE [Part::MultiFuse] Fusion106  label="plugHousing064"
  Placement = pos=(0,0,0) rot=(0,0,1;1.5708rad)
  Shapes = -> [Revolve138,Revolve136]
FEATURE [Part::MultiFuse] Fusion108  label="plugHousing066"
  Placement = pos=(0,19,0) rot=(0,0,1;3.14159rad)
  Shapes = -> [Fusion106,Fusion112]
FEATURE [Part::Feature] Face134
  shape: bbox 10 x 16.5 x 2e-07 mm, 1 faces, 0 solids (baked)
FEATURE [Part::Revolution] Revolve142  label="plugHousing075"
  Angle = 360
  Axis = (0,1,0)
  Base = (0,0,0)
  FaceMakerClass = Part::FaceMakerBullseye
  Placement = pos=(0,0,36.15) rot=(0,0,1;0rad)
  Solid = false
  Source = -> Face134
  Symmetric = false
FEATURE [Part::MultiFuse] Fusion107  label="plugHousing065"
  Placement = pos=(0,0,0) rot=(0,0,1;1.5708rad)
  Shapes = -> [Revolve137,Revolve142]
FEATURE [Part::MultiFuse] Fusion111  label="plugHousing077"
  Placement = pos=(0,19,0) rot=(0,0,1;3.14159rad)
  Shapes = -> [Fusion110,Fusion107]
FEATURE [Part::MultiFuse] Fusion109  label="plugHousing067"
  Placement = pos=(131.236,0,-0.15) rot=(0,0,1;0rad)
  Shapes = -> [Fusion108,Fusion111]
FEATURE [Part::MultiFuse] Fusion113  label="plugHousing079"
  Shapes = -> [Fillet043,Fusion109]
FEATURE [Part::Feature] Face135
  shape: bbox 3.5 x 17.8 x 2e-07 mm, 1 faces, 0 solids (baked)
FEATURE [Part::Revolution] Revolve143  label="removeToCreateScrewAndThreadedInsertHole049"
  Angle = 360
  Axis = (0,1,0)
  Base = (0,0,0)
  FaceMakerClass = Part::FaceMakerBullseye
  Placement = pos=(12.5,0,10) rot=(0,0,1;0rad)
  Solid = false
  Source = -> Face135
  Symmetric = false
FEATURE [Part::Feature] Face136
  shape: bbox 3.5 x 17.8 x 2e-07 mm, 1 faces, 0 solids (baked)
FEATURE [Part::Revolution] Revolve144  label="removeToCreateScrewAndThreadedInsertHole050"
  Angle = 360
  Axis = (0,1,0)
  Base = (0,0,0)
  FaceMakerClass = Part::FaceMakerBullseye
  Placement = pos=(12.5,0,62) rot=(0,0,1;0rad)
  Solid = false
  Source = -> Face136
  Symmetric = false
FEATURE [Part::Feature] Face137
  shape: bbox 3.5 x 17.8 x 2e-07 mm, 1 faces, 0 solids (baked)
FEATURE [Part::Revolution] Revolve145  label="removeToCreateScrewAndThreadedInsertHole051"
  Angle = 360
  Axis = (0,1,0)
  Base = (0,0,0)
  FaceMakerClass = Part::FaceMakerBullseye
  Placement = pos=(89.5,0,68.5) rot=(0,0,1;0rad)
  Solid = false
  Source = -> Face137
  Symmetric = false
FEATURE [Part::Feature] Face138
  shape: bbox 3.5 x 17.8 x 2e-07 mm, 1 faces, 0 solids (baked)
FEATURE [Part::Revolution] Revolve146  label="removeToCreateScrewAndThreadedInsertHole052"
  Angle = 360
  Axis = (0,1,0)
  Base = (0,0,0)
  FaceMakerClass = Part::FaceMakerBullseye
  Placement = pos=(89.5,0,3.5) rot=(0,0,1;0rad)
  Solid = false
  Source = -> Face138
  Symmetric = false
FEATURE [Part::Feature] Face139
  shape: bbox 3.5 x 17.8 x 2e-07 mm, 1 faces, 0 solids (baked)
FEATURE [Part::Revolution] Revolve147  label="removeToCreateScrewAndThreadedInsertHole053"
  Angle = 360
  Axis = (0,1,0)
  Base = (0,0,0)
  FaceMakerClass = Part::FaceMakerBullseye
  Placement = pos=(109.5,4.7,3.5) rot=(0,0,1;0rad)
  Solid = false
  Source = -> Face139
  Symmetric = false
FEATURE [Part::Feature] Face140
  shape: bbox 3.5 x 17.8 x 2e-07 mm, 1 faces, 0 solids (baked)
FEATURE [Part::Revolution] Revolve148  label="removeToCreateScrewAndThreadedInsertHole054"
  Angle = 360
  Axis = (0,1,0)
  Base = (0,0,0)
  FaceMakerClass = Part::FaceMakerBullseye
  Placement = pos=(109.5,4.7,68.5) rot=(0,0,1;0rad)
  Solid = false
  Source = -> Face140
  Symmetric = false
FEATURE [Part::MultiFuse] Fusion114  label="removeToCreateScrewAndThreadedInsertHole055"
  Shapes = -> [Revolve148,Revolve147,Revolve146,Revolve145,Revolve144,Revolve143]
FEATURE [Part::Cut] Cut047  label="casePillars004"
  Base = -> Cut037
  Tool = -> Fusion114
FEATURE [Part::Feature] Face141
  shape: bbox 3.5 x 17.8 x 2e-07 mm, 1 faces, 0 solids (baked)
FEATURE [Part::Feature] Face142
  shape: bbox 3.5 x 17.8 x 2e-07 mm, 1 faces, 0 solids (baked)
FEATURE [Part::Feature] Face143
  shape: bbox 3.5 x 17.8 x 2e-07 mm, 1 faces, 0 solids (baked)
FEATURE [Part::Revolution] Revolve149  label="removeToCreateScrewAndThreadedInsertHole057"
  Angle = 360
  Axis = (0,1,0)
  Base = (0,0,0)
  FaceMakerClass = Part::FaceMakerBullseye
  Placement = pos=(12.5,0,10) rot=(0,0,1;0rad)
  Solid = false
  Source = -> Face141
  Symmetric = false
FEATURE [Part::Feature] Face144
  shape: bbox 3.5 x 17.8 x 2e-07 mm, 1 faces, 0 solids (baked)
FEATURE [Part::Feature] Face145
  shape: bbox 3.5 x 17.8 x 2e-07 mm, 1 faces, 0 solids (baked)
FEATURE [Part::Feature] Face146
  shape: bbox 3.5 x 17.8 x 2e-07 mm, 1 faces, 0 solids (baked)
FEATURE [Part::Revolution] Revolve150  label="removeToCreateScrewAndThreadedInsertHole058"
  Angle = 360
  Axis = (0,1,0)
  Base = (0,0,0)
  FaceMakerClass = Part::FaceMakerBullseye
  Placement = pos=(12.5,0,62) rot=(0,0,1;0rad)
  Solid = false
  Source = -> Face146
  Symmetric = false
FEATURE [Part::Revolution] Revolve151  label="removeToCreateScrewAndThreadedInsertHole059"
  Angle = 360
  Axis = (0,1,0)
  Base = (0,0,0)
  FaceMakerClass = Part::FaceMakerBullseye
  Placement = pos=(89.5,0,68.5) rot=(0,0,1;0rad)
  Solid = false
  Source = -> Face143
  Symmetric = false
FEATURE [Part::Revolution] Revolve152  label="removeToCreateScrewAndThreadedInsertHole060"
  Angle = 360
  Axis = (0,1,0)
  Base = (0,0,0)
  FaceMakerClass = Part::FaceMakerBullseye
  Placement = pos=(89.5,0,3.5) rot=(0,0,1;0rad)
  Solid = false
  Source = -> Face142
  Symmetric = false
FEATURE [Part::Revolution] Revolve153  label="removeToCreateScrewAndThreadedInsertHole061"
  Angle = 360
  Axis = (0,1,0)
  Base = (0,0,0)
  FaceMakerClass = Part::FaceMakerBullseye
  Placement = pos=(109.5,4.7,3.5) rot=(0,0,1;0rad)
  Solid = false
  Source = -> Face145
  Symmetric = false
FEATURE [Part::Revolution] Revolve154  label="removeToCreateScrewAndThreadedInsertHole062"
  Angle = 360
  Axis = (0,1,0)
  Base = (0,0,0)
  FaceMakerClass = Part::FaceMakerBullseye
  Placement = pos=(109.5,4.7,68.5) rot=(0,0,1;0rad)
  Solid = false
  Source = -> Face144
  Symmetric = false
FEATURE [Part::MultiFuse] Fusion115  label="removeToCreateScrewAndThreadedInsertHole056"
  Shapes = -> [Revolve154,Revolve153,Revolve152,Revolve151,Revolve150,Revolve149]
FEATURE [Part::Feature] Face147
  shape: bbox 9.8 x 26.5 x 2e-07 mm, 1 faces, 0 solids (baked)
FEATURE [Part::Revolution] Revolve155
  Angle = 360
  Axis = (0,1,0)
  Base = (0,0,0)
  FaceMakerClass = Part::FaceMakerBullseye
  Placement = pos=(0,0,0) rot=(0,0,1;1.5708rad)
  Solid = false
  Source = -> Face147
  Symmetric = false
FEATURE [Part::Feature] Face148
  shape: bbox 9.8 x 26.5 x 2e-07 mm, 1 faces, 0 solids (baked)
FEATURE [Part::Revolution] Revolve156
  Angle = 360
  Axis = (0,1,0)
  Base = (0,0,0)
  FaceMakerClass = Part::FaceMakerBullseye
  Placement = pos=(0,0,0) rot=(0,0,1;1.5708rad)
  Solid = false
  Source = -> Face148
  Symmetric = false
FEATURE [Part::MultiFuse] Fusion116
  Placement = pos=(-18,19,36) rot=(0,0,1;0rad)
  Shapes = -> [Revolve156,Revolve155]
FEATURE [Part::Box] Box029  label="Cube016"
  AttacherType = Attacher::AttachEngine3D
  Height = 28
  Length = 3
  Placement = pos=(110.7,19,22) rot=(0,0,1;0rad)
  Width = 15.7
FEATURE [Part::Cylinder] Cylinder046
  Angle = 360
  AttacherType = Attacher::AttachEngine3D
  Height = 10
  Placement = pos=(0,0,36.15) rot=(0,0,1;0rad)
  Radius = 4
FEATURE [Part::Cylinder] Cylinder047
  Angle = 360
  AttacherType = Attacher::AttachEngine3D
  Height = 20
  Placement = pos=(0,0,36.15) rot=(0,0,1;0rad)
  Radius = 10.3
FEATURE [Part::MultiFuse] Fusion117  label="removeToCreteHoleForPlugHousing041"
  Placement = pos=(70,19,36) rot=(0,1,0;1.5708rad)
  Shapes = -> [Cylinder047,Cylinder046]
FEATURE [Part::Cut] Cut049  label="plugHousingTab004"
  Base = -> Box029
  Placement = pos=(-107.4,-14,0) rot=(0,0,1;0rad)
  Tool = -> Fusion117
FEATURE [Part::Box] Box030  label="Cube017"
  AttacherType = Attacher::AttachEngine3D
  Height = 28
  Length = 3
  Placement = pos=(110.7,19,22) rot=(0,0,1;0rad)
  Width = 15.7
FEATURE [Part::Cylinder] Cylinder048
  Angle = 360
  AttacherType = Attacher::AttachEngine3D
  Height = 10
  Placement = pos=(0,0,36.15) rot=(0,0,1;0rad)
  Radius = 4
FEATURE [Part::Cylinder] Cylinder049
  Angle = 360
  AttacherType = Attacher::AttachEngine3D
  Height = 20
  Placement = pos=(0,0,36.15) rot=(0,0,1;0rad)
  Radius = 10.3
FEATURE [Part::MultiFuse] Fusion118  label="removeToCreteHoleForPlugHousing042"
  Placement = pos=(70,19,36) rot=(0,1,0;1.5708rad)
  Shapes = -> [Cylinder049,Cylinder048]
FEATURE [Part::Cut] Cut050  label="plugHousingTab005"
  Base = -> Box030
  Placement = pos=(-107.4,-14,0) rot=(0,0,1;0rad)
  Tool = -> Fusion118
FEATURE [Part::MultiFuse] Fusion119
  Placement = pos=(9.6,23,0) rot=(0,0,1;3.14159rad)
  Shapes = -> [Cut049,Cut050]
FEATURE [Part::Box] Box031  label="Cube018"
  AttacherType = Attacher::AttachEngine3D
  Height = 10
  Length = 3
  Placement = pos=(3.3,4,12) rot=(0,0,1;0rad)
  Width = 10
FEATURE [Part::Fillet] Fillet044
  Base = -> Box031
  Edges = 1 edges r=2: [Edge11]
FEATURE [Part::Box] Box032  label="Cube019"
  AttacherType = Attacher::AttachEngine3D
  Height = 10
  Length = 3
  Placement = pos=(3.3,4,50) rot=(0,0,1;0rad)
  Width = 10
FEATURE [Part::Fillet] Fillet045
  Base = -> Box032
  Edges = 1 edges r=2: [Edge12]
FEATURE [Part::Box] Box033  label="Cube020"
  AttacherType = Attacher::AttachEngine3D
  Height = 28
  Length = 4
  Placement = pos=(5,0,22) rot=(0,0,1;0rad)
  Width = 10
FEATURE [Part::Fillet] Fillet046
  Base = -> Box033
  Edges = 1 edges r=1: [Edge7]
FEATURE [Part::Fillet] Fillet047
  Base = -> Fillet046
  Edges = 1 edges r=2: [Edge5]
FEATURE [Part::Fillet] Fillet048
  Base = -> Fillet047
  Edges = 1 edges r=2: [Edge2]
FEATURE [Part::Cylinder] Cylinder050
  Angle = 360
  AttacherType = Attacher::AttachEngine3D
  Height = 20
  Placement = pos=(0,0,36.15) rot=(0,0,1;0rad)
  Radius = 8.2
FEATURE [Part::Cylinder] Cylinder051
  Angle = 360
  AttacherType = Attacher::AttachEngine3D
  Height = 10
  Placement = pos=(0,0,36.15) rot=(0,0,1;0rad)
  Radius = 4
FEATURE [Part::MultiFuse] Fusion120  label="removeToCreteHoleForPlugHousing043"
  Placement = pos=(-42,19,36) rot=(0,1,0;1.5708rad)
  Shapes = -> [Cylinder050,Cylinder051]
FEATURE [Sketcher::SketchObject] Sketch067  label="topSketch018"
  FullyConstrained = true
  sketch-geometry (4):
    g0: LineSegment StartX=16.8446 StartY=31.512 StartZ=0 EndX=16.3251 EndY=34.4666 EndZ=0
    g1: ArcOfCircle CenterX=19 CenterY=19.2524 CenterZ=0 NormalX=0 NormalY=0 NormalZ=1 AngleXU=0 Radius=15.4476 StartAngle=1.74483 EndAngle=2.72717
    g2: ArcOfCircle CenterX=19 CenterY=19.2524 CenterZ=0 NormalX=0 NormalY=0 NormalZ=1 AngleXU=0 Radius=12.4476 StartAngle=1.74483 EndAngle=2.73189
    g3: LineSegment StartX=4.86004 StartY=25.4725 StartZ=0 EndX=7.58253 EndY=24.2107 EndZ=0
  constraints (7):
    c: Block(g0)
    c: Coincident(g1,g0)
    c: Coincident(g2,g0)
    c: Coincident(g3,g1)
    c: Coincident(g3,g2)
    c: Block(g1)
    c: Block(g2)
FEATURE [Part::Extrusion] Extrude058
  Base = -> Sketch067
  Dir = (0,0,1)
  DirMode = 2
  FaceMakerClass = Part::FaceMakerBullseye
  LengthFwd = 10
  LengthRev = 0
  Placement = pos=(0,0,31) rot=(0,0,1;0rad)
  Solid = true
  Symmetric = false
FEATURE [Part::Cut] Cut051
  Base = -> Extrude058
  Tool = -> Fusion120
FEATURE [Part::Fillet] Fillet049
  Base = -> Cut051
  Edges = 1 edges r=2: [Edge1]
FEATURE [Part::Fillet] Fillet050
  Base = -> Fillet049
  Edges = 1 edges r=2.5: [Edge1]
FEATURE [Part::Fillet] Fillet051
  Base = -> Fillet050
  Edges = 1 edges r=2.5: [Edge2]
FEATURE [Part::MultiFuse] Fusion121  label="wireHolder003"
  Shapes = -> [Fusion116,Fillet051]
FEATURE [Part::MultiFuse] Fusion122
  Shapes = -> [Fillet045,Fusion121]
FEATURE [Part::MultiFuse] Fusion123  label="wireHolder004"
  Shapes = -> [Fusion122,Fillet048]
FEATURE [Part::MultiFuse] Fusion124  label="wireHolder005"
  Shapes = -> [Fillet044,Fusion119,Fusion123]
FEATURE [Sketcher::SketchObject] Sketch068  label="topSketch019"
  FullyConstrained = true
  sketch-geometry (6):
    g0: LineSegment StartX=19 StartY=38 StartZ=0 EndX=117 EndY=38 EndZ=0
    g1: ArcOfCircle CenterX=19 CenterY=19 CenterZ=0 NormalX=0 NormalY=0 NormalZ=1 AngleXU=0 Radius=19 StartAngle=1.5708 EndAngle=3.14159
    g2: LineSegment StartX=117 StartY=38 StartZ=0 EndX=117 EndY=19 EndZ=0
    g3: LineSegment StartX=98 StartY=1.0161e-12 StartZ=0 EndX=5.22862e-06 EndY=1.0161e-12 EndZ=0
    g4: LineSegment StartX=5.22862e-06 StartY=19 StartZ=0 EndX=5.22862e-06 EndY=1.0161e-12 EndZ=0
    g5: ArcOfCircle CenterX=98 CenterY=19 CenterZ=0 NormalX=0 NormalY=0 NormalZ=1 AngleXU=0 Radius=19 StartAngle=4.71239 EndAngle=6.28319
  constraints (16):
    c: Horizontal(g0)
    c: Distance(g0) = 98
    c: Coincident(g1,g0)
    c: Block(g1)
    c: Coincident(g2,g0)
    c: Vertical(g2)
    c: Distance(g2) = 19
    c: Horizontal(g3)
    c: Coincident(g4,g1)
    c: Vertical(g4)
    c: Coincident(g3,g4)
    c: Block(g3)
    c: Coincident(g5,g2)
    c: Coincident(g5,g3)
    c: Block(g0)
    c: Block(g5)
FEATURE [Part::Extrusion] Extrude059  label="sideA002"
  Base = -> Sketch068
  Dir = (0,0,1)
  DirMode = 2
  FaceMakerClass = Part::FaceMakerBullseye
  LengthFwd = 3
  LengthRev = 0
  Placement = pos=(0,0,-2.7) rot=(0,0,1;0rad)
  Solid = true
  Symmetric = false
FEATURE [Sketcher::SketchObject] Sketch069  label="topSketch020"
  FullyConstrained = true
  sketch-geometry (6):
    g0: LineSegment StartX=19 StartY=38 StartZ=0 EndX=117 EndY=38 EndZ=0
    g1: ArcOfCircle CenterX=19 CenterY=19 CenterZ=0 NormalX=0 NormalY=0 NormalZ=1 AngleXU=0 Radius=19 StartAngle=1.5708 EndAngle=3.14159
    g2: LineSegment StartX=117 StartY=38 StartZ=0 EndX=117 EndY=19 EndZ=0
    g3: LineSegment StartX=98 StartY=1.0161e-12 StartZ=0 EndX=5.22862e-06 EndY=1.0161e-12 EndZ=0
    g4: LineSegment StartX=5.22862e-06 StartY=19 StartZ=0 EndX=5.22862e-06 EndY=1.0161e-12 EndZ=0
    g5: ArcOfCircle CenterX=98 CenterY=19 CenterZ=0 NormalX=0 NormalY=0 NormalZ=1 AngleXU=0 Radius=19 StartAngle=4.71239 EndAngle=6.28319
  constraints (16):
    c: Horizontal(g0)
    c: Distance(g0) = 98
    c: Coincident(g1,g0)
    c: Block(g1)
    c: Coincident(g2,g0)
    c: Vertical(g2)
    c: Distance(g2) = 19
    c: Horizontal(g3)
    c: Coincident(g4,g1)
    c: Vertical(g4)
    c: Coincident(g3,g4)
    c: Block(g3)
    c: Coincident(g5,g2)
    c: Coincident(g5,g3)
    c: Block(g0)
    c: Block(g5)
FEATURE [Part::Extrusion] Extrude060  label="sideB002"
  Base = -> Sketch069
  Dir = (0,0,1)
  DirMode = 2
  FaceMakerClass = Part::FaceMakerBullseye
  LengthFwd = 3
  LengthRev = 0
  Placement = pos=(0,0,71.7) rot=(0,0,1;0rad)
  Solid = true
  Symmetric = false
FEATURE [Part::MultiFuse] Fusion127  label="removeFromBottom001"
  Placement = pos=(2,0,0) rot=(0,0,1;0rad)
  Shapes = -> [Extrude059,Extrude060]
FEATURE [Part::Cylinder] Cylinder052
  Angle = 360
  AttacherType = Attacher::AttachEngine3D
  Height = 20
  Placement = pos=(0,0,36.15) rot=(0,0,1;0rad)
  Radius = 14
FEATURE [Part::Cylinder] Cylinder053
  Angle = 360
  AttacherType = Attacher::AttachEngine3D
  Height = 10
  Placement = pos=(0,0,36.15) rot=(0,0,1;0rad)
  Radius = 4
FEATURE [Part::MultiFuse] Fusion128  label="removeToCreteHoleForPlugHousing044"
  Placement = pos=(70,19,36) rot=(0,1,0;1.5708rad)
  Shapes = -> [Cylinder052,Cylinder053]
FEATURE [Part::Cut] Cut052  label="bottom011"
  Base = -> Extrude043
  Tool = -> Fusion128
FEATURE [Part::Cut] Cut054  label="bottom012"
  Base = -> Cut052
  Tool = -> Fusion115
FEATURE [Sketcher::SketchObject] Sketch070
  FullyConstrained = true
  Placement = pos=(117,19,0) rot=(0.57735,0.57735,0.57735;2.0944rad)
  sketch-geometry (48):
    g0: LineSegment StartX=-49.19 StartY=69.25 StartZ=0 EndX=-49.19 EndY=66.25 EndZ=0
    g1: LineSegment StartX=-49.19 StartY=63.5 StartZ=0 EndX=-49.19 EndY=60.5 EndZ=0
    g2: LineSegment StartX=-49.19 StartY=57.75 StartZ=0 EndX=-49.19 EndY=54.75 EndZ=0
    g3: LineSegment StartX=-49.19 StartY=52 StartZ=0 EndX=-49.19 EndY=49 EndZ=0
    g4: LineSegment StartX=-49.19 StartY=46.25 StartZ=0 EndX=-49.19 EndY=43.25 EndZ=0
    g5: LineSegment StartX=-49.19 StartY=40.5 StartZ=0 EndX=-49.19 EndY=37.5 EndZ=0
    g6: LineSegment StartX=-49.19 StartY=34.5 StartZ=0 EndX=-49.19 EndY=31.5 EndZ=0
    g7: LineSegment StartX=-49.19 StartY=28.75 StartZ=0 EndX=-49.19 EndY=25.75 EndZ=0
    g8: LineSegment StartX=-49.19 StartY=23 StartZ=0 EndX=-49.19 EndY=20 EndZ=0
    g9: LineSegment StartX=-49.19 StartY=17.25 StartZ=0 EndX=-49.19 EndY=14.25 EndZ=0
    g10: LineSegment StartX=-49.19 StartY=11.5 StartZ=0 EndX=-49.19 EndY=8.5 EndZ=0
    g11: LineSegment StartX=-49.19 StartY=5.75 StartZ=0 EndX=-49.19 EndY=2.75 EndZ=0
    g12: ArcOfCircle CenterX=-1.5 CenterY=67.75 CenterZ=0 NormalX=0 NormalY=0 NormalZ=1 AngleXU=0 Radius=1.5 StartAngle=4.71239 EndAngle=7.85398
    g13: ArcOfCircle CenterX=-1.5 CenterY=62 CenterZ=0 NormalX=0 NormalY=0 NormalZ=1 AngleXU=0 Radius=1.5 StartAngle=4.71239 EndAngle=7.85398
    g14: ArcOfCircle CenterX=-1.5 CenterY=56.25 CenterZ=0 NormalX=0 NormalY=0 NormalZ=1 AngleXU=0 Radius=1.5 StartAngle=4.71239 EndAngle=7.85398
    g15: ArcOfCircle CenterX=-11.49 CenterY=50.5 CenterZ=0 NormalX=0 NormalY=0 NormalZ=1 AngleXU=0 Radius=1.5 StartAngle=4.71239 EndAngle=7.85398
    g16: ArcOfCircle CenterX=-16.28 CenterY=44.75 CenterZ=0 NormalX=0 NormalY=0 NormalZ=1 AngleXU=0 Radius=1.5 StartAngle=4.71239 EndAngle=7.85398
    g17: ArcOfCircle CenterX=-18.2337 CenterY=39 CenterZ=0 NormalX=0 NormalY=0 NormalZ=1 AngleXU=0 Radius=1.5 StartAngle=4.71485 EndAngle=7.85398
    g18: ArcOfCircle CenterX=-16.2837 CenterY=27.25 CenterZ=0 NormalX=0 NormalY=0 NormalZ=1 AngleXU=0 Radius=1.5 StartAngle=4.71485 EndAngle=7.85398
    g19: ArcOfCircle CenterX=-18.2337 CenterY=33 CenterZ=0 NormalX=0 NormalY=0 NormalZ=1 AngleXU=0 Radius=1.5 StartAngle=4.71485 EndAngle=7.85398
    g20: ArcOfCircle CenterX=-11.49 CenterY=21.5 CenterZ=0 NormalX=0 NormalY=0 NormalZ=1 AngleXU=0 Radius=1.5 StartAngle=4.71239 EndAngle=7.85398
    g21: ArcOfCircle CenterX=-1.5 CenterY=4.25 CenterZ=0 NormalX=0 NormalY=0 NormalZ=1 AngleXU=0 Radius=1.5 StartAngle=4.71239 EndAngle=7.85398
    g22: ArcOfCircle CenterX=-1.5 CenterY=10 CenterZ=0 NormalX=0 NormalY=0 NormalZ=1 AngleXU=0 Radius=1.5 StartAngle=4.71239 EndAngle=7.85398
    g23: ArcOfCircle CenterX=-1.5 CenterY=15.75 CenterZ=0 NormalX=0 NormalY=0 NormalZ=1 AngleXU=0 Radius=1.5 StartAngle=4.71239 EndAngle=7.85398
    g24: LineSegment StartX=-49.19 StartY=69.25 StartZ=0 EndX=-1.5 EndY=69.25 EndZ=0
    g25: LineSegment StartX=-49.19 StartY=66.25 StartZ=0 EndX=-1.5 EndY=66.25 EndZ=0
    g26: LineSegment StartX=-49.19 StartY=63.5 StartZ=0 EndX=-1.5 EndY=63.5 EndZ=0
    g27: LineSegment StartX=-49.19 StartY=60.5 StartZ=0 EndX=-1.5 EndY=60.5 EndZ=0
    g28: LineSegment StartX=-49.19 StartY=57.75 StartZ=0 EndX=-1.5 EndY=57.75 EndZ=0
    g29: LineSegment StartX=-49.19 StartY=54.75 StartZ=0 EndX=-1.5 EndY=54.75 EndZ=0
    g30: LineSegment StartX=-49.19 StartY=52 StartZ=0 EndX=-11.49 EndY=52 EndZ=0
    g31: LineSegment StartX=-49.19 StartY=49 StartZ=0 EndX=-11.49 EndY=49 EndZ=0
    g32: LineSegment StartX=-49.19 StartY=46.25 StartZ=0 EndX=-16.28 EndY=46.25 EndZ=0
    g33: LineSegment StartX=-49.19 StartY=43.25 StartZ=0 EndX=-16.28 EndY=43.25 EndZ=0
    g34: LineSegment StartX=-49.19 StartY=40.5 StartZ=0 EndX=-18.2337 EndY=40.5 EndZ=0
    g35: LineSegment StartX=-49.19 StartY=37.5 StartZ=0 EndX=-18.23 EndY=37.5 EndZ=0
    g36: LineSegment StartX=-49.19 StartY=34.5 StartZ=0 EndX=-18.2337 EndY=34.5 EndZ=0
    g37: LineSegment StartX=-49.19 StartY=31.5 StartZ=0 EndX=-18.23 EndY=31.5 EndZ=0
    g38: LineSegment StartX=-49.19 StartY=28.75 StartZ=0 EndX=-16.2837 EndY=28.75 EndZ=0
    g39: LineSegment StartX=-49.19 StartY=25.75 StartZ=0 EndX=-16.28 EndY=25.75 EndZ=0
    g40: LineSegment StartX=-49.19 StartY=23 StartZ=0 EndX=-11.49 EndY=23 EndZ=0
    g41: LineSegment StartX=-49.19 StartY=20 StartZ=0 EndX=-11.49 EndY=20 EndZ=0
    g42: LineSegment StartX=-49.19 StartY=17.25 StartZ=0 EndX=-1.5 EndY=17.25 EndZ=0
    g43: LineSegment StartX=-49.19 StartY=14.25 StartZ=0 EndX=-1.5 EndY=14.25 EndZ=0
    g44: LineSegment StartX=-49.19 StartY=11.5 StartZ=0 EndX=-1.5 EndY=11.5 EndZ=0
    g45: LineSegment StartX=-49.19 StartY=8.5 StartZ=0 EndX=-1.5 EndY=8.5 EndZ=0
    g46: LineSegment StartX=-49.19 StartY=5.75 StartZ=0 EndX=-1.5 EndY=5.75 EndZ=0
    g47: LineSegment StartX=-49.19 StartY=2.75 StartZ=0 EndX=-1.5 EndY=2.75 EndZ=0
  constraints (120):
    c: Vertical(g0)
    c: Distance(g0) = 3
    c: Block(g0)
    c: Vertical(g1)
    c: Distance(g1) = 3
    c: Vertical(g2)
    c: Equal(g0,g2) = 3
    c: Block(g2)
    c: Vertical(g3)
    c: Equal(g1,g3) = 3
    c: Vertical(g4)
    c: Equal(g0,g4) = 3
    c: Block(g4)
    c: Vertical(g5)
    c: Equal(g1,g5) = 3
    c: Vertical(g6)
    c: Equal(g0,g6) = 3
    c: Block(g6)
    c: Vertical(g7)
    c: Equal(g1,g7) = 3
    c: Vertical(g8)
    c: Equal(g0,g8) = 3
    c: Block(g8)
    c: Vertical(g9)
    c: Equal(g1,g9) = 3
    c: Vertical(g10)
    c: Equal(g0,g10) = 3
    c: Block(g10)
    c: Vertical(g11)
    c: Equal(g1,g11) = 3
    c: Block(g12)
    c: Block(g13)
    c: Block(g14)
    c: Block(g15)
    c: Block(g16)
    c: Block(g17)
    c: Block(g18)
    c: Block(g19)
    c: Block(g20)
    c: Block(g21)
    c: Block(g22)
    c: Block(g23)
    c: Block(g11)
    c: Block(g9)
    c: Block(g7)
    c: Block(g5)
    c: Block(g3)
    c: Block(g1)
    c: Coincident(g24,g0)
    c: Coincident(g24,g12)
    c: Horizontal(g24)
    c: Coincident(g25,g0)
    c: Coincident(g25,g12)
    c: Horizontal(g25)
    c: Coincident(g26,g1)
    c: Coincident(g26,g13)
    c: Horizontal(g26)
    c: Coincident(g27,g1)
    c: Coincident(g27,g13)
    c: Horizontal(g27)
    c: Coincident(g28,g2)
    c: Coincident(g28,g14)
    c: Horizontal(g28)
    c: Coincident(g29,g2)
    c: Coincident(g29,g14)
    c: Horizontal(g29)
    c: Coincident(g30,g3)
    c: Coincident(g30,g15)
    c: Horizontal(g30)
    c: Coincident(g31,g3)
    c: Coincident(g31,g15)
    c: Horizontal(g31)
    c: Coincident(g32,g4)
    c: Coincident(g32,g16)
    c: Horizontal(g32)
    c: Coincident(g33,g4)
    c: Coincident(g33,g16)
    c: Horizontal(g33)
    c: Coincident(g34,g5)
    c: Coincident(g34,g17)
    c: Horizontal(g34)
    c: Coincident(g35,g5)
    c: Coincident(g35,g17)
    c: Horizontal(g35)
    c: Coincident(g36,g6)
    c: Coincident(g36,g19)
    c: Horizontal(g36)
    c: Coincident(g37,g6)
    c: Coincident(g37,g19)
    c: Horizontal(g37)
    c: Coincident(g38,g7)
    c: Coincident(g38,g18)
    c: Horizontal(g38)
    c: Coincident(g39,g7)
    c: Coincident(g39,g18)
    c: Horizontal(g39)
    c: Coincident(g40,g8)
    c: Coincident(g40,g20)
    c: Horizontal(g40)
    c: Coincident(g41,g8)
    c: Coincident(g41,g20)
    c: Horizontal(g41)
    c: Coincident(g42,g9)
    c: Coincident(g42,g23)
    c: Horizontal(g42)
    c: Coincident(g43,g9)
    c: Coincident(g43,g23)
    c: Horizontal(g43)
    c: Coincident(g44,g10)
    c: Coincident(g44,g22)
    c: Horizontal(g44)
    c: Coincident(g45,g10)
    c: Coincident(g45,g22)
    c: Horizontal(g45)
    c: Coincident(g46,g11)
    c: Coincident(g46,g21)
    c: Horizontal(g46)
    c: Coincident(g47,g11)
    c: Coincident(g47,g21)
    c: Horizontal(g47)
FEATURE [Part::Extrusion] Extrude061
  Base = -> Sketch070
  Dir = (1,0,0)
  DirMode = 2
  FaceMakerClass = Part::FaceMakerBullseye
  LengthFwd = 23
  LengthRev = 0
  Placement = pos=(-19,0,0) rot=(0,0,1;0rad)
  Solid = true
  Symmetric = false
FEATURE [Part::Fillet] Fillet052  label="removeToCreateVentalationHoles002"
  Base = -> Extrude061
  Edges = <same value as first occurrence — deduplicated (x6 in doc)>
  Placement = pos=(7,0.02,0) rot=(0,0,1;0rad)
FEATURE [Part::MultiFuse] Fusion130  label="bottom013"
  Shapes = -> [Cut054,Cut034]
FEATURE [Part::Cut] Cut055
  Base = -> Fusion130
  Tool = -> Fillet052
FEATURE [Part::Cylinder] Cylinder054
  Angle = 360
  AttacherType = Attacher::AttachEngine3D
  Height = 20
  Placement = pos=(0,0,36.15) rot=(0,0,1;0rad)
  Radius = 4
FEATURE [Sketcher::SketchObject] Sketch071  label="bottomSketch002"
  FullyConstrained = true
  sketch-geometry (32):
    g0: LineSegment StartX=3.3 StartY=-6.03275e-07 StartZ=0 EndX=98 EndY=-6.03275e-07 EndZ=0
    g1: ArcOfCircle CenterX=98 CenterY=19 CenterZ=0 NormalX=0 NormalY=0 NormalZ=1 AngleXU=0 Radius=19 StartAngle=4.71239 EndAngle=5.71103
    g2: LineSegment StartX=6.3 StartY=8 StartZ=0 EndX=3.3 EndY=8 EndZ=0
    g3: LineSegment StartX=3.3 StartY=8 StartZ=0 EndX=3.3 EndY=-6.03275e-07 EndZ=0
    g4: ArcOfCircle CenterX=8.3 CenterY=5 CenterZ=0 NormalX=0 NormalY=0 NormalZ=1 AngleXU=0 Radius=2 StartAngle=3.14159 EndAngle=4.71239
    g5: LineSegment StartX=6.3 StartY=8 StartZ=0 EndX=6.3 EndY=5 EndZ=0
    g6: ArcOfCircle CenterX=98 CenterY=19 CenterZ=0 NormalX=0 NormalY=0 NormalZ=1 AngleXU=0 Radius=12.7 StartAngle=4.71239 EndAngle=6.28319
    g7: LineSegment StartX=94.7 StartY=3 StartZ=0 EndX=8.3 EndY=3 EndZ=0
    g8-g12: Circle x5 (B-spline internal-alignment scaffolding for g13; pole/knot coordinates omitted)
    g13: BSplineCurve PolesCount=5 KnotsCount=3 Degree=3 IsPeriodic=0
    g14: GeomPoint X=98 Y=6.3 Z=0
    g15: GeomPoint X=96.3938 Y=4.71946 Z=0
    g16: GeomPoint X=94.7 Y=3 Z=0
    g17-g23: Circle x7 (B-spline internal-alignment scaffolding for g24; pole/knot coordinates omitted)
    g24: BSplineCurve PolesCount=7 KnotsCount=5 Degree=3 IsPeriodic=0
    g25-g29: GeomPoint x5 (B-spline internal-alignment scaffolding for g24; pole/knot coordinates omitted)
    g30: ArcOfCircle CenterX=98 CenterY=19 CenterZ=0 NormalX=0 NormalY=0 NormalZ=1 AngleXU=0 Radius=15.7 StartAngle=5.81226 EndAngle=6.28319
    g31: LineSegment StartX=110.7 StartY=19 StartZ=0 EndX=113.7 EndY=19 EndZ=0
  constraints (41):
    c: Horizontal(g0)
    c: Coincident(g1,g0)
    c: Block(g1)
    c: Horizontal(g2)
    c: Distance(g2) = 3
    c: Coincident(g3,g2)
    c: Vertical(g3)
    c: Coincident(g3,g0)
    c: Block(g4)
    c: Block(g2)
    c: Coincident(g5,g2)
    c: Coincident(g5,g4)
    c: Vertical(g5)
    c: Coincident(g6,g1)
    c: Block(g6)
    c: Coincident(g7,g4)
    c: Horizontal(g7)
    c: Block(g0)
    c: Block(g7)
    c: Block(g3)
    c: Coincident(g13,g6)
    c: Weight(g8) = 1
    c: Equal(g8, g9-g12) x4
    c: Coincident(g13,g7)
    c: InternalAlignment(g8-g12 -> g13) x5
    c: InternalAlignment(g14,g13)
    c: InternalAlignment(g15,g13)
    c: InternalAlignment(g16,g13)
    c: Block(g13)
    c: Weight(g17) = 1
    c: Equal(g17, g18-g23) x6
    c: Coincident(g24,g1)
    c: InternalAlignment(g17-g23 -> g24) x7
    c: InternalAlignment(g25-g29 -> g24) x5
    c: Block(g24)
    c: Coincident(g30,g24)
    c: Coincident(g31,g6)
    c: Coincident(g31,g30)
    c: Horizontal(g31)
    c: Block(g31)
    c: Block(g30)
FEATURE [Part::Extrusion] Extrude062  label="bottom014"
  Base = -> Sketch071
  Dir = (0,0,1)
  DirMode = 2
  FaceMakerClass = Part::FaceMakerBullseye
  LengthFwd = 71.4
  LengthRev = 0
  Placement = pos=(0,0,0.3) rot=(0,0,1;0rad)
  Solid = true
  Symmetric = false
FEATURE [Part::Fillet] Fillet054
  Base = -> Extrude062
  Edges = 1 edges r=2.4: [Edge17]
FEATURE [Part::Fillet] Fillet055  label="bottom015"
  Base = -> Fillet054
  Edges = 1 edges r=2.4: [Edge36]
FEATURE [Part::Cylinder] Cylinder055
  Angle = 360
  AttacherType = Attacher::AttachEngine3D
  Height = 10
  Placement = pos=(0,0,36.15) rot=(0,0,1;0rad)
  Radius = 4
FEATURE [Part::MultiFuse] Fusion131  label="removeToCreateHoleForPlugHousing002"
  Placement = pos=(70,19,36.15) rot=(0,1,0;1.5708rad)
  Shapes = -> [Cylinder054,Cylinder055]
FEATURE [Part::Cut] Cut056  label="Bottom001"
  Base = -> Fillet055
  Placement = pos=(9,0,0) rot=(0,0,1;0rad)
  Tool = -> Fusion131
FEATURE [Part::Cut] Cut057
  Base = -> Cut055
  Tool = -> Cut056
FEATURE [Sketcher::SketchObject] Sketch072  label="topSketch021"
  FullyConstrained = true
  sketch-geometry (4):
    g0: ArcOfCircle CenterX=105 CenterY=19 CenterZ=0 NormalX=0 NormalY=0 NormalZ=1 AngleXU=0 Radius=20.6155 StartAngle=5.54125 EndAngle=6.28319
    g1: ArcOfCircle CenterX=105 CenterY=19 CenterZ=0 NormalX=0 NormalY=0 NormalZ=1 AngleXU=0 Radius=13 StartAngle=5.54125 EndAngle=6.28319
    g2: LineSegment StartX=118 StartY=19 StartZ=0 EndX=125.616 EndY=19 EndZ=0
    g3: LineSegment StartX=114.583 StartY=10.2157 StartZ=0 EndX=120.197 EndY=5.06982 EndZ=0
  constraints (7):
    c: Block(g0)
    c: Block(g1)
    c: Coincident(g2,g1)
    c: Coincident(g2,g0)
    c: Horizontal(g2)
    c: Coincident(g3,g1)
    c: Coincident(g3,g0)
FEATURE [Part::Extrusion] Extrude063  label="bottomPlugHousingBit003"
  Base = -> Sketch072
  Dir = (0,0,1)
  DirMode = 2
  FaceMakerClass = Part::FaceMakerBullseye
  LengthFwd = 72
  LengthRev = 0
  Solid = true
  Symmetric = false
FEATURE [Part::Cylinder] Cylinder056
  Angle = 360
  AttacherType = Attacher::AttachEngine3D
  Height = 20
  Placement = pos=(0,0,36.15) rot=(0,0,1;0rad)
  Radius = 14.3
FEATURE [Part::Cylinder] Cylinder057
  Angle = 360
  AttacherType = Attacher::AttachEngine3D
  Height = 10
  Placement = pos=(0,0,36.15) rot=(0,0,1;0rad)
  Radius = 4
FEATURE [Part::Box] Box034  label="removeToCreteHoleForPlugHousing047"
  AttacherType = Attacher::AttachEngine3D
  Height = 28.6
  Length = 20
  Placement = pos=(106.15,0,21.7) rot=(0,0,1;0rad)
  Width = 19
FEATURE [Part::Cylinder] Cylinder058
  Angle = 360
  AttacherType = Attacher::AttachEngine3D
  Height = 20
  Placement = pos=(0,0,36.15) rot=(0,0,1;0rad)
  Radius = 14.3
FEATURE [Part::Cylinder] Cylinder059
  Angle = 360
  AttacherType = Attacher::AttachEngine3D
  Height = 10
  Placement = pos=(0,0,36.15) rot=(0,0,1;0rad)
  Radius = 4
FEATURE [Part::MultiFuse] Fusion134  label="removeToCreteHoleForPlugHousing046"
  Placement = pos=(70,19,36) rot=(0,1,0;1.5708rad)
  Shapes = -> [Cylinder058,Cylinder059]
FEATURE [Part::Cylinder] Cylinder060
  Angle = 360
  AttacherType = Attacher::AttachEngine3D
  Height = 20
  Placement = pos=(0,0,36.15) rot=(0,0,1;0rad)
  Radius = 14
FEATURE [Part::Cylinder] Cylinder061
  Angle = 360
  AttacherType = Attacher::AttachEngine3D
  Height = 10
  Placement = pos=(0,0,36.15) rot=(0,0,1;0rad)
  Radius = 4
FEATURE [Part::MultiFuse] Fusion135  label="removeToCreteHoleForPlugHousing048"
  Placement = pos=(70,19,36) rot=(0,1,0;1.5708rad)
  Shapes = -> [Cylinder060,Cylinder061]
FEATURE [Part::Box] Box035  label="removeToCreteHoleForPlugHousing049"
  AttacherType = Attacher::AttachEngine3D
  Height = 28.6
  Length = 20
  Placement = pos=(106.15,0,21.7) rot=(0,0,1;0rad)
  Width = 19
FEATURE [Part::MultiFuse] Fusion133  label="removeToCreteHoleForPlugHousing045"
  Placement = pos=(0,0,-28.3) rot=(0,0,1;0rad)
  Shapes = -> [Box035,Fusion134]
FEATURE [Part::MultiFuse] Fusion138  label="removeToCreteHoleForPlugHousing051"
  Placement = pos=(70,19,36) rot=(0,1,0;1.5708rad)
  Shapes = -> [Cylinder056,Cylinder057]
FEATURE [Part::MultiFuse] Fusion137  label="removeToCreteHoleForPlugHousing050"
  Placement = pos=(0,0,28.3) rot=(0,0,1;0rad)
  Shapes = -> [Box034,Fusion138]
FEATURE [Part::MultiFuse] Fusion132  label="removeToCreatePlugHousingBottomBit002"
  Shapes = -> [Fusion133,Fusion137]
FEATURE [Part::MultiFuse] Fusion136  label="removeToCreatePlugHousingBottomBit003"
  Shapes = -> [Fusion135,Fusion132]
FEATURE [Part::Cut] Cut058  label="bottomPlugHousingBit002"
  Base = -> Extrude063
  Placement = pos=(-0.09,0,0) rot=(0,0,1;0rad)
  Tool = -> Fusion136
FEATURE [Sketcher::SketchObject] Sketch073  label="bottomSketch003"
  FullyConstrained = true
  sketch-geometry (45):
    g0: LineSegment StartX=6.29999 StartY=8 StartZ=0 EndX=3.29999 EndY=8 EndZ=0
    g1: LineSegment StartX=3.29999 StartY=8 StartZ=0 EndX=3.29999 EndY=-6.03275e-07 EndZ=0
    g2: ArcOfCircle CenterX=8.29999 CenterY=5 CenterZ=0 NormalX=0 NormalY=0 NormalZ=1 AngleXU=0 Radius=2 StartAngle=3.14159 EndAngle=4.71239
    g3: LineSegment StartX=6.29999 StartY=8 StartZ=0 EndX=6.29999 EndY=5 EndZ=0
    g4: ArcOfCircle CenterX=105 CenterY=19 CenterZ=0 NormalX=0 NormalY=0 NormalZ=1 AngleXU=0 Radius=12.7 StartAngle=4.71239 EndAngle=5.94289
    g5-g11: Circle x7 (B-spline internal-alignment scaffolding for g12; pole/knot coordinates omitted)
    g12: BSplineCurve PolesCount=7 KnotsCount=5 Degree=3 IsPeriodic=0
    g13-g17: GeomPoint x5 (B-spline internal-alignment scaffolding for g12; pole/knot coordinates omitted)
    g18: ArcOfCircle CenterX=105 CenterY=19 CenterZ=0 NormalX=0 NormalY=0 NormalZ=1 AngleXU=0 Radius=15.7 StartAngle=5.81226 EndAngle=6.28319
    g19: BSplineCurve PolesCount=5 KnotsCount=3 Degree=3 IsPeriodic=0
    g20: LineSegment StartX=8.29999 StartY=3 StartZ=0 EndX=101.7 EndY=3 EndZ=0
    g21: LineSegment StartX=3.29999 StartY=-6.03275e-07 StartZ=0 EndX=105 EndY=-6.03275e-07 EndZ=0
    g22: LineSegment StartX=120.974 StartY=8.71251 StartZ=0 EndX=122.332 EndY=7.83778 EndZ=0
    g23: LineSegment StartX=105 StartY=-6.03274e-07 StartZ=0 EndX=113 EndY=-6.03274e-07 EndZ=0
    g24: ArcOfCircle CenterX=105 CenterY=19 CenterZ=0 NormalX=0 NormalY=0 NormalZ=1 AngleXU=0 Radius=20.6155 StartAngle=5.11091 EndAngle=5.71103
    g25: ArcOfCircle CenterX=117.7 CenterY=19 CenterZ=0 NormalX=0 NormalY=0 NormalZ=1 AngleXU=0 Radius=3 StartAngle=1.2e-15 EndAngle=2.10468
    g26: Circle CenterX=116.345 CenterY=16.3232 CenterZ=0 NormalX=0 NormalY=0 NormalZ=1 AngleXU=0 Radius=1
    g27: Circle CenterX=117.24 CenterY=15.7584 CenterZ=0 NormalX=0 NormalY=0 NormalZ=1 AngleXU=0 Radius=1
    g28: Circle CenterX=116.972 CenterY=14.7612 CenterZ=0 NormalX=0 NormalY=0 NormalZ=1 AngleXU=0 Radius=1
    g29: BSplineCurve PolesCount=3 KnotsCount=2 Degree=2 IsPeriodic=0
    g30: GeomPoint X=116.345 Y=16.3232 Z=0
    g31: GeomPoint X=116.972 Y=14.7612 Z=0
    g32: Circle CenterX=115.828 CenterY=17.157 CenterZ=0 NormalX=0 NormalY=0 NormalZ=1 AngleXU=0 Radius=1
    g33: Circle CenterX=115.841 CenterY=16.639 CenterZ=0 NormalX=0 NormalY=0 NormalZ=1 AngleXU=0 Radius=1
    g34: Circle CenterX=116.345 CenterY=16.3232 CenterZ=0 NormalX=0 NormalY=0 NormalZ=1 AngleXU=0 Radius=1
    g35: BSplineCurve PolesCount=3 KnotsCount=2 Degree=2 IsPeriodic=0
    g36: GeomPoint X=115.828 Y=17.157 Z=0
    g37: GeomPoint X=116.345 Y=16.3232 Z=0
    g38: LineSegment StartX=115.828 StartY=17.157 StartZ=0 EndX=115.828 EndY=20.8307 EndZ=0
    g39: Circle CenterX=115.828 CenterY=20.8307 CenterZ=0 NormalX=0 NormalY=0 NormalZ=1 AngleXU=0 Radius=1
    g40: Circle CenterX=115.831 CenterY=21.3396 CenterZ=0 NormalX=0 NormalY=0 NormalZ=1 AngleXU=0 Radius=1
    g41: Circle CenterX=116.173 CenterY=21.5825 CenterZ=0 NormalX=0 NormalY=0 NormalZ=1 AngleXU=0 Radius=1
    g42: BSplineCurve PolesCount=3 KnotsCount=2 Degree=2 IsPeriodic=0
    g43: GeomPoint X=115.828 Y=20.8307 Z=0
    g44: GeomPoint X=116.173 Y=21.5825 Z=0
  constraints (70):
    c: Horizontal(g0)
    c: Distance(g0) = 3
    c: Coincident(g1,g0)
    c: Vertical(g1)
    c: Block(g2)
    c: Block(g0)
    c: Coincident(g3,g0)
    c: Coincident(g3,g2)
    c: Vertical(g3)
    c: Block(g1)
    c: Block(g4)
    c: Coincident(g19,g4)
    c: Block(g19)
    c: Equal(g5, g6-g11) x6
    c: InternalAlignment(g5-g11 -> g12) x7
    c: InternalAlignment(g13-g17 -> g12) x5
    c: Block(g12)
    c: Coincident(g18,g12)
    c: Block(g18)
    c: Coincident(g20,g2)
    c: Coincident(g20,g19)
    c: Horizontal(g20)
    c: Distance(g20) = 93.4
    c: Coincident(g21,g1)
    c: Horizontal(g21)
    c: Distance(g21) = 101.7
    c: Horizontal(g23)
    c: Distance(g23) = 8
    c: Coincident(g24,g23)
    c: Block(g23)
    c: Coincident(g22,g24)
    c: Block(g24)
    c: Block(g22)
    c: Distance(g22) = 1.61553
    c: Coincident(g25,g18)
    c: Block(g25)
    c: Weight(g26) = 1
    c: Equal(g26,g27)
    c: Equal(g26,g28)
    c: Coincident(g29,g4)
    c: InternalAlignment(g26,g29)
    c: InternalAlignment(g27,g29)
    c: InternalAlignment(g28,g29)
    c: InternalAlignment(g30,g29)
    c: InternalAlignment(g31,g29)
    c: Block(g29)
    c: Weight(g32) = 1
    c: Equal(g32,g33)
    c: Equal(g32,g34)
    c: Coincident(g35,g29)
    c: InternalAlignment(g32,g35)
    c: InternalAlignment(g33,g35)
    c: InternalAlignment(g34,g35)
    c: InternalAlignment(g36,g35)
    c: InternalAlignment(g37,g35)
    c: Block(g35)
    c: Coincident(g38,g35)
    c: Vertical(g38)
    c: Block(g38)
    c: Coincident(g42,g38)
    c: Weight(g39) = 1
    c: Equal(g39,g40)
    c: Equal(g39,g41)
    c: Coincident(g42,g25)
    c: InternalAlignment(g39,g42)
    c: InternalAlignment(g40,g42)
    c: InternalAlignment(g41,g42)
    c: InternalAlignment(g43,g42)
    c: InternalAlignment(g44,g42)
    c: Block(g42)
FEATURE [Part::Extrusion] Extrude064  label="bottom016"
  Base = -> Sketch073
  Dir = (0,0,1)
  DirMode = 2
  FaceMakerClass = Part::FaceMakerBullseye
  LengthFwd = 71.4
  LengthRev = 0
  Placement = pos=(0,0,0.3) rot=(0,0,1;0rad)
  Solid = true
  Symmetric = false
FEATURE [Part::Revolution] Revolve157  label="removeToCreateScrewAndThreadedInsertHole063"
  Angle = 360
  Axis = (0,1,0)
  Base = (0,0,0)
  FaceMakerClass = Part::FaceMakerBullseye
  Placement = pos=(12.5,0,10) rot=(0,0,1;0rad)
  Solid = false
  Source = -> Face141
  Symmetric = false
FEATURE [Sketcher::SketchObject] Sketch074
  FullyConstrained = true
  Placement = pos=(117,19,0) rot=(0.57735,0.57735,0.57735;2.0944rad)
  sketch-geometry (48):
    g0: LineSegment StartX=-49.19 StartY=69.25 StartZ=0 EndX=-49.19 EndY=66.25 EndZ=0
    g1: LineSegment StartX=-49.19 StartY=63.5 StartZ=0 EndX=-49.19 EndY=60.5 EndZ=0
    g2: LineSegment StartX=-49.19 StartY=57.75 StartZ=0 EndX=-49.19 EndY=54.75 EndZ=0
    g3: LineSegment StartX=-49.19 StartY=52 StartZ=0 EndX=-49.19 EndY=49 EndZ=0
    g4: LineSegment StartX=-49.19 StartY=46.25 StartZ=0 EndX=-49.19 EndY=43.25 EndZ=0
    g5: LineSegment StartX=-49.19 StartY=40.5 StartZ=0 EndX=-49.19 EndY=37.5 EndZ=0
    g6: LineSegment StartX=-49.19 StartY=34.5 StartZ=0 EndX=-49.19 EndY=31.5 EndZ=0
    g7: LineSegment StartX=-49.19 StartY=28.75 StartZ=0 EndX=-49.19 EndY=25.75 EndZ=0
    g8: LineSegment StartX=-49.19 StartY=23 StartZ=0 EndX=-49.19 EndY=20 EndZ=0
    g9: LineSegment StartX=-49.19 StartY=17.25 StartZ=0 EndX=-49.19 EndY=14.25 EndZ=0
    g10: LineSegment StartX=-49.19 StartY=11.5 StartZ=0 EndX=-49.19 EndY=8.5 EndZ=0
    g11: LineSegment StartX=-49.19 StartY=5.75 StartZ=0 EndX=-49.19 EndY=2.75 EndZ=0
    g12: ArcOfCircle CenterX=-1.5 CenterY=67.75 CenterZ=0 NormalX=0 NormalY=0 NormalZ=1 AngleXU=0 Radius=1.5 StartAngle=4.71239 EndAngle=7.85398
    g13: ArcOfCircle CenterX=-1.5 CenterY=62 CenterZ=0 NormalX=0 NormalY=0 NormalZ=1 AngleXU=0 Radius=1.5 StartAngle=4.71239 EndAngle=7.85398
    g14: ArcOfCircle CenterX=-1.5 CenterY=56.25 CenterZ=0 NormalX=0 NormalY=0 NormalZ=1 AngleXU=0 Radius=1.5 StartAngle=4.71239 EndAngle=7.85398
    g15: ArcOfCircle CenterX=-11.49 CenterY=50.5 CenterZ=0 NormalX=0 NormalY=0 NormalZ=1 AngleXU=0 Radius=1.5 StartAngle=4.71239 EndAngle=7.85398
    g16: ArcOfCircle CenterX=-16.28 CenterY=44.75 CenterZ=0 NormalX=0 NormalY=0 NormalZ=1 AngleXU=0 Radius=1.5 StartAngle=4.71239 EndAngle=7.85398
    g17: ArcOfCircle CenterX=-18.2337 CenterY=39 CenterZ=0 NormalX=0 NormalY=0 NormalZ=1 AngleXU=0 Radius=1.5 StartAngle=4.71485 EndAngle=7.85398
    g18: ArcOfCircle CenterX=-16.2837 CenterY=27.25 CenterZ=0 NormalX=0 NormalY=0 NormalZ=1 AngleXU=0 Radius=1.5 StartAngle=4.71485 EndAngle=7.85398
    g19: ArcOfCircle CenterX=-18.2337 CenterY=33 CenterZ=0 NormalX=0 NormalY=0 NormalZ=1 AngleXU=0 Radius=1.5 StartAngle=4.71485 EndAngle=7.85398
    g20: ArcOfCircle CenterX=-11.49 CenterY=21.5 CenterZ=0 NormalX=0 NormalY=0 NormalZ=1 AngleXU=0 Radius=1.5 StartAngle=4.71239 EndAngle=7.85398
    g21: ArcOfCircle CenterX=-1.5 CenterY=4.25 CenterZ=0 NormalX=0 NormalY=0 NormalZ=1 AngleXU=0 Radius=1.5 StartAngle=4.71239 EndAngle=7.85398
    g22: ArcOfCircle CenterX=-1.5 CenterY=10 CenterZ=0 NormalX=0 NormalY=0 NormalZ=1 AngleXU=0 Radius=1.5 StartAngle=4.71239 EndAngle=7.85398
    g23: ArcOfCircle CenterX=-1.5 CenterY=15.75 CenterZ=0 NormalX=0 NormalY=0 NormalZ=1 AngleXU=0 Radius=1.5 StartAngle=4.71239 EndAngle=7.85398
    g24: LineSegment StartX=-49.19 StartY=69.25 StartZ=0 EndX=-1.5 EndY=69.25 EndZ=0
    g25: LineSegment StartX=-49.19 StartY=66.25 StartZ=0 EndX=-1.5 EndY=66.25 EndZ=0
    g26: LineSegment StartX=-49.19 StartY=63.5 StartZ=0 EndX=-1.5 EndY=63.5 EndZ=0
    g27: LineSegment StartX=-49.19 StartY=60.5 StartZ=0 EndX=-1.5 EndY=60.5 EndZ=0
    g28: LineSegment StartX=-49.19 StartY=57.75 StartZ=0 EndX=-1.5 EndY=57.75 EndZ=0
    g29: LineSegment StartX=-49.19 StartY=54.75 StartZ=0 EndX=-1.5 EndY=54.75 EndZ=0
    g30: LineSegment StartX=-49.19 StartY=52 StartZ=0 EndX=-11.49 EndY=52 EndZ=0
    g31: LineSegment StartX=-49.19 StartY=49 StartZ=0 EndX=-11.49 EndY=49 EndZ=0
    g32: LineSegment StartX=-49.19 StartY=46.25 StartZ=0 EndX=-16.28 EndY=46.25 EndZ=0
    g33: LineSegment StartX=-49.19 StartY=43.25 StartZ=0 EndX=-16.28 EndY=43.25 EndZ=0
    g34: LineSegment StartX=-49.19 StartY=40.5 StartZ=0 EndX=-18.2337 EndY=40.5 EndZ=0
    g35: LineSegment StartX=-49.19 StartY=37.5 StartZ=0 EndX=-18.23 EndY=37.5 EndZ=0
    g36: LineSegment StartX=-49.19 StartY=34.5 StartZ=0 EndX=-18.2337 EndY=34.5 EndZ=0
    g37: LineSegment StartX=-49.19 StartY=31.5 StartZ=0 EndX=-18.23 EndY=31.5 EndZ=0
    g38: LineSegment StartX=-49.19 StartY=28.75 StartZ=0 EndX=-16.2837 EndY=28.75 EndZ=0
    g39: LineSegment StartX=-49.19 StartY=25.75 StartZ=0 EndX=-16.28 EndY=25.75 EndZ=0
    g40: LineSegment StartX=-49.19 StartY=23 StartZ=0 EndX=-11.49 EndY=23 EndZ=0
    g41: LineSegment StartX=-49.19 StartY=20 StartZ=0 EndX=-11.49 EndY=20 EndZ=0
    g42: LineSegment StartX=-49.19 StartY=17.25 StartZ=0 EndX=-1.5 EndY=17.25 EndZ=0
    g43: LineSegment StartX=-49.19 StartY=14.25 StartZ=0 EndX=-1.5 EndY=14.25 EndZ=0
    g44: LineSegment StartX=-49.19 StartY=11.5 StartZ=0 EndX=-1.5 EndY=11.5 EndZ=0
    g45: LineSegment StartX=-49.19 StartY=8.5 StartZ=0 EndX=-1.5 EndY=8.5 EndZ=0
    g46: LineSegment StartX=-49.19 StartY=5.75 StartZ=0 EndX=-1.5 EndY=5.75 EndZ=0
    g47: LineSegment StartX=-49.19 StartY=2.75 StartZ=0 EndX=-1.5 EndY=2.75 EndZ=0
  constraints (120):
    c: Vertical(g0)
    c: Distance(g0) = 3
    c: Block(g0)
    c: Vertical(g1)
    c: Distance(g1) = 3
    c: Vertical(g2)
    c: Equal(g0,g2) = 3
    c: Block(g2)
    c: Vertical(g3)
    c: Equal(g1,g3) = 3
    c: Vertical(g4)
    c: Equal(g0,g4) = 3
    c: Block(g4)
    c: Vertical(g5)
    c: Equal(g1,g5) = 3
    c: Vertical(g6)
    c: Equal(g0,g6) = 3
    c: Block(g6)
    c: Vertical(g7)
    c: Equal(g1,g7) = 3
    c: Vertical(g8)
    c: Equal(g0,g8) = 3
    c: Block(g8)
    c: Vertical(g9)
    c: Equal(g1,g9) = 3
    c: Vertical(g10)
    c: Equal(g0,g10) = 3
    c: Block(g10)
    c: Vertical(g11)
    c: Equal(g1,g11) = 3
    c: Block(g12)
    c: Block(g13)
    c: Block(g14)
    c: Block(g15)
    c: Block(g16)
    c: Block(g17)
    c: Block(g18)
    c: Block(g19)
    c: Block(g20)
    c: Block(g21)
    c: Block(g22)
    c: Block(g23)
    c: Block(g11)
    c: Block(g9)
    c: Block(g7)
    c: Block(g5)
    c: Block(g3)
    c: Block(g1)
    c: Coincident(g24,g0)
    c: Coincident(g24,g12)
    c: Horizontal(g24)
    c: Coincident(g25,g0)
    c: Coincident(g25,g12)
    c: Horizontal(g25)
    c: Coincident(g26,g1)
    c: Coincident(g26,g13)
    c: Horizontal(g26)
    c: Coincident(g27,g1)
    c: Coincident(g27,g13)
    c: Horizontal(g27)
    c: Coincident(g28,g2)
    c: Coincident(g28,g14)
    c: Horizontal(g28)
    c: Coincident(g29,g2)
    c: Coincident(g29,g14)
    c: Horizontal(g29)
    c: Coincident(g30,g3)
    c: Coincident(g30,g15)
    c: Horizontal(g30)
    c: Coincident(g31,g3)
    c: Coincident(g31,g15)
    c: Horizontal(g31)
    c: Coincident(g32,g4)
    c: Coincident(g32,g16)
    c: Horizontal(g32)
    c: Coincident(g33,g4)
    c: Coincident(g33,g16)
    c: Horizontal(g33)
    c: Coincident(g34,g5)
    c: Coincident(g34,g17)
    c: Horizontal(g34)
    c: Coincident(g35,g5)
    c: Coincident(g35,g17)
    c: Horizontal(g35)
    c: Coincident(g36,g6)
    c: Coincident(g36,g19)
    c: Horizontal(g36)
    c: Coincident(g37,g6)
    c: Coincident(g37,g19)
    c: Horizontal(g37)
    c: Coincident(g38,g7)
    c: Coincident(g38,g18)
    c: Horizontal(g38)
    c: Coincident(g39,g7)
    c: Coincident(g39,g18)
    c: Horizontal(g39)
    c: Coincident(g40,g8)
    c: Coincident(g40,g20)
    c: Horizontal(g40)
    c: Coincident(g41,g8)
    c: Coincident(g41,g20)
    c: Horizontal(g41)
    c: Coincident(g42,g9)
    c: Coincident(g42,g23)
    c: Horizontal(g42)
    c: Coincident(g43,g9)
    c: Coincident(g43,g23)
    c: Horizontal(g43)
    c: Coincident(g44,g10)
    c: Coincident(g44,g22)
    c: Horizontal(g44)
    c: Coincident(g45,g10)
    c: Coincident(g45,g22)
    c: Horizontal(g45)
    c: Coincident(g46,g11)
    c: Coincident(g46,g21)
    c: Horizontal(g46)
    c: Coincident(g47,g11)
    c: Coincident(g47,g21)
    c: Horizontal(g47)
FEATURE [Part::Extrusion] Extrude065
  Base = -> Sketch074
  Dir = (1,0,0)
  DirMode = 2
  FaceMakerClass = Part::FaceMakerBullseye
  LengthFwd = 23
  LengthRev = 0
  Placement = pos=(-19,0,0) rot=(0,0,1;0rad)
  Solid = true
  Symmetric = false
FEATURE [Part::Fillet] Fillet056  label="removeToCreateVentalationHoles003"
  Base = -> Extrude065
  Edges = <same value as first occurrence — deduplicated (x6 in doc)>
  Placement = pos=(7,0.02,0) rot=(0,0,1;0rad)
FEATURE [Part::Revolution] Revolve158  label="removeToCreateScrewAndThreadedInsertHole065"
  Angle = 360
  Axis = (0,1,0)
  Base = (0,0,0)
  FaceMakerClass = Part::FaceMakerBullseye
  Placement = pos=(12.5,0,62) rot=(0,0,1;0rad)
  Solid = false
  Source = -> Face146
  Symmetric = false
FEATURE [Part::Revolution] Revolve159  label="removeToCreateScrewAndThreadedInsertHole066"
  Angle = 360
  Axis = (0,1,0)
  Base = (0,0,0)
  FaceMakerClass = Part::FaceMakerBullseye
  Placement = pos=(89.5,0,68.5) rot=(0,0,1;0rad)
  Solid = false
  Source = -> Face143
  Symmetric = false
FEATURE [Part::Revolution] Revolve160  label="removeToCreateScrewAndThreadedInsertHole067"
  Angle = 360
  Axis = (0,1,0)
  Base = (0,0,0)
  FaceMakerClass = Part::FaceMakerBullseye
  Placement = pos=(89.5,0,3.5) rot=(0,0,1;0rad)
  Solid = false
  Source = -> Face142
  Symmetric = false
FEATURE [Part::Revolution] Revolve161  label="removeToCreateScrewAndThreadedInsertHole068"
  Angle = 360
  Axis = (0,1,0)
  Base = (0,0,0)
  FaceMakerClass = Part::FaceMakerBullseye
  Placement = pos=(109.5,4.7,3.5) rot=(0,0,1;0rad)
  Solid = false
  Source = -> Face145
  Symmetric = false
FEATURE [Part::Revolution] Revolve162  label="removeToCreateScrewAndThreadedInsertHole069"
  Angle = 360
  Axis = (0,1,0)
  Base = (0,0,0)
  FaceMakerClass = Part::FaceMakerBullseye
  Placement = pos=(109.5,4.7,68.5) rot=(0,0,1;0rad)
  Solid = false
  Source = -> Face144
  Symmetric = false
FEATURE [Part::MultiFuse] Fusion141  label="removeToCreateScrewAndThreadedInsertHole064"
  Shapes = -> [Revolve162,Revolve161,Revolve160,Revolve159,Revolve158,Revolve157]
FEATURE [Part::Cylinder] Cylinder062
  Angle = 360
  AttacherType = Attacher::AttachEngine3D
  Height = 20
  Placement = pos=(0,0,36.15) rot=(0,0,1;0rad)
  Radius = 14
FEATURE [Part::Cylinder] Cylinder063
  Angle = 360
  AttacherType = Attacher::AttachEngine3D
  Height = 10
  Placement = pos=(0,0,36.15) rot=(0,0,1;0rad)
  Radius = 4
FEATURE [Part::MultiFuse] Fusion139  label="removeToCreteHoleForPlugHousing052"
  Placement = pos=(70,19,36) rot=(0,1,0;1.5708rad)
  Shapes = -> [Cylinder062,Cylinder063]
FEATURE [Part::Cut] Cut060  label="bottom017"
  Base = -> Extrude064
  Tool = -> Fusion139
FEATURE [Part::Cut] Cut061  label="bottom019"
  Base = -> Cut060
  Tool = -> Fusion141
FEATURE [Part::MultiFuse] Fusion140  label="bottom018"
  Shapes = -> [Cut061,Cut058]
FEATURE [Part::Cut] Cut059  label="bottom020"
  Base = -> Fusion140
  Tool = -> Fillet056
FEATURE [Part::Box] Box036  label="Cube021"
  AttacherType = Attacher::AttachEngine3D
  Height = 80
  Length = 26
  Placement = pos=(0,-1,-5) rot=(0,0,1;0rad)
  Width = 11
FEATURE [Part::Cut] Cut062  label="removeFromBottom002"
  Base = -> Cut057
  Tool = -> Box036
FEATURE [Part::Cut] Cut063
  Base = -> Cut059
  Tool = -> Cut062
FEATURE [Part::Cut] Cut064  label="pcbStands"
  Base = -> Fusion095
  Tool = -> Fusion127
FEATURE [Sketcher::SketchObject] Sketch075  label="topSketch022"
  FullyConstrained = true
  sketch-geometry (6):
    g0: LineSegment StartX=19 StartY=38 StartZ=0 EndX=117 EndY=38 EndZ=0
    g1: ArcOfCircle CenterX=19 CenterY=19 CenterZ=0 NormalX=0 NormalY=0 NormalZ=1 AngleXU=0 Radius=19 StartAngle=1.5708 EndAngle=3.14159
    g2: LineSegment StartX=117 StartY=38 StartZ=0 EndX=117 EndY=19 EndZ=0
    g3: LineSegment StartX=98 StartY=1.0161e-12 StartZ=0 EndX=5.22862e-06 EndY=1.0161e-12 EndZ=0
    g4: LineSegment StartX=5.22862e-06 StartY=19 StartZ=0 EndX=5.22862e-06 EndY=1.0161e-12 EndZ=0
    g5: ArcOfCircle CenterX=98 CenterY=19 CenterZ=0 NormalX=0 NormalY=0 NormalZ=1 AngleXU=0 Radius=19 StartAngle=4.71239 EndAngle=6.28319
  constraints (16):
    c: Horizontal(g0)
    c: Distance(g0) = 98
    c: Coincident(g1,g0)
    c: Block(g1)
    c: Coincident(g2,g0)
    c: Vertical(g2)
    c: Distance(g2) = 19
    c: Horizontal(g3)
    c: Coincident(g4,g1)
    c: Vertical(g4)
    c: Coincident(g3,g4)
    c: Block(g3)
    c: Coincident(g5,g2)
    c: Coincident(g5,g3)
    c: Block(g0)
    c: Block(g5)
FEATURE [Part::Extrusion] Extrude067  label="sideB003"
  Base = -> Sketch075
  Dir = (0,0,1)
  DirMode = 2
  FaceMakerClass = Part::FaceMakerBullseye
  LengthFwd = 3
  LengthRev = 0
  Placement = pos=(0,0,71.7) rot=(0,0,1;0rad)
  Solid = true
  Symmetric = false
FEATURE [Sketcher::SketchObject] Sketch076  label="topSketch023"
  FullyConstrained = true
  sketch-geometry (6):
    g0: LineSegment StartX=19 StartY=38 StartZ=0 EndX=117 EndY=38 EndZ=0
    g1: ArcOfCircle CenterX=19 CenterY=19 CenterZ=0 NormalX=0 NormalY=0 NormalZ=1 AngleXU=0 Radius=19 StartAngle=1.5708 EndAngle=3.14159
    g2: LineSegment StartX=117 StartY=38 StartZ=0 EndX=117 EndY=19 EndZ=0
    g3: LineSegment StartX=98 StartY=1.0161e-12 StartZ=0 EndX=5.22862e-06 EndY=1.0161e-12 EndZ=0
    g4: LineSegment StartX=5.22862e-06 StartY=19 StartZ=0 EndX=5.22862e-06 EndY=1.0161e-12 EndZ=0
    g5: ArcOfCircle CenterX=98 CenterY=19 CenterZ=0 NormalX=0 NormalY=0 NormalZ=1 AngleXU=0 Radius=19 StartAngle=4.71239 EndAngle=6.28319
  constraints (16):
    c: Horizontal(g0)
    c: Distance(g0) = 98
    c: Coincident(g1,g0)
    c: Block(g1)
    c: Coincident(g2,g0)
    c: Vertical(g2)
    c: Distance(g2) = 19
    c: Horizontal(g3)
    c: Coincident(g4,g1)
    c: Vertical(g4)
    c: Coincident(g3,g4)
    c: Block(g3)
    c: Coincident(g5,g2)
    c: Coincident(g5,g3)
    c: Block(g0)
    c: Block(g5)
FEATURE [Part::Extrusion] Extrude066  label="sideA003"
  Base = -> Sketch076
  Dir = (0,0,1)
  DirMode = 2
  FaceMakerClass = Part::FaceMakerBullseye
  LengthFwd = 3
  LengthRev = 0
  Placement = pos=(0,0,-2.7) rot=(0,0,1;0rad)
  Solid = true
  Symmetric = false
FEATURE [Part::MultiFuse] Fusion142  label="removeFromBottom003"
  Placement = pos=(2,0,0) rot=(0,0,1;0rad)
  Shapes = -> [Extrude066,Extrude067]
FEATURE [Part::Cut] Cut065  label="screwRetainers002"
  Base = -> Fusion096
  Tool = -> Fusion142
FEATURE [Sketcher::SketchObject] Sketch077
  FullyConstrained = true
  Placement = pos=(117,19,0) rot=(0.57735,0.57735,0.57735;2.0944rad)
  sketch-geometry (8):
    g0: LineSegment StartX=-49.19 StartY=63.5 StartZ=0 EndX=-49.19 EndY=60.5 EndZ=0
    g1: LineSegment StartX=-49.19 StartY=11.5 StartZ=0 EndX=-49.19 EndY=8.5 EndZ=0
    g2: ArcOfCircle CenterX=-1.5 CenterY=62 CenterZ=0 NormalX=0 NormalY=0 NormalZ=1 AngleXU=0 Radius=1.5 StartAngle=4.71239 EndAngle=7.85398
    g3: ArcOfCircle CenterX=-1.5 CenterY=10 CenterZ=0 NormalX=0 NormalY=0 NormalZ=1 AngleXU=0 Radius=1.5 StartAngle=4.71239 EndAngle=7.85398
    g4: LineSegment StartX=-49.19 StartY=63.5 StartZ=0 EndX=-1.5 EndY=63.5 EndZ=0
    g5: LineSegment StartX=-49.19 StartY=60.5 StartZ=0 EndX=-1.5 EndY=60.5 EndZ=0
    g6: LineSegment StartX=-49.19 StartY=11.5 StartZ=0 EndX=-1.5 EndY=11.5 EndZ=0
    g7: LineSegment StartX=-49.19 StartY=8.5 StartZ=0 EndX=-1.5 EndY=8.5 EndZ=0
  constraints (19):
    c: Vertical(g0)
    c: Distance(g0) = 3
    c: Vertical(g1)
    c: Block(g1)
    c: Block(g2)
    c: Block(g3)
    c: Block(g0)
    c: Coincident(g4,g0)
    c: Coincident(g4,g2)
    c: Horizontal(g4)
    c: Coincident(g5,g0)
    c: Coincident(g5,g2)
    c: Horizontal(g5)
    c: Coincident(g6,g1)
    c: Coincident(g6,g3)
    c: Horizontal(g6)
    c: Coincident(g7,g1)
    c: Coincident(g7,g3)
    c: Horizontal(g7)
FEATURE [Part::Extrusion] Extrude068
  Base = -> Sketch077
  Dir = (1,0,0)
  DirMode = 2
  FaceMakerClass = Part::FaceMakerBullseye
  LengthFwd = 10
  LengthRev = 0
  Solid = true
  Symmetric = false
FEATURE [Part::Fillet] Fillet057  label="removeFromtMoreFrontCaseScrewRetainers002"
  Base = -> Extrude068
  Edges = 4 edges r=1.49: [Edge6,Edge11,Edge18,Edge23]
  Placement = pos=(-12,0,0) rot=(0,0,1;0rad)
FEATURE [Sketcher::SketchObject] Sketch078
  FullyConstrained = true
  Placement = pos=(117,19,0) rot=(0.57735,0.57735,0.57735;2.0944rad)
  sketch-geometry (8):
    g0: LineSegment StartX=-49.19 StartY=69.25 StartZ=0 EndX=-49.19 EndY=66.25 EndZ=0
    g1: LineSegment StartX=-49.19 StartY=5.75 StartZ=0 EndX=-49.19 EndY=2.75 EndZ=0
    g2: ArcOfCircle CenterX=-1.5 CenterY=67.75 CenterZ=0 NormalX=0 NormalY=0 NormalZ=1 AngleXU=0 Radius=1.5 StartAngle=4.71239 EndAngle=7.85398
    g3: ArcOfCircle CenterX=-1.5 CenterY=4.25 CenterZ=0 NormalX=0 NormalY=0 NormalZ=1 AngleXU=0 Radius=1.5 StartAngle=4.71239 EndAngle=7.85398
    g4: LineSegment StartX=-49.19 StartY=69.25 StartZ=0 EndX=-1.5 EndY=69.25 EndZ=0
    g5: LineSegment StartX=-49.19 StartY=66.25 StartZ=0 EndX=-1.5 EndY=66.25 EndZ=0
    g6: LineSegment StartX=-49.19 StartY=5.75 StartZ=0 EndX=-1.5 EndY=5.75 EndZ=0
    g7: LineSegment StartX=-49.19 StartY=2.75 StartZ=0 EndX=-1.5 EndY=2.75 EndZ=0
  constraints (19):
    c: Vertical(g0)
    c: Distance(g0) = 3
    c: Block(g0)
    c: Vertical(g1)
    c: Block(g2)
    c: Block(g3)
    c: Block(g1)
    c: Coincident(g4,g0)
    c: Coincident(g4,g2)
    c: Horizontal(g4)
    c: Coincident(g5,g0)
    c: Coincident(g5,g2)
    c: Horizontal(g5)
    c: Coincident(g6,g1)
    c: Coincident(g6,g3)
    c: Horizontal(g6)
    c: Coincident(g7,g1)
    c: Coincident(g7,g3)
    c: Horizontal(g7)
FEATURE [Part::Extrusion] Extrude069
  Base = -> Sketch078
  Dir = (1,0,0)
  DirMode = 2
  FaceMakerClass = Part::FaceMakerBullseye
  LengthFwd = 10
  LengthRev = 0
  Solid = true
  Symmetric = false
FEATURE [Part::Fillet] Fillet058  label="removeFromtMoreFrontCaseScrewRetainers003"
  Base = -> Extrude069
  Edges = 4 edges r=1.49: [Edge6,Edge11,Edge18,Edge23]
  Placement = pos=(-4,0,0) rot=(0,0,1;0rad)
FEATURE [Part::Cut] Cut066
  Base = -> Cut065
  Tool = -> Fillet058
FEATURE [Part::Cut] Cut067  label="screwPillars"
  Base = -> Cut066
  Tool = -> Fillet057
FEATURE [Part::MultiFuse] Fusion143  label="bottom021"
  Shapes = -> [Cut031,Cut063]
FEATURE [Part::Cylinder] Cylinder
  Angle = 360
  AttacherType = Attacher::AttachEngine3D
  Height = 10
  Placement = pos=(20.65,12,4.68) rot=(1,0,0;1.5708rad)
  Radius = 2
FEATURE [Part::Cylinder] Cylinder064
  Angle = 360
  AttacherType = Attacher::AttachEngine3D
  Height = 10
  Placement = pos=(20.65,12,67.38) rot=(1,0,0;1.5708rad)
  Radius = 2
FEATURE [Part::Cylinder] Cylinder065
  Angle = 360
  AttacherType = Attacher::AttachEngine3D
  Height = 10
  Placement = pos=(77.15,12,67.38) rot=(1,0,0;1.5708rad)
  Radius = 2
FEATURE [Part::Cylinder] Cylinder066
  Angle = 360
  AttacherType = Attacher::AttachEngine3D
  Height = 10
  Placement = pos=(77.15,12,4.68) rot=(1,0,0;1.5708rad)
  Radius = 2
FEATURE [Part::MultiFuse] Fusion144  label="removeFromThreadedInsertHousing"
  Shapes = -> [Cylinder065,Cylinder064,Cylinder,Cylinder066]
FEATURE [Part::Cut] Cut068  label="pcbStands001"
  Base = -> Cut064
  Tool = -> Fusion144
FEATURE [Part::MultiFuse] Fusion145
  Shapes = -> [Cut068,Fusion143]
FEATURE [Part::MultiFuse] Fusion146
  Shapes = -> [Fusion145]
FEATURE [Part::MultiFuse] Fusion147  label="bottom022"
  Shapes = -> [Cut067,Fusion146]
FEATURE [Part::MultiFuse] Fusion148  label="casePillars005"
  Shapes = -> [Cut047,Fusion092]
FEATURE [Part::MultiFuse] Fusion149  label="bottom023"
  Shapes = -> [Fusion124,Fusion113,Fusion147]
FEATURE [Part::MultiFuse] Fusion150  label="topBits"
  Shapes = -> [Cut025,Fusion148,Cut030,Fillet034]
FEATURE [Part::Feature] Face149 .. Face152  x4 (patterned run collapsed; names and placements below)
  shape: bbox 3.2 x 1.5 x 2e-07 mm, 1 faces, 0 solids (baked)
FEATURE [Part::Feature] Face153
  shape: bbox 3.6 x 3.2 x 2e-07 mm, 1 faces, 0 solids (baked)
FEATURE [Part::Feature] Face154
  shape: bbox 3.6 x 3.2 x 2e-07 mm, 1 faces, 0 solids (baked)
FEATURE [Sketcher::SketchObject] Sketch079  label="topSketch024"
  FullyConstrained = true
  sketch-geometry (6):
    g0: LineSegment StartX=19 StartY=38 StartZ=0 EndX=117 EndY=38 EndZ=0
    g1: ArcOfCircle CenterX=19 CenterY=19 CenterZ=0 NormalX=0 NormalY=0 NormalZ=1 AngleXU=0 Radius=19 StartAngle=1.5708 EndAngle=3.14159
    g2: LineSegment StartX=117 StartY=38 StartZ=0 EndX=117 EndY=19 EndZ=0
    g3: LineSegment StartX=98 StartY=1.0161e-12 StartZ=0 EndX=5.22862e-06 EndY=1.0161e-12 EndZ=0
    g4: LineSegment StartX=5.22862e-06 StartY=19 StartZ=0 EndX=5.22862e-06 EndY=1.0161e-12 EndZ=0
    g5: ArcOfCircle CenterX=98 CenterY=19 CenterZ=0 NormalX=0 NormalY=0 NormalZ=1 AngleXU=0 Radius=19 StartAngle=4.71239 EndAngle=6.28319
  constraints (16):
    c: Horizontal(g0)
    c: Distance(g0) = 98
    c: Coincident(g1,g0)
    c: Block(g1)
    c: Coincident(g2,g0)
    c: Vertical(g2)
    c: Distance(g2) = 19
    c: Horizontal(g3)
    c: Coincident(g4,g1)
    c: Vertical(g4)
    c: Coincident(g3,g4)
    c: Block(g3)
    c: Coincident(g5,g2)
    c: Coincident(g5,g3)
    c: Block(g0)
    c: Block(g5)
FEATURE [Sketcher::SketchObject] Sketch080  label="topSketch025"
  FullyConstrained = true
  sketch-geometry (6):
    g0: LineSegment StartX=19 StartY=38 StartZ=0 EndX=117 EndY=38 EndZ=0
    g1: ArcOfCircle CenterX=19 CenterY=19 CenterZ=0 NormalX=0 NormalY=0 NormalZ=1 AngleXU=0 Radius=19 StartAngle=1.5708 EndAngle=3.14159
    g2: LineSegment StartX=117 StartY=38 StartZ=0 EndX=117 EndY=19 EndZ=0
    g3: LineSegment StartX=98 StartY=1.0161e-12 StartZ=0 EndX=5.22862e-06 EndY=1.0161e-12 EndZ=0
    g4: LineSegment StartX=5.22862e-06 StartY=19 StartZ=0 EndX=5.22862e-06 EndY=1.0161e-12 EndZ=0
    g5: ArcOfCircle CenterX=98 CenterY=19 CenterZ=0 NormalX=0 NormalY=0 NormalZ=1 AngleXU=0 Radius=19 StartAngle=4.71239 EndAngle=6.28319
  constraints (16):
    c: Horizontal(g0)
    c: Distance(g0) = 98
    c: Coincident(g1,g0)
    c: Block(g1)
    c: Coincident(g2,g0)
    c: Vertical(g2)
    c: Distance(g2) = 19
    c: Horizontal(g3)
    c: Coincident(g4,g1)
    c: Vertical(g4)
    c: Coincident(g3,g4)
    c: Block(g3)
    c: Coincident(g5,g2)
    c: Coincident(g5,g3)
    c: Block(g0)
    c: Block(g5)
FEATURE [Part::Extrusion] Extrude070  label="sideA004"
  Base = -> Sketch080
  Dir = (0,0,1)
  DirMode = 2
  FaceMakerClass = Part::FaceMakerBullseye
  LengthFwd = 3
  LengthRev = 0
  Placement = pos=(0,0,-2.7) rot=(0,0,1;0rad)
  Solid = true
  Symmetric = false
FEATURE [Sketcher::SketchObject] Sketch081
  FullyConstrained = true
  Placement = pos=(117,19,0) rot=(0.57735,0.57735,0.57735;2.0944rad)
  sketch-geometry (8):
    g0: LineSegment StartX=-49.19 StartY=63.5 StartZ=0 EndX=-49.19 EndY=60.5 EndZ=0
    g1: LineSegment StartX=-49.19 StartY=11.5 StartZ=0 EndX=-49.19 EndY=8.5 EndZ=0
    g2: ArcOfCircle CenterX=-1.5 CenterY=62 CenterZ=0 NormalX=0 NormalY=0 NormalZ=1 AngleXU=0 Radius=1.5 StartAngle=4.71239 EndAngle=7.85398
    g3: ArcOfCircle CenterX=-1.5 CenterY=10 CenterZ=0 NormalX=0 NormalY=0 NormalZ=1 AngleXU=0 Radius=1.5 StartAngle=4.71239 EndAngle=7.85398
    g4: LineSegment StartX=-49.19 StartY=63.5 StartZ=0 EndX=-1.5 EndY=63.5 EndZ=0
    g5: LineSegment StartX=-49.19 StartY=60.5 StartZ=0 EndX=-1.5 EndY=60.5 EndZ=0
    g6: LineSegment StartX=-49.19 StartY=11.5 StartZ=0 EndX=-1.5 EndY=11.5 EndZ=0
    g7: LineSegment StartX=-49.19 StartY=8.5 StartZ=0 EndX=-1.5 EndY=8.5 EndZ=0
  constraints (19):
    c: Vertical(g0)
    c: Distance(g0) = 3
    c: Vertical(g1)
    c: Block(g1)
    c: Block(g2)
    c: Block(g3)
    c: Block(g0)
    c: Coincident(g4,g0)
    c: Coincident(g4,g2)
    c: Horizontal(g4)
    c: Coincident(g5,g0)
    c: Coincident(g5,g2)
    c: Horizontal(g5)
    c: Coincident(g6,g1)
    c: Coincident(g6,g3)
    c: Horizontal(g6)
    c: Coincident(g7,g1)
    c: Coincident(g7,g3)
    c: Horizontal(g7)
FEATURE [Part::Extrusion] Extrude071  label="sideB004"
  Base = -> Sketch079
  Dir = (0,0,1)
  DirMode = 2
  FaceMakerClass = Part::FaceMakerBullseye
  LengthFwd = 3
  LengthRev = 0
  Placement = pos=(0,0,71.7) rot=(0,0,1;0rad)
  Solid = true
  Symmetric = false
FEATURE [Part::MultiFuse] Fusion152  label="removeFromBottom004"
  Placement = pos=(2,0,0) rot=(0,0,1;0rad)
  Shapes = -> [Extrude070,Extrude071]
FEATURE [Part::Extrusion] Extrude072
  Base = -> Sketch081
  Dir = (1,0,0)
  DirMode = 2
  FaceMakerClass = Part::FaceMakerBullseye
  LengthFwd = 10
  LengthRev = 0
  Solid = true
  Symmetric = false
FEATURE [Part::Fillet] Fillet059  label="removeFromtMoreFrontCaseScrewRetainers004"
  Base = -> Extrude072
  Edges = 4 edges r=1.49: [Edge6,Edge11,Edge18,Edge23]
  Placement = pos=(-12,0,0) rot=(0,0,1;0rad)
FEATURE [Sketcher::SketchObject] Sketch082
  FullyConstrained = true
  Placement = pos=(117,19,0) rot=(0.57735,0.57735,0.57735;2.0944rad)
  sketch-geometry (8):
    g0: LineSegment StartX=-49.19 StartY=69.25 StartZ=0 EndX=-49.19 EndY=66.25 EndZ=0
    g1: LineSegment StartX=-49.19 StartY=5.75 StartZ=0 EndX=-49.19 EndY=2.75 EndZ=0
    g2: ArcOfCircle CenterX=-1.5 CenterY=67.75 CenterZ=0 NormalX=0 NormalY=0 NormalZ=1 AngleXU=0 Radius=1.5 StartAngle=4.71239 EndAngle=7.85398
    g3: ArcOfCircle CenterX=-1.5 CenterY=4.25 CenterZ=0 NormalX=0 NormalY=0 NormalZ=1 AngleXU=0 Radius=1.5 StartAngle=4.71239 EndAngle=7.85398
    g4: LineSegment StartX=-49.19 StartY=69.25 StartZ=0 EndX=-1.5 EndY=69.25 EndZ=0
    g5: LineSegment StartX=-49.19 StartY=66.25 StartZ=0 EndX=-1.5 EndY=66.25 EndZ=0
    g6: LineSegment StartX=-49.19 StartY=5.75 StartZ=0 EndX=-1.5 EndY=5.75 EndZ=0
    g7: LineSegment StartX=-49.19 StartY=2.75 StartZ=0 EndX=-1.5 EndY=2.75 EndZ=0
  constraints (19):
    c: Vertical(g0)
    c: Distance(g0) = 3
    c: Block(g0)
    c: Vertical(g1)
    c: Block(g2)
    c: Block(g3)
    c: Block(g1)
    c: Coincident(g4,g0)
    c: Coincident(g4,g2)
    c: Horizontal(g4)
    c: Coincident(g5,g0)
    c: Coincident(g5,g2)
    c: Horizontal(g5)
    c: Coincident(g6,g1)
    c: Coincident(g6,g3)
    c: Horizontal(g6)
    c: Coincident(g7,g1)
    c: Coincident(g7,g3)
    c: Horizontal(g7)
FEATURE [Part::Extrusion] Extrude073
  Base = -> Sketch082
  Dir = (1,0,0)
  DirMode = 2
  FaceMakerClass = Part::FaceMakerBullseye
  LengthFwd = 10
  LengthRev = 0
  Solid = true
  Symmetric = false
FEATURE [Part::Fillet] Fillet060  label="removeFromtMoreFrontCaseScrewRetainers005"
  Base = -> Extrude073
  Edges = 4 edges r=1.49: [Edge6,Edge11,Edge18,Edge23]
  Placement = pos=(-4,0,0) rot=(0,0,1;0rad)
FEATURE [Part::Revolution] Revolve163  label="backCaseScrewRetainer004"
  Angle = 360
  Axis = (0,1,0)
  Base = (0,0,0)
  FaceMakerClass = Part::FaceMakerBullseye
  Placement = pos=(12.5,3,62) rot=(0,0,1;0rad)
  Solid = false
  Source = -> Face149
  Symmetric = false
FEATURE [Part::Revolution] Revolve164  label="frontCaseScrewRetainer006"
  Angle = 360
  Axis = (0,1,0)
  Base = (0,0,0)
  FaceMakerClass = Part::FaceMakerBullseye
  Placement = pos=(89.5,3,68.5) rot=(0,0,1;0rad)
  Solid = false
  Source = -> Face151
  Symmetric = false
FEATURE [Part::Revolution] Revolve165  label="frontCaseScrewRetainer007"
  Angle = 360
  Axis = (0,1,0)
  Base = (0,0,0)
  FaceMakerClass = Part::FaceMakerBullseye
  Placement = pos=(89.5,3,3.5) rot=(0,0,1;0rad)
  Solid = false
  Source = -> Face152
  Symmetric = false
FEATURE [Part::Revolution] Revolve166  label="backCaseScrewRetainer005"
  Angle = 360
  Axis = (0,1,0)
  Base = (0,0,0)
  FaceMakerClass = Part::FaceMakerBullseye
  Placement = pos=(12.5,3,10) rot=(0,0,1;0rad)
  Solid = false
  Source = -> Face150
  Symmetric = false
FEATURE [Part::Revolution] Revolve167  label="moreFrontCaseScrewRetainer006"
  Angle = 360
  Axis = (0,1,0)
  Base = (0,0,0)
  FaceMakerClass = Part::FaceMakerBullseye
  Placement = pos=(109.5,4.5,68.5) rot=(0,0,1;0rad)
  Solid = false
  Source = -> Face153
  Symmetric = false
FEATURE [Part::Revolution] Revolve168  label="moreFrontCaseScrewRetainer007"
  Angle = 360
  Axis = (0,1,0)
  Base = (0,0,0)
  FaceMakerClass = Part::FaceMakerBullseye
  Placement = pos=(109.5,4.5,3.5) rot=(0,0,1;0rad)
  Solid = false
  Source = -> Face154
  Symmetric = false
FEATURE [Part::MultiFuse] Fusion151  label="screwRetainers003"
  Shapes = -> [Revolve168,Revolve167,Revolve166,Revolve165,Revolve164,Revolve163]
FEATURE [Part::Cut] Cut069  label="screwRetainers004"
  Base = -> Fusion151
  Tool = -> Fusion152
FEATURE [Part::Cut] Cut070
  Base = -> Cut069
  Tool = -> Fillet060
FEATURE [Part::Cut] Cut071  label="screwPillars001"
  Base = -> Cut070
  Tool = -> Fillet059
FEATURE [Part::MultiFuse] Fusion153  label="bottom024"
  Shapes = -> [Fusion149,Cut071]
FEATURE [Part::Cylinder] Cylinder067
  Angle = 360
  AttacherType = Attacher::AttachEngine3D
  Height = 10
  Placement = pos=(20.65,12,4.68) rot=(1,0,0;1.5708rad)
  Radius = 2
FEATURE [Part::Cylinder] Cylinder068
  Angle = 360
  AttacherType = Attacher::AttachEngine3D
  Height = 10
  Placement = pos=(20.65,12,67.38) rot=(1,0,0;1.5708rad)
  Radius = 2
FEATURE [Part::Cylinder] Cylinder069
  Angle = 360
  AttacherType = Attacher::AttachEngine3D
  Height = 10
  Placement = pos=(77.15,12,67.38) rot=(1,0,0;1.5708rad)
  Radius = 2
FEATURE [Part::Cylinder] Cylinder070
  Angle = 360
  AttacherType = Attacher::AttachEngine3D
  Height = 10
  Placement = pos=(77.15,12,4.68) rot=(1,0,0;1.5708rad)
  Radius = 2
FEATURE [Part::MultiFuse] Fusion154  label="removeFromThreadedInsertHousing001"
  Shapes = -> [Cylinder069,Cylinder068,Cylinder067,Cylinder070]
FEATURE [Part::Cut] Cut072  label="bottom025"
  Base = -> Fusion153
  Tool = -> Fusion154
FEATURE [Image::ImagePlane] ImagePlane
  XSize = 339
  YSize = 72
FEATURE [Sketcher::SketchObject] Sketch083
  FullyConstrained = true
  MapMode = 5
  Support = -> [XY_Plane]
  sketch-geometry (338):
    g0: LineSegment StartX=-151.619 StartY=28.8932 StartZ=0 EndX=-140.819 EndY=28.8932 EndZ=0
    g1: LineSegment StartX=-151.619 StartY=24.0313 StartZ=0 EndX=-151.619 EndY=28.8932 EndZ=0
    g2: LineSegment StartX=-140.819 StartY=17.7713 StartZ=0 EndX=-151.619 EndY=17.7713 EndZ=0
    g3: LineSegment StartX=-151.619 StartY=17.7713 StartZ=0 EndX=-151.619 EndY=22.6313 EndZ=0
    g4: LineSegment StartX=-151.619 StartY=22.6313 StartZ=0 EndX=-145.128 EndY=22.6313 EndZ=0
    g5: LineSegment StartX=-145.128 StartY=24.0313 StartZ=0 EndX=-140.819 EndY=28.8932 EndZ=0
    g6: LineSegment StartX=-145.128 StartY=22.6313 StartZ=0 EndX=-140.819 EndY=17.7713 EndZ=0
    g7: ArcOfCircle CenterX=-155.157 CenterY=23.3323 CenterZ=0 NormalX=0 NormalY=0 NormalZ=1 AngleXU=0 Radius=6.92354 StartAngle=1.03434 EndAngle=5.24885
    g8: ArcOfCircle CenterX=-155.157 CenterY=23.3323 CenterZ=0 NormalX=0 NormalY=0 NormalZ=1 AngleXU=0 Radius=12.6269 StartAngle=1.28675 EndAngle=4.99643
    g9: LineSegment StartX=-151.619 StartY=35.4532 StartZ=0 EndX=-151.619 EndY=29.2832 EndZ=0
    g10: LineSegment StartX=-151.619 StartY=17.3813 StartZ=0 EndX=-151.619 EndY=11.2113 EndZ=0
    g11-g21: Circle x11 (B-spline internal-alignment scaffolding for g22; pole/knot coordinates omitted)
    g22: BSplineCurve PolesCount=11 KnotsCount=9 Degree=3 IsPeriodic=0
    g23-g31: GeomPoint x9 (B-spline internal-alignment scaffolding for g22; pole/knot coordinates omitted)
    g32-g49: Circle x18 (B-spline internal-alignment scaffolding for g50; pole/knot coordinates omitted)
    g50: BSplineCurve PolesCount=18 KnotsCount=16 Degree=3 IsPeriodic=0
    g51-g66: GeomPoint x16 (B-spline internal-alignment scaffolding for g50; pole/knot coordinates omitted)
    g67: LineSegment StartX=-117.124 StartY=30.093 StartZ=0 EndX=-117.603 EndY=26.5272 EndZ=0
    g68: LineSegment StartX=-117.603 StartY=17.8472 StartZ=0 EndX=-117.124 EndY=14.2659 EndZ=0
    g69: Ellipse CenterX=-109.671 CenterY=20.025 CenterZ=0 NormalX=0 NormalY=0 NormalZ=1 MajorRadius=3.34798 MinorRadius=2.71052 AngleXU=-1.56793
    g70: GeomPoint X=-109.666 Y=18.0598 Z=0
    g71: GeomPoint X=-109.677 Y=21.9902 Z=0
    g72: Ellipse CenterX=-109.671 CenterY=20.0123 CenterZ=0 NormalX=0 NormalY=0 NormalZ=1 MajorRadius=6.93002 MinorRadius=6.36273 AngleXU=-3.13976
    g73: GeomPoint X=-112.417 Y=20.0073 Z=0
    g74: GeomPoint X=-106.925 Y=20.0173 Z=0
    g75: Ellipse CenterX=-51.7682 CenterY=20.1463 CenterZ=0 NormalX=0 NormalY=0 NormalZ=1 MajorRadius=3.19279 MinorRadius=2.71052 AngleXU=-1.52774
    g76: GeomPoint X=-51.6955 Y=18.4606 Z=0
    g77: GeomPoint X=-51.8408 Y=21.832 Z=0
    g78: GeomPoint X=-54.5142 Y=20.1413 Z=0
    g79: GeomPoint X=-49.0221 Y=20.1513 Z=0
    g80: Ellipse CenterX=-51.7682 CenterY=20.1463 CenterZ=0 NormalX=0 NormalY=0 NormalZ=1 MajorRadius=6.93002 MinorRadius=6.36273 AngleXU=-3.13976
    g81: Ellipse CenterX=-22.8436 CenterY=20.1783 CenterZ=0 NormalX=0 NormalY=0 NormalZ=1 MajorRadius=3.31512 MinorRadius=2.71052 AngleXU=-1.60214
    g82: GeomPoint X=-22.9034 Y=18.2706 Z=0
    g83: GeomPoint X=-22.7838 Y=22.0861 Z=0
    g84: GeomPoint X=-25.5897 Y=20.1733 Z=0
    g85: GeomPoint X=-20.0976 Y=20.1833 Z=0
    g86: Ellipse CenterX=-22.8436 CenterY=20.1783 CenterZ=0 NormalX=0 NormalY=0 NormalZ=1 MajorRadius=6.93002 MinorRadius=6.36273 AngleXU=-3.13976
    g87: LineSegment StartX=-101.889 StartY=14.1107 StartZ=0 EndX=-97.7455 EndY=14.1107 EndZ=0
    g88: LineSegment StartX=-93.8155 StartY=14.1107 StartZ=0 EndX=-89.6755 EndY=14.1107 EndZ=0
    g89: LineSegment StartX=-85.7455 StartY=14.1107 StartZ=0 EndX=-81.6055 EndY=14.1107 EndZ=0
    g90: LineSegment StartX=-101.889 StartY=14.1107 StartZ=0 EndX=-101.889 EndY=25.9907 EndZ=0
    g91: LineSegment StartX=-101.889 StartY=25.9907 StartZ=0 EndX=-97.8594 EndY=25.9907 EndZ=0
    g92: LineSegment StartX=-97.8594 StartY=25.9907 StartZ=0 EndX=-97.8594 EndY=24.0907 EndZ=0
    g93: LineSegment StartX=-97.7455 StartY=14.1107 StartZ=0 EndX=-97.7455 EndY=19.9107 EndZ=0
    g94: LineSegment StartX=-89.6755 StartY=14.1107 StartZ=0 EndX=-89.6755 EndY=19.9107 EndZ=0
    g95: LineSegment StartX=-93.8155 StartY=14.1107 StartZ=0 EndX=-93.8155 EndY=21.0107 EndZ=0
    g96-g106: Circle x11 (B-spline internal-alignment scaffolding for g107; pole/knot coordinates omitted)
    g107: BSplineCurve PolesCount=11 KnotsCount=9 Degree=3 IsPeriodic=0
    g108-g116: GeomPoint x9 (B-spline internal-alignment scaffolding for g107; pole/knot coordinates omitted)
    g117: BSplineCurve PolesCount=11 KnotsCount=9 Degree=3 IsPeriodic=0
    g118-g125: Circle x8 (B-spline internal-alignment scaffolding for g126; pole/knot coordinates omitted)
    g126: BSplineCurve PolesCount=8 KnotsCount=6 Degree=3 IsPeriodic=0
    g127-g132: GeomPoint x6 (B-spline internal-alignment scaffolding for g126; pole/knot coordinates omitted)
    g133: BSplineCurve PolesCount=8 KnotsCount=6 Degree=3 IsPeriodic=0
    g134: LineSegment StartX=-85.7455 StartY=21.0107 StartZ=0 EndX=-85.7455 EndY=14.1107 EndZ=0
    g135: LineSegment StartX=-80.0879 StartY=14.1107 StartZ=0 EndX=-75.944 EndY=14.1107 EndZ=0
    g136: LineSegment StartX=-72.014 StartY=14.1107 StartZ=0 EndX=-67.874 EndY=14.1107 EndZ=0
    g137: LineSegment StartX=-63.944 StartY=14.1107 StartZ=0 EndX=-59.804 EndY=14.1107 EndZ=0
    g138: LineSegment StartX=-80.0879 StartY=14.1107 StartZ=0 EndX=-80.0879 EndY=25.9907 EndZ=0
    g139: LineSegment StartX=-80.0879 StartY=25.9907 StartZ=0 EndX=-76.0579 EndY=25.9907 EndZ=0
    g140: LineSegment StartX=-76.0579 StartY=25.9907 StartZ=0 EndX=-76.0579 EndY=24.0907 EndZ=0
    g141: LineSegment StartX=-75.944 StartY=14.1107 StartZ=0 EndX=-75.944 EndY=19.9107 EndZ=0
    g142: LineSegment StartX=-67.874 StartY=14.1107 StartZ=0 EndX=-67.874 EndY=19.9107 EndZ=0
    g143: LineSegment StartX=-72.014 StartY=14.1107 StartZ=0 EndX=-72.014 EndY=21.0107 EndZ=0
    g144-g148: Circle x5 (B-spline internal-alignment scaffolding for g149; pole/knot coordinates omitted)
    g149: BSplineCurve PolesCount=11 KnotsCount=9 Degree=3 IsPeriodic=0
    g150-g158: GeomPoint x9 (B-spline internal-alignment scaffolding for g149; pole/knot coordinates omitted)
    g159: BSplineCurve PolesCount=11 KnotsCount=9 Degree=3 IsPeriodic=0
    g160-g167: Circle x8 (B-spline internal-alignment scaffolding for g168; pole/knot coordinates omitted)
    g168: BSplineCurve PolesCount=8 KnotsCount=6 Degree=3 IsPeriodic=0
    g169-g174: GeomPoint x6 (B-spline internal-alignment scaffolding for g168; pole/knot coordinates omitted)
    g175: BSplineCurve PolesCount=8 KnotsCount=6 Degree=3 IsPeriodic=0
    g176: LineSegment StartX=-63.944 StartY=21.0107 StartZ=0 EndX=-63.944 EndY=14.1107 EndZ=0
    g177: LineSegment StartX=-59.804 StartY=14.1107 StartZ=0 EndX=-59.804 EndY=21.5868 EndZ=0
    g178: BSplineCurve PolesCount=4 KnotsCount=2 Degree=3 IsPeriodic=0
    g179: GeomPoint X=-59.804 Y=21.5868 Z=0
    g180: GeomPoint X=-60.2379 Y=24.0907 Z=0
    g181: LineSegment StartX=-81.6055 StartY=14.1107 StartZ=0 EndX=-81.6055 EndY=21.5868 EndZ=0
    g182: LineSegment StartX=-151.619 StartY=24.0313 StartZ=0 EndX=-145.128 EndY=24.0313 EndZ=0
    g183: Circle CenterX=-82.0394 CenterY=24.0907 CenterZ=0 NormalX=0 NormalY=0 NormalZ=1 AngleXU=0 Radius=1
    g184: Circle CenterX=-81.7131 CenterY=23.2736 CenterZ=0 NormalX=0 NormalY=0 NormalZ=1 AngleXU=0 Radius=1
    g185: Circle CenterX=-81.6055 CenterY=21.5868 CenterZ=0 NormalX=0 NormalY=0 NormalZ=1 AngleXU=0 Radius=1
    g186: BSplineCurve PolesCount=3 KnotsCount=2 Degree=2 IsPeriodic=0
    g187: GeomPoint X=-82.0394 Y=24.0907 Z=0
    g188: GeomPoint X=-81.6055 Y=21.5868 Z=0
    g189: Ellipse CenterX=-37.3522 CenterY=19.9515 CenterZ=0 NormalX=0 NormalY=0 NormalZ=1 MajorRadius=2.99755 MinorRadius=2.49 AngleXU=1.5708
    g190: GeomPoint X=-37.3522 Y=21.6203 Z=0
    g191: GeomPoint X=-37.3522 Y=18.2826 Z=0
    g192: ArcOfEllipse CenterX=-38.7647 CenterY=20.06 CenterZ=0 NormalX=0 NormalY=0 NormalZ=1 MajorRadius=6.30025 MinorRadius=5.3849 AngleXU=1.57276 StartAngle=5.50632 EndAngle=10.3035
    g193: GeomPoint X=-38.7711 Y=23.3304 Z=0
    g194: GeomPoint X=-38.7583 Y=16.7895 Z=0
    g195: LineSegment StartX=-34.6109 StartY=14.1107 StartZ=0 EndX=-30.8984 EndY=14.1107 EndZ=0
    g196: LineSegment StartX=-30.8984 StartY=14.1107 StartZ=0 EndX=-30.8984 EndY=31.1784 EndZ=0
    g197: LineSegment StartX=-30.8984 StartY=31.1784 StartZ=0 EndX=-34.9984 EndY=31.1784 EndZ=0
    g198: LineSegment StartX=-34.9984 StartY=24.5602 StartZ=0 EndX=-34.9984 EndY=31.1784 EndZ=0
    g199: LineSegment StartX=-34.6109 StartY=16.0476 StartZ=0 EndX=-34.6109 EndY=14.1107 EndZ=0
    g200: LineSegment StartX=-14.8781 StartY=14.1107 StartZ=0 EndX=-10.5106 EndY=14.1107 EndZ=0
    g201: LineSegment StartX=-14.8781 StartY=14.1107 StartZ=0 EndX=-14.8781 EndY=25.8504 EndZ=0
    g202: LineSegment StartX=-14.8781 StartY=25.8504 StartZ=0 EndX=-10.8534 EndY=25.8504 EndZ=0
    g203: LineSegment StartX=-10.8534 StartY=25.8504 StartZ=0 EndX=-10.8534 EndY=24.0923 EndZ=0
    g204: LineSegment StartX=-10.5106 StartY=14.1107 StartZ=0 EndX=-10.5106 EndY=19.7752 EndZ=0
    g205: LineSegment StartX=-5.96397 StartY=25.9304 StartZ=0 EndX=-5.96397 EndY=22.574 EndZ=0
    g206-g214: Circle x9 (B-spline internal-alignment scaffolding for g215; pole/knot coordinates omitted)
    g215: BSplineCurve PolesCount=9 KnotsCount=7 Degree=3 IsPeriodic=0
    g216-g222: GeomPoint x7 (B-spline internal-alignment scaffolding for g215; pole/knot coordinates omitted)
    g223-g232: Circle x10 (B-spline internal-alignment scaffolding for g233; pole/knot coordinates omitted)
    g233: BSplineCurve PolesCount=10 KnotsCount=8 Degree=3 IsPeriodic=0
    g234-g241: GeomPoint x8 (B-spline internal-alignment scaffolding for g233; pole/knot coordinates omitted)
    g242: LineSegment StartX=-1.58923 StartY=21.0696 StartZ=0 EndX=2.62034 EndY=21.0696 EndZ=0
    g243: LineSegment StartX=-1.55856 StartY=18.7342 StartZ=0 EndX=6.45946 EndY=18.7342 EndZ=0
    g244: LineSegment StartX=5.29231 StartY=17.386 StartZ=0 EndX=5.29231 EndY=14.3674 EndZ=0
    g245-g269: Circle x25 (B-spline internal-alignment scaffolding for g270; pole/knot coordinates omitted)
    g270: BSplineCurve PolesCount=25 KnotsCount=23 Degree=3 IsPeriodic=0
    g271-g293: GeomPoint x23 (B-spline internal-alignment scaffolding for g270; pole/knot coordinates omitted)
    g294-g304: Circle x11 (B-spline internal-alignment scaffolding for g305; pole/knot coordinates omitted)
    g305: BSplineCurve PolesCount=11 KnotsCount=9 Degree=3 IsPeriodic=0
    g306-g314: GeomPoint x9 (B-spline internal-alignment scaffolding for g305; pole/knot coordinates omitted)
    g315-g326: Circle x12 (B-spline internal-alignment scaffolding for g327; pole/knot coordinates omitted)
    g327: BSplineCurve PolesCount=12 KnotsCount=10 Degree=3 IsPeriodic=0
    g328-g337: GeomPoint x10 (B-spline internal-alignment scaffolding for g327; pole/knot coordinates omitted)
  constraints (252):
    c: Coincident(g1,g0)
    c: Horizontal(g0)
    c: Vertical(g1)
    c: Coincident(g2,g3)
    c: Coincident(g3,g4)
    c: Horizontal(g4)
    c: Horizontal(g2)
    c: Vertical(g3)
    c: Block(g1)
    c: Distance(g3) = 4.86
    c: Block(g4)
    c: Distance(g0) = 10.8
    c: Distance(g2) = 10.8
    c: Coincident(g5,g0)
    c: Coincident(g6,g4)
    c: Coincident(g6,g2)
    c: Block(g8)
    c: Block(g7)
    c: Coincident(g9,g8)
    c: Coincident(g9,g7)
    c: Vertical(g9)
    c: Coincident(g10,g7)
    c: Coincident(g10,g8)
    c: Vertical(g10)
    c: Weight(g11) = 1
    c: Equal(g11, g12-g21) x10
    c: InternalAlignment(g11-g21 -> g22) x11
    c: InternalAlignment(g23-g31 -> g22) x9
    c: Block(g22)
    c: Weight(g32) = 1
    c: Equal(g32, g33-g49) x17
    c: InternalAlignment(g32-g49 -> g50) x18
    c: InternalAlignment(g51-g66 -> g50) x16
    c: Block(g50)
    c: Coincident(g67,g50)
    c: Coincident(g67,g22)
    c: Coincident(g68,g22)
    c: Coincident(g68,g50)
    c: InternalAlignment(g70,g69)
    c: InternalAlignment(g71,g69)
    c: Block(g69)
    c: InternalAlignment(g73,g72)
    c: InternalAlignment(g74,g72)
    c: Block(g72)
    c: InternalAlignment(g76,g75)
    c: InternalAlignment(g77,g75)
    c: InternalAlignment(g78,g80)
    c: InternalAlignment(g79,g80)
    c: Block(g80)
    c: Coincident(g75,g80)
    c: Block(g75)
    c: InternalAlignment(g82,g81)
    c: InternalAlignment(g83,g81)
    c: InternalAlignment(g84,g86)
    c: InternalAlignment(g85,g86)
    c: Block(g86)
    c: Coincident(g81,g86)
    c: Block(g81)
    c: Horizontal(g87)
    c: Block(g87)
    c: Horizontal(g88)
    c: Distance(g88) = 4.14
    c: Horizontal(g89)
    c: Equal(g88,g89) = 4.14
    c: Block(g89)
    c: Block(g88)
    c: Coincident(g90,g87)
    c: Vertical(g90)
    c: Distance(g90) = 11.88
    c: Coincident(g91,g90)
    c: Horizontal(g91)
    c: Coincident(g92,g91)
    c: Vertical(g92)
    c: Distance(g91) = 4.03
    c: Distance(g92) = 1.9
    c: Coincident(g93,g87)
    c: Vertical(g93)
    c: Vertical(g94)
    c: Coincident(g94,g88)
    c: Distance(g93) = 5.8
    c: Distance(g94) = 5.8
    c: Vertical(g95)
    c: Coincident(g95,g88)
    c: Distance(g95) = 6.9
    c: Coincident(g107,g92)
    c: Weight(g96) = 1
    c: Equal(g96, g97-g106) x10
    c: InternalAlignment(g96-g106 -> g107) x11
    c: InternalAlignment(g108-g116 -> g107) x9
    c: Block(g107)
    c: Block(g117)
    c: Coincident(g126,g93)
    c: Weight(g118) = 1
    c: Equal(g118, g119-g125) x7
    c: Coincident(g126,g95)
    c: InternalAlignment(g118-g125 -> g126) x8
    c: InternalAlignment(g127-g132 -> g126) x6
    c: Coincident(g133,g94)
    c: Block(g126)
    c: Block(g133)
    c: Coincident(g134,g133)
    c: Coincident(g134,g89)
    c: Vertical(g134)
    c: Horizontal(g135)
    c: Block(g135)
    c: Horizontal(g136)
    c: Equal(g88,g136) = 4.14
    c: Horizontal(g137)
    c: Equal(g136,g137) = 4.14
    c: Block(g137)
    c: Block(g136)
    c: Coincident(g138,g135)
    c: Vertical(g138)
    c: Equal(g90,g138) = 11.88
    c: Coincident(g139,g138)
    c: Horizontal(g139)
    c: Coincident(g140,g139)
    c: Vertical(g140)
    c: Equal(g91,g139) = 4.03
    c: Equal(g92,g140) = 1.9
    c: Coincident(g141,g135)
    c: Vertical(g141)
    c: Vertical(g142)
    c: Coincident(g142,g136)
    c: Equal(g93,g141) = 5.8
    c: Equal(g94,g142) = 5.8
    c: Vertical(g143)
    c: Coincident(g143,g136)
    c: Equal(g95,g143) = 6.9
    c: Coincident(g149,g140)
    c: Equal(g96,g144) = 1
    c: Equal(g144, g145-g148) x4
    c: InternalAlignment(g144-g148 -> g149) x5
    c: InternalAlignment(g150-g158 -> g149) x9
    c: Block(g149)
    c: Block(g159)
    c: Coincident(g168,g141)
    c: Equal(g118,g160) = 1
    c: Equal(g160, g161-g167) x7
    c: Coincident(g168,g143)
    c: InternalAlignment(g160-g167 -> g168) x8
    c: InternalAlignment(g169-g174 -> g168) x6
    c: Coincident(g175,g142)
    c: Block(g168)
    c: Block(g175)
    c: Coincident(g176,g175)
    c: Coincident(g176,g137)
    c: Vertical(g176)
    c: Coincident(g177,g137)
    c: Vertical(g177)
    c: Coincident(g178,g177)
    c: Coincident(g178,g159)
    c: InternalAlignment(g179,g178)
    c: InternalAlignment(g180,g178)
    c: Block(g178)
    c: Vertical(g181)
    c: Coincident(g181,g89)
    c: Block(g5)
    c: Coincident(g182,g1)
    c: Coincident(g182,g5)
    c: Horizontal(g182)
    c: Coincident(g186,g117)
    c: Weight(g183) = 1
    c: Equal(g183,g184)
    c: Equal(g183,g185)
    c: Coincident(g186,g181)
    c: InternalAlignment(g183,g186)
    c: InternalAlignment(g184,g186)
    c: InternalAlignment(g185,g186)
    c: InternalAlignment(g187,g186)
    c: InternalAlignment(g188,g186)
    c: Block(g186)
    c: InternalAlignment(g190,g189)
    c: InternalAlignment(g191,g189)
    c: Block(g189)
    c: InternalAlignment(g193,g192)
    c: InternalAlignment(g194,g192)
    c: Block(g192)
    c: Horizontal(g195)
    c: Block(g195)
    c: Coincident(g196,g195)
    c: Vertical(g196)
    c: Block(g196)
    c: Distance(g195) = 3.71244
    c: Coincident(g197,g196)
    c: Horizontal(g197)
    c: Distance(g197) = 4.1
    c: Coincident(g198,g192)
    c: Coincident(g198,g197)
    c: Vertical(g198)
    c: Block(g198)
    c: Coincident(g199,g192)
    c: Coincident(g199,g195)
    c: Vertical(g199)
    c: Block(g199)
    c: Horizontal(g200)
    c: Block(g200)
    c: Coincident(g201,g200)
    c: Vertical(g201)
    c: Block(g201)
    c: Coincident(g202,g201)
    c: Horizontal(g202)
    c: Block(g202)
    c: Coincident(g203,g202)
    c: Vertical(g203)
    c: Block(g203)
    c: Coincident(g204,g200)
    c: Vertical(g204)
    c: Block(g204)
    c: Coincident(g215,g203)
    c: Weight(g206) = 1
    c: Equal(g206, g207-g214) x8
    c: Coincident(g215,g205)
    c: InternalAlignment(g206-g214 -> g215) x9
    c: InternalAlignment(g216-g222 -> g215) x7
    c: Coincident(g233,g204)
    c: Weight(g223) = 1
    c: Equal(g223, g224-g232) x9
    c: Coincident(g233,g205)
    c: InternalAlignment(g223-g232 -> g233) x10
    c: InternalAlignment(g234-g241 -> g233) x8
    c: Vertical(g205)
    c: Block(g205)
    c: Block(g215)
    c: Block(g233)
    c: Horizontal(g242)
    c: Horizontal(g243)
    c: Block(g242)
    c: Block(g243)
    c: Vertical(g244)
    c: Block(g244)
    c: Coincident(g270,g243)
    c: Weight(g245) = 1
    c: Equal(g245, g246-g269) x24
    c: Coincident(g270,g244)
    c: InternalAlignment(g245-g269 -> g270) x25
    c: InternalAlignment(g271-g293 -> g270) x23
    c: Coincident(g305,g242)
    c: Weight(g294) = 1
    c: Equal(g294, g295-g304) x10
    c: Coincident(g305,g242)
    c: InternalAlignment(g294-g304 -> g305) x11
    c: InternalAlignment(g306-g314 -> g305) x9
    c: Block(g305)
    c: Coincident(g327,g243)
    c: Weight(g315) = 1
    c: Equal(g315, g316-g326) x11
    c: Coincident(g327,g244)
    c: InternalAlignment(g315-g326 -> g327) x12
    c: InternalAlignment(g328-g337 -> g327) x10
    c: Block(g327)
    c: Block(g270)
FEATURE [PartDesign::Body] Body  label="CommodoreLogoAndText"
  Group = -> [Sketch083]
  Origin = -> Origin
FEATURE [Part::Extrusion] Extrude074  label="CommodoreLogoAndText001"
  Base = -> Sketch083
  Dir = (0,0,1)
  DirMode = 2
  FaceMakerClass = Part::FaceMakerBullseye
  LengthFwd = 10
  LengthRev = 0
  Solid = true
  Symmetric = false
FEATURE [Part::FeaturePython] Clone  label="CommodoreLogoAndTextScale"  # Draft clone (typed FeaturePython)
  AttacherType = Attacher::AttachEngine3D
  Fuse = false
  Objects = -> [Extrude074]
  Placement = pos=(111,5.37,-11.6) rot=(0,0,1;0rad)
  Scale = (0.62,0.62,1)
FEATURE [Part::Mirroring] Part__Mirroring  label="CommodoreLogoAndTextScale (Mirror #1)"
  Base = (0,0,0)
  Normal = (1,0,0)
  Placement = pos=(123.576,0,0) rot=(0,0,1;0rad)
  Source = -> Clone
FEATURE [Sketcher::SketchObject] Sketch084
  FullyConstrained = true
  MapMode = 5
  Support = -> [XY_Plane001]
  sketch-geometry (338):
    g0: LineSegment StartX=-151.619 StartY=28.8932 StartZ=0 EndX=-140.819 EndY=28.8932 EndZ=0
    g1: LineSegment StartX=-151.619 StartY=24.0313 StartZ=0 EndX=-151.619 EndY=28.8932 EndZ=0
    g2: LineSegment StartX=-140.819 StartY=17.7713 StartZ=0 EndX=-151.619 EndY=17.7713 EndZ=0
    g3: LineSegment StartX=-151.619 StartY=17.7713 StartZ=0 EndX=-151.619 EndY=22.6313 EndZ=0
    g4: LineSegment StartX=-151.619 StartY=22.6313 StartZ=0 EndX=-145.128 EndY=22.6313 EndZ=0
    g5: LineSegment StartX=-145.128 StartY=24.0313 StartZ=0 EndX=-140.819 EndY=28.8932 EndZ=0
    g6: LineSegment StartX=-145.128 StartY=22.6313 StartZ=0 EndX=-140.819 EndY=17.7713 EndZ=0
    g7: ArcOfCircle CenterX=-155.157 CenterY=23.3323 CenterZ=0 NormalX=0 NormalY=0 NormalZ=1 AngleXU=0 Radius=6.92354 StartAngle=1.03434 EndAngle=5.24885
    g8: ArcOfCircle CenterX=-155.157 CenterY=23.3323 CenterZ=0 NormalX=0 NormalY=0 NormalZ=1 AngleXU=0 Radius=12.6269 StartAngle=1.28675 EndAngle=4.99643
    g9: LineSegment StartX=-151.619 StartY=35.4532 StartZ=0 EndX=-151.619 EndY=29.2832 EndZ=0
    g10: LineSegment StartX=-151.619 StartY=17.3813 StartZ=0 EndX=-151.619 EndY=11.2113 EndZ=0
    g11-g21: Circle x11 (B-spline internal-alignment scaffolding for g22; pole/knot coordinates omitted)
    g22: BSplineCurve PolesCount=11 KnotsCount=9 Degree=3 IsPeriodic=0
    g23-g31: GeomPoint x9 (B-spline internal-alignment scaffolding for g22; pole/knot coordinates omitted)
    g32-g49: Circle x18 (B-spline internal-alignment scaffolding for g50; pole/knot coordinates omitted)
    g50: BSplineCurve PolesCount=18 KnotsCount=16 Degree=3 IsPeriodic=0
    g51-g66: GeomPoint x16 (B-spline internal-alignment scaffolding for g50; pole/knot coordinates omitted)
    g67: LineSegment StartX=-117.124 StartY=30.093 StartZ=0 EndX=-117.603 EndY=26.5272 EndZ=0
    g68: LineSegment StartX=-117.603 StartY=17.8472 StartZ=0 EndX=-117.124 EndY=14.2659 EndZ=0
    g69: Ellipse CenterX=-109.671 CenterY=20.025 CenterZ=0 NormalX=0 NormalY=0 NormalZ=1 MajorRadius=3.34798 MinorRadius=2.71052 AngleXU=-1.56793
    g70: GeomPoint X=-109.666 Y=18.0598 Z=0
    g71: GeomPoint X=-109.677 Y=21.9902 Z=0
    g72: Ellipse CenterX=-109.671 CenterY=20.0123 CenterZ=0 NormalX=0 NormalY=0 NormalZ=1 MajorRadius=6.93002 MinorRadius=6.36273 AngleXU=-3.13976
    g73: GeomPoint X=-112.417 Y=20.0073 Z=0
    g74: GeomPoint X=-106.925 Y=20.0173 Z=0
    g75: Ellipse CenterX=-51.7682 CenterY=20.1463 CenterZ=0 NormalX=0 NormalY=0 NormalZ=1 MajorRadius=3.19279 MinorRadius=2.71052 AngleXU=-1.52774
    g76: GeomPoint X=-51.6955 Y=18.4606 Z=0
    g77: GeomPoint X=-51.8408 Y=21.832 Z=0
    g78: GeomPoint X=-54.5142 Y=20.1413 Z=0
    g79: GeomPoint X=-49.0221 Y=20.1513 Z=0
    g80: Ellipse CenterX=-51.7682 CenterY=20.1463 CenterZ=0 NormalX=0 NormalY=0 NormalZ=1 MajorRadius=6.93002 MinorRadius=6.36273 AngleXU=-3.13976
    g81: Ellipse CenterX=-22.8436 CenterY=20.1783 CenterZ=0 NormalX=0 NormalY=0 NormalZ=1 MajorRadius=3.31512 MinorRadius=2.71052 AngleXU=-1.60214
    g82: GeomPoint X=-22.9034 Y=18.2706 Z=0
    g83: GeomPoint X=-22.7838 Y=22.0861 Z=0
    g84: GeomPoint X=-25.5897 Y=20.1733 Z=0
    g85: GeomPoint X=-20.0976 Y=20.1833 Z=0
    g86: Ellipse CenterX=-22.8436 CenterY=20.1783 CenterZ=0 NormalX=0 NormalY=0 NormalZ=1 MajorRadius=6.93002 MinorRadius=6.36273 AngleXU=-3.13976
    g87: LineSegment StartX=-101.889 StartY=14.1107 StartZ=0 EndX=-97.7455 EndY=14.1107 EndZ=0
    g88: LineSegment StartX=-93.8155 StartY=14.1107 StartZ=0 EndX=-89.6755 EndY=14.1107 EndZ=0
    g89: LineSegment StartX=-85.7455 StartY=14.1107 StartZ=0 EndX=-81.6055 EndY=14.1107 EndZ=0
    g90: LineSegment StartX=-101.889 StartY=14.1107 StartZ=0 EndX=-101.889 EndY=25.9907 EndZ=0
    g91: LineSegment StartX=-101.889 StartY=25.9907 StartZ=0 EndX=-97.8594 EndY=25.9907 EndZ=0
    g92: LineSegment StartX=-97.8594 StartY=25.9907 StartZ=0 EndX=-97.8594 EndY=24.0907 EndZ=0
    g93: LineSegment StartX=-97.7455 StartY=14.1107 StartZ=0 EndX=-97.7455 EndY=19.9107 EndZ=0
    g94: LineSegment StartX=-89.6755 StartY=14.1107 StartZ=0 EndX=-89.6755 EndY=19.9107 EndZ=0
    g95: LineSegment StartX=-93.8155 StartY=14.1107 StartZ=0 EndX=-93.8155 EndY=21.0107 EndZ=0
    g96-g106: Circle x11 (B-spline internal-alignment scaffolding for g107; pole/knot coordinates omitted)
    g107: BSplineCurve PolesCount=11 KnotsCount=9 Degree=3 IsPeriodic=0
    g108-g116: GeomPoint x9 (B-spline internal-alignment scaffolding for g107; pole/knot coordinates omitted)
    g117: BSplineCurve PolesCount=11 KnotsCount=9 Degree=3 IsPeriodic=0
    g118-g125: Circle x8 (B-spline internal-alignment scaffolding for g126; pole/knot coordinates omitted)
    g126: BSplineCurve PolesCount=8 KnotsCount=6 Degree=3 IsPeriodic=0
    g127-g132: GeomPoint x6 (B-spline internal-alignment scaffolding for g126; pole/knot coordinates omitted)
    g133: BSplineCurve PolesCount=8 KnotsCount=6 Degree=3 IsPeriodic=0
    g134: LineSegment StartX=-85.7455 StartY=21.0107 StartZ=0 EndX=-85.7455 EndY=14.1107 EndZ=0
    g135: LineSegment StartX=-80.0879 StartY=14.1107 StartZ=0 EndX=-75.944 EndY=14.1107 EndZ=0
    g136: LineSegment StartX=-72.014 StartY=14.1107 StartZ=0 EndX=-67.874 EndY=14.1107 EndZ=0
    g137: LineSegment StartX=-63.944 StartY=14.1107 StartZ=0 EndX=-59.804 EndY=14.1107 EndZ=0
    g138: LineSegment StartX=-80.0879 StartY=14.1107 StartZ=0 EndX=-80.0879 EndY=25.9907 EndZ=0
    g139: LineSegment StartX=-80.0879 StartY=25.9907 StartZ=0 EndX=-76.0579 EndY=25.9907 EndZ=0
    g140: LineSegment StartX=-76.0579 StartY=25.9907 StartZ=0 EndX=-76.0579 EndY=24.0907 EndZ=0
    g141: LineSegment StartX=-75.944 StartY=14.1107 StartZ=0 EndX=-75.944 EndY=19.9107 EndZ=0
    g142: LineSegment StartX=-67.874 StartY=14.1107 StartZ=0 EndX=-67.874 EndY=19.9107 EndZ=0
    g143: LineSegment StartX=-72.014 StartY=14.1107 StartZ=0 EndX=-72.014 EndY=21.0107 EndZ=0
    g144-g148: Circle x5 (B-spline internal-alignment scaffolding for g149; pole/knot coordinates omitted)
    g149: BSplineCurve PolesCount=11 KnotsCount=9 Degree=3 IsPeriodic=0
    g150-g158: GeomPoint x9 (B-spline internal-alignment scaffolding for g149; pole/knot coordinates omitted)
    g159: BSplineCurve PolesCount=11 KnotsCount=9 Degree=3 IsPeriodic=0
    g160-g167: Circle x8 (B-spline internal-alignment scaffolding for g168; pole/knot coordinates omitted)
    g168: BSplineCurve PolesCount=8 KnotsCount=6 Degree=3 IsPeriodic=0
    g169-g174: GeomPoint x6 (B-spline internal-alignment scaffolding for g168; pole/knot coordinates omitted)
    g175: BSplineCurve PolesCount=8 KnotsCount=6 Degree=3 IsPeriodic=0
    g176: LineSegment StartX=-63.944 StartY=21.0107 StartZ=0 EndX=-63.944 EndY=14.1107 EndZ=0
    g177: LineSegment StartX=-59.804 StartY=14.1107 StartZ=0 EndX=-59.804 EndY=21.5868 EndZ=0
    g178: BSplineCurve PolesCount=4 KnotsCount=2 Degree=3 IsPeriodic=0
    g179: GeomPoint X=-59.804 Y=21.5868 Z=0
    g180: GeomPoint X=-60.2379 Y=24.0907 Z=0
    g181: LineSegment StartX=-81.6055 StartY=14.1107 StartZ=0 EndX=-81.6055 EndY=21.5868 EndZ=0
    g182: LineSegment StartX=-151.619 StartY=24.0313 StartZ=0 EndX=-145.128 EndY=24.0313 EndZ=0
    g183: Circle CenterX=-82.0394 CenterY=24.0907 CenterZ=0 NormalX=0 NormalY=0 NormalZ=1 AngleXU=0 Radius=1
    g184: Circle CenterX=-81.7131 CenterY=23.2736 CenterZ=0 NormalX=0 NormalY=0 NormalZ=1 AngleXU=0 Radius=1
    g185: Circle CenterX=-81.6055 CenterY=21.5868 CenterZ=0 NormalX=0 NormalY=0 NormalZ=1 AngleXU=0 Radius=1
    g186: BSplineCurve PolesCount=3 KnotsCount=2 Degree=2 IsPeriodic=0
    g187: GeomPoint X=-82.0394 Y=24.0907 Z=0
    g188: GeomPoint X=-81.6055 Y=21.5868 Z=0
    g189: Ellipse CenterX=-37.3522 CenterY=19.9515 CenterZ=0 NormalX=0 NormalY=0 NormalZ=1 MajorRadius=2.99755 MinorRadius=2.49 AngleXU=1.5708
    g190: GeomPoint X=-37.3522 Y=21.6203 Z=0
    g191: GeomPoint X=-37.3522 Y=18.2826 Z=0
    g192: ArcOfEllipse CenterX=-38.7647 CenterY=20.06 CenterZ=0 NormalX=0 NormalY=0 NormalZ=1 MajorRadius=6.30025 MinorRadius=5.3849 AngleXU=1.57276 StartAngle=5.50632 EndAngle=10.3035
    g193: GeomPoint X=-38.7711 Y=23.3304 Z=0
    g194: GeomPoint X=-38.7583 Y=16.7895 Z=0
    g195: LineSegment StartX=-34.6109 StartY=14.1107 StartZ=0 EndX=-30.8984 EndY=14.1107 EndZ=0
    g196: LineSegment StartX=-30.8984 StartY=14.1107 StartZ=0 EndX=-30.8984 EndY=31.1784 EndZ=0
    g197: LineSegment StartX=-30.8984 StartY=31.1784 StartZ=0 EndX=-34.9984 EndY=31.1784 EndZ=0
    g198: LineSegment StartX=-34.9984 StartY=24.5602 StartZ=0 EndX=-34.9984 EndY=31.1784 EndZ=0
    g199: LineSegment StartX=-34.6109 StartY=16.0476 StartZ=0 EndX=-34.6109 EndY=14.1107 EndZ=0
    g200: LineSegment StartX=-14.8781 StartY=14.1107 StartZ=0 EndX=-10.5106 EndY=14.1107 EndZ=0
    g201: LineSegment StartX=-14.8781 StartY=14.1107 StartZ=0 EndX=-14.8781 EndY=25.8504 EndZ=0
    g202: LineSegment StartX=-14.8781 StartY=25.8504 StartZ=0 EndX=-10.8534 EndY=25.8504 EndZ=0
    g203: LineSegment StartX=-10.8534 StartY=25.8504 StartZ=0 EndX=-10.8534 EndY=24.0923 EndZ=0
    g204: LineSegment StartX=-10.5106 StartY=14.1107 StartZ=0 EndX=-10.5106 EndY=19.7752 EndZ=0
    g205: LineSegment StartX=-5.96397 StartY=25.9304 StartZ=0 EndX=-5.96397 EndY=22.574 EndZ=0
    g206-g214: Circle x9 (B-spline internal-alignment scaffolding for g215; pole/knot coordinates omitted)
    g215: BSplineCurve PolesCount=9 KnotsCount=7 Degree=3 IsPeriodic=0
    g216-g222: GeomPoint x7 (B-spline internal-alignment scaffolding for g215; pole/knot coordinates omitted)
    g223-g232: Circle x10 (B-spline internal-alignment scaffolding for g233; pole/knot coordinates omitted)
    g233: BSplineCurve PolesCount=10 KnotsCount=8 Degree=3 IsPeriodic=0
    g234-g241: GeomPoint x8 (B-spline internal-alignment scaffolding for g233; pole/knot coordinates omitted)
    g242: LineSegment StartX=-1.58923 StartY=21.0696 StartZ=0 EndX=2.62034 EndY=21.0696 EndZ=0
    g243: LineSegment StartX=-1.55856 StartY=18.7342 StartZ=0 EndX=6.45946 EndY=18.7342 EndZ=0
    g244: LineSegment StartX=5.29231 StartY=17.386 StartZ=0 EndX=5.29231 EndY=14.3674 EndZ=0
    g245-g269: Circle x25 (B-spline internal-alignment scaffolding for g270; pole/knot coordinates omitted)
    g270: BSplineCurve PolesCount=25 KnotsCount=23 Degree=3 IsPeriodic=0
    g271-g293: GeomPoint x23 (B-spline internal-alignment scaffolding for g270; pole/knot coordinates omitted)
    g294-g304: Circle x11 (B-spline internal-alignment scaffolding for g305; pole/knot coordinates omitted)
    g305: BSplineCurve PolesCount=11 KnotsCount=9 Degree=3 IsPeriodic=0
    g306-g314: GeomPoint x9 (B-spline internal-alignment scaffolding for g305; pole/knot coordinates omitted)
    g315-g326: Circle x12 (B-spline internal-alignment scaffolding for g327; pole/knot coordinates omitted)
    g327: BSplineCurve PolesCount=12 KnotsCount=10 Degree=3 IsPeriodic=0
    g328-g337: GeomPoint x10 (B-spline internal-alignment scaffolding for g327; pole/knot coordinates omitted)
  constraints (252):
    c: Coincident(g1,g0)
    c: Horizontal(g0)
    c: Vertical(g1)
    c: Coincident(g2,g3)
    c: Coincident(g3,g4)
    c: Horizontal(g4)
    c: Horizontal(g2)
    c: Vertical(g3)
    c: Block(g1)
    c: Distance(g3) = 4.86
    c: Block(g4)
    c: Distance(g0) = 10.8
    c: Distance(g2) = 10.8
    c: Coincident(g5,g0)
    c: Coincident(g6,g4)
    c: Coincident(g6,g2)
    c: Block(g8)
    c: Block(g7)
    c: Coincident(g9,g8)
    c: Coincident(g9,g7)
    c: Vertical(g9)
    c: Coincident(g10,g7)
    c: Coincident(g10,g8)
    c: Vertical(g10)
    c: Weight(g11) = 1
    c: Equal(g11, g12-g21) x10
    c: InternalAlignment(g11-g21 -> g22) x11
    c: InternalAlignment(g23-g31 -> g22) x9
    c: Block(g22)
    c: Weight(g32) = 1
    c: Equal(g32, g33-g49) x17
    c: InternalAlignment(g32-g49 -> g50) x18
    c: InternalAlignment(g51-g66 -> g50) x16
    c: Block(g50)
    c: Coincident(g67,g50)
    c: Coincident(g67,g22)
    c: Coincident(g68,g22)
    c: Coincident(g68,g50)
    c: InternalAlignment(g70,g69)
    c: InternalAlignment(g71,g69)
    c: Block(g69)
    c: InternalAlignment(g73,g72)
    c: InternalAlignment(g74,g72)
    c: Block(g72)
    c: InternalAlignment(g76,g75)
    c: InternalAlignment(g77,g75)
    c: InternalAlignment(g78,g80)
    c: InternalAlignment(g79,g80)
    c: Block(g80)
    c: Coincident(g75,g80)
    c: Block(g75)
    c: InternalAlignment(g82,g81)
    c: InternalAlignment(g83,g81)
    c: InternalAlignment(g84,g86)
    c: InternalAlignment(g85,g86)
    c: Block(g86)
    c: Coincident(g81,g86)
    c: Block(g81)
    c: Horizontal(g87)
    c: Block(g87)
    c: Horizontal(g88)
    c: Distance(g88) = 4.14
    c: Horizontal(g89)
    c: Equal(g88,g89) = 4.14
    c: Block(g89)
    c: Block(g88)
    c: Coincident(g90,g87)
    c: Vertical(g90)
    c: Distance(g90) = 11.88
    c: Coincident(g91,g90)
    c: Horizontal(g91)
    c: Coincident(g92,g91)
    c: Vertical(g92)
    c: Distance(g91) = 4.03
    c: Distance(g92) = 1.9
    c: Coincident(g93,g87)
    c: Vertical(g93)
    c: Vertical(g94)
    c: Coincident(g94,g88)
    c: Distance(g93) = 5.8
    c: Distance(g94) = 5.8
    c: Vertical(g95)
    c: Coincident(g95,g88)
    c: Distance(g95) = 6.9
    c: Coincident(g107,g92)
    c: Weight(g96) = 1
    c: Equal(g96, g97-g106) x10
    c: InternalAlignment(g96-g106 -> g107) x11
    c: InternalAlignment(g108-g116 -> g107) x9
    c: Block(g107)
    c: Block(g117)
    c: Coincident(g126,g93)
    c: Weight(g118) = 1
    c: Equal(g118, g119-g125) x7
    c: Coincident(g126,g95)
    c: InternalAlignment(g118-g125 -> g126) x8
    c: InternalAlignment(g127-g132 -> g126) x6
    c: Coincident(g133,g94)
    c: Block(g126)
    c: Block(g133)
    c: Coincident(g134,g133)
    c: Coincident(g134,g89)
    c: Vertical(g134)
    c: Horizontal(g135)
    c: Block(g135)
    c: Horizontal(g136)
    c: Equal(g88,g136) = 4.14
    c: Horizontal(g137)
    c: Equal(g136,g137) = 4.14
    c: Block(g137)
    c: Block(g136)
    c: Coincident(g138,g135)
    c: Vertical(g138)
    c: Equal(g90,g138) = 11.88
    c: Coincident(g139,g138)
    c: Horizontal(g139)
    c: Coincident(g140,g139)
    c: Vertical(g140)
    c: Equal(g91,g139) = 4.03
    c: Equal(g92,g140) = 1.9
    c: Coincident(g141,g135)
    c: Vertical(g141)
    c: Vertical(g142)
    c: Coincident(g142,g136)
    c: Equal(g93,g141) = 5.8
    c: Equal(g94,g142) = 5.8
    c: Vertical(g143)
    c: Coincident(g143,g136)
    c: Equal(g95,g143) = 6.9
    c: Coincident(g149,g140)
    c: Equal(g96,g144) = 1
    c: Equal(g144, g145-g148) x4
    c: InternalAlignment(g144-g148 -> g149) x5
    c: InternalAlignment(g150-g158 -> g149) x9
    c: Block(g149)
    c: Block(g159)
    c: Coincident(g168,g141)
    c: Equal(g118,g160) = 1
    c: Equal(g160, g161-g167) x7
    c: Coincident(g168,g143)
    c: InternalAlignment(g160-g167 -> g168) x8
    c: InternalAlignment(g169-g174 -> g168) x6
    c: Coincident(g175,g142)
    c: Block(g168)
    c: Block(g175)
    c: Coincident(g176,g175)
    c: Coincident(g176,g137)
    c: Vertical(g176)
    c: Coincident(g177,g137)
    c: Vertical(g177)
    c: Coincident(g178,g177)
    c: Coincident(g178,g159)
    c: InternalAlignment(g179,g178)
    c: InternalAlignment(g180,g178)
    c: Block(g178)
    c: Vertical(g181)
    c: Coincident(g181,g89)
    c: Block(g5)
    c: Coincident(g182,g1)
    c: Coincident(g182,g5)
    c: Horizontal(g182)
    c: Coincident(g186,g117)
    c: Weight(g183) = 1
    c: Equal(g183,g184)
    c: Equal(g183,g185)
    c: Coincident(g186,g181)
    c: InternalAlignment(g183,g186)
    c: InternalAlignment(g184,g186)
    c: InternalAlignment(g185,g186)
    c: InternalAlignment(g187,g186)
    c: InternalAlignment(g188,g186)
    c: Block(g186)
    c: InternalAlignment(g190,g189)
    c: InternalAlignment(g191,g189)
    c: Block(g189)
    c: InternalAlignment(g193,g192)
    c: InternalAlignment(g194,g192)
    c: Block(g192)
    c: Horizontal(g195)
    c: Block(g195)
    c: Coincident(g196,g195)
    c: Vertical(g196)
    c: Block(g196)
    c: Distance(g195) = 3.71244
    c: Coincident(g197,g196)
    c: Horizontal(g197)
    c: Distance(g197) = 4.1
    c: Coincident(g198,g192)
    c: Coincident(g198,g197)
    c: Vertical(g198)
    c: Block(g198)
    c: Coincident(g199,g192)
    c: Coincident(g199,g195)
    c: Vertical(g199)
    c: Block(g199)
    c: Horizontal(g200)
    c: Block(g200)
    c: Coincident(g201,g200)
    c: Vertical(g201)
    c: Block(g201)
    c: Coincident(g202,g201)
    c: Horizontal(g202)
    c: Block(g202)
    c: Coincident(g203,g202)
    c: Vertical(g203)
    c: Block(g203)
    c: Coincident(g204,g200)
    c: Vertical(g204)
    c: Block(g204)
    c: Coincident(g215,g203)
    c: Weight(g206) = 1
    c: Equal(g206, g207-g214) x8
    c: Coincident(g215,g205)
    c: InternalAlignment(g206-g214 -> g215) x9
    c: InternalAlignment(g216-g222 -> g215) x7
    c: Coincident(g233,g204)
    c: Weight(g223) = 1
    c: Equal(g223, g224-g232) x9
    c: Coincident(g233,g205)
    c: InternalAlignment(g223-g232 -> g233) x10
    c: InternalAlignment(g234-g241 -> g233) x8
    c: Vertical(g205)
    c: Block(g205)
    c: Block(g215)
    c: Block(g233)
    c: Horizontal(g242)
    c: Horizontal(g243)
    c: Block(g242)
    c: Block(g243)
    c: Vertical(g244)
    c: Block(g244)
    c: Coincident(g270,g243)
    c: Weight(g245) = 1
    c: Equal(g245, g246-g269) x24
    c: Coincident(g270,g244)
    c: InternalAlignment(g245-g269 -> g270) x25
    c: InternalAlignment(g271-g293 -> g270) x23
    c: Coincident(g305,g242)
    c: Weight(g294) = 1
    c: Equal(g294, g295-g304) x10
    c: Coincident(g305,g242)
    c: InternalAlignment(g294-g304 -> g305) x11
    c: InternalAlignment(g306-g314 -> g305) x9
    c: Block(g305)
    c: Coincident(g327,g243)
    c: Weight(g315) = 1
    c: Equal(g315, g316-g326) x11
    c: Coincident(g327,g244)
    c: InternalAlignment(g315-g326 -> g327) x12
    c: InternalAlignment(g328-g337 -> g327) x10
    c: Block(g327)
    c: Block(g270)
FEATURE [Part::Extrusion] Extrude075  label="CommodoreLogoAndText002"
  Base = -> Sketch084
  Dir = (0,0,1)
  DirMode = 2
  FaceMakerClass = Part::FaceMakerBullseye
  LengthFwd = 10
  LengthRev = 0
  Solid = true
  Symmetric = false
FEATURE [Part::FeaturePython] Clone001  label="CommodoreLogoAndTextScale001"  # Draft clone (typed FeaturePython)
  AttacherType = Attacher::AttachEngine3D
  Fuse = false
  Objects = -> [Extrude075]
  Placement = pos=(112.566,5.37,73.6) rot=(0,0,1;0rad)
  Scale = (0.62,0.62,1)
FEATURE [Part::Cut] Cut073  label="sideA005"
  Base = -> Extrude002
  Tool = -> Part__Mirroring
FEATURE [Part::Cut] Cut074  label="sideB005"
  Base = -> Extrude028
  Tool = -> Clone001
FEATURE [Sketcher::SketchObject] Sketch085
  FullyConstrained = true
  Placement = pos=(0,0,0) rot=(-1,0,0;4.71239rad)
  sketch-geometry (10):
    g0: LineSegment StartX=0 StartY=0 StartZ=0 EndX=-7 EndY=0 EndZ=0
    g1: LineSegment StartX=-7 StartY=10 StartZ=0 EndX=-6.5 EndY=10 EndZ=0
    g2: LineSegment StartX=0 StartY=10 StartZ=0 EndX=-0.5 EndY=10 EndZ=0
    g3: ArcOfCircle CenterX=-3.5 CenterY=10 CenterZ=0 NormalX=0 NormalY=0 NormalZ=1 AngleXU=0 Radius=3 StartAngle=3.14159 EndAngle=6.28319
    g4: LineSegment StartX=-7 StartY=0 StartZ=0 EndX=-10.5 EndY=0 EndZ=0
    g5: LineSegment StartX=0 StartY=0 StartZ=0 EndX=3.5 EndY=0 EndZ=0
    g6: ArcOfCircle CenterX=-10.5 CenterY=3.5 CenterZ=0 NormalX=0 NormalY=0 NormalZ=1 AngleXU=0 Radius=3.5 StartAngle=4.71239 EndAngle=6.28319
    g7: ArcOfCircle CenterX=3.5 CenterY=3.5 CenterZ=0 NormalX=0 NormalY=0 NormalZ=1 AngleXU=0 Radius=3.5 StartAngle=3.14159 EndAngle=4.71239
    g8: LineSegment StartX=-7 StartY=3.5 StartZ=0 EndX=-7 EndY=10 EndZ=0
    g9: LineSegment StartX=0 StartY=10 StartZ=0 EndX=0 EndY=3.5 EndZ=0
  constraints (26):
    c: Coincident(g0,g-1)
    c: Horizontal(g0)
    c: Distance(g0) = 7
    c: Horizontal(g1)
    c: Distance(g1) = 0.5
    c: Horizontal(g2)
    c: Distance(g2) = 0.5
    c: Coincident(g3,g1)
    c: Coincident(g3,g2)
    c: Block(g3)
    c: Coincident(g4,g0)
    c: Horizontal(g4)
    c: Distance(g4) = 3.5
    c: Coincident(g5,g0)
    c: Distance(g5) = 3.5
    c: Horizontal(g5)
    c: Coincident(g6,g4)
    c: Block(g6)
    c: Coincident(g7,g5)
    c: Block(g7)
    c: Coincident(g8,g6)
    c: Coincident(g8,g1)
    c: Vertical(g8)
    c: Coincident(g9,g2)
    c: Coincident(g9,g7)
    c: Vertical(g9)
FEATURE [Part::Extrusion] Extrude076  label="backRightCasePillarSideBracket"
  Base = -> Sketch085
  Dir = (0,-1,3e-16)
  DirMode = 2
  FaceMakerClass = Part::FaceMakerBullseye
  LengthFwd = 6.7
  LengthRev = 0
  Placement = pos=(16,11.5,0) rot=(0,0,1;0rad)
  Solid = true
  Symmetric = false
FEATURE [Sketcher::SketchObject] Sketch086
  FullyConstrained = true
  Placement = pos=(0,0,0) rot=(1,0,0;1.5708rad)
  sketch-geometry (10):
    g0: LineSegment StartX=0 StartY=0 StartZ=0 EndX=-7 EndY=0 EndZ=0
    g1: LineSegment StartX=-7 StartY=10 StartZ=0 EndX=-6.5 EndY=10 EndZ=0
    g2: LineSegment StartX=0 StartY=10 StartZ=0 EndX=-0.5 EndY=10 EndZ=0
    g3: ArcOfCircle CenterX=-3.5 CenterY=10 CenterZ=0 NormalX=0 NormalY=0 NormalZ=1 AngleXU=0 Radius=3 StartAngle=3.14159 EndAngle=6.28319
    g4: LineSegment StartX=-7 StartY=0 StartZ=0 EndX=-10.5 EndY=0 EndZ=0
    g5: LineSegment StartX=0 StartY=0 StartZ=0 EndX=3.5 EndY=0 EndZ=0
    g6: ArcOfCircle CenterX=-10.5 CenterY=3.5 CenterZ=0 NormalX=0 NormalY=0 NormalZ=1 AngleXU=0 Radius=3.5 StartAngle=4.71239 EndAngle=6.28319
    g7: ArcOfCircle CenterX=3.5 CenterY=3.5 CenterZ=0 NormalX=0 NormalY=0 NormalZ=1 AngleXU=0 Radius=3.5 StartAngle=3.14159 EndAngle=4.71239
    g8: LineSegment StartX=-7 StartY=3.5 StartZ=0 EndX=-7 EndY=10 EndZ=0
    g9: LineSegment StartX=0 StartY=10 StartZ=0 EndX=0 EndY=3.5 EndZ=0
  constraints (26):
    c: Coincident(g0,g-1)
    c: Horizontal(g0)
    c: Distance(g0) = 7
    c: Horizontal(g1)
    c: Distance(g1) = 0.5
    c: Horizontal(g2)
    c: Distance(g2) = 0.5
    c: Coincident(g3,g1)
    c: Coincident(g3,g2)
    c: Block(g3)
    c: Coincident(g4,g0)
    c: Horizontal(g4)
    c: Distance(g4) = 3.5
    c: Coincident(g5,g0)
    c: Distance(g5) = 3.5
    c: Horizontal(g5)
    c: Coincident(g6,g4)
    c: Block(g6)
    c: Coincident(g7,g5)
    c: Block(g7)
    c: Coincident(g8,g6)
    c: Coincident(g8,g1)
    c: Vertical(g8)
    c: Coincident(g9,g2)
    c: Coincident(g9,g7)
    c: Vertical(g9)
FEATURE [Part::Extrusion] Extrude077  label="backLeftCasePillarSideBracket001"
  Base = -> Sketch086
  Dir = (0,-1,3e-16)
  DirMode = 2
  FaceMakerClass = Part::FaceMakerBullseye
  LengthFwd = 6.7
  LengthRev = 0
  Placement = pos=(9,11.5,72) rot=(0,1,0;3.14159rad)
  Solid = true
  Symmetric = false
FEATURE [Sketcher::SketchObject] Sketch087
  FullyConstrained = true
  Placement = pos=(0,0,0) rot=(1,0,0;1.5708rad)
  sketch-geometry (8):
    g0: LineSegment StartX=0 StartY=4e-16 StartZ=0 EndX=-7 EndY=4e-16 EndZ=0
    g1: LineSegment StartX=-7 StartY=4e-16 StartZ=0 EndX=-10.5 EndY=4e-16 EndZ=0
    g2: LineSegment StartX=0 StartY=4e-16 StartZ=0 EndX=3.5 EndY=4e-16 EndZ=0
    g3: ArcOfCircle CenterX=-10.5 CenterY=3.5 CenterZ=0 NormalX=0 NormalY=0 NormalZ=1 AngleXU=0 Radius=3.5 StartAngle=4.71239 EndAngle=6.28319
    g4: ArcOfCircle CenterX=3.5 CenterY=3.5 CenterZ=0 NormalX=0 NormalY=0 NormalZ=1 AngleXU=0 Radius=3.5 StartAngle=3.14159 EndAngle=4.71239
    g5: ArcOfCircle CenterX=-3.5 CenterY=3.5 CenterZ=0 NormalX=0 NormalY=0 NormalZ=1 AngleXU=0 Radius=3 StartAngle=3.14159 EndAngle=6.28319
    g6: LineSegment StartX=-7 StartY=3.5 StartZ=0 EndX=-6.5 EndY=3.5 EndZ=0
    g7: LineSegment StartX=-0.5 StartY=3.5 StartZ=0 EndX=0 EndY=3.5 EndZ=0
  constraints (20):
    c: Coincident(g0,g-1)
    c: Horizontal(g0)
    c: Distance(g0) = 7
    c: Coincident(g1,g0)
    c: Horizontal(g1)
    c: Distance(g1) = 3.5
    c: Coincident(g2,g0)
    c: Distance(g2) = 3.5
    c: Horizontal(g2)
    c: Coincident(g3,g1)
    c: Block(g3)
    c: Coincident(g4,g2)
    c: Block(g4)
    c: Horizontal(g6)
    c: Coincident(g5,g6)
    c: Block(g5)
    c: Coincident(g6,g3)
    c: Coincident(g7,g5)
    c: Coincident(g7,g4)
    c: Horizontal(g7)
FEATURE [Part::Extrusion] Extrude078  label="frontBackLeftCasePillarSideBracket001"
  Base = -> Sketch087
  Dir = (0,-1,2e-16)
  DirMode = 2
  FaceMakerClass = Part::FaceMakerBullseye
  LengthFwd = 6.7
  LengthRev = 0
  Placement = pos=(93,11.5,0) rot=(0,0,1;0rad)
  Solid = true
  Symmetric = false
FEATURE [Sketcher::SketchObject] Sketch088
  FullyConstrained = true
  Placement = pos=(0,0,0) rot=(1,0,0;1.5708rad)
  sketch-geometry (8):
    g0: LineSegment StartX=0 StartY=4e-16 StartZ=0 EndX=-7 EndY=4e-16 EndZ=0
    g1: LineSegment StartX=-7 StartY=4e-16 StartZ=0 EndX=-10.5 EndY=4e-16 EndZ=0
    g2: LineSegment StartX=0 StartY=4e-16 StartZ=0 EndX=3.5 EndY=4e-16 EndZ=0
    g3: ArcOfCircle CenterX=-10.5 CenterY=3.5 CenterZ=0 NormalX=0 NormalY=0 NormalZ=1 AngleXU=0 Radius=3.5 StartAngle=4.71239 EndAngle=6.28319
    g4: ArcOfCircle CenterX=3.5 CenterY=3.5 CenterZ=0 NormalX=0 NormalY=0 NormalZ=1 AngleXU=0 Radius=3.5 StartAngle=3.14159 EndAngle=4.71239
    g5: ArcOfCircle CenterX=-3.5 CenterY=3.5 CenterZ=0 NormalX=0 NormalY=0 NormalZ=1 AngleXU=0 Radius=3 StartAngle=3.14159 EndAngle=6.28319
    g6: LineSegment StartX=-7 StartY=3.5 StartZ=0 EndX=-6.5 EndY=3.5 EndZ=0
    g7: LineSegment StartX=-0.5 StartY=3.5 StartZ=0 EndX=0 EndY=3.5 EndZ=0
  constraints (20):
    c: Coincident(g0,g-1)
    c: Horizontal(g0)
    c: Distance(g0) = 7
    c: Coincident(g1,g0)
    c: Horizontal(g1)
    c: Distance(g1) = 3.5
    c: Coincident(g2,g0)
    c: Distance(g2) = 3.5
    c: Horizontal(g2)
    c: Coincident(g3,g1)
    c: Block(g3)
    c: Coincident(g4,g2)
    c: Block(g4)
    c: Horizontal(g6)
    c: Coincident(g5,g6)
    c: Block(g5)
    c: Coincident(g6,g3)
    c: Coincident(g7,g5)
    c: Coincident(g7,g4)
    c: Horizontal(g7)
FEATURE [Part::Extrusion] Extrude079  label="frontFrontLeftCasePillarSideBracket002"
  Base = -> Sketch088
  Dir = (0,-1,2e-16)
  DirMode = 2
  FaceMakerClass = Part::FaceMakerBullseye
  LengthFwd = 2
  LengthRev = 0
  Placement = pos=(113,11.5,0) rot=(0,0,1;0rad)
  Solid = true
  Symmetric = false
FEATURE [Part::Chamfer] Chamfer
  Base = -> Extrude076
  Edges = 1 edges r=3: [Edge19]
FEATURE [Part::Chamfer] Chamfer002
  Base = -> Extrude077
  Edges = 1 edges r=3: [Edge7]
FEATURE [Part::Chamfer] Chamfer003  label="backLeftCasePillarSideBracket002"
  Base = -> Chamfer002
  Edges = 1 edges r=3.8: [Edge29]
FEATURE [Part::Chamfer] Chamfer004  label="backRightCasePillarSideBracket001"
  Base = -> Chamfer
  Edges = 1 edges r=3.8: [Edge24]
FEATURE [Sketcher::SketchObject] Sketch089
  FullyConstrained = true
  Placement = pos=(0,0,0) rot=(1,0,0;1.5708rad)
  sketch-geometry (8):
    g0: LineSegment StartX=0 StartY=4e-16 StartZ=0 EndX=-7 EndY=4e-16 EndZ=0
    g1: LineSegment StartX=-7 StartY=4e-16 StartZ=0 EndX=-10.5 EndY=4e-16 EndZ=0
    g2: LineSegment StartX=0 StartY=4e-16 StartZ=0 EndX=3.5 EndY=4e-16 EndZ=0
    g3: ArcOfCircle CenterX=-10.5 CenterY=3.5 CenterZ=0 NormalX=0 NormalY=0 NormalZ=1 AngleXU=0 Radius=3.5 StartAngle=4.71239 EndAngle=6.28319
    g4: ArcOfCircle CenterX=3.5 CenterY=3.5 CenterZ=0 NormalX=0 NormalY=0 NormalZ=1 AngleXU=0 Radius=3.5 StartAngle=3.14159 EndAngle=4.71239
    g5: ArcOfCircle CenterX=-3.5 CenterY=3.5 CenterZ=0 NormalX=0 NormalY=0 NormalZ=1 AngleXU=0 Radius=3 StartAngle=3.14159 EndAngle=6.28319
    g6: LineSegment StartX=-7 StartY=3.5 StartZ=0 EndX=-6.5 EndY=3.5 EndZ=0
    g7: LineSegment StartX=-0.5 StartY=3.5 StartZ=0 EndX=0 EndY=3.5 EndZ=0
  constraints (20):
    c: Coincident(g0,g-1)
    c: Horizontal(g0)
    c: Distance(g0) = 7
    c: Coincident(g1,g0)
    c: Horizontal(g1)
    c: Distance(g1) = 3.5
    c: Coincident(g2,g0)
    c: Distance(g2) = 3.5
    c: Horizontal(g2)
    c: Coincident(g3,g1)
    c: Block(g3)
    c: Coincident(g4,g2)
    c: Block(g4)
    c: Horizontal(g6)
    c: Coincident(g5,g6)
    c: Block(g5)
    c: Coincident(g6,g3)
    c: Coincident(g7,g5)
    c: Coincident(g7,g4)
    c: Horizontal(g7)
FEATURE [Part::Extrusion] Extrude080  label="frontBackLeftCasePillarSideBracket002"
  Base = -> Sketch089
  Dir = (0,-1,2e-16)
  DirMode = 2
  FaceMakerClass = Part::FaceMakerBullseye
  LengthFwd = 6.7
  LengthRev = 0
  Placement = pos=(86,11.5,72) rot=(0,1,0;3.14159rad)
  Solid = true
  Symmetric = false
